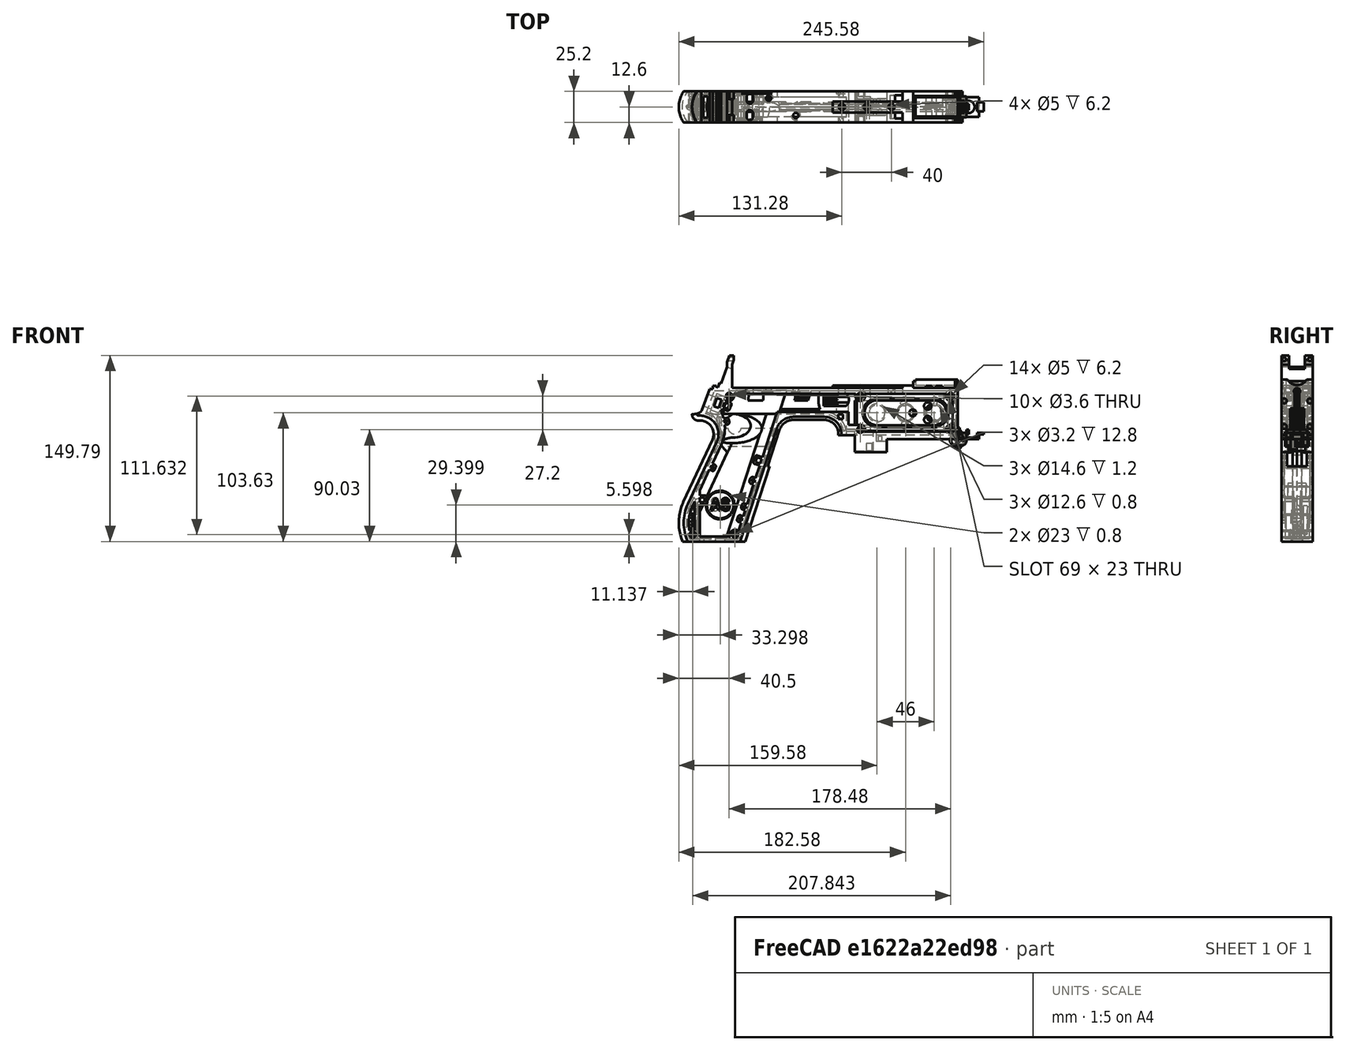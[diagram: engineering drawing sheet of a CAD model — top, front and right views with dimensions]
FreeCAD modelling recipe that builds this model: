
FCSTD DOCUMENT  (FreeCAD 1.1R20260325 (Git shallow))
Label: PICON-OF_ver_68
License: All rights reserved
LicenseURL: https://en.wikipedia.org/wiki/All_rights_reserved
objects: Sketcher::SketchObject×132, Part::Extrusion×66, Part::Cut×51, PartDesign::Pad×34, PartDesign::Pocket×21, PartDesign::Chamfer×15, PartDesign::Body×11, App::Point×11, PartDesign::Fillet×6, Part::MultiFuse×5, Part::Part2DObjectPython×4, PartDesign::SubtractivePipe×4, PartDesign::SubtractiveLoft×4, PartDesign::Plane×3, PartDesign::SubShapeBinder×2, Part::Sweep×1, PartDesign::ShapeBinder×1, Mesh::Feature×1, PartDesign::Point×1, PartDesign::Groove×1
note: 664 computed .brp shape members not serialized (recipe doc carries the construction recipe); baked Part::Feature solids carry a one-line shape summary decoded from their .brp

FEATURE [Sketcher::SketchObject] Sketch  label="corpo principale"
  ArcFitTolerance = 1e-06
  AttacherType = Attacher::AttachEngine3D
  AttachmentSupport = -> [XZ_Plane]
  ExternalTypes = [0]
  FullyConstrained = true
  MakeInternals = false
  MapMode = 5
  Placement = pos=(0,0,0) rot=(1,0,0;1.5708rad)
  _ExternalGeoVersion = 0
  sketch-geometry (65):
    g0: LineSegment StartX=0 StartY=0 StartZ=0 EndX=-57.2 EndY=0 EndZ=0
    g1: LineSegment StartX=-57.2 StartY=0 StartZ=0 EndX=-57.2 EndY=-10.4 EndZ=0
    g2: LineSegment StartX=-57.2 StartY=-10.4 StartZ=0 EndX=-82.8 EndY=-10.4 EndZ=0
    g3: LineSegment StartX=-82.8 StartY=-10.4 StartZ=0 EndX=-82.8 EndY=3.2 EndZ=0
    g4: LineSegment StartX=-82.8 StartY=3.2 StartZ=0 EndX=-93.6 EndY=3.2 EndZ=0
    g5: LineSegment StartX=-93.6 StartY=3.2 StartZ=0 EndX=-93.6 EndY=4 EndZ=0
    g6: LineSegment StartX=-107.6 StartY=18 StartZ=0 EndX=-132.428 EndY=18 EndZ=0
    g7: LineSegment StartX=-145.743 StartY=8.32624 StartZ=0 EndX=-175.232 EndY=-82.4316 EndZ=0
    g8: LineSegment StartX=-175.232 StartY=-82.4316 StartZ=0 EndX=-217.232 EndY=-82.4316 EndZ=0
    g9: LineSegment StartX=-217.232 StartY=-52.1862 StartZ=0 EndX=-193.988 EndY=-2.33927 EndZ=0
    g10: LineSegment StartX=-206.196 StartY=23.0857 StartZ=0 EndX=-199.861 EndY=40.4914 EndZ=0
    g11: LineSegment StartX=-199.861 StartY=40.4914 StartZ=0 EndX=-197.061 EndY=40.4914 EndZ=0
    g12: LineSegment StartX=-197.061 StartY=40.4914 StartZ=0 EndX=-197.061 EndY=42.8914 EndZ=0
    g13: LineSegment StartX=-197.061 StartY=42.8914 StartZ=0 EndX=-194.261 EndY=42.8914 EndZ=0
    g14: LineSegment StartX=-194.261 StartY=42.8914 StartZ=0 EndX=-194.535 EndY=42.1397 EndZ=0
    g15: LineSegment StartX=-194.535 StartY=42.1397 StartZ=0 EndX=-193.031 EndY=41.5924 EndZ=0
    g16: LineSegment StartX=-193.031 StartY=41.5924 StartZ=0 EndX=-191.663 EndY=45.3512 EndZ=0
    g17: LineSegment StartX=-191.663 StartY=45.3512 StartZ=0 EndX=-190.536 EndY=44.9408 EndZ=0
    g18: LineSegment StartX=-190.536 StartY=44.9408 StartZ=0 EndX=-185.747 EndY=58.0965 EndZ=0
    g19: LineSegment StartX=-185.747 StartY=58.0965 StartZ=0 EndX=-185.747 EndY=62.0965 EndZ=0
    g20: LineSegment StartX=-185.747 StartY=62.0965 StartZ=0 EndX=-183.832 EndY=67.3588 EndZ=0
    g21: LineSegment StartX=-183.832 StartY=67.3588 StartZ=0 EndX=-180.232 EndY=67.3588 EndZ=0
    g22: LineSegment StartX=-180.232 StartY=67.3588 StartZ=0 EndX=-180.232 EndY=63.7588 EndZ=0
    g23: LineSegment StartX=-180.232 StartY=63.7588 StartZ=0 EndX=-181.6 EndY=60 EndZ=0
    g24: LineSegment StartX=-181.6 StartY=60 StartZ=0 EndX=-181.6 EndY=41.2 EndZ=0
    g25: LineSegment StartX=-181.6 StartY=41.2 StartZ=0 EndX=-100.8 EndY=41.2 EndZ=0
    g26: LineSegment StartX=-36 StartY=43.2 StartZ=0 EndX=-36 EndY=41.2 EndZ=0
    g27: LineSegment StartX=0 StartY=48 StartZ=0 EndX=0 EndY=0 EndZ=0
    g28: LineSegment StartX=-209.901 StartY=19.85 StartZ=0 EndX=-209.901 EndY=20.1 EndZ=0
    g29: LineSegment StartX=-208.001 StartY=22 StartZ=0 EndX=-207.747 EndY=22 EndZ=0
    g30: LineSegment StartX=-207.583 StartY=19 StartZ=0 EndX=-209.051 EndY=19 EndZ=0
    g31: ArcOfCircle CenterX=-208.001 CenterY=20.1 CenterZ=0 NormalX=0 NormalY=0 NormalZ=1 AngleXU=0 Radius=1.9 StartAngle=1.5708 EndAngle=3.14159
    g32: GeomPoint [constr] X=-209.901 Y=22 Z=0
    g33: ArcOfCircle CenterX=-209.051 CenterY=19.85 CenterZ=0 NormalX=0 NormalY=0 NormalZ=1 AngleXU=0 Radius=0.85 StartAngle=3.14159 EndAngle=4.71239
    g34: GeomPoint [constr] X=-209.901 Y=19 Z=0
    g35: ArcOfCircle CenterX=-207.747 CenterY=23.65 CenterZ=0 NormalX=0 NormalY=0 NormalZ=1 AngleXU=0 Radius=1.65 StartAngle=4.71239 EndAngle=5.93412
    g36: GeomPoint [constr] X=-206.591 Y=22 Z=0
    g37: LineSegment StartX=-4 StartY=6 StartZ=0 EndX=-4 EndY=36.4 EndZ=0
    g38: LineSegment StartX=-4 StartY=36.4 StartZ=0 EndX=-185.2 EndY=36.4 EndZ=0
    g39: LineSegment StartX=-185.2 StartY=36.4 StartZ=0 EndX=-190.441 EndY=22 EndZ=0
    g40: LineSegment StartX=-214.575 StartY=-78.4316 StartZ=0 EndX=-178.142 EndY=-78.4316 EndZ=0
    g41: LineSegment StartX=-178.142 StartY=-78.4316 StartZ=0 EndX=-145.51 EndY=22 EndZ=0
    g42: LineSegment StartX=-145.51 StartY=22 StartZ=0 EndX=-87.91 EndY=22 EndZ=0
    g43: LineSegment StartX=-87.91 StartY=22 StartZ=0 EndX=-87.91 EndY=11.6 EndZ=0
    g44: LineSegment StartX=-87.91 StartY=11.6 StartZ=0 EndX=-80.11 EndY=11.6 EndZ=0
    g45: LineSegment StartX=-80.11 StartY=11.6 StartZ=0 EndX=-80.11 EndY=6 EndZ=0
    g46: LineSegment StartX=-80.11 StartY=6 StartZ=0 EndX=-4 EndY=6 EndZ=0
    g47: LineSegment StartX=-190.363 StartY=-4.02975 StartZ=0 EndX=-213.607 EndY=-53.8767 EndZ=0
    g48: ArcOfCircle CenterX=-132.428 CenterY=4 CenterZ=0 NormalX=0 NormalY=0 NormalZ=1 AngleXU=0 Radius=14 StartAngle=1.5708 EndAngle=2.82743
    g49: GeomPoint [constr] X=-142.6 Y=18 Z=0
    g50: ArcOfCircle CenterX=-107.6 CenterY=4 CenterZ=0 NormalX=0 NormalY=0 NormalZ=1 AngleXU=0 Radius=14 StartAngle=0 EndAngle=1.5708
    g51: GeomPoint [constr] X=-93.6 Y=18 Z=0
    g52: ArcOfCircle CenterX=-184.801 CenterY=-67.3089 CenterZ=0 NormalX=0 NormalY=0 NormalZ=1 AngleXU=0 Radius=35.7833 StartAngle=2.70526 EndAngle=3.57792
    g53: ArcOfCircle CenterX=-207.583 CenterY=4 CenterZ=0 NormalX=0 NormalY=0 NormalZ=1 AngleXU=0 Radius=15 StartAngle=5.84685 EndAngle=7.85398
    g54: LineSegment [constr] StartX=-213.607 StartY=-53.8767 StartZ=0 EndX=-217.232 EndY=-52.1862 EndZ=0
    g55: ArcOfCircle CenterX=-184.801 CenterY=-67.3089 CenterZ=0 NormalX=0 NormalY=0 NormalZ=1 AngleXU=0 Radius=31.7833 StartAngle=2.70526 EndAngle=3.49911
    g56: ArcOfCircle CenterX=-218.095 CenterY=8.90192 CenterZ=0 NormalX=0 NormalY=0 NormalZ=1 AngleXU=0 Radius=30.5989 StartAngle=5.84685 EndAngle=6.72553
    g57: LineSegment StartX=-44.6 StartY=43.2 StartZ=0 EndX=-36 EndY=43.2 EndZ=0
    g58: LineSegment StartX=-100.8 StartY=41.2 StartZ=0 EndX=-44.6 EndY=41.2 EndZ=0
    g59: LineSegment StartX=-44.6 StartY=41.2 StartZ=0 EndX=-44.6 EndY=43.2 EndZ=0
    g60: LineSegment StartX=-2.4 StartY=48 StartZ=0 EndX=0 EndY=48 EndZ=0
    g61: LineSegment StartX=-36 StartY=41.2 StartZ=0 EndX=-2.4 EndY=41.2 EndZ=0
    g62: LineSegment StartX=-2.4 StartY=41.2 StartZ=0 EndX=-2.4 EndY=48 EndZ=0
    g63: LineSegment [constr] StartX=-181.6 StartY=36.4 StartZ=0 EndX=-152.209 EndY=36.4 EndZ=0
    g64: LineSegment [constr] StartX=-181.6 StartY=36.4 StartZ=0 EndX=-130.41 EndY=36.4 EndZ=0
  constraints (183):
    c: Coincident(g-1,g0)
    c: PointOnObject(g0,g-1)
    c: Coincident(g0,g1)
    c: Vertical(g1)
    c: Coincident(g1,g2)
    c: Horizontal(g2)
    c: Coincident(g2,g3)
    c: Vertical(g3)
    c: Coincident(g3,g4)
    c: Coincident(g4,g5)
    c: Vertical(g5)
    c: Horizontal(g6)
    c: Coincident(g7,g8)
    c: Horizontal(g8)
    c: Coincident(g10,g11)
    c: Horizontal(g11)
    c: Coincident(g11,g12)
    c: Vertical(g12)
    c: Coincident(g12,g13)
    c: Horizontal(g13)
    c: Coincident(g13,g14)
    c: Coincident(g14,g15)
    c: Coincident(g15,g16)
    c: Coincident(g16,g17)
    c: Coincident(g17,g18)
    c: Coincident(g18,g19)
    c: Vertical(g19)
    c: Coincident(g19,g20)
    c: Coincident(g20,g21)
    c: Horizontal(g21)
    c: Coincident(g21,g22)
    c: Vertical(g22)
    c: Coincident(g22,g23)
    c: Coincident(g23,g24)
    c: Vertical(g24)
    c: Coincident(g24,g25)
    c: Horizontal(g25)
    c: Coincident(g57,g26)
    c: Vertical(g26)
    c: Coincident(g26,g61)
    c: PointOnObject(g60,g-2)
    c: Coincident(g60,g27)
    c: Coincident(g27,g0)
    c: DistanceY(g27,g27) = 48
    c: DistanceY(g1,g1) = 10.4
    c: DistanceX(g0,g0) = 57.2
    c: DistanceX(g2,g2) = 25.6
    c: Horizontal(g4)
    c: DistanceY(g3,g3) = 13.6
    c: DistanceX(g4,g4) = 10.8
    c: DistanceY(g5,g51) = 14.8
    c: DistanceX(g49,g51) = 49
    c: Distance(g7,g49) = 105.6
    c: DistanceX(g61,g60) = 36
    c: DistanceX(g25,g25) = 80.8
    c: DistanceY(g24,g24) = 18.8
    c: DistanceY(g22,g22) = 3.6
    c: Distance(g23) = 4
    c: Angle(g-1,g23) = 1.22173
    c: DistanceX(g21,g21) = 3.6
    c: Distance(g20) = 5.6
    c: Angle(g-1,g20) = 1.22173
    c: DistanceY(g19,g19) = 4
    c: Distance(g18) = 14
    c: Angle(g-1,g18) = 1.22173
    c: Distance(g17) = 1.2
    c: Distance(g16) = 4
    c: Angle(g16) = 1.22173
    c: Perpendicular(g18,g17)
    c: Distance(g15) = 1.6
    c: Perpendicular(g16,g15)
    c: Distance(g14) = 0.8
    c: DistanceX(g13,g13) = 2.8
    c: Perpendicular(g15,g14)
    c: DistanceY(g12,g12) = 2.4
    c: DistanceX(g11,g11) = 2.8
    c: Distance(g9) = 55
    c: Angle(g9,g-1) = 2.00713
    c: Horizontal(g29)
    c: Vertical(g28)
    c: Horizontal(g30)
    c: PointOnObject(g32,g29)
    c: PointOnObject(g32,g28)
    c: Tangent(g29,g31) = 1.5708
    c: Tangent(g28,g31) = 1.5708
    c: PointOnObject(g34,g28)
    c: PointOnObject(g34,g30)
    c: Tangent(g28,g33) = 1.5708
    c: Tangent(g30,g33) = 1.5708
    c: PointOnObject(g36,g29)
    c: PointOnObject(g36,g10)
    c: Tangent(g29,g35) = -1.5708
    c: Tangent(g10,g35) = -1.5708
    c: Angle(g-1,g10) = 1.22173
    c: Radius(g35) = 1.65
    c: Vertical(g37)
    c: Coincident(g37,g38)
    c: Horizontal(g38)
    c: Coincident(g38,g39)
    c: Horizontal(g40)
    c: Coincident(g40,g41)
    c: Coincident(g41,g42)
    c: Horizontal(g42)
    c: Coincident(g42,g43)
    c: Vertical(g43)
    c: Coincident(g43,g44)
    c: Horizontal(g44)
    c: Coincident(g44,g45)
    c: Vertical(g45)
    c: Coincident(g45,g46)
    c: Coincident(g46,g37)
    c: Horizontal(g46)
    c: DistanceY(g0,g37) = 6
    c: DistanceX(g37,g0) = 4
    c: DistanceY(g37,g25) = 4.8
    c: DistanceX(g38,g38) = 181.2
    c: DistanceX(g42,g42) = 57.6
    c: DistanceY(g49,g41) = 4
    c: DistanceX(g41,g49) = 2.91
    c: DistanceY(g43,g43) = 10.4
    c: DistanceX(g44,g44) = 7.8
    c: DistanceY(g7,g40) = 4
    c: Distance(g47) = 55
    c: Angle(g-1,g39) = 1.22173
    c: PointOnObject(g49,g7)
    c: PointOnObject(g49,g6)
    c: Tangent(g7,g48) = -1.5708
    c: Tangent(g6,g48) = -1.5708
    c: PointOnObject(g51,g5)
    c: PointOnObject(g51,g6)
    c: Tangent(g5,g50) = -1.5708
    c: Tangent(g6,g50) = -1.5708
    c: Radius(g50) = 14
    c: Radius(g48) = 14
    c: DistanceX(g8,g8) = 42
    c: Angle(g7,g-1) = 1.88496
    c: Parallel(g41,g7)
    c: Parallel(g47,g9)
    c: Coincident(g52,g8)
    c: Tangent(g52,g9) = 1.5708
    c: DistanceX(g9,g8) = 0
    c: Tangent(g53,g9) = -1.5708
    c: Tangent(g53,g30) = -1.5708
    c: Diameter(g53) = 30
    c: DistanceY(g53,g0) = -4
    c: Coincident(g54,g47)
    c: Distance(g54) = 4
    c: Coincident(g54,g9)
    c: Coincident(g55,g40)
    c: Tangent(g55,g47) = -1.5708
    c: Coincident(g52,g55)
    c: Coincident(g56,g39)
    c: Tangent(g56,g47) = 1.5708
    c: Horizontal(g57)
    c: DistanceX(g57,g57) = 8.6
    c: Coincident(g58,g25)
    c: Horizontal(g58)
    c: Coincident(g59,g58)
    c: Vertical(g59)
    c: DistanceY(g58,g57) = 2
    c: DistanceX(g58,g58) = 56.2
    c: Coincident(g59,g57)
    c: DistanceY(g41,g36) = 0
    c: DistanceY(g36,g39) = 0
    c: DistanceY(g28,g28) = 0.25
    c: DistanceX(g30,g36) = 2.46
    c: DistanceX(g28,g29) = 1.9
    c: Coincident(g62,g60)
    c: Horizontal(g60)
    c: DistanceX(g62,g27) = 2.4
    c: Coincident(g61,g62)
    c: DistanceY(g26,g26) = 2
    c: Vertical(g62)
    c: DistanceY(g61,g60) = 6.8
    c: Horizontal(g61)
    c: Distance(g63) = 29.391
    c: PointOnObject(g63,g38)
    c: PointOnObject(g63,g38)
    c: Distance(g64) = 51.19
    c: PointOnObject(g64,g38)
    c: PointOnObject(g64,g38)
    c: DistanceX(g24,g63) = 0
    c: DistanceX(g24,g64) = 0
FEATURE [Part::Extrusion] Extrude  label="Extrude corpo principale"
  Base = -> Sketch
  Dir = (0,-1,2e-16)
  DirMode = 2
  FaceMakerClass = Part::FaceMakerBullseye
  FaceMakerMode = 3
  InnerWireTaper = 1
  LengthFwd = 25.2
  LengthRev = 12.6
  Solid = true
  Symmetric = true
FEATURE [Sketcher::SketchObject] Sketch002  label="scavo grilletto"
  ArcFitTolerance = 1e-06
  AttachmentSupport = -> [XZ_Plane]
  ExternalGeometry = -> [Sketch]
  ExternalTypes = [0]
  FullyConstrained = true
  MakeInternals = false
  MapMode = 5
  Placement = pos=(0,0,0) rot=(1,0,0;1.5708rad)
  _ExternalGeoVersion = 0
  sketch-geometry (4):
    g0: LineSegment StartX=-89.51 StartY=22 StartZ=0 EndX=-152.71 EndY=22 EndZ=0
    g1: LineSegment StartX=-152.71 StartY=22 StartZ=0 EndX=-167.006 EndY=-22 EndZ=0
    g2: LineSegment StartX=-167.006 StartY=-22 StartZ=0 EndX=-89.51 EndY=-22 EndZ=0
    g3: LineSegment StartX=-89.51 StartY=-22 StartZ=0 EndX=-89.51 EndY=22 EndZ=0
  constraints (12):
    c: Horizontal(g0)
    c: Coincident(g0,g1)
    c: Coincident(g1,g2)
    c: Horizontal(g2)
    c: Coincident(g2,g3)
    c: Coincident(g3,g0)
    c: Vertical(g3)
    c: Angle(g1,g0) = 1.88496
    c: DistanceY(g3,g3) = 44
    c: DistanceX(g0,g0) = 63.2
    c: DistanceX(g0,g-3) = 1.6
    c: DistanceY(g-3,g0) = 0
FEATURE [Sketcher::SketchObject] Sketch004  label="traiettoria arrotondamento impugnatura anteriore"
  ArcFitTolerance = 1e-06
  AttachmentSupport = -> [XZ_Plane]
  ExternalGeometry = -> [Sketch]
  ExternalTypes = [0]
  FullyConstrained = true
  MakeInternals = false
  MapMode = 5
  Placement = pos=(0,0,0) rot=(1,0,0;1.5708rad)
  _ExternalGeoVersion = 0
  sketch-geometry (13):
    g0: LineSegment StartX=-175.232 StartY=-82.4316 StartZ=0 EndX=-145.743 EndY=8.32624 EndZ=0
    g1: LineSegment StartX=-93.6 StartY=3.2 StartZ=0 EndX=-93.6 EndY=4 EndZ=0
    g2: LineSegment StartX=-132.428 StartY=18 StartZ=0 EndX=-107.6 EndY=18 EndZ=0
    g3: ArcOfCircle CenterX=-132.428 CenterY=4 CenterZ=0 NormalX=0 NormalY=0 NormalZ=1 AngleXU=0 Radius=14 StartAngle=1.5708 EndAngle=2.82743
    g4: ArcOfCircle CenterX=-107.6 CenterY=4 CenterZ=0 NormalX=0 NormalY=0 NormalZ=1 AngleXU=0 Radius=14 StartAngle=0 EndAngle=1.5708
    g5: LineSegment StartX=-175.232 StartY=-82.4316 StartZ=0 EndX=-217.232 EndY=-82.4316 EndZ=0
    g6: LineSegment StartX=-217.232 StartY=-52.1862 StartZ=0 EndX=-193.988 EndY=-2.33927 EndZ=0
    g7: LineSegment StartX=-209.051 StartY=19 StartZ=0 EndX=-207.583 EndY=19 EndZ=0
    g8: LineSegment StartX=-209.901 StartY=20.1 StartZ=0 EndX=-209.901 EndY=19.85 EndZ=0
    g9: ArcOfCircle CenterX=-184.801 CenterY=-67.3089 CenterZ=0 NormalX=0 NormalY=0 NormalZ=1 AngleXU=0 Radius=35.7833 StartAngle=2.70526 EndAngle=3.57792
    g10: ArcOfCircle CenterX=-207.583 CenterY=4 CenterZ=0 NormalX=0 NormalY=0 NormalZ=1 AngleXU=0 Radius=15 StartAngle=5.84685 EndAngle=7.85398
    g11: ArcOfCircle CenterX=-209.051 CenterY=19.85 CenterZ=0 NormalX=0 NormalY=0 NormalZ=1 AngleXU=0 Radius=0.85 StartAngle=3.14159 EndAngle=4.71239
    g12: ArcOfCircle CenterX=-208.001 CenterY=20.1 CenterZ=0 NormalX=0 NormalY=0 NormalZ=1 AngleXU=0 Radius=1.9 StartAngle=1.5708 EndAngle=3.14159
  constraints (26):
    c: Coincident(g0,g-3)
    c: Coincident(g0,g-6)
    c: Coincident(g1,g-8)
    c: Coincident(g1,g-7)
    c: Coincident(g2,g-5)
    c: Coincident(g2,g-4)
    c: Coincident(g3,g2)
    c: Tangent(g3,g0) = 1.5708
    c: Coincident(g4,g1)
    c: Tangent(g4,g2) = 1.5708
    c: Coincident(g5,g0)
    c: Coincident(g5,g-9)
    c: Coincident(g6,g-12)
    c: Coincident(g6,g-11)
    c: Coincident(g7,g-15)
    c: Coincident(g7,g-14)
    c: Coincident(g8,g-16)
    c: Coincident(g8,g-17)
    c: Tangent(g9,g6) = 1.5708
    c: Coincident(g9,g5)
    c: Coincident(g10,g7)
    c: Tangent(g10,g6) = -1.5708
    c: Tangent(g11,g7) = -1.5708
    c: Coincident(g11,g8)
    c: Tangent(g12,g8) = -1.5708
    c: Coincident(g12,g-17)
FEATURE [PartDesign::Plane] DatumPlane  label="Piano per disegno arrotondamento impugnatura"
  AttachmentSupport = -> [Sketch]
  Length = 73.6581
  MapMode = 7
  Placement = pos=(-145.743,1.8e-15,8.32624) rot=(0.154555,0.154555,0.97582;1.59527rad)
  ResizeMode = 0
  Width = 303.511
FEATURE [Sketcher::SketchObject] Sketch005  label="forma arrotondamento impugnatura anteriore"
  ArcFitTolerance = 1e-06
  AttachmentSupport = -> [DatumPlane]
  ExternalTypes = [0]
  FullyConstrained = true
  MakeInternals = false
  MapMode = 5
  Placement = pos=(-145.743,1.8e-15,8.32624) rot=(0.154555,0.154555,0.97582;1.59527rad)
  _ExternalGeoVersion = 0
  sketch-geometry (5):
    g0: GeomPoint [constr] X=0 Y=-4 Z=0
    g1: GeomPoint [constr] X=-12.6 Y=7.1e-15 Z=0
    g2: GeomPoint [constr] X=12.6 Y=4.97e-14 Z=0
    g3: LineSegment StartX=-12.6 StartY=7.1e-15 StartZ=0 EndX=12.6 EndY=4.97e-14 EndZ=0
    g4: ArcOfCircle CenterX=-3.88e-14 CenterY=17.845 CenterZ=0 NormalX=0 NormalY=0 NormalZ=1 AngleXU=0 Radius=21.845 StartAngle=4.09759 EndAngle=5.32718
  constraints (11):
    c: DistanceY(g0,g-1) = 4
    c: DistanceX(g-1,g0) = 0
    c: DistanceX(g1,g-1) = 12.6
    c: DistanceX(g-1,g2) = 12.6
    c: DistanceY(g-1,g2) = 0
    c: DistanceY(g-1,g1) = 0
    c: Coincident(g3,g1)
    c: Coincident(g3,g2)
    c: Coincident(g4,g1)
    c: Coincident(g4,g2)
    c: PointOnObject(g0,g4)
FEATURE [Part::Sweep] Sweep  label="Sweep impugnatura"
  Frenet = true
  Sections = -> [Sketch005]
  Solid = true
  Spine = -> Sketch [Edge32,Edge33,Edge34,Edge35,Edge36,Edge37,Edge38,Edge39,Edge40,Edge41,Edge42,Edge43,Edge44]
  Transition = 1
FEATURE [Sketcher::SketchObject] Sketch008  label="buchi e pulizie varie"
  ArcFitTolerance = 1e-06
  AttachmentSupport = -> [XZ_Plane]
  ExternalGeometry = -> [Sketch]
  ExternalTypes = [0]
  FullyConstrained = true
  MakeInternals = false
  MapMode = 5
  Placement = pos=(0,0,0) rot=(1,0,0;1.5708rad)
  _ExternalGeoVersion = 0
  sketch-geometry (26):
    g0: LineSegment StartX=-96.278 StartY=20.155 StartZ=0 EndX=-92.278 EndY=20.155 EndZ=0
    g1: LineSegment StartX=-92.278 StartY=20.155 StartZ=0 EndX=-92.278 EndY=16.155 EndZ=0
    g2: LineSegment StartX=-92.278 StartY=16.155 StartZ=0 EndX=-96.278 EndY=16.155 EndZ=0
    g3: LineSegment StartX=-96.278 StartY=16.155 StartZ=0 EndX=-96.278 EndY=20.155 EndZ=0
    g4: LineSegment StartX=-222.232 StartY=-82.4316 StartZ=0 EndX=-170.232 EndY=-82.4316 EndZ=0
    g5: LineSegment StartX=-170.232 StartY=-82.4316 StartZ=0 EndX=-170.232 EndY=-86.4316 EndZ=0
    g6: LineSegment StartX=-170.232 StartY=-86.4316 StartZ=0 EndX=-222.232 EndY=-86.4316 EndZ=0
    g7: LineSegment StartX=-222.232 StartY=-86.4316 StartZ=0 EndX=-222.232 EndY=-82.4316 EndZ=0
    g8: LineSegment StartX=-213.901 StartY=20.1 StartZ=0 EndX=-213.901 EndY=26 EndZ=0
    g9: LineSegment StartX=-213.901 StartY=26 StartZ=0 EndX=-206.196 EndY=26 EndZ=0
    g10: LineSegment StartX=-17.4 StartY=42.8 StartZ=0 EndX=-12.4 EndY=42.8 EndZ=0
    g11: LineSegment StartX=-12.4 StartY=42.8 StartZ=0 EndX=-12.4 EndY=41.2 EndZ=0
    g12: LineSegment StartX=-12.4 StartY=41.2 StartZ=0 EndX=-17.4 EndY=41.2 EndZ=0
    g13: LineSegment StartX=-17.4 StartY=41.2 StartZ=0 EndX=-17.4 EndY=42.8 EndZ=0
    g14: LineSegment StartX=-25.9 StartY=42.8 StartZ=0 EndX=-20.9 EndY=42.8 EndZ=0
    g15: LineSegment StartX=-20.9 StartY=42.8 StartZ=0 EndX=-20.9 EndY=41.2 EndZ=0
    g16: LineSegment StartX=-20.9 StartY=41.2 StartZ=0 EndX=-25.9 EndY=41.2 EndZ=0
    g17: LineSegment StartX=-25.9 StartY=41.2 StartZ=0 EndX=-25.9 EndY=42.8 EndZ=0
    g18: GeomPoint [constr] X=-206.196 Y=23.0857 Z=0
    g19: GeomPoint [constr] X=-213.901 Y=20.1 Z=0
    g20: BSplineCurve PolesCount=4 KnotsCount=2 Degree=3 IsPeriodic=0
    g21-g24: Circle [constr] x4 (B-spline internal-alignment scaffolding for g20; pole/knot coordinates omitted)
    g25: LineSegment StartX=-206.196 StartY=26 StartZ=0 EndX=-206.196 EndY=23.0857 EndZ=0
  constraints (73):
    c: Horizontal(g0)
    c: Coincident(g1,g0)
    c: Vertical(g1)
    c: Coincident(g2,g1)
    c: Horizontal(g2)
    c: Coincident(g3,g2)
    c: Coincident(g3,g0)
    c: Vertical(g3)
    c: DistanceX(g0,g-4) = 4.368
    c: DistanceY(g0,g-4) = 1.845
    c: DistanceY(g1,g1) = 4
    c: DistanceX(g2,g2) = 4
    c: Horizontal(g4)
    c: Coincident(g5,g4)
    c: Vertical(g5)
    c: Coincident(g6,g5)
    c: Horizontal(g6)
    c: Coincident(g7,g6)
    c: Coincident(g7,g4)
    c: Vertical(g7)
    c: DistanceY(g7,g7) = 4
    c: DistanceX(g4,g-5) = 5
    c: DistanceX(g-5,g4) = 5
    c: DistanceY(g4,g-5) = 0
    c: Coincident(g9,g8)
    c: Parallel(g9,g-6)
    c: DistanceX(g8,g-8) = 4
    c: Horizontal(g10)
    c: Coincident(g11,g10)
    c: Vertical(g11)
    c: Coincident(g12,g11)
    c: Horizontal(g12)
    c: Coincident(g13,g12)
    c: Coincident(g13,g10)
    c: Vertical(g13)
    c: Horizontal(g14)
    c: Coincident(g15,g14)
    c: Vertical(g15)
    c: Coincident(g16,g15)
    c: Horizontal(g16)
    c: Coincident(g17,g16)
    c: Coincident(g17,g14)
    c: Vertical(g17)
    c: DistanceY(g11,g10) = 1.6
    c: DistanceX(g10,g10) = 5
    c: DistanceY(g15,g14) = 1.6
    c: DistanceX(g14,g14) = 5
    c: DistanceX(g15,g12) = 3.5
    c: DistanceX(g11,g-9) = 10
    c: DistanceY(g-9,g11) = 0
    c: DistanceY(g-9,g15) = 0
    c: Perpendicular(g8,g9)
    c: DistanceY(g-7,g9) = 4
    c: DistanceY(g8,g-8) = 0
    c: InternalAlignment(g18,g20)
    c: InternalAlignment(g19,g20)
    c: InternalAlignment(g21,g20)
    c: Weight(g21) = 1
    c: InternalAlignment(g22,g20)
    c: Equal(g22,g21)
    c: InternalAlignment(g23,g20)
    c: Equal(g23,g21)
    c: InternalAlignment(g24,g20)
    c: Equal(g24,g21)
    c: Coincident(g18,g-12)
    c: Coincident(g19,g8)
    c: Coincident(g25,g9)
    c: Coincident(g25,g20)
    c: Vertical(g25)
    c: DistanceY(g20,g23) = 0
    c: DistanceY(g22,g18) = 2.26
    c: DistanceX(g22,g18) = 0.93
    c: DistanceX(g20,g23) = 2.9
FEATURE [Part::Extrusion] Extrude004  label="Extrude Buchi e pulizie varie"
  Base = -> Sketch008
  Dir = (0,-1,2e-16)
  DirMode = 2
  FaceMakerClass = Part::FaceMakerBullseye
  FaceMakerMode = 3
  InnerWireTaper = 1
  LengthFwd = 25.2
  LengthRev = 0
  Solid = true
  Symmetric = true
FEATURE [Sketcher::SketchObject] Sketch009  label="rinforzi"
  ArcFitTolerance = 1e-06
  AttachmentSupport = -> [XZ_Plane]
  ExternalGeometry = -> [Sketch]
  ExternalTypes = [0]
  FullyConstrained = true
  MakeInternals = false
  MapMode = 5
  Placement = pos=(0,0,0) rot=(1,0,0;1.5708rad)
  _ExternalGeoVersion = 0
  sketch-geometry (9):
    g0: LineSegment StartX=-87.91 StartY=22 StartZ=0 EndX=-87.91 EndY=36.4 EndZ=0
    g1: LineSegment StartX=-87.91 StartY=36.4 StartZ=0 EndX=-97.91 EndY=36.4 EndZ=0
    g2: LineSegment StartX=-97.91 StartY=36.4 StartZ=0 EndX=-97.91 EndY=22 EndZ=0
    g3: LineSegment StartX=-97.91 StartY=22 StartZ=0 EndX=-87.91 EndY=22 EndZ=0
    g4: LineSegment StartX=-149.713 StartY=9.06563 StartZ=0 EndX=-154.586 EndY=-5.93437 EndZ=0
    g5: LineSegment StartX=-154.586 StartY=-5.93437 StartZ=0 EndX=-191.863 EndY=-5.93437 EndZ=0
    g6: LineSegment StartX=-191.863 StartY=-5.93437 StartZ=0 EndX=-191.863 EndY=9.06563 EndZ=0
    g7: LineSegment StartX=-191.863 StartY=9.06563 StartZ=0 EndX=-149.713 EndY=9.06563 EndZ=0
    g8: LineSegment [constr] StartX=-145.51 StartY=22 StartZ=0 EndX=-149.713 EndY=9.06563 EndZ=0
  constraints (25):
    c: Vertical(g0)
    c: Coincident(g1,g0)
    c: Horizontal(g1)
    c: Coincident(g2,g1)
    c: Vertical(g2)
    c: Coincident(g3,g2)
    c: Coincident(g3,g0)
    c: Horizontal(g3)
    c: Coincident(g0,g-4)
    c: DistanceX(g3,g3) = 10
    c: DistanceY(g0,g-3) = 0
    c: Coincident(g5,g4)
    c: Horizontal(g5)
    c: Coincident(g6,g5)
    c: Vertical(g6)
    c: Coincident(g7,g6)
    c: Coincident(g7,g4)
    c: Horizontal(g7)
    c: Distance(g8) = 13.6
    c: Parallel(g-6,g8)
    c: Coincident(g-6,g8)
    c: Parallel(g4,g-6)
    c: DistanceY(g4,g4) = 15
    c: Coincident(g4,g8)
    c: DistanceX(g-5,g5) = -1.5
FEATURE [Part::Extrusion] Extrude001  label="Extrude scavo grilletto"
  Base = -> Sketch002
  Dir = (0,-1,2e-16)
  DirMode = 2
  FaceMakerClass = Part::FaceMakerBullseye
  FaceMakerMode = 3
  InnerWireTaper = 1
  LengthFwd = 16
  LengthRev = 0
  Solid = true
  Symmetric = true
FEATURE [Part::Extrusion] Extrude005  label="Extrude Rinforzi"
  Base = -> Sketch009
  Dir = (0,-1,2e-16)
  DirMode = 2
  FaceMakerClass = Part::FaceMakerBullseye
  FaceMakerMode = 3
  InnerWireTaper = 1
  LengthFwd = 2
  LengthRev = 0
  Placement = pos=(0,12.6,0) rot=(0,0,1;0rad)
  Solid = true
  Symmetric = false
FEATURE [PartDesign::ShapeBinder] CopyCut
  TraceSupport = false
FEATURE [PartDesign::Plane] DatumPlane001
  AttachmentSupport = -> [CopyCut]
  Length = 283.944
  MapMode = 5
  Placement = pos=(0,12.6,0) rot=(0,0.707107,0.707107;3.14159rad)
  ResizeMode = 0
  Width = 188.15
FEATURE [Sketcher::SketchObject] Sketch010  label="buco neopixel"
  ArcFitTolerance = 1e-06
  AttachmentSupport = -> [XZ_Plane]
  ExternalGeometry = -> [Sketch]
  ExternalTypes = [0]
  FullyConstrained = true
  MakeInternals = false
  MapMode = 5
  Placement = pos=(0,0,0) rot=(1,0,0;1.5708rad)
  _ExternalGeoVersion = 0
  sketch-geometry (5):
    g0: LineSegment [constr] StartX=-199.861 StartY=40.4914 StartZ=0 EndX=-201.368 EndY=36.3521 EndZ=0
    g1: LineSegment StartX=-201.368 StartY=36.3521 StartZ=0 EndX=-204.932 EndY=26.5605 EndZ=0
    g2: LineSegment StartX=-201.368 StartY=36.3521 StartZ=0 EndX=-180.2 EndY=28.6477 EndZ=0
    g3: LineSegment StartX=-180.2 StartY=28.6477 StartZ=0 EndX=-183.764 EndY=18.8561 EndZ=0
    g4: LineSegment StartX=-183.764 StartY=18.8561 StartZ=0 EndX=-204.932 EndY=26.5605 EndZ=0
  constraints (14):
    c: Parallel(g0,g-3)
    c: Distance(g0) = 4.405
    c: Coincident(g0,g-3)
    c: Coincident(g2,g1)
    c: Coincident(g3,g2)
    c: Coincident(g4,g3)
    c: Coincident(g4,g1)
    c: Parallel(g1,g-3)
    c: Distance(g1) = 10.42
    c: Coincident(g1,g0)
    c: Parallel(g2,g4)
    c: Perpendicular(g1,g2)
    c: DistanceX(g-4,g2) = 5
    c: Parallel(g3,g1)
FEATURE [Part::Extrusion] Extrude006  label="Extrude buco neopixel"
  Base = -> Sketch010
  Dir = (0,-1,2e-16)
  DirMode = 2
  FaceMakerClass = Part::FaceMakerBullseye
  FaceMakerMode = 3
  InnerWireTaper = 1
  LengthFwd = 17.2
  LengthRev = 0
  Solid = true
  Symmetric = true
FEATURE [Sketcher::SketchObject] Sketch011  label="fermo grilletto"
  ArcFitTolerance = 1e-06
  AttachmentSupport = -> [XZ_Plane]
  ExternalGeometry = -> [Sketch]
  ExternalTypes = [0]
  FullyConstrained = true
  MakeInternals = false
  MapMode = 5
  Placement = pos=(0,0,0) rot=(1,0,0;1.5708rad)
  _ExternalGeoVersion = 0
  sketch-geometry (18):
    g0: LineSegment [constr] StartX=-145.51 StartY=22 StartZ=0 EndX=-157.347 EndY=-14.4293 EndZ=0
    g1: LineSegment [constr] StartX=-157.347 StartY=-14.4293 StartZ=0 EndX=-157.841 EndY=-15.951 EndZ=0
    g2: LineSegment StartX=-161.151 StartY=-13.1932 StartZ=0 EndX=-155.825 EndY=-14.9237 EndZ=0
    g3: LineSegment StartX=-163.167 StartY=-14.2205 StartZ=0 EndX=-164.403 EndY=-18.0247 EndZ=0
    g4: LineSegment StartX=-163.376 StartY=-20.0408 StartZ=0 EndX=-158.05 EndY=-21.7713 EndZ=0
    g5: LineSegment StartX=-158.05 StartY=-21.7713 StartZ=0 EndX=-155.825 EndY=-14.9237 EndZ=0
    g6: LineSegment StartX=-161.645 StartY=-14.7149 StartZ=0 EndX=-157.841 EndY=-15.951 EndZ=0
    g7: LineSegment StartX=-157.841 StartY=-15.951 StartZ=0 EndX=-159.077 EndY=-19.7552 EndZ=0
    g8: LineSegment StartX=-159.077 StartY=-19.7552 StartZ=0 EndX=-162.881 EndY=-18.5191 EndZ=0
    g9: LineSegment StartX=-162.881 StartY=-18.5191 StartZ=0 EndX=-161.645 EndY=-14.7149 EndZ=0
    g10: LineSegment [constr] StartX=-161.645 StartY=-14.7149 StartZ=0 EndX=-161.151 EndY=-13.1932 EndZ=0
    g11: LineSegment [constr] StartX=-159.077 StartY=-19.7552 StartZ=0 EndX=-157.555 EndY=-20.2496 EndZ=0
    g12: LineSegment [constr] StartX=-159.077 StartY=-19.7552 StartZ=0 EndX=-159.572 EndY=-21.2769 EndZ=0
    g13: LineSegment [constr] StartX=-161.645 StartY=-14.7149 StartZ=0 EndX=-163.167 EndY=-14.2205 EndZ=0
    g14: ArcOfCircle CenterX=-161.645 CenterY=-14.7149 CenterZ=0 NormalX=0 NormalY=0 NormalZ=1 AngleXU=0 Radius=1.6 StartAngle=1.25664 EndAngle=2.82743
    g15: GeomPoint [constr] X=-162.673 Y=-12.6988 Z=0
    g16: ArcOfCircle CenterX=-162.881 CenterY=-18.5191 CenterZ=0 NormalX=0 NormalY=0 NormalZ=1 AngleXU=0 Radius=1.6 StartAngle=2.82743 EndAngle=4.39823
    g17: GeomPoint [constr] X=-164.897 Y=-19.5464 Z=0
  constraints (48):
    c: Parallel(g0,g-3)
    c: Distance(g0) = 38.304
    c: Coincident(g0,g-3)
    c: Parallel(g1,g-3)
    c: Distance(g1) = 1.6
    c: Coincident(g1,g0)
    c: Coincident(g5,g4)
    c: Coincident(g5,g2)
    c: Coincident(g7,g6)
    c: Coincident(g8,g7)
    c: Coincident(g9,g8)
    c: Coincident(g9,g6)
    c: Parallel(g7,g-3)
    c: Parallel(g9,g7)
    c: Perpendicular(g6,g7)
    c: Parallel(g6,g8)
    c: Distance(g6) = 4
    c: Distance(g9) = 4
    c: Parallel(g5,g7)
    c: Parallel(g9,g3)
    c: Parallel(g2,g6)
    c: Parallel(g4,g8)
    c: Parallel(g13,g6)
    c: Parallel(g10,g9)
    c: Parallel(g11,g8)
    c: Parallel(g12,g7)
    c: Distance(g10) = 1.6
    c: Distance(g13) = 1.6
    c: Distance(g12) = 1.6
    c: Distance(g11) = 1.6
    c: Coincident(g10,g6)
    c: Coincident(g13,g6)
    c: Coincident(g12,g7)
    c: Coincident(g11,g7)
    c: Distance(g10,g15) = 1.6
    c: Distance(g15,g13) = 1.6
    c: Distance(g4,g12) = 1.6
    c: Distance(g4,g11) = 1.6
    c: PointOnObject(g15,g2)
    c: Tangent(g3,g14) = -1.5708
    c: Tangent(g2,g14) = 1.5708
    c: PointOnObject(g17,g4)
    c: PointOnObject(g17,g3)
    c: Tangent(g4,g16) = -1.5708
    c: Tangent(g3,g16) = -1.5708
    c: Equal(g16,g14)
    c: Coincident(g16,g8)
    c: Coincident(g6,g1)
FEATURE [Part::Extrusion] Extrude007  label="Extrude fermo grilletto"
  Base = -> Sketch011
  Dir = (0,-1,2e-16)
  DirMode = 2
  FaceMakerClass = Part::FaceMakerBullseye
  FaceMakerMode = 3
  InnerWireTaper = 1
  LengthFwd = 25.2
  LengthRev = 0
  Solid = true
  Symmetric = true
FEATURE [Sketcher::SketchObject] Sketch012  label="buco oled"
  ArcFitTolerance = 1e-06
  AttachmentSupport = -> [XZ_Plane]
  ExternalGeometry = -> [Sketch]
  ExternalTypes = [0]
  FullyConstrained = true
  MakeInternals = false
  MapMode = 5
  Placement = pos=(0,0,0) rot=(1,0,0;1.5708rad)
  _ExternalGeoVersion = 0
  sketch-geometry (4):
    g0: LineSegment StartX=-185.747 StartY=58.0965 StartZ=0 EndX=-180.232 EndY=56.0891 EndZ=0
    g1: LineSegment StartX=-185.747 StartY=58.0965 StartZ=0 EndX=-185.747 EndY=67.3588 EndZ=0
    g2: LineSegment StartX=-185.747 StartY=67.3588 StartZ=0 EndX=-180.232 EndY=67.3588 EndZ=0
    g3: LineSegment StartX=-180.232 StartY=67.3588 StartZ=0 EndX=-180.232 EndY=56.0891 EndZ=0
  constraints (10):
    c: Coincident(g1,g0)
    c: Coincident(g2,g1)
    c: Coincident(g3,g2)
    c: Coincident(g3,g0)
    c: Parallel(g1,g-5)
    c: Perpendicular(g-3,g0)
    c: Parallel(g2,g-6)
    c: Parallel(g3,g-4)
    c: Coincident(g0,g-5)
    c: Coincident(g2,g-6)
FEATURE [Part::Extrusion] Extrude008  label="Extrude buco oled"
  Base = -> Sketch012
  Dir = (0,-1,2e-16)
  DirMode = 2
  FaceMakerClass = Part::FaceMakerBullseye
  FaceMakerMode = 3
  InnerWireTaper = 1
  LengthFwd = 12.8
  LengthRev = 0
  Solid = true
  Symmetric = true
FEATURE [Sketcher::SketchObject] Sketch013  label="buco pompa"
  ArcFitTolerance = 1e-06
  AttachmentSupport = -> [XZ_Plane]
  ExternalGeometry = -> [Sketch]
  ExternalTypes = [0]
  FullyConstrained = true
  MakeInternals = false
  MapMode = 5
  Placement = pos=(0,0,0) rot=(1,0,0;1.5708rad)
  _ExternalGeoVersion = 0
  sketch-geometry (8):
    g0: LineSegment StartX=-82.8 StartY=-10.4 StartZ=0 EndX=-82.8 EndY=-9.6 EndZ=0
    g1: LineSegment StartX=-82.8 StartY=-9.6 StartZ=0 EndX=-67.9 EndY=-9.6 EndZ=0
    g2: LineSegment StartX=-67.9 StartY=-9.6 StartZ=0 EndX=-67.9 EndY=6 EndZ=0
    g3: LineSegment StartX=-67.9 StartY=6 StartZ=0 EndX=-65.9 EndY=6 EndZ=0
    g4: LineSegment StartX=-65.9 StartY=6 StartZ=0 EndX=-65.9 EndY=-1.7 EndZ=0
    g5: LineSegment StartX=-65.9 StartY=-1.7 StartZ=0 EndX=-57.2 EndY=-1.7 EndZ=0
    g6: LineSegment StartX=-57.2 StartY=-1.7 StartZ=0 EndX=-57.2 EndY=-10.4 EndZ=0
    g7: LineSegment StartX=-57.2 StartY=-10.4 StartZ=0 EndX=-82.8 EndY=-10.4 EndZ=0
  constraints (22):
    c: Vertical(g0)
    c: Coincident(g1,g0)
    c: Horizontal(g1)
    c: Coincident(g2,g1)
    c: Vertical(g2)
    c: Coincident(g3,g2)
    c: Horizontal(g3)
    c: Coincident(g4,g3)
    c: Vertical(g4)
    c: Coincident(g5,g4)
    c: Horizontal(g5)
    c: Coincident(g6,g5)
    c: Vertical(g6)
    c: Coincident(g7,g6)
    c: Coincident(g7,g0)
    c: DistanceY(g0,g0) = 0.8
    c: DistanceY(g6,g6) = 8.7
    c: DistanceX(g1,g1) = 14.9
    c: DistanceX(g3,g3) = 2
    c: Coincident(g0,g-4)
    c: DistanceY(g2,g-6) = 0
    c: Coincident(g6,g-5)
FEATURE [Part::Extrusion] Extrude009  label="Extrude buco pompa"
  Base = -> Sketch013
  Dir = (0,-1,2e-16)
  DirMode = 2
  FaceMakerClass = Part::FaceMakerBullseye
  FaceMakerMode = 3
  InnerWireTaper = 1
  LengthFwd = 13.2
  LengthRev = 0
  Solid = true
  Symmetric = true
FEATURE [Sketcher::SketchObject] Sketch014  label="buco frontale"
  ArcFitTolerance = 1e-06
  AttachmentSupport = -> [XZ_Plane]
  ExternalGeometry = -> [Sketch]
  ExternalTypes = [0]
  FullyConstrained = true
  MakeInternals = false
  MapMode = 5
  Placement = pos=(0,0,0) rot=(1,0,0;1.5708rad)
  _ExternalGeoVersion = 0
  sketch-geometry (10):
    g0: LineSegment StartX=0 StartY=0 StartZ=0 EndX=0 EndY=24.671 EndZ=0
    g1: LineSegment StartX=0 StartY=24.671 StartZ=0 EndX=-4 EndY=24.671 EndZ=0
    g2: LineSegment StartX=-4 StartY=24.671 StartZ=0 EndX=-4 EndY=16 EndZ=0
    g3: LineSegment StartX=-4 StartY=16 StartZ=0 EndX=-2.4 EndY=16 EndZ=0
    g4: LineSegment StartX=-2.4 StartY=16 StartZ=0 EndX=-2.4 EndY=10 EndZ=0
    g5: LineSegment StartX=-2.4 StartY=10 StartZ=0 EndX=-12 EndY=10 EndZ=0
    g6: LineSegment StartX=-12 StartY=10 StartZ=0 EndX=-12 EndY=6 EndZ=0
    g7: LineSegment StartX=-12 StartY=6 StartZ=0 EndX=-2.4 EndY=6 EndZ=0
    g8: LineSegment StartX=-2.4 StartY=6 StartZ=0 EndX=-2.4 EndY=0 EndZ=0
    g9: LineSegment StartX=-2.4 StartY=0 StartZ=0 EndX=0 EndY=0 EndZ=0
  constraints (29):
    c: Vertical(g0)
    c: Coincident(g1,g0)
    c: Horizontal(g1)
    c: Coincident(g2,g1)
    c: Vertical(g2)
    c: Coincident(g3,g2)
    c: Horizontal(g3)
    c: Coincident(g4,g3)
    c: Vertical(g4)
    c: Coincident(g5,g4)
    c: Horizontal(g5)
    c: Coincident(g6,g5)
    c: Vertical(g6)
    c: Coincident(g7,g6)
    c: Coincident(g8,g7)
    c: Vertical(g8)
    c: Coincident(g9,g8)
    c: Coincident(g9,g0)
    c: Horizontal(g9)
    c: DistanceY(g0,g0) = 24.671
    c: Horizontal(g7)
    c: DistanceY(g6,g6) = 4
    c: DistanceY(g4,g4) = 6
    c: DistanceX(g9,g9) = 2.4
    c: Coincident(g0,g-1)
    c: DistanceY(g-3,g7) = 0
    c: DistanceX(g8,g4) = 0
    c: DistanceX(g-3,g1) = 0
    c: DistanceX(g6,g-3) = 8
FEATURE [Part::Extrusion] Extrude010  label="Extrude buco frontale"
  Base = -> Sketch014
  Dir = (0,-1,2e-16)
  DirMode = 2
  FaceMakerClass = Part::FaceMakerBullseye
  FaceMakerMode = 3
  InnerWireTaper = 1
  LengthFwd = 11.2
  LengthRev = 0
  Solid = true
  Symmetric = true
FEATURE [Sketcher::SketchObject] Sketch015  label="guida rail"
  ArcFitTolerance = 1e-06
  AttachmentSupport = -> [XZ_Plane]
  ExternalGeometry = -> [Sketch]
  ExternalTypes = [0]
  FullyConstrained = true
  MakeInternals = false
  MapMode = 5
  Placement = pos=(0,0,0) rot=(1,0,0;1.5708rad)
  _ExternalGeoVersion = 0
  sketch-geometry (4):
    g0: LineSegment StartX=-100.8 StartY=43.2 StartZ=0 EndX=-44.6 EndY=43.2 EndZ=0
    g1: LineSegment StartX=-44.6 StartY=43.2 StartZ=0 EndX=-44.6 EndY=41.2 EndZ=0
    g2: LineSegment StartX=-44.6 StartY=41.2 StartZ=0 EndX=-100.8 EndY=41.2 EndZ=0
    g3: LineSegment StartX=-100.8 StartY=41.2 StartZ=0 EndX=-100.8 EndY=43.2 EndZ=0
  constraints (9):
    c: Horizontal(g0)
    c: Coincident(g1,g0)
    c: Coincident(g2,g1)
    c: Coincident(g3,g2)
    c: Coincident(g3,g0)
    c: Vertical(g3)
    c: Coincident(g2,g-3)
    c: Coincident(g1,g-3)
    c: Coincident(g0,g-4)
FEATURE [Part::Extrusion] Extrude011  label="Extrude guida rail"
  Base = -> Sketch015
  Dir = (0,-1,2e-16)
  DirMode = 2
  FaceMakerClass = Part::FaceMakerBullseye
  FaceMakerMode = 3
  InnerWireTaper = 1
  LengthFwd = 9
  LengthRev = 0
  Solid = true
  Symmetric = true
FEATURE [Sketcher::SketchObject] Sketch016  label="guide per coperture laterali"
  ArcFitTolerance = 1e-06
  AttachmentSupport = -> [XZ_Plane]
  ExternalGeometry = -> [Sketch]
  ExternalTypes = [0]
  FullyConstrained = true
  MakeInternals = false
  MapMode = 5
  Placement = pos=(0,0,0) rot=(1,0,0;1.5708rad)
  _ExternalGeoVersion = 0
  sketch-geometry (14):
    g0: Circle CenterX=-5.6 CenterY=7.6 CenterZ=0 NormalX=0 NormalY=0 NormalZ=1 AngleXU=0 Radius=1.6
    g1: Circle CenterX=-5.6 CenterY=7.6 CenterZ=0 NormalX=0 NormalY=0 NormalZ=1 AngleXU=0 Radius=4
    g2: Circle CenterX=-5.6 CenterY=34.8 CenterZ=0 NormalX=0 NormalY=0 NormalZ=1 AngleXU=0 Radius=1.6
    g3: Circle CenterX=-5.6 CenterY=34.8 CenterZ=0 NormalX=0 NormalY=0 NormalZ=1 AngleXU=0 Radius=4
    g4: Circle CenterX=-184.08 CenterY=34.8 CenterZ=0 NormalX=0 NormalY=0 NormalZ=1 AngleXU=0 Radius=1.6
    g5: Circle CenterX=-184.08 CenterY=34.8 CenterZ=0 NormalX=0 NormalY=0 NormalZ=1 AngleXU=0 Radius=4
    g6: Circle CenterX=-179.305 CenterY=-76.8316 CenterZ=0 NormalX=0 NormalY=0 NormalZ=1 AngleXU=0 Radius=1.6
    g7: Circle CenterX=-179.305 CenterY=-76.8316 CenterZ=0 NormalX=0 NormalY=0 NormalZ=1 AngleXU=0 Radius=4
    g8: Circle CenterX=-213.443 CenterY=-76.8316 CenterZ=0 NormalX=0 NormalY=0 NormalZ=1 AngleXU=0 Radius=1.6
    g9: Circle CenterX=-213.443 CenterY=-76.8316 CenterZ=0 NormalX=0 NormalY=0 NormalZ=1 AngleXU=0 Radius=4
    g10: Circle CenterX=-78.51 CenterY=7.6 CenterZ=0 NormalX=0 NormalY=0 NormalZ=1 AngleXU=0 Radius=1.6
    g11: Circle CenterX=-78.51 CenterY=7.6 CenterZ=0 NormalX=0 NormalY=0 NormalZ=1 AngleXU=0 Radius=4
    g12: Circle CenterX=-78.51 CenterY=34.8 CenterZ=0 NormalX=0 NormalY=0 NormalZ=1 AngleXU=0 Radius=1.6
    g13: Circle CenterX=-78.51 CenterY=34.8 CenterZ=0 NormalX=0 NormalY=0 NormalZ=1 AngleXU=0 Radius=4
  constraints (35):
    c: Diameter(g0) = 3.2
    c: Diameter(g1) = 8
    c: Coincident(g0,g1)
    c: Diameter(g2) = 3.2
    c: Diameter(g3) = 8
    c: Coincident(g3,g2)
    c: Tangent(g2,g-7)
    c: Diameter(g4) = 3.2
    c: Diameter(g5) = 8
    c: Coincident(g5,g4)
    c: Tangent(g4,g-7)
    c: Tangent(g4,g-8)
    c: Diameter(g6) = 3.2
    c: Diameter(g7) = 8
    c: Coincident(g7,g6)
    c: Tangent(g6,g-9)
    c: Tangent(g6,g-10)
    c: Diameter(g8) = 3.2
    c: Diameter(g9) = 8
    c: Coincident(g9,g8)
    c: Tangent(g8,g-10)
    c: Tangent(g8,g-11)
    c: Diameter(g10) = 3.2
    c: Diameter(g11) = 8
    c: Diameter(g12) = 3.2
    c: Diameter(g13) = 8
    c: Coincident(g12,g13)
    c: Coincident(g10,g11)
    c: Tangent(g12,g-7)
    c: DistanceX(g12,g10) = 0
    c: Tangent(g2,g-6)
    c: Tangent(g0,g-6)
    c: Tangent(g0,g-3)
    c: Tangent(g10,g-3)
    c: Tangent(g10,g-4)
FEATURE [Part::Extrusion] Extrude012  label="extrude guide per coperture laterali"
  Base = -> Sketch016
  Dir = (0,-1,2e-16)
  DirMode = 2
  FaceMakerClass = Part::FaceMakerBullseye
  FaceMakerMode = 3
  InnerWireTaper = 1
  LengthFwd = 25.2
  LengthRev = 0
  Solid = true
  Symmetric = true
FEATURE [Sketcher::SketchObject] Sketch017  label="supporto CAM"
  ArcFitTolerance = 1e-06
  AttachmentSupport = -> [XZ_Plane]
  ExternalGeometry = -> [Sketch]
  ExternalTypes = [0]
  FullyConstrained = true
  MakeInternals = false
  MapMode = 5
  Placement = pos=(0,0,0) rot=(1,0,0;1.5708rad)
  _ExternalGeoVersion = 0
  sketch-geometry (6):
    g0: LineSegment StartX=-2.4 StartY=48 StartZ=0 EndX=-2.4 EndY=41.2 EndZ=0
    g1: LineSegment StartX=-2.4 StartY=48 StartZ=0 EndX=-34 EndY=48 EndZ=0
    g2: LineSegment StartX=-34 StartY=48 StartZ=0 EndX=-34 EndY=46.72 EndZ=0
    g3: LineSegment StartX=-34 StartY=46.72 StartZ=0 EndX=-36 EndY=46.72 EndZ=0
    g4: LineSegment StartX=-36 StartY=46.72 StartZ=0 EndX=-36 EndY=41.2 EndZ=0
    g5: LineSegment StartX=-36 StartY=41.2 StartZ=0 EndX=-2.4 EndY=41.2 EndZ=0
  constraints (15):
    c: Coincident(g1,g0)
    c: Horizontal(g1)
    c: Coincident(g2,g1)
    c: Vertical(g2)
    c: Coincident(g3,g2)
    c: Horizontal(g3)
    c: Coincident(g4,g3)
    c: Coincident(g5,g4)
    c: DistanceX(g1,g0) = 31.6
    c: Coincident(g5,g0)
    c: Vertical(g4)
    c: DistanceY(g2,g1) = 1.28
    c: Coincident(g0,g-3)
    c: Coincident(g0,g-3)
    c: Coincident(g4,g-4)
FEATURE [Part::Extrusion] Extrude013  label="Extrude supporto CAM"
  Base = -> Sketch017
  Dir = (0,-1,2e-16)
  DirMode = 2
  FaceMakerClass = Part::FaceMakerBullseye
  FaceMakerMode = 3
  InnerWireTaper = 1
  LengthFwd = 17.8
  LengthRev = 0
  Solid = true
  Symmetric = true
FEATURE [Sketcher::SketchObject] Sketch018  label="Scavo CAM"
  ArcFitTolerance = 1e-06
  AttachmentSupport = -> [YZ_Plane]
  ExternalGeometry = -> [Sketch]
  ExternalTypes = [0]
  FullyConstrained = true
  MakeInternals = false
  MapMode = 5
  Placement = pos=(0,0,0) rot=(0.57735,0.57735,0.57735;2.0944rad)
  _ExternalGeoVersion = 0
  sketch-geometry (4):
    g0: LineSegment StartX=-7.73 StartY=48 StartZ=0 EndX=7.73 EndY=48 EndZ=0
    g1: LineSegment [constr] StartX=1.07e-14 StartY=48 StartZ=0 EndX=0 EndY=43.5155 EndZ=0
    g2: ArcOfCircle CenterX=9e-15 CenterY=52.42 CenterZ=0 NormalX=0 NormalY=0 NormalZ=1 AngleXU=0 Radius=8.90445 StartAngle=3.66102 EndAngle=5.76376
    g3: Circle [constr] CenterX=9e-15 CenterY=52.42 CenterZ=0 NormalX=0 NormalY=0 NormalZ=1 AngleXU=0 Radius=8.9
  constraints (13):
    c: Horizontal(g0)
    c: DistanceY(g-3,g0) = 0
    c: DistanceX(g0,g0) = 15.46
    c: DistanceX(g0,g-3) = 7.73
    c: DistanceX(g-3) = 0
    c: Coincident(g1,g-3)
    c: PointOnObject(g1,g-2)
    c: Coincident(g2,g0)
    c: Coincident(g2,g0)
    c: PointOnObject(g1,g2)
    c: Diameter(g3) = 17.8
    c: DistanceY(g1,g3) = 4.42
    c: Coincident(g2,g3)
FEATURE [Part::Extrusion] Extrude014  label="Extrude Scavo CAM"
  Base = -> Sketch018
  Dir = (1,0,0)
  DirMode = 2
  FaceMakerClass = Part::FaceMakerBullseye
  FaceMakerMode = 3
  InnerWireTaper = 1
  LengthFwd = -34
  LengthRev = 0
  Solid = true
  Symmetric = false
FEATURE [Sketcher::SketchObject] Sketch019  label="scavo rumble"
  ArcFitTolerance = 1e-06
  AttachmentSupport = -> [XZ_Plane]
  ExternalGeometry = -> [Sketch]
  ExternalTypes = [0]
  FullyConstrained = true
  MakeInternals = false
  MapMode = 5
  Placement = pos=(0,0,0) rot=(1,0,0;1.5708rad)
  _ExternalGeoVersion = 0
  sketch-geometry (6):
    g0: LineSegment StartX=-168.716 StartY=-37.1227 StartZ=0 EndX=-163.58 EndY=-38.7914 EndZ=0
    g1: LineSegment StartX=-163.58 StartY=-38.7914 StartZ=0 EndX=-170.687 EndY=-60.6657 EndZ=0
    g2: LineSegment StartX=-170.687 StartY=-60.6657 StartZ=0 EndX=-175.823 EndY=-58.997 EndZ=0
    g3: LineSegment StartX=-175.823 StartY=-58.997 StartZ=0 EndX=-168.716 EndY=-37.1227 EndZ=0
    g4: LineSegment [constr] StartX=-145.51 StartY=22 StartZ=0 EndX=-165.102 EndY=-38.297 EndZ=0
    g5: LineSegment [constr] StartX=-163.58 StartY=-38.7914 StartZ=0 EndX=-165.102 EndY=-38.297 EndZ=0
  constraints (17):
    c: Coincident(g1,g0)
    c: Coincident(g2,g1)
    c: Coincident(g3,g2)
    c: Coincident(g3,g0)
    c: Parallel(g3,g-3)
    c: Parallel(g3,g1)
    c: Perpendicular(g3,g0)
    c: Perpendicular(g2,g3)
    c: Distance(g2,g0) = 23
    c: Parallel(g4,g-3)
    c: Distance(g4) = 63.4
    c: Coincident(g4,g-3)
    c: Parallel(g5,g0)
    c: Coincident(g5,g0)
    c: Coincident(g5,g4)
    c: Distance(g4,g0) = 3.8
    c: Distance(g4,g0) = 1.6
FEATURE [Part::Extrusion] Extrude015  label="scavo rumble001"
  Base = -> Sketch019
  Dir = (0,-1,2e-16)
  DirMode = 2
  FaceMakerClass = Part::FaceMakerBullseye
  FaceMakerMode = 3
  InnerWireTaper = 1
  LengthFwd = 21
  LengthRev = 0
  Solid = true
  Symmetric = true
FEATURE [Sketcher::SketchObject] Sketch020  label="fermo rumble"
  ArcFitTolerance = 1e-06
  AttachmentSupport = -> [XZ_Plane]
  ExternalGeometry = -> [Sketch019,Sketch]
  ExternalTypes = [0]
  FullyConstrained = true
  MakeInternals = false
  MapMode = 5
  Placement = pos=(0,0,0) rot=(1,0,0;1.5708rad)
  _ExternalGeoVersion = 0
  sketch-geometry (16):
    g0: LineSegment [constr] StartX=-170.849 StartY=-55.9866 StartZ=0 EndX=-172.209 EndY=-60.1713 EndZ=0
    g1: LineSegment [constr] StartX=-172.209 StartY=-60.1713 StartZ=0 EndX=-170.687 EndY=-60.6657 EndZ=0
    g2: LineSegment StartX=-172.262 StartY=-53.2145 StartZ=0 EndX=-170.17 EndY=-53.8943 EndZ=0
    g3: LineSegment StartX=-170.17 StartY=-53.8943 StartZ=0 EndX=-170.849 EndY=-55.9866 EndZ=0
    g4: LineSegment StartX=-170.849 StartY=-55.9866 StartZ=0 EndX=-172.942 EndY=-55.3068 EndZ=0
    g5: LineSegment StartX=-172.942 StartY=-55.3068 StartZ=0 EndX=-172.262 EndY=-53.2145 EndZ=0
    g6: LineSegment StartX=-171.767 StartY=-51.6928 StartZ=0 EndX=-168.344 EndY=-52.8052 EndZ=0
    g7: LineSegment StartX=-168.344 StartY=-52.8052 StartZ=0 EndX=-169.951 EndY=-57.7507 EndZ=0
    g8: LineSegment StartX=-169.951 StartY=-57.7507 StartZ=0 EndX=-173.374 EndY=-56.6383 EndZ=0
    g9: LineSegment StartX=-174.402 StartY=-54.6222 StartZ=0 EndX=-173.784 EndY=-52.72 EndZ=0
    g10: LineSegment [constr] StartX=-173.784 StartY=-52.72 StartZ=0 EndX=-173.289 EndY=-51.1984 EndZ=0
    g11: LineSegment [constr] StartX=-173.289 StartY=-51.1984 StartZ=0 EndX=-171.767 EndY=-51.6928 EndZ=0
    g12: ArcOfCircle CenterX=-172.88 CenterY=-55.1166 CenterZ=0 NormalX=0 NormalY=0 NormalZ=1 AngleXU=0 Radius=1.6 StartAngle=2.82743 EndAngle=4.39823
    g13: GeomPoint [constr] X=-174.896 Y=-56.1438 Z=0
    g14: ArcOfCircle CenterX=-172.262 CenterY=-53.2145 CenterZ=0 NormalX=0 NormalY=0 NormalZ=1 AngleXU=0 Radius=1.6 StartAngle=1.25664 EndAngle=2.82743
    g15: GeomPoint [constr] X=-173.289 Y=-51.1984 Z=0
  constraints (42):
    c: Parallel(g0,g-4)
    c: Distance(g0) = 4.4
    c: Coincident(g1,g0)
    c: Perpendicular(g0,g1)
    c: Distance(g1) = 1.6
    c: Coincident(g1,g-5)
    c: Coincident(g3,g2)
    c: Coincident(g4,g3)
    c: Coincident(g5,g4)
    c: Coincident(g5,g2)
    c: Parallel(g3,g-4)
    c: Parallel(g3,g5)
    c: Perpendicular(g2,g3)
    c: Parallel(g4,g2)
    c: Distance(g2) = 2.2
    c: Distance(g3) = 2.2
    c: Coincident(g7,g6)
    c: Coincident(g8,g7)
    c: Parallel(g7,g-4)
    c: Parallel(g7,g9)
    c: Perpendicular(g6,g7)
    c: Parallel(g6,g8)
    c: Distance(g6,g15) = 5.2
    c: Distance(g7) = 5.2
    c: Coincident(g11,g10)
    c: Parallel(g10,g9)
    c: Parallel(g11,g6)
    c: Distance(g10) = 1.6
    c: Distance(g11) = 1.6
    c: Coincident(g10,g15)
    c: Distance(g11,g2) = 1.6
    c: Distance(g2,g10) = 1.6
    c: PointOnObject(g13,g8)
    c: PointOnObject(g13,g9)
    c: Tangent(g8,g12) = 1.5708
    c: Tangent(g9,g12) = 1.5708
    c: PointOnObject(g15,g9)
    c: Tangent(g6,g14) = 1.5708
    c: Tangent(g9,g14) = 1.5708
    c: Equal(g12,g14)
    c: Coincident(g6,g11)
    c: Coincident(g3,g0)
FEATURE [Part::Extrusion] Extrude016  label="Extrude fermo rumble"
  Base = -> Sketch020
  Dir = (0,-1,2e-16)
  DirMode = 2
  FaceMakerClass = Part::FaceMakerBullseye
  FaceMakerMode = 3
  InnerWireTaper = 1
  LengthFwd = 25.2
  LengthRev = 0
  Solid = true
  Symmetric = true
FEATURE [Sketcher::SketchObject] Sketch021  label="perno fermo rumble001"
  ArcFitTolerance = 1e-06
  AttachmentSupport = -> [XZ_Plane001]
  ExternalTypes = [0]
  FullyConstrained = true
  MakeInternals = false
  MapMode = 5
  Placement = pos=(0,0,0) rot=(1,0,0;1.5708rad)
  _ExternalGeoVersion = 0
  sketch-geometry (16):
    g0: LineSegment StartX=0 StartY=0.45 StartZ=0 EndX=0 EndY=1.55 EndZ=0
    g1: LineSegment StartX=0.45 StartY=2 StartZ=0 EndX=1.55 EndY=2 EndZ=0
    g2: LineSegment StartX=2 StartY=1.55 StartZ=0 EndX=2 EndY=0.45 EndZ=0
    g3: LineSegment StartX=1.55 StartY=0 StartZ=0 EndX=0.45 EndY=0 EndZ=0
    g4: ArcOfCircle [constr] CenterX=0.45 CenterY=1.55 CenterZ=0 NormalX=0 NormalY=0 NormalZ=1 AngleXU=0 Radius=0.45 StartAngle=1.5708 EndAngle=3.14159
    g5: GeomPoint [constr] X=0 Y=2 Z=0
    g6: LineSegment StartX=0.45 StartY=2 StartZ=0 EndX=0 EndY=1.55 EndZ=0
    g7: ArcOfCircle [constr] CenterX=1.55 CenterY=1.55 CenterZ=0 NormalX=0 NormalY=0 NormalZ=1 AngleXU=0 Radius=0.45 StartAngle=0 EndAngle=1.5708
    g8: GeomPoint [constr] X=2 Y=2 Z=0
    g9: LineSegment StartX=2 StartY=1.55 StartZ=0 EndX=1.55 EndY=2 EndZ=0
    g10: ArcOfCircle [constr] CenterX=1.55 CenterY=0.45 CenterZ=0 NormalX=0 NormalY=0 NormalZ=1 AngleXU=0 Radius=0.45 StartAngle=4.71239 EndAngle=6.28319
    g11: GeomPoint [constr] X=2 Y=0 Z=0
    g12: LineSegment StartX=1.55 StartY=0 StartZ=0 EndX=2 EndY=0.45 EndZ=0
    g13: ArcOfCircle [constr] CenterX=0.45 CenterY=0.45 CenterZ=0 NormalX=0 NormalY=0 NormalZ=1 AngleXU=0 Radius=0.45 StartAngle=3.14159 EndAngle=4.71239
    g14: GeomPoint [constr] X=0 Y=0 Z=0
    g15: LineSegment StartX=0 StartY=0.45 StartZ=0 EndX=0.45 EndY=0 EndZ=0
  constraints (35):
    c: Coincident(g14,g-1)
    c: PointOnObject(g5,g-2)
    c: Horizontal(g1)
    c: Vertical(g2)
    c: Horizontal(g3)
    c: DistanceX(g5,g8) = 2
    c: DistanceY(g11,g8) = 2
    c: PointOnObject(g5,g0)
    c: PointOnObject(g5,g1)
    c: Tangent(g0,g4) = 1.5708
    c: Tangent(g1,g4) = 1.5708
    c: Coincident(g6,g0)
    c: Coincident(g6,g1)
    c: PointOnObject(g8,g2)
    c: PointOnObject(g8,g1)
    c: Tangent(g2,g7) = 1.5708
    c: Tangent(g1,g7) = 1.5708
    c: Coincident(g9,g2)
    c: Coincident(g9,g1)
    c: PointOnObject(g11,g2)
    c: PointOnObject(g11,g3)
    c: Tangent(g2,g10) = 1.5708
    c: Tangent(g3,g10) = 1.5708
    c: Coincident(g12,g2)
    c: Coincident(g12,g3)
    c: PointOnObject(g14,g0)
    c: PointOnObject(g14,g3)
    c: Tangent(g0,g13) = 1.5708
    c: Tangent(g3,g13) = 1.5708
    c: Coincident(g15,g0)
    c: Coincident(g15,g3)
    c: Equal(g6,g9)
    c: Equal(g9,g12)
    c: Equal(g12,g15)
    c: DistanceX(g14,g3) = 0.45
FEATURE [Sketcher::SketchObject] Sketch022  label="fori per M3x5(OD)x6(L)"
  ArcFitTolerance = 1e-06
  AttachmentSupport = -> [XZ_Plane]
  ExternalGeometry = -> [Sketch016]
  ExternalTypes = [0]
  FullyConstrained = true
  MakeInternals = false
  MapMode = 5
  Placement = pos=(0,0,0) rot=(1,0,0;1.5708rad)
  _ExternalGeoVersion = 0
  sketch-geometry (7):
    g0: Circle CenterX=-5.6 CenterY=34.8 CenterZ=0 NormalX=0 NormalY=0 NormalZ=1 AngleXU=0 Radius=2.5
    g1: Circle CenterX=-5.6 CenterY=7.6 CenterZ=0 NormalX=0 NormalY=0 NormalZ=1 AngleXU=0 Radius=2.5
    g2: Circle CenterX=-78.51 CenterY=34.8 CenterZ=0 NormalX=0 NormalY=0 NormalZ=1 AngleXU=0 Radius=2.5
    g3: Circle CenterX=-78.51 CenterY=7.6 CenterZ=0 NormalX=0 NormalY=0 NormalZ=1 AngleXU=0 Radius=2.5
    g4: Circle CenterX=-184.08 CenterY=34.8 CenterZ=0 NormalX=0 NormalY=0 NormalZ=1 AngleXU=0 Radius=2.5
    g5: Circle CenterX=-179.305 CenterY=-76.8316 CenterZ=0 NormalX=0 NormalY=0 NormalZ=1 AngleXU=0 Radius=2.5
    g6: Circle CenterX=-213.443 CenterY=-76.8316 CenterZ=0 NormalX=0 NormalY=0 NormalZ=1 AngleXU=0 Radius=2.5
  constraints (14):
    c: Diameter(g0) = 5
    c: Diameter(g1) = 5
    c: Diameter(g2) = 5
    c: Diameter(g3) = 5
    c: Diameter(g4) = 5
    c: Diameter(g5) = 5
    c: Diameter(g6) = 5
    c: Coincident(g0,g-8)
    c: Coincident(g1,g-9)
    c: Coincident(g2,g-6)
    c: Coincident(g3,g-7)
    c: Coincident(g4,g-5)
    c: Coincident(g5,g-4)
    c: Coincident(g6,g-3)
FEATURE [Part::Extrusion] Extrude018  label="Extrude fori M3x5x6 - dx"
  Base = -> Sketch022
  Dir = (0,-1,2e-16)
  DirMode = 2
  FaceMakerClass = Part::FaceMakerBullseye
  FaceMakerMode = 3
  InnerWireTaper = 1
  LengthFwd = 6.2
  LengthRev = 0
  Placement = pos=(0,-9.5,0) rot=(0,0,1;0rad)
  Solid = true
  Symmetric = true
FEATURE [Part::Extrusion] Extrude019  label="Extrude fori M3x5x6 - sx"
  Base = -> Sketch022
  Dir = (0,-1,2e-16)
  DirMode = 2
  FaceMakerClass = Part::FaceMakerBullseye
  FaceMakerMode = 3
  InnerWireTaper = 1
  LengthFwd = 6.2
  LengthRev = 0
  Placement = pos=(0,9.5,0) rot=(0,0,1;0rad)
  Solid = true
  Symmetric = true
FEATURE [Sketcher::SketchObject] Sketch023  label="foro anteriore M3x5x6"
  ArcFitTolerance = 1e-06
  AttachmentSupport = -> [YZ_Plane]
  ExternalTypes = [0]
  FullyConstrained = true
  MakeInternals = false
  MapMode = 5
  Placement = pos=(0,0,0) rot=(0.57735,0.57735,0.57735;2.0944rad)
  _ExternalGeoVersion = 0
  sketch-geometry (2):
    g0: LineSegment [constr] StartX=0 StartY=0 StartZ=0 EndX=0 EndY=38.6 EndZ=0
    g1: Circle CenterX=0 CenterY=38.6 CenterZ=0 NormalX=0 NormalY=0 NormalZ=1 AngleXU=0 Radius=2.5
  constraints (5):
    c: Coincident(g0,g-1)
    c: PointOnObject(g0,g-2)
    c: DistanceY(g0,g0) = 38.6
    c: Diameter(g1) = 5
    c: Coincident(g1,g0)
FEATURE [Part::Extrusion] Extrude020  label="Extrude foro anteriore M3x5x6"
  Base = -> Sketch023
  Dir = (1,0,0)
  DirMode = 2
  FaceMakerClass = Part::FaceMakerBullseye
  FaceMakerMode = 3
  InnerWireTaper = 1
  LengthFwd = -6.2
  LengthRev = 0
  Solid = true
  Symmetric = false
FEATURE [Sketcher::SketchObject] Sketch024  label="fori per viti frontale"
  ArcFitTolerance = 1e-06
  AttachmentSupport = -> [YZ_Plane]
  ExternalTypes = [0]
  FullyConstrained = true
  MakeInternals = false
  MapMode = 5
  Placement = pos=(0,0,0) rot=(0.57735,0.57735,0.57735;2.0944rad)
  _ExternalGeoVersion = 0
  sketch-geometry (9):
    g0: LineSegment [constr] StartX=-10.3 StartY=30.721 StartZ=0 EndX=10.3 EndY=30.721 EndZ=0
    g1: LineSegment [constr] StartX=10.3 StartY=30.721 StartZ=0 EndX=10.3 EndY=10.121 EndZ=0
    g2: LineSegment [constr] StartX=10.3 StartY=10.121 StartZ=0 EndX=-10.3 EndY=10.121 EndZ=0
    g3: LineSegment [constr] StartX=-10.3 StartY=10.121 StartZ=0 EndX=-10.3 EndY=30.721 EndZ=0
    g4: LineSegment [constr] StartX=0 StartY=0 StartZ=0 EndX=0 EndY=10.121 EndZ=0
    g5: Circle CenterX=-10.3 CenterY=30.721 CenterZ=0 NormalX=0 NormalY=0 NormalZ=1 AngleXU=0 Radius=2
    g6: Circle CenterX=10.3 CenterY=30.721 CenterZ=0 NormalX=0 NormalY=0 NormalZ=1 AngleXU=0 Radius=2
    g7: Circle CenterX=-10.3 CenterY=10.121 CenterZ=0 NormalX=0 NormalY=0 NormalZ=1 AngleXU=0 Radius=2
    g8: Circle CenterX=10.3 CenterY=10.121 CenterZ=0 NormalX=0 NormalY=0 NormalZ=1 AngleXU=0 Radius=2
  constraints (22):
    c: Horizontal(g0)
    c: Coincident(g1,g0)
    c: Vertical(g1)
    c: Coincident(g2,g1)
    c: Horizontal(g2)
    c: Coincident(g3,g2)
    c: Coincident(g3,g0)
    c: Vertical(g3)
    c: DistanceX(g0,g0) = 20.6
    c: DistanceY(g3,g3) = 20.6
    c: Coincident(g4,g-1)
    c: PointOnObject(g4,g-2)
    c: DistanceY(g4,g4) = 10.121
    c: Symmetric(g2,g2,g4)
    c: Diameter(g5) = 4
    c: Diameter(g6) = 4
    c: Diameter(g7) = 4
    c: Diameter(g8) = 4
    c: Coincident(g5,g0)
    c: Coincident(g6,g0)
    c: Coincident(g7,g2)
    c: Coincident(g8,g1)
FEATURE [Part::Extrusion] Extrude021  label="Extrude fori per viti frontale"
  Base = -> Sketch024
  Dir = (1,0,0)
  DirMode = 2
  FaceMakerClass = Part::FaceMakerBullseye
  FaceMakerMode = 3
  InnerWireTaper = 1
  LengthFwd = -2.4
  LengthRev = 0
  Solid = true
  Symmetric = false
FEATURE [Sketcher::SketchObject] Sketch025  label="foro per filo CAM"
  ArcFitTolerance = 1e-06
  AttachmentSupport = -> [XZ_Plane]
  ExternalGeometry = -> [Sketch]
  ExternalTypes = [0]
  FullyConstrained = true
  MakeInternals = false
  MapMode = 5
  Placement = pos=(0,0,0) rot=(1,0,0;1.5708rad)
  _ExternalGeoVersion = 0
  sketch-geometry (4):
    g0: LineSegment StartX=-44.6 StartY=41.2 StartZ=0 EndX=-44.6 EndY=36.4 EndZ=0
    g1: LineSegment StartX=-44.6 StartY=36.4 StartZ=0 EndX=-54.6 EndY=36.4 EndZ=0
    g2: LineSegment StartX=-54.6 StartY=36.4 StartZ=0 EndX=-50.4 EndY=41.2 EndZ=0
    g3: LineSegment StartX=-50.4 StartY=41.2 StartZ=0 EndX=-44.6 EndY=41.2 EndZ=0
  constraints (11):
    c: Vertical(g0)
    c: Coincident(g1,g0)
    c: Horizontal(g1)
    c: Coincident(g2,g1)
    c: Coincident(g3,g2)
    c: Coincident(g3,g0)
    c: Horizontal(g3)
    c: Coincident(g0,g-3)
    c: DistanceY(g0,g-4) = 0
    c: DistanceX(g3,g3) = 5.8
    c: DistanceX(g1,g1) = 10
FEATURE [Part::Extrusion] Extrude022  label="Extrude foro per filo CAM dx"
  Base = -> Sketch025
  Dir = (0,-1,2e-16)
  DirMode = 2
  FaceMakerClass = Part::FaceMakerBullseye
  FaceMakerMode = 3
  InnerWireTaper = 1
  LengthFwd = 4.9
  LengthRev = 0
  Placement = pos=(0,6.95,0) rot=(0,0,1;0rad)
  Solid = true
  Symmetric = true
FEATURE [Part::Extrusion] Extrude023  label="Extrude foro per filo CAM sx"
  Base = -> Sketch025
  Dir = (0,-1,2e-16)
  DirMode = 2
  FaceMakerClass = Part::FaceMakerBullseye
  FaceMakerMode = 3
  InnerWireTaper = 1
  LengthFwd = 4.9
  LengthRev = 0
  Placement = pos=(0,-6.95,0) rot=(0,0,1;0rad)
  Solid = true
  Symmetric = true
FEATURE [Sketcher::SketchObject] Sketch026  label="foro sotto anteriore M3x5x6"
  ArcFitTolerance = 1e-06
  AttachmentSupport = -> [XY_Plane]
  ExternalTypes = [0]
  FullyConstrained = true
  MakeInternals = false
  MapMode = 5
  _ExternalGeoVersion = 0
  sketch-geometry (2):
    g0: LineSegment [constr] StartX=0 StartY=0 StartZ=0 EndX=-16.5 EndY=0 EndZ=0
    g1: Circle CenterX=-16.5 CenterY=0 CenterZ=0 NormalX=0 NormalY=0 NormalZ=1 AngleXU=0 Radius=2.5
  constraints (5):
    c: Distance(g0) = 16.5
    c: Coincident(g0,g-1)
    c: PointOnObject(g0,g-1)
    c: Diameter(g1) = 5
    c: Coincident(g0,g1)
FEATURE [Sketcher::SketchObject] Sketch027  label="foro sotto posteriore M3x5x6"
  ArcFitTolerance = 1e-06
  AttachmentSupport = -> [XY_Plane]
  ExternalGeometry = -> [Sketch]
  ExternalTypes = [0]
  FullyConstrained = true
  MakeInternals = false
  MapMode = 5
  _ExternalGeoVersion = 0
  sketch-geometry (2):
    g0: LineSegment [constr] StartX=-82.8 StartY=2e-16 StartZ=0 EndX=-71.3 EndY=2e-16 EndZ=0
    g1: Circle CenterX=-71.3 CenterY=2e-16 CenterZ=0 NormalX=0 NormalY=0 NormalZ=1 AngleXU=0 Radius=2.5
  constraints (5):
    c: Distance(g0) = 11.5
    c: Coincident(g0,g-3)
    c: PointOnObject(g0,g-3)
    c: Diameter(g1) = 5
    c: Coincident(g1,g0)
FEATURE [Sketcher::SketchObject] Sketch029  label="fori sotto impugnatura"
  ArcFitTolerance = 1e-06
  AttachmentSupport = -> [XY_Plane]
  ExternalGeometry = -> [Sketch]
  ExternalTypes = [0]
  FullyConstrained = true
  MakeInternals = false
  MapMode = 5
  _ExternalGeoVersion = 0
  sketch-geometry (15):
    g0: LineSegment [constr] StartX=-175.232 StartY=-1.83e-14 StartZ=0 EndX=-191.232 EndY=0 EndZ=0
    g1: Circle CenterX=-191.232 CenterY=0 CenterZ=0 NormalX=0 NormalY=0 NormalZ=1 AngleXU=0 Radius=3.95
    g2: LineSegment [constr] StartX=-175.232 StartY=-1.83e-14 StartZ=0 EndX=-204.275 EndY=0 EndZ=0
    g3: LineSegment StartX=-204.275 StartY=3.525 StartZ=0 EndX=-204.275 EndY=-3.525 EndZ=0
    g4: LineSegment StartX=-205.4 StartY=-4.65 StartZ=0 EndX=-206.65 EndY=-4.65 EndZ=0
    g5: LineSegment StartX=-207.775 StartY=-3.525 StartZ=0 EndX=-207.775 EndY=3.525 EndZ=0
    g6: LineSegment StartX=-206.65 StartY=4.65 StartZ=0 EndX=-205.4 EndY=4.65 EndZ=0
    g7: ArcOfCircle CenterX=-206.65 CenterY=3.525 CenterZ=0 NormalX=0 NormalY=0 NormalZ=1 AngleXU=0 Radius=1.125 StartAngle=1.5708 EndAngle=3.14159
    g8: GeomPoint [constr] X=-207.775 Y=4.65 Z=0
    g9: ArcOfCircle CenterX=-205.4 CenterY=3.525 CenterZ=0 NormalX=0 NormalY=0 NormalZ=1 AngleXU=0 Radius=1.125 StartAngle=0 EndAngle=1.5708
    g10: GeomPoint [constr] X=-204.275 Y=4.65 Z=0
    g11: ArcOfCircle CenterX=-205.4 CenterY=-3.525 CenterZ=0 NormalX=0 NormalY=0 NormalZ=1 AngleXU=0 Radius=1.125 StartAngle=4.71239 EndAngle=6.28319
    g12: GeomPoint [constr] X=-204.275 Y=-4.65 Z=0
    g13: ArcOfCircle CenterX=-206.65 CenterY=-3.525 CenterZ=0 NormalX=0 NormalY=0 NormalZ=1 AngleXU=0 Radius=1.125 StartAngle=3.14159 EndAngle=4.71239
    g14: GeomPoint [constr] X=-207.775 Y=-4.65 Z=0
  constraints (35):
    c: Distance(g0) = 16
    c: Coincident(g0,g-3)
    c: PointOnObject(g0,g-1)
    c: Diameter(g1) = 7.9
    c: Coincident(g1,g0)
    c: Coincident(g2,g0)
    c: PointOnObject(g2,g-1)
    c: Vertical(g3)
    c: Horizontal(g4)
    c: Vertical(g5)
    c: Horizontal(g6)
    c: DistanceY(g12,g10) = 9.3
    c: DistanceX(g8,g10) = 3.5
    c: Symmetric(g10,g12,g2)
    c: PointOnObject(g8,g5)
    c: PointOnObject(g8,g6)
    c: Tangent(g5,g7) = 1.5708
    c: Tangent(g6,g7) = 1.5708
    c: PointOnObject(g10,g3)
    c: PointOnObject(g10,g6)
    c: Tangent(g3,g9) = 1.5708
    c: Tangent(g6,g9) = 1.5708
    c: PointOnObject(g12,g3)
    c: PointOnObject(g12,g4)
    c: Tangent(g3,g11) = 1.5708
    c: Tangent(g4,g11) = 1.5708
    c: PointOnObject(g14,g4)
    c: PointOnObject(g14,g5)
    c: Tangent(g4,g13) = 1.5708
    c: Tangent(g5,g13) = 1.5708
    c: Equal(g7,g9)
    c: Equal(g9,g11)
    c: Equal(g11,g13)
    c: DistanceX(g6,g6) = 1.25
    c: DistanceX(g-5,g5) = 6.8
FEATURE [Sketcher::SketchObject] Sketch030  label="fori superiori per solenoide e oled"
  ArcFitTolerance = 1e-06
  AttachmentSupport = -> [XY_Plane]
  ExternalGeometry = -> [Sketch]
  ExternalTypes = [0]
  FullyConstrained = true
  MakeInternals = false
  MapMode = 5
  _ExternalGeoVersion = 0
  sketch-geometry (33):
    g0: LineSegment [constr] StartX=-181.6 StartY=1.12e-14 StartZ=0 EndX=-169.91 EndY=0 EndZ=0
    g1: LineSegment [constr] StartX=-169.91 StartY=0 StartZ=0 EndX=-169.91 EndY=-2.6 EndZ=0
    g2: LineSegment [constr] StartX=-169.91 StartY=0 StartZ=0 EndX=-169.91 EndY=2.6 EndZ=0
    g3: LineSegment StartX=-169.91 StartY=4.975 StartZ=0 EndX=-169.91 EndY=8.225 EndZ=0
    g4: LineSegment StartX=-167.535 StartY=10.6 StartZ=0 EndX=-167.285 EndY=10.6 EndZ=0
    g5: LineSegment StartX=-164.91 StartY=8.225 StartZ=0 EndX=-164.91 EndY=4.975 EndZ=0
    g6: LineSegment StartX=-167.285 StartY=2.6 StartZ=0 EndX=-167.535 EndY=2.6 EndZ=0
    g7: LineSegment StartX=-169.91 StartY=-4.975 StartZ=0 EndX=-169.91 EndY=-8.225 EndZ=0
    g8: LineSegment StartX=-167.535 StartY=-10.6 StartZ=0 EndX=-167.285 EndY=-10.6 EndZ=0
    g9: LineSegment StartX=-164.91 StartY=-8.225 StartZ=0 EndX=-164.91 EndY=-4.975 EndZ=0
    g10: LineSegment StartX=-167.285 StartY=-2.6 StartZ=0 EndX=-167.535 EndY=-2.6 EndZ=0
    g11: ArcOfCircle CenterX=-167.535 CenterY=8.225 CenterZ=0 NormalX=0 NormalY=0 NormalZ=1 AngleXU=0 Radius=2.375 StartAngle=1.5708 EndAngle=3.14159
    g12: GeomPoint [constr] X=-169.91 Y=10.6 Z=0
    g13: ArcOfCircle CenterX=-167.285 CenterY=8.225 CenterZ=0 NormalX=0 NormalY=0 NormalZ=1 AngleXU=0 Radius=2.375 StartAngle=0 EndAngle=1.5708
    g14: GeomPoint [constr] X=-164.91 Y=10.6 Z=0
    g15: ArcOfCircle CenterX=-167.285 CenterY=4.975 CenterZ=0 NormalX=0 NormalY=0 NormalZ=1 AngleXU=0 Radius=2.375 StartAngle=4.71239 EndAngle=6.28319
    g16: GeomPoint [constr] X=-164.91 Y=2.6 Z=0
    g17: ArcOfCircle CenterX=-167.535 CenterY=4.975 CenterZ=0 NormalX=0 NormalY=0 NormalZ=1 AngleXU=0 Radius=2.375 StartAngle=3.14159 EndAngle=4.71239
    g18: GeomPoint [constr] X=-169.91 Y=2.6 Z=0
    g19: ArcOfCircle CenterX=-167.535 CenterY=-4.975 CenterZ=0 NormalX=0 NormalY=0 NormalZ=1 AngleXU=0 Radius=2.375 StartAngle=1.5708 EndAngle=3.14159
    g20: GeomPoint [constr] X=-169.91 Y=-2.6 Z=0
    g21: ArcOfCircle CenterX=-167.285 CenterY=-4.975 CenterZ=0 NormalX=0 NormalY=0 NormalZ=1 AngleXU=0 Radius=2.375 StartAngle=0 EndAngle=1.5708
    g22: GeomPoint [constr] X=-164.91 Y=-2.6 Z=0
    g23: ArcOfCircle CenterX=-167.285 CenterY=-8.225 CenterZ=0 NormalX=0 NormalY=0 NormalZ=1 AngleXU=0 Radius=2.375 StartAngle=4.71239 EndAngle=6.28319
    g24: GeomPoint [constr] X=-164.91 Y=-10.6 Z=0
    g25: ArcOfCircle CenterX=-167.535 CenterY=-8.225 CenterZ=0 NormalX=0 NormalY=0 NormalZ=1 AngleXU=0 Radius=2.375 StartAngle=3.14159 EndAngle=4.71239
    g26: GeomPoint [constr] X=-169.91 Y=-10.6 Z=0
    g27: LineSegment [constr] StartX=-181.6 StartY=1.12e-14 StartZ=0 EndX=-152.209 EndY=0 EndZ=0
    g28: LineSegment [constr] StartX=-181.6 StartY=1.12e-14 StartZ=0 EndX=-130.41 EndY=0 EndZ=0
    g29: LineSegment [constr] StartX=-152.209 StartY=0 StartZ=0 EndX=-152.209 EndY=6.95 EndZ=0
    g30: LineSegment [constr] StartX=-130.41 StartY=0 StartZ=0 EndX=-130.41 EndY=-6.95 EndZ=0
    g31: Circle CenterX=-152.209 CenterY=6.95 CenterZ=0 NormalX=0 NormalY=0 NormalZ=1 AngleXU=0 Radius=2.1
    g32: Circle CenterX=-130.41 CenterY=-6.95 CenterZ=0 NormalX=0 NormalY=0 NormalZ=1 AngleXU=0 Radius=2.1
  constraints (79):
    c: Distance(g0) = 11.69
    c: PointOnObject(g0,g-1)
    c: Coincident(g-4,g0)
    c: Distance(g1) = 2.6
    c: Coincident(g1,g0)
    c: Vertical(g1)
    c: Distance(g2) = 2.6
    c: Coincident(g2,g0)
    c: Vertical(g2)
    c: Distance(g18,g12) = 8
    c: Coincident(g18,g2)
    c: Vertical(g3)
    c: Distance(g14,g12) = 5
    c: Horizontal(g4)
    c: Distance(g16,g14) = 8
    c: Vertical(g5)
    c: Distance(g26,g20) = 8
    c: Coincident(g20,g1)
    c: Vertical(g7)
    c: Distance(g26,g24) = 5
    c: Horizontal(g8)
    c: Distance(g24,g22) = 8
    c: Vertical(g9)
    c: PointOnObject(g12,g3)
    c: PointOnObject(g12,g4)
    c: Tangent(g3,g11) = 1.5708
    c: Tangent(g4,g11) = 1.5708
    c: PointOnObject(g14,g5)
    c: PointOnObject(g14,g4)
    c: Tangent(g5,g13) = 1.5708
    c: Tangent(g4,g13) = 1.5708
    c: PointOnObject(g16,g5)
    c: PointOnObject(g16,g6)
    c: Tangent(g5,g15) = 1.5708
    c: Tangent(g6,g15) = 1.5708
    c: PointOnObject(g18,g3)
    c: PointOnObject(g18,g6)
    c: Tangent(g3,g17) = 1.5708
    c: Tangent(g6,g17) = 1.5708
    c: Equal(g11,g13)
    c: Equal(g13,g15)
    c: Equal(g15,g17)
    c: DistanceX(g4,g4) = 0.25
    c: PointOnObject(g20,g7)
    c: PointOnObject(g20,g10)
    c: Tangent(g7,g19) = -1.5708
    c: Tangent(g10,g19) = -1.5708
    c: PointOnObject(g22,g9)
    c: PointOnObject(g22,g10)
    c: Tangent(g9,g21) = -1.5708
    c: Tangent(g10,g21) = -1.5708
    c: PointOnObject(g24,g9)
    c: PointOnObject(g24,g8)
    c: Tangent(g9,g23) = -1.5708
    c: Tangent(g8,g23) = -1.5708
    c: PointOnObject(g26,g8)
    c: PointOnObject(g26,g7)
    c: Tangent(g8,g25) = -1.5708
    c: Tangent(g7,g25) = -1.5708
    c: Equal(g19,g21)
    c: Equal(g21,g23)
    c: Equal(g23,g25)
    c: DistanceX(g10,g10) = 0.25
    c: Distance(g27) = 29.391
    c: Coincident(g27,g0)
    c: PointOnObject(g27,g-1)
    c: Distance(g28) = 51.19
    c: Coincident(g28,g0)
    c: PointOnObject(g28,g-1)
    c: Distance(g29) = 6.95
    c: Coincident(g29,g27)
    c: Vertical(g29)
    c: Distance(g30) = 6.95
    c: Coincident(g30,g28)
    c: Vertical(g30)
    c: Diameter(g31) = 4.2
    c: Diameter(g32) = 4.2
    c: Coincident(g32,g30)
    c: Coincident(g31,g29)
FEATURE [Sketcher::SketchObject] Sketch031  label="fori inferiori switch pompa"
  ArcFitTolerance = 1e-06
  AttachmentSupport = -> [XY_Plane]
  ExternalGeometry = -> [Sketch]
  ExternalTypes = [0]
  FullyConstrained = true
  MakeInternals = false
  MapMode = 5
  _ExternalGeoVersion = 0
  sketch-geometry (4):
    g0: LineSegment [constr] StartX=-57.2 StartY=1.9e-15 StartZ=0 EndX=-62.45 EndY=1.9e-15 EndZ=0
    g1: LineSegment [constr] StartX=-62.45 StartY=3.25 StartZ=0 EndX=-62.45 EndY=-3.25 EndZ=0
    g2: Circle CenterX=-62.45 CenterY=3.25 CenterZ=0 NormalX=0 NormalY=0 NormalZ=1 AngleXU=0 Radius=1.6
    g3: Circle CenterX=-62.45 CenterY=-3.25 CenterZ=0 NormalX=0 NormalY=0 NormalZ=1 AngleXU=0 Radius=1.6
  constraints (10):
    c: Distance(g0) = 5.25
    c: Coincident(g0,g-3)
    c: PointOnObject(g0,g-3)
    c: Vertical(g1)
    c: DistanceY(g1,g1) = 6.5
    c: Symmetric(g1,g1,g0)
    c: Diameter(g2) = 3.2
    c: Diameter(g3) = 3.2
    c: Coincident(g2,g1)
    c: Coincident(g3,g1)
FEATURE [Sketcher::SketchObject] Sketch032  label="spazio per PILA 18650"
  ArcFitTolerance = 1e-06
  AttachmentSupport = -> [XY_Plane]
  ExternalGeometry = -> [Sketch]
  ExternalTypes = [0]
  FullyConstrained = true
  MakeInternals = false
  MapMode = 5
  _ExternalGeoVersion = 0
  sketch-geometry (2):
    g0: LineSegment [constr] StartX=-178.142 StartY=-1.74e-14 StartZ=0 EndX=-191.142 EndY=-1.83e-14 EndZ=0
    g1: Circle CenterX=-191.142 CenterY=-1.83e-14 CenterZ=0 NormalX=0 NormalY=0 NormalZ=1 AngleXU=0 Radius=10.5
  constraints (5):
    c: Distance(g0) = 13
    c: Coincident(g0,g-3)
    c: PointOnObject(g0,g-4)
    c: Diameter(g1) = 21
    c: Coincident(g1,g0)
FEATURE [Part::Extrusion] Extrude030  label="Extrude spazio per PILA 18650"
  Base = -> Sketch032
  Dir = (0,0,1)
  DirLink = -> Sketch [Edge45]
  DirMode = 2
  FaceMakerClass = Part::FaceMakerBullseye
  FaceMakerMode = 3
  InnerWireTaper = 1
  LengthFwd = 76
  LengthRev = 0
  Placement = pos=(6,0,-72) rot=(0,0,1;0rad)
  Solid = true
  Symmetric = false
FEATURE [Sketcher::SketchObject] Sketch033  label="fermo per scheda micro"
  ArcFitTolerance = 1e-06
  AttachmentSupport = -> [XZ_Plane]
  ExternalGeometry = -> [Sketch]
  ExternalTypes = [0]
  FullyConstrained = true
  MakeInternals = false
  MapMode = 5
  Placement = pos=(0,0,0) rot=(1,0,0;1.5708rad)
  _ExternalGeoVersion = 0
  sketch-geometry (12):
    g0: LineSegment StartX=-11.6 StartY=6 StartZ=0 EndX=-4 EndY=6 EndZ=0
    g1: LineSegment StartX=-4 StartY=6 StartZ=0 EndX=-4 EndY=36.4 EndZ=0
    g2: LineSegment StartX=-4 StartY=36.4 StartZ=0 EndX=-11.6 EndY=36.4 EndZ=0
    g3: LineSegment StartX=-11.6 StartY=36.4 StartZ=0 EndX=-11.6 EndY=6 EndZ=0
    g4: LineSegment StartX=-80.11 StartY=11.6 StartZ=0 EndX=-70.51 EndY=11.6 EndZ=0
    g5: LineSegment StartX=-70.51 StartY=11.6 StartZ=0 EndX=-70.51 EndY=6 EndZ=0
    g6: LineSegment StartX=-70.51 StartY=6 StartZ=0 EndX=-80.11 EndY=6 EndZ=0
    g7: LineSegment StartX=-80.11 StartY=6 StartZ=0 EndX=-80.11 EndY=11.6 EndZ=0
    g8: LineSegment StartX=-78.51 StartY=36.4 StartZ=0 EndX=-70.51 EndY=36.4 EndZ=0
    g9: LineSegment StartX=-70.51 StartY=36.4 StartZ=0 EndX=-70.51 EndY=30.8 EndZ=0
    g10: LineSegment StartX=-70.51 StartY=30.8 StartZ=0 EndX=-78.51 EndY=30.8 EndZ=0
    g11: LineSegment StartX=-78.51 StartY=30.8 StartZ=0 EndX=-78.51 EndY=36.4 EndZ=0
  constraints (33):
    c: Horizontal(g0)
    c: Coincident(g1,g0)
    c: Coincident(g2,g1)
    c: Horizontal(g2)
    c: Coincident(g3,g2)
    c: Coincident(g3,g0)
    c: Vertical(g3)
    c: DistanceX(g2,g2) = 7.6
    c: Coincident(g1,g-3)
    c: Coincident(g0,g-3)
    c: Horizontal(g4)
    c: Coincident(g5,g4)
    c: Vertical(g5)
    c: Coincident(g6,g5)
    c: Horizontal(g6)
    c: Coincident(g7,g6)
    c: Coincident(g7,g4)
    c: Vertical(g7)
    c: DistanceY(g5,g5) = 5.6
    c: DistanceX(g4,g4) = 9.6
    c: Coincident(g9,g8)
    c: Vertical(g9)
    c: Coincident(g10,g9)
    c: Horizontal(g10)
    c: Coincident(g11,g10)
    c: Coincident(g11,g8)
    c: Vertical(g11)
    c: DistanceY(g9,g9) = 5.6
    c: DistanceX(g10,g10) = 8
    c: Coincident(g4,g-4)
    c: DistanceX(g4,g10) = 1.6
    c: Horizontal(g8)
    c: DistanceY(g8,g1) = 0
FEATURE [Sketcher::SketchObject] Sketch034  label="buchi guida rail"
  ArcFitTolerance = 1e-06
  AttachmentSupport = -> [XY_Plane]
  ExternalGeometry = -> [Sketch]
  ExternalTypes = [0]
  FullyConstrained = true
  MakeInternals = false
  MapMode = 5
  _ExternalGeoVersion = 0
  sketch-geometry (6):
    g0: LineSegment [constr] StartX=-100.8 StartY=9.1e-15 StartZ=0 EndX=-93.3 EndY=0 EndZ=0
    g1: LineSegment [constr] StartX=-93.3 StartY=0 StartZ=0 EndX=-73.3 EndY=0 EndZ=0
    g2: LineSegment [constr] StartX=-73.3 StartY=0 StartZ=0 EndX=-53.3 EndY=0 EndZ=0
    g3: Circle CenterX=-93.3 CenterY=0 CenterZ=0 NormalX=0 NormalY=0 NormalZ=1 AngleXU=0 Radius=2.5
    g4: Circle CenterX=-73.3 CenterY=0 CenterZ=0 NormalX=0 NormalY=0 NormalZ=1 AngleXU=0 Radius=2.5
    g5: Circle CenterX=-53.3 CenterY=0 CenterZ=0 NormalX=0 NormalY=0 NormalZ=1 AngleXU=0 Radius=2.5
  constraints (15):
    c: Distance(g0) = 7.5
    c: Coincident(g0,g-3)
    c: PointOnObject(g0,g-1)
    c: Distance(g1) = 20
    c: Coincident(g1,g0)
    c: PointOnObject(g1,g-1)
    c: Distance(g2) = 20
    c: Coincident(g2,g1)
    c: PointOnObject(g2,g-1)
    c: Diameter(g3) = 5
    c: Diameter(g4) = 5
    c: Diameter(g5) = 5
    c: Coincident(g3,g0)
    c: Coincident(g4,g1)
    c: Coincident(g5,g2)
FEATURE [Part::Extrusion] Extrude032  label="Extrude buchi guida rail"
  Base = -> Sketch034
  Dir = (0,0,1)
  DirMode = 2
  FaceMakerClass = Part::FaceMakerBullseye
  FaceMakerMode = 3
  InnerWireTaper = 1
  LengthFwd = -6.2
  LengthRev = 0
  Placement = pos=(0,0,43.2) rot=(0,0,1;0rad)
  Solid = true
  Symmetric = false
FEATURE [Part::Extrusion] Extrude033  label="Extrude fori superiori per solenoide e oled001"
  Base = -> Sketch030
  Dir = (0,0,1)
  DirMode = 2
  FaceMakerClass = Part::FaceMakerBullseye
  FaceMakerMode = 3
  InnerWireTaper = 1
  LengthFwd = -4.8
  LengthRev = 0
  Placement = pos=(0,0,41.2) rot=(0,0,1;0rad)
  Solid = true
  Symmetric = false
FEATURE [Part::Extrusion] Extrude034  label="Extrude fori sotto impugnatura001"
  Base = -> Sketch029
  Dir = (0,0,1)
  DirMode = 2
  FaceMakerClass = Part::FaceMakerBullseye
  FaceMakerMode = 3
  InnerWireTaper = 1
  LengthFwd = 5
  LengthRev = 0
  Placement = pos=(0,0,-83) rot=(0,0,1;0rad)
  Solid = true
  Symmetric = false
FEATURE [Part::Extrusion] Extrude035  label="Extrude fori inferiori switch pompa001"
  Base = -> Sketch031
  Dir = (0,0,1)
  DirMode = 2
  FaceMakerClass = Part::FaceMakerBullseye
  FaceMakerMode = 3
  InnerWireTaper = 1
  LengthFwd = 4
  LengthRev = 0
  Placement = pos=(0,0,-1.7) rot=(0,0,1;0rad)
  Solid = true
  Symmetric = false
FEATURE [Part::Extrusion] Extrude036  label="Extrude foro sotto posteriore M3x5x007"
  Base = -> Sketch027
  Dir = (0,0,1)
  DirMode = 2
  FaceMakerClass = Part::FaceMakerBullseye
  FaceMakerMode = 3
  InnerWireTaper = 1
  LengthFwd = 6.2
  LengthRev = 0
  Placement = pos=(0,0,-9.6) rot=(0,0,1;0rad)
  Solid = true
  Symmetric = false
FEATURE [Part::Extrusion] Extrude037  label="Extrude foro sotto anteriore M3x5x007"
  Base = -> Sketch026
  Dir = (0,0,1)
  DirMode = 2
  FaceMakerClass = Part::FaceMakerBullseye
  FaceMakerMode = 3
  InnerWireTaper = 1
  LengthFwd = 6.2
  LengthRev = 0
  Solid = true
  Symmetric = false
FEATURE [Sketcher::SketchObject] Sketch035  label="foro per fissaggio micro"
  ArcFitTolerance = 1e-06
  AttachmentSupport = -> [XZ_Plane]
  ExternalGeometry = -> [Sketch,Sketch033]
  ExternalTypes = [0]
  FullyConstrained = true
  MakeInternals = false
  MapMode = 5
  Placement = pos=(0,0,0) rot=(1,0,0;1.5708rad)
  _ExternalGeoVersion = 0
  sketch-geometry (3):
    g0: Circle CenterX=-7.8 CenterY=21.2 CenterZ=0 NormalX=0 NormalY=0 NormalZ=1 AngleXU=0 Radius=1.6
    g1: GeomPoint [constr] X=-4 Y=21.2 Z=0
    g2: LineSegment [constr] StartX=-4 StartY=21.2 StartZ=0 EndX=-11.6 EndY=21.2 EndZ=0
  constraints (6):
    c: Diameter(g0) = 3.2
    c: Symmetric(g-3,g-3,g1)
    c: Coincident(g2,g1)
    c: Horizontal(g2)
    c: DistanceX(g-4,g2) = 0
    c: Symmetric(g2,g1,g0)
FEATURE [Part::Extrusion] Extrude038  label="Extrude foro per fissaggio micro"
  Base = -> Sketch035
  Dir = (0,-1,2e-16)
  DirMode = 2
  FaceMakerClass = Part::FaceMakerBullseye
  FaceMakerMode = 3
  InnerWireTaper = 1
  LengthFwd = 3
  LengthRev = 0
  Placement = pos=(0,8.6,0) rot=(0,0,1;0rad)
  Solid = true
  Symmetric = false
FEATURE [Sketcher::SketchObject] Sketch036  label="supporto per alimentatore"
  ArcFitTolerance = 1e-06
  AttachmentSupport = -> [XZ_Plane]
  ExternalGeometry = -> [Sketch,Sketch016,Sketch022]
  ExternalTypes = [0]
  FullyConstrained = true
  MakeInternals = false
  MapMode = 5
  Placement = pos=(0,0,0) rot=(1,0,0;1.5708rad)
  _ExternalGeoVersion = 0
  sketch-geometry (5):
    g0: LineSegment StartX=-211.843 StartY=-50.0944 StartZ=0 EndX=-211.843 EndY=-80.4316 EndZ=0
    g1: LineSegment StartX=-211.843 StartY=-50.0944 StartZ=0 EndX=-207.775 EndY=-41.3701 EndZ=0
    g2: LineSegment [constr] StartX=-209.443 StartY=-50.0944 StartZ=0 EndX=-209.443 EndY=-80.4316 EndZ=0
    g3: LineSegment StartX=-207.775 StartY=-41.3701 StartZ=0 EndX=-207.775 EndY=-80.4316 EndZ=0
    g4: LineSegment StartX=-211.843 StartY=-80.4316 StartZ=0 EndX=-207.775 EndY=-80.4316 EndZ=0
  constraints (15):
    c: Vertical(g0)
    c: Coincident(g1,g0)
    c: Vertical(g2)
    c: Tangent(g2,g-5)
    c: Coincident(g3,g1)
    c: Vertical(g3)
    c: DistanceY(g-3,g3) = -2
    c: Tangent(g1,g-8)
    c: DistanceY(g-3,g0) = -2
    c: Coincident(g4,g0)
    c: Coincident(g4,g3)
    c: Tangent(g0,g-6)
    c: DistanceY(g-3,g2) = -2
    c: DistanceY(g2,g0) = 0
    c: DistanceX(g-3,g3) = 6.8
FEATURE [Part::Extrusion] Extrude039  label="Extrude039 supporto alimentatore"
  Base = -> Sketch036
  Dir = (0,-1,2e-16)
  DirMode = 2
  FaceMakerClass = Part::FaceMakerBullseye
  FaceMakerMode = 3
  InnerWireTaper = 1
  LengthFwd = 25.2
  LengthRev = 0
  Solid = true
  Symmetric = true
FEATURE [Sketcher::SketchObject] Sketch037  label="scavo per alimentatore"
  ArcFitTolerance = 1e-06
  AttachmentSupport = -> [XZ_Plane]
  ExternalGeometry = -> [Sketch036]
  ExternalTypes = [0]
  FullyConstrained = true
  MakeInternals = false
  MapMode = 5
  Placement = pos=(0,0,0) rot=(1,0,0;1.5708rad)
  _ExternalGeoVersion = 0
  sketch-geometry (4):
    g0: LineSegment StartX=-209.575 StartY=-50.4316 StartZ=0 EndX=-209.575 EndY=-80.4316 EndZ=0
    g1: LineSegment StartX=-209.575 StartY=-50.4316 StartZ=0 EndX=-207.775 EndY=-50.4316 EndZ=0
    g2: LineSegment StartX=-207.775 StartY=-50.4316 StartZ=0 EndX=-207.775 EndY=-80.4316 EndZ=0
    g3: LineSegment StartX=-207.775 StartY=-80.4316 StartZ=0 EndX=-209.575 EndY=-80.4316 EndZ=0
  constraints (11):
    c: Vertical(g0)
    c: Coincident(g1,g0)
    c: Horizontal(g1)
    c: Coincident(g2,g1)
    c: Vertical(g2)
    c: Coincident(g3,g2)
    c: Coincident(g3,g0)
    c: Horizontal(g3)
    c: DistanceX(g1,g1) = 1.8
    c: Coincident(g2,g-3)
    c: DistanceY(g2,g2) = 30
FEATURE [Part::Extrusion] Extrude040  label="Extrude040 scavo alimentatore"
  Base = -> Sketch037
  Dir = (0,-1,2e-16)
  DirMode = 2
  FaceMakerClass = Part::FaceMakerBullseye
  FaceMakerMode = 3
  InnerWireTaper = 1
  LengthFwd = 19.5
  LengthRev = 0
  Solid = true
  Symmetric = true
FEATURE [Part::Extrusion] Extrude031  label="Extrude fermo per scheda micro"
  Base = -> Sketch033
  Dir = (0,-1,2e-16)
  DirMode = 2
  FaceMakerClass = Part::FaceMakerBullseye
  FaceMakerMode = 3
  InnerWireTaper = 1
  LengthFwd = 3
  LengthRev = 0
  Placement = pos=(0,8.6,0) rot=(0,0,1;0rad)
  Solid = true
  Symmetric = false
FEATURE [Sketcher::SketchObject] Sketch038  label="scavo driver solenoide"
  ArcFitTolerance = 1e-06
  AttachmentSupport = -> [XZ_Plane]
  ExternalGeometry = -> [Sketch,Sketch036]
  ExternalTypes = [0]
  FullyConstrained = true
  MakeInternals = false
  MapMode = 5
  Placement = pos=(0,0,0) rot=(1,0,0;1.5708rad)
  _ExternalGeoVersion = 0
  sketch-geometry (8):
    g0: LineSegment StartX=-193.575 StartY=-10.9177 StartZ=0 EndX=-196.838 EndY=-9.39626 EndZ=0
    g1: LineSegment StartX=-196.838 StartY=-9.39626 StartZ=0 EndX=-214.165 EndY=-46.5549 EndZ=0
    g2: LineSegment StartX=-193.575 StartY=-10.9177 StartZ=0 EndX=-190.131 EndY=-12.5236 EndZ=0
    g3: LineSegment StartX=-190.131 StartY=-12.5236 StartZ=0 EndX=-206.38 EndY=-47.3701 EndZ=0
    g4: LineSegment [constr] StartX=-214.165 StartY=-46.5549 StartZ=0 EndX=-210.902 EndY=-48.0763 EndZ=0
    g5: LineSegment StartX=-214.165 StartY=-46.5549 StartZ=0 EndX=-210.902 EndY=-48.0763 EndZ=0
    g6: LineSegment StartX=-206.38 StartY=-47.3701 StartZ=0 EndX=-207.775 EndY=-47.3701 EndZ=0
    g7: LineSegment StartX=-207.775 StartY=-47.3701 StartZ=0 EndX=-210.902 EndY=-48.0763 EndZ=0
  constraints (23):
    c: Coincident(g1,g0)
    c: Coincident(g3,g2)
    c: Distance(g2) = 3.8
    c: Distance(g1) = 41
    c: Coincident(g4,g1)
    c: Distance(g4) = 3.6
    c: Perpendicular(g4,g-3)
    c: Parallel(g1,g-3)
    c: Perpendicular(g1,g0)
    c: Distance(g0) = 3.6
    c: Coincident(g5,g1)
    c: Parallel(g3,g-3)
    c: Perpendicular(g2,g3)
    c: Coincident(g2,g0)
    c: PointOnObject(g4,g-3)
    c: Distance(g-3,g4) = 6.4
    c: Coincident(g6,g3)
    c: Horizontal(g6)
    c: PointOnObject(g6,g-4)
    c: Coincident(g7,g6)
    c: Coincident(g7,g5)
    c: DistanceY(g6,g-4) = 6
    c: Coincident(g5,g4)
FEATURE [Part::Extrusion] Extrude041  label="Extrude scavo driver solenoide"
  Base = -> Sketch038
  Dir = (0,-1,2e-16)
  DirMode = 2
  FaceMakerClass = Part::FaceMakerBullseye
  FaceMakerMode = 3
  InnerWireTaper = 1
  LengthFwd = 20.6
  LengthRev = 0
  Solid = true
  Symmetric = true
FEATURE [Sketcher::SketchObject] Sketch039  label="scavo per cavo usb per micro"
  ArcFitTolerance = 1e-06
  AttachmentSupport = -> [XZ_Plane]
  ExternalGeometry = -> [Sketch,Sketch016]
  ExternalTypes = [0]
  FullyConstrained = true
  MakeInternals = false
  MapMode = 5
  Placement = pos=(0,0,0) rot=(1,0,0;1.5708rad)
  _ExternalGeoVersion = 0
  sketch-geometry (4):
    g0: LineSegment StartX=-82.51 StartY=36.4 StartZ=0 EndX=-74.51 EndY=36.4 EndZ=0
    g1: LineSegment StartX=-74.51 StartY=36.4 StartZ=0 EndX=-74.51 EndY=30.8 EndZ=0
    g2: LineSegment StartX=-74.51 StartY=30.8 StartZ=0 EndX=-82.51 EndY=30.8 EndZ=0
    g3: LineSegment StartX=-82.51 StartY=30.8 StartZ=0 EndX=-82.51 EndY=36.4 EndZ=0
  constraints (11):
    c: Coincident(g1,g0)
    c: Vertical(g1)
    c: Coincident(g2,g1)
    c: Horizontal(g2)
    c: Coincident(g3,g2)
    c: Coincident(g3,g0)
    c: Vertical(g3)
    c: Tangent(g0,g-3)
    c: Tangent(g2,g-4)
    c: Tangent(g3,g-4)
    c: Tangent(g1,g-4)
FEATURE [Part::Extrusion] Extrude042  label="Extrude scavo per cavo usb per micro"
  Base = -> Sketch039
  Dir = (0,-1,2e-16)
  DirMode = 2
  FaceMakerClass = Part::FaceMakerBullseye
  FaceMakerMode = 3
  InnerWireTaper = 1
  LengthFwd = 13.2
  LengthRev = 0
  Placement = pos=(0,5.6,0) rot=(0,0,1;0rad)
  Solid = true
  Symmetric = false
FEATURE [Sketcher::SketchObject] Sketch040  label="scavo saldature alimentatore connettore 5v"
  ArcFitTolerance = 1e-06
  AttachmentSupport = -> [XZ_Plane]
  ExternalGeometry = -> [Sketch037]
  ExternalTypes = [0]
  FullyConstrained = true
  MakeInternals = false
  MapMode = 5
  Placement = pos=(0,0,0) rot=(1,0,0;1.5708rad)
  _ExternalGeoVersion = 0
  sketch-geometry (4):
    g0: LineSegment StartX=-211.175 StartY=-52.4316 StartZ=0 EndX=-211.175 EndY=-56.4316 EndZ=0
    g1: LineSegment StartX=-211.175 StartY=-52.4316 StartZ=0 EndX=-209.575 EndY=-52.4316 EndZ=0
    g2: LineSegment StartX=-209.575 StartY=-52.4316 StartZ=0 EndX=-209.575 EndY=-56.4316 EndZ=0
    g3: LineSegment StartX=-209.575 StartY=-56.4316 StartZ=0 EndX=-211.175 EndY=-56.4316 EndZ=0
  constraints (11):
    c: Vertical(g0)
    c: Coincident(g1,g0)
    c: Horizontal(g1)
    c: Coincident(g2,g1)
    c: Coincident(g3,g2)
    c: Coincident(g3,g0)
    c: Horizontal(g3)
    c: DistanceX(g1,g1) = 1.6
    c: DistanceY(g2,g2) = 4
    c: Tangent(g2,g-3)
    c: DistanceY(g1,g-3) = 2
FEATURE [Part::Extrusion] Extrude043  label="Extrude scavo saldature alimentatore connettore 5v"
  Base = -> Sketch040
  Dir = (0,-1,2e-16)
  DirMode = 2
  FaceMakerClass = Part::FaceMakerBullseye
  FaceMakerMode = 3
  InnerWireTaper = 1
  LengthFwd = 8
  LengthRev = 0
  Solid = true
  Symmetric = true
FEATURE [Sketcher::SketchObject] Sketch041  label="scavo saldature alimentatore connettore 5v verticali"
  ArcFitTolerance = 1e-06
  AttachmentSupport = -> [XZ_Plane]
  ExternalGeometry = -> [Sketch037]
  ExternalTypes = [0]
  FullyConstrained = true
  MakeInternals = false
  MapMode = 5
  Placement = pos=(0,0,0) rot=(1,0,0;1.5708rad)
  _ExternalGeoVersion = 0
  sketch-geometry (4):
    g0: LineSegment StartX=-211.175 StartY=-53.6316 StartZ=0 EndX=-209.575 EndY=-53.6316 EndZ=0
    g1: LineSegment StartX=-209.575 StartY=-53.6316 StartZ=0 EndX=-209.575 EndY=-76.6316 EndZ=0
    g2: LineSegment StartX=-209.575 StartY=-76.6316 StartZ=0 EndX=-211.175 EndY=-76.6316 EndZ=0
    g3: LineSegment StartX=-211.175 StartY=-76.6316 StartZ=0 EndX=-211.175 EndY=-53.6316 EndZ=0
  constraints (11):
    c: Horizontal(g0)
    c: Coincident(g1,g0)
    c: Coincident(g2,g1)
    c: Horizontal(g2)
    c: Coincident(g3,g2)
    c: Coincident(g3,g0)
    c: Vertical(g3)
    c: DistanceY(g3,g3) = 23
    c: DistanceX(g0,g0) = 1.6
    c: Tangent(g1,g-3)
    c: DistanceY(g0,g-3) = 3.2
FEATURE [Part::Extrusion] Extrude044  label="Extrude scavo saldature alimentatore connettore 5v verticali"
  Base = -> Sketch041
  Dir = (0,-1,2e-16)
  DirMode = 2
  FaceMakerClass = Part::FaceMakerBullseye
  FaceMakerMode = 3
  InnerWireTaper = 1
  LengthFwd = 3.2
  LengthRev = 0
  Placement = pos=(0,8.3,0) rot=(0,0,1;0rad)
  Solid = true
  Symmetric = false
FEATURE [Sketcher::SketchObject] Sketch042  label="fermi per driver solenoide e alimentatore"
  ArcFitTolerance = 1e-06
  AttachmentSupport = -> [XZ_Plane]
  ExternalGeometry = -> [Sketch036,Sketch037,Sketch,Sketch038]
  ExternalTypes = [0]
  FullyConstrained = true
  MakeInternals = false
  MapMode = 5
  Placement = pos=(0,0,0) rot=(1,0,0;1.5708rad)
  _ExternalGeoVersion = 0
  sketch-geometry (27):
    g0: LineSegment StartX=-198.308 StartY=-21.0683 StartZ=0 EndX=-199.238 EndY=-23.0622 EndZ=0
    g1: LineSegment StartX=-199.238 StartY=-23.0622 StartZ=0 EndX=-197.244 EndY=-23.992 EndZ=0
    g2: LineSegment StartX=-197.244 StartY=-23.992 StartZ=0 EndX=-196.314 EndY=-21.9981 EndZ=0
    g3: LineSegment StartX=-196.314 StartY=-21.9981 StartZ=0 EndX=-198.308 EndY=-21.0683 EndZ=0
    g4: LineSegment StartX=-199.082 StartY=-18.9421 StartZ=0 EndX=-201.364 EndY=-23.8361 EndZ=0
    g5: LineSegment StartX=-201.364 StartY=-23.8361 StartZ=0 EndX=-197.92 EndY=-25.4421 EndZ=0
    g6: LineSegment StartX=-195.794 StartY=-24.6682 StartZ=0 EndX=-194.864 EndY=-22.6743 EndZ=0
    g7: LineSegment StartX=-195.638 StartY=-20.548 StartZ=0 EndX=-199.082 EndY=-18.9421 EndZ=0
    g8: LineSegment [constr] StartX=-196.47 StartY=-26.1183 StartZ=0 EndX=-195.794 EndY=-24.6682 EndZ=0
    g9: LineSegment [constr] StartX=-196.47 StartY=-26.1183 StartZ=0 EndX=-197.92 EndY=-25.4421 EndZ=0
    g10: ArcOfCircle CenterX=-196.314 CenterY=-21.9981 CenterZ=0 NormalX=0 NormalY=0 NormalZ=1 AngleXU=0 Radius=1.6 StartAngle=5.84685 EndAngle=7.41765
    g11: GeomPoint [constr] X=-194.188 Y=-21.2242 Z=0
    g12: ArcOfCircle CenterX=-197.244 CenterY=-23.992 CenterZ=0 NormalX=0 NormalY=0 NormalZ=1 AngleXU=0 Radius=1.6 StartAngle=4.27606 EndAngle=5.84685
    g13: GeomPoint [constr] X=-196.47 Y=-26.1183 Z=0
    g14: LineSegment StartX=-207.775 StartY=-46.8316 StartZ=0 EndX=-207.775 EndY=-50.8316 EndZ=0
    g15: LineSegment StartX=-207.775 StartY=-46.8316 StartZ=0 EndX=-203.775 EndY=-46.8316 EndZ=0
    g16: LineSegment StartX=-203.775 StartY=-46.8316 StartZ=0 EndX=-203.775 EndY=-50.8316 EndZ=0
    g17: LineSegment StartX=-207.775 StartY=-50.8316 StartZ=0 EndX=-203.775 EndY=-50.8316 EndZ=0
    g18: LineSegment StartX=-209.375 StartY=-52.4316 StartZ=0 EndX=-203.775 EndY=-52.4316 EndZ=0
    g19: LineSegment StartX=-202.175 StartY=-50.8316 StartZ=0 EndX=-202.175 EndY=-46.8316 EndZ=0
    g20: LineSegment StartX=-203.775 StartY=-45.2316 StartZ=0 EndX=-209.375 EndY=-45.2316 EndZ=0
    g21: LineSegment StartX=-209.375 StartY=-45.2316 StartZ=0 EndX=-209.375 EndY=-52.4316 EndZ=0
    g22: ArcOfCircle CenterX=-203.775 CenterY=-46.8316 CenterZ=0 NormalX=0 NormalY=0 NormalZ=1 AngleXU=0 Radius=1.6 StartAngle=1.8e-15 EndAngle=1.5708
    g23: GeomPoint [constr] X=-202.175 Y=-45.2316 Z=0
    g24: ArcOfCircle CenterX=-203.775 CenterY=-50.8316 CenterZ=0 NormalX=0 NormalY=0 NormalZ=1 AngleXU=0 Radius=1.6 StartAngle=4.71239 EndAngle=6.28319
    g25: GeomPoint [constr] X=-202.175 Y=-52.4316 Z=0
    g26: LineSegment [constr] StartX=-207.775 StartY=-50.4316 StartZ=0 EndX=-207.775 EndY=-50.8316 EndZ=0
  constraints (69):
    c: Coincident(g1,g0)
    c: Coincident(g2,g1)
    c: Coincident(g3,g2)
    c: Coincident(g3,g0)
    c: Parallel(g0,g2)
    c: Perpendicular(g3,g0)
    c: Perpendicular(g1,g0)
    c: Coincident(g5,g4)
    c: Coincident(g7,g4)
    c: Distance(g3) = 2.2
    c: Distance(g2) = 2.2
    c: Parallel(g6,g2)
    c: Parallel(g6,g4)
    c: Perpendicular(g5,g6)
    c: Perpendicular(g7,g6)
    c: Distance(g13,g11) = 5.4
    c: Distance(g5,g13) = 5.4
    c: Coincident(g9,g8)
    c: Distance(g8) = 1.6
    c: Distance(g9) = 1.6
    c: Perpendicular(g9,g8)
    c: Parallel(g8,g6)
    c: Coincident(g8,g13)
    c: Distance(g8,g1) = 1.6
    c: Distance(g9,g1) = 1.6
    c: Tangent(g0,g-5)
    c: Distance(g0,g-6) = 27.6
    c: PointOnObject(g11,g7)
    c: PointOnObject(g11,g6)
    c: Tangent(g7,g10) = -1.5708
    c: Tangent(g6,g10) = -1.5708
    c: PointOnObject(g13,g5)
    c: Tangent(g5,g12) = -1.5708
    c: Tangent(g6,g12) = -1.5708
    c: Equal(g10,g12)
    c: Coincident(g10,g2)
    c: Vertical(g14)
    c: Coincident(g15,g14)
    c: Horizontal(g15)
    c: Coincident(g16,g15)
    c: Vertical(g16)
    c: Coincident(g17,g14)
    c: Coincident(g17,g16)
    c: Horizontal(g17)
    c: Distance(g16) = 4
    c: Distance(g15) = 4
    c: Horizontal(g18)
    c: Vertical(g19)
    c: Horizontal(g20)
    c: Coincident(g21,g20)
    c: Coincident(g21,g18)
    c: Vertical(g21)
    c: Distance(g20,g23) = 7.2
    c: Distance(g25,g23) = 7.2
    c: DistanceY(g18,g14) = 1.6
    c: DistanceX(g18,g14) = 1.6
    c: PointOnObject(g23,g20)
    c: PointOnObject(g23,g19)
    c: Tangent(g20,g22) = -1.5708
    c: Tangent(g19,g22) = -1.5708
    c: PointOnObject(g25,g19)
    c: Tangent(g18,g24) = -1.5708
    c: Tangent(g19,g24) = -1.5708
    c: Equal(g22,g24)
    c: Coincident(g22,g15)
    c: Vertical(g26)
    c: Distance(g26) = 0.4
    c: Coincident(g26,g-4)
    c: Coincident(g14,g26)
FEATURE [Part::Extrusion] Extrude045  label="Extrude fermi per driver solenoide e alimentatore"
  Base = -> Sketch042
  Dir = (0,-1,2e-16)
  DirMode = 2
  FaceMakerClass = Part::FaceMakerBullseye
  FaceMakerMode = 3
  InnerWireTaper = 1
  LengthFwd = 25.2
  LengthRev = 0
  Solid = true
  Symmetric = true
FEATURE [Sketcher::SketchObject] Sketch043  label="scavo pulizia fermo alimentatore"
  ArcFitTolerance = 1e-06
  AttachmentSupport = -> [XZ_Plane]
  ExternalGeometry = -> [Sketch042,Sketch036,Sketch037]
  ExternalTypes = [0]
  FullyConstrained = true
  MakeInternals = false
  MapMode = 5
  Placement = pos=(0,0,0) rot=(1,0,0;1.5708rad)
  _ExternalGeoVersion = 0
  sketch-geometry (6):
    g0: LineSegment StartX=-209.375 StartY=-52.4316 StartZ=0 EndX=-209.375 EndY=-50.4316 EndZ=0
    g1: LineSegment StartX=-209.375 StartY=-50.4316 StartZ=0 EndX=-207.775 EndY=-50.4316 EndZ=0
    g2: LineSegment StartX=-207.775 StartY=-50.4316 StartZ=0 EndX=-207.775 EndY=-45.2316 EndZ=0
    g3: LineSegment StartX=-207.775 StartY=-45.2316 StartZ=0 EndX=-202.175 EndY=-45.2316 EndZ=0
    g4: LineSegment StartX=-202.175 StartY=-45.2316 StartZ=0 EndX=-202.175 EndY=-52.4316 EndZ=0
    g5: LineSegment StartX=-202.175 StartY=-52.4316 StartZ=0 EndX=-209.375 EndY=-52.4316 EndZ=0
  constraints (13):
    c: Vertical(g0)
    c: Coincident(g1,g0)
    c: Coincident(g2,g1)
    c: Coincident(g3,g2)
    c: Coincident(g4,g3)
    c: Coincident(g5,g4)
    c: Coincident(g5,g0)
    c: Horizontal(g5)
    c: Coincident(g0,g-6)
    c: Tangent(g1,g-8)
    c: Tangent(g2,g-4)
    c: Tangent(g3,g-7)
    c: Tangent(g4,g-3)
FEATURE [Part::Extrusion] Extrude046  label="Extrude scavo pulizia fermo alimentatore"
  Base = -> Sketch043
  Dir = (0,-1,2e-16)
  DirMode = 2
  FaceMakerClass = Part::FaceMakerBullseye
  FaceMakerMode = 3
  InnerWireTaper = 1
  LengthFwd = 19.5
  LengthRev = 0
  Solid = true
  Symmetric = true
FEATURE [Sketcher::SketchObject] Sketch044  label="buchini per fissaggio oled"
  ArcFitTolerance = 1e-06
  AttachmentSupport = -> [YZ_Plane]
  ExternalGeometry = -> [Sketch]
  ExternalTypes = [0]
  FullyConstrained = true
  MakeInternals = false
  MapMode = 5
  Placement = pos=(0,0,0) rot=(0.57735,0.57735,0.57735;2.0944rad)
  _ExternalGeoVersion = 0
  sketch-geometry (5):
    g0: LineSegment [constr] StartX=1.5e-14 StartY=67.3588 StartZ=0 EndX=0 EndY=64.3588 EndZ=0
    g1: LineSegment [constr] StartX=0 StartY=64.3588 StartZ=0 EndX=10.4 EndY=64.3588 EndZ=0
    g2: LineSegment [constr] StartX=0 StartY=64.3588 StartZ=0 EndX=-10.4 EndY=64.3588 EndZ=0
    g3: Circle CenterX=10.4 CenterY=64.3588 CenterZ=0 NormalX=0 NormalY=0 NormalZ=1 AngleXU=0 Radius=1.5
    g4: Circle CenterX=-10.4 CenterY=64.3588 CenterZ=0 NormalX=0 NormalY=0 NormalZ=1 AngleXU=0 Radius=1.5
  constraints (13):
    c: Distance(g0) = 3
    c: PointOnObject(g0,g-2)
    c: Coincident(g1,g0)
    c: Horizontal(g1)
    c: Coincident(g2,g0)
    c: Horizontal(g2)
    c: DistanceX(g1,g1) = 10.4
    c: Coincident(g3,g1)
    c: Diameter(g4) = 3
    c: Coincident(g4,g2)
    c: Coincident(g0,g-7)
    c: Equal(g1,g2)
    c: Equal(g4,g3)
FEATURE [Part::Extrusion] Extrude047  label="Extrude buchini per fissaggio oled"
  Base = -> Sketch044
  Dir = (1,0,0)
  DirMode = 2
  FaceMakerClass = Part::FaceMakerBullseye
  FaceMakerMode = 3
  InnerWireTaper = 1
  LengthFwd = 10
  LengthRev = 0
  Placement = pos=(-186,0,0) rot=(0,0,1;0rad)
  Solid = true
  Symmetric = false
FEATURE [Sketcher::SketchObject] Sketch046  label="scavo 5x5 neopixel"
  ArcFitTolerance = 1e-06
  AttachmentSupport = -> [YZ_Plane002]
  ExternalTypes = [0]
  FullyConstrained = true
  MakeInternals = false
  MapMode = 5
  Placement = pos=(0,0,0) rot=(0.57735,0.57735,0.57735;2.0944rad)
  _ExternalGeoVersion = 0
  sketch-geometry (4):
    g0: LineSegment StartX=-2.7 StartY=2.7 StartZ=0 EndX=2.7 EndY=2.7 EndZ=0
    g1: LineSegment StartX=2.7 StartY=2.7 StartZ=0 EndX=2.7 EndY=-2.7 EndZ=0
    g2: LineSegment StartX=2.7 StartY=-2.7 StartZ=0 EndX=-2.7 EndY=-2.7 EndZ=0
    g3: LineSegment StartX=-2.7 StartY=-2.7 StartZ=0 EndX=-2.7 EndY=2.7 EndZ=0
  constraints (11):
    c: Horizontal(g0)
    c: Coincident(g1,g0)
    c: Vertical(g1)
    c: Coincident(g2,g1)
    c: Horizontal(g2)
    c: Coincident(g3,g2)
    c: Coincident(g3,g0)
    c: Vertical(g3)
    c: DistanceX(g0,g0) = 5.4
    c: DistanceY(g1,g1) = 5.4
    c: Symmetric(g0,g1,g-1)
FEATURE [Sketcher::SketchObject] Sketch047  label="scavo 10x10 neopixel corpo"
  ArcFitTolerance = 1e-06
  AttachmentOffset = pos=(0,0,1) rot=(0,0,1;0rad)
  AttachmentSupport = -> [YZ_Plane002]
  ExternalTypes = [0]
  FullyConstrained = true
  MakeInternals = false
  MapMode = 5
  Placement = pos=(1,0,0) rot=(0.57735,0.57735,0.57735;2.0944rad)
  _ExternalGeoVersion = 0
  sketch-geometry (4):
    g0: LineSegment StartX=-5 StartY=5.1 StartZ=0 EndX=5 EndY=5.1 EndZ=0
    g1: LineSegment StartX=5 StartY=5.1 StartZ=0 EndX=5 EndY=-5.1 EndZ=0
    g2: LineSegment StartX=5 StartY=-5.1 StartZ=0 EndX=-5 EndY=-5.1 EndZ=0
    g3: LineSegment StartX=-5 StartY=-5.1 StartZ=0 EndX=-5 EndY=5.1 EndZ=0
  constraints (11):
    c: Horizontal(g0)
    c: Coincident(g1,g0)
    c: Vertical(g1)
    c: Coincident(g2,g1)
    c: Horizontal(g2)
    c: Coincident(g3,g2)
    c: Coincident(g3,g0)
    c: Vertical(g3)
    c: DistanceX(g0,g0) = 10
    c: DistanceY(g1,g1) = 10.2
    c: Symmetric(g0,g2,g-1)
FEATURE [Sketcher::SketchObject] Sketch048  label="buco per perno blocco neopixel"
  ArcFitTolerance = 1e-06
  AttachmentSupport = -> [XZ_Plane002]
  ExternalTypes = [0]
  FullyConstrained = true
  MakeInternals = false
  MapMode = 5
  Placement = pos=(0,0,0) rot=(1,0,0;1.5708rad)
  _ExternalGeoVersion = 0
  sketch-geometry (4):
    g0: LineSegment StartX=3 StartY=1.2 StartZ=0 EndX=3 EndY=-1.2 EndZ=0
    g1: LineSegment StartX=3 StartY=-1.2 StartZ=0 EndX=5.4 EndY=-1.2 EndZ=0
    g2: LineSegment StartX=5.4 StartY=-1.2 StartZ=0 EndX=5.4 EndY=1.2 EndZ=0
    g3: LineSegment StartX=5.4 StartY=1.2 StartZ=0 EndX=3 EndY=1.2 EndZ=0
  constraints (11):
    c: Coincident(g1,g0)
    c: Horizontal(g1)
    c: Coincident(g2,g1)
    c: Vertical(g2)
    c: Coincident(g3,g2)
    c: Coincident(g3,g0)
    c: Horizontal(g3)
    c: DistanceX(g1,g1) = 2.4
    c: DistanceY(g2,g2) = 2.4
    c: Symmetric(g0,g0,g-1)
    c: DistanceX(g-1,g0) = 3
FEATURE [Sketcher::SketchObject] Sketch045  label="blocco principale per neopixel"
  ArcFitTolerance = 1e-06
  AttachmentSupport = -> [XZ_Plane002]
  ExternalGeometry = -> [Sketch048]
  ExternalTypes = [0]
  FullyConstrained = true
  MakeInternals = false
  MapMode = 5
  Placement = pos=(0,0,0) rot=(1,0,0;1.5708rad)
  _ExternalGeoVersion = 0
  sketch-geometry (6):
    g0: LineSegment StartX=0 StartY=5.1 StartZ=0 EndX=0 EndY=-5.1 EndZ=0
    g1: LineSegment StartX=0 StartY=-5.1 StartZ=0 EndX=3 EndY=-5.1 EndZ=0
    g2: LineSegment StartX=7 StartY=-1.1 StartZ=0 EndX=7 EndY=5.1 EndZ=0
    g3: LineSegment StartX=7 StartY=5.1 StartZ=0 EndX=0 EndY=5.1 EndZ=0
    g4: ArcOfCircle CenterX=3 CenterY=-1.1 CenterZ=0 NormalX=0 NormalY=0 NormalZ=1 AngleXU=0 Radius=4 StartAngle=4.71239 EndAngle=6.28319
    g5: GeomPoint [constr] X=7 Y=-5.1 Z=0
  constraints (15):
    c: Vertical(g0)
    c: Coincident(g1,g0)
    c: Horizontal(g1)
    c: Vertical(g2)
    c: Coincident(g3,g2)
    c: Coincident(g3,g0)
    c: Horizontal(g3)
    c: DistanceY(g0,g0) = 10.2
    c: Symmetric(g0,g0,g-1)
    c: DistanceX(g3,g3) = 7
    c: PointOnObject(g5,g2)
    c: PointOnObject(g5,g1)
    c: Tangent(g2,g4) = -1.5708
    c: Tangent(g1,g4) = -1.5708
    c: DistanceX(g-3,g1) = 0
FEATURE [Sketcher::SketchObject] Sketch049  label="rinforzi esterni per corpo neopoixel"
  ArcFitTolerance = 1e-06
  AttachmentSupport = -> [XZ_Plane002]
  ExternalGeometry = -> [Sketch045]
  ExternalTypes = [0]
  FullyConstrained = true
  MakeInternals = false
  MapMode = 5
  Placement = pos=(0,0,0) rot=(1,0,0;1.5708rad)
  _ExternalGeoVersion = 0
  sketch-geometry (8):
    g0: LineSegment StartX=1 StartY=-4.1 StartZ=0 EndX=2 EndY=-4.1 EndZ=0
    g1: LineSegment StartX=2 StartY=-4.1 StartZ=0 EndX=2 EndY=-5.1 EndZ=0
    g2: LineSegment StartX=2 StartY=-5.1 StartZ=0 EndX=1 EndY=-5.1 EndZ=0
    g3: LineSegment StartX=1 StartY=-5.1 StartZ=0 EndX=1 EndY=-4.1 EndZ=0
    g4: LineSegment StartX=1 StartY=5.1 StartZ=0 EndX=2 EndY=5.1 EndZ=0
    g5: LineSegment StartX=2 StartY=5.1 StartZ=0 EndX=2 EndY=4.1 EndZ=0
    g6: LineSegment StartX=2 StartY=4.1 StartZ=0 EndX=1 EndY=4.1 EndZ=0
    g7: LineSegment StartX=1 StartY=4.1 StartZ=0 EndX=1 EndY=5.1 EndZ=0
  constraints (24):
    c: Horizontal(g0)
    c: Coincident(g1,g0)
    c: Vertical(g1)
    c: Coincident(g2,g1)
    c: Horizontal(g2)
    c: Coincident(g3,g2)
    c: Coincident(g3,g0)
    c: Vertical(g3)
    c: Horizontal(g4)
    c: Coincident(g5,g4)
    c: Vertical(g5)
    c: Coincident(g6,g5)
    c: Horizontal(g6)
    c: Coincident(g7,g6)
    c: Coincident(g7,g4)
    c: Vertical(g7)
    c: DistanceX(g4,g4) = 1
    c: DistanceY(g5,g5) = 1
    c: DistanceX(g0,g0) = 1
    c: DistanceY(g1,g1) = 1
    c: DistanceX(g-3,g4) = 1
    c: DistanceY(g-3,g4) = 0
    c: DistanceX(g-4,g2) = 1
    c: DistanceY(g2,g-4) = 0
FEATURE [Sketcher::SketchObject] Sketch052  label="scavo saldature driver solenoide"
  ArcFitTolerance = 1e-06
  AttachmentSupport = -> [XZ_Plane]
  ExternalGeometry = -> [Sketch038]
  ExternalTypes = [0]
  FullyConstrained = true
  MakeInternals = false
  MapMode = 5
  Placement = pos=(0,0,0) rot=(1,0,0;1.5708rad)
  _ExternalGeoVersion = 0
  sketch-geometry (4):
    g0: LineSegment StartX=-197.2 StartY=-9.22721 StartZ=0 EndX=-198.891 EndY=-12.8524 EndZ=0
    g1: LineSegment StartX=-198.891 StartY=-12.8524 StartZ=0 EndX=-198.528 EndY=-13.0215 EndZ=0
    g2: LineSegment StartX=-198.528 StartY=-13.0215 StartZ=0 EndX=-196.838 EndY=-9.39626 EndZ=0
    g3: LineSegment StartX=-196.838 StartY=-9.39626 StartZ=0 EndX=-197.2 EndY=-9.22721 EndZ=0
  constraints (11):
    c: Coincident(g1,g0)
    c: Coincident(g2,g1)
    c: Coincident(g3,g2)
    c: Coincident(g3,g0)
    c: Parallel(g2,g0)
    c: Perpendicular(g2,g3)
    c: Perpendicular(g1,g2,g1) = 1.5708
    c: Parallel(g2,g-3)
    c: Distance(g2) = 4
    c: Distance(g3) = 0.4
    c: Coincident(g2,g-3)
FEATURE [Part::Extrusion] Extrude055  label="Extrude scavo saldature driver solenoide"
  Base = -> Sketch052
  Dir = (0,-1,2e-16)
  DirMode = 2
  FaceMakerClass = Part::FaceMakerBullseye
  FaceMakerMode = 3
  InnerWireTaper = 1
  LengthFwd = 6
  LengthRev = 0
  Solid = true
  Symmetric = true
FEATURE [Sketcher::SketchObject] Sketch053  label="scavo saldature rumble"
  ArcFitTolerance = 1e-06
  AttachmentSupport = -> [XZ_Plane]
  ExternalGeometry = -> [Sketch019]
  ExternalTypes = [0]
  FullyConstrained = true
  MakeInternals = false
  MapMode = 5
  Placement = pos=(0,0,0) rot=(1,0,0;1.5708rad)
  _ExternalGeoVersion = 0
  sketch-geometry (4):
    g0: LineSegment StartX=-169.451 StartY=-56.8615 StartZ=0 EndX=-170.687 EndY=-60.6657 EndZ=0
    g1: LineSegment StartX=-170.687 StartY=-60.6657 StartZ=0 EndX=-169.546 EndY=-61.0365 EndZ=0
    g2: LineSegment StartX=-169.546 StartY=-61.0365 StartZ=0 EndX=-168.31 EndY=-57.2323 EndZ=0
    g3: LineSegment StartX=-168.31 StartY=-57.2323 StartZ=0 EndX=-169.451 EndY=-56.8615 EndZ=0
  constraints (11):
    c: Coincident(g1,g0)
    c: Coincident(g2,g1)
    c: Coincident(g3,g2)
    c: Coincident(g3,g0)
    c: Parallel(g0,g2)
    c: Perpendicular(g3,g0)
    c: Perpendicular(g1,g0)
    c: Parallel(g0,g-3)
    c: Distance(g0) = 4
    c: Coincident(g0,g-3)
    c: Distance(g1) = 1.2
FEATURE [Part::Extrusion] Extrude056  label="Extrude scavo saldature rumble"
  Base = -> Sketch053
  Dir = (0,-1,2e-16)
  DirMode = 2
  FaceMakerClass = Part::FaceMakerBullseye
  FaceMakerMode = 3
  InnerWireTaper = 1
  LengthFwd = 8.4
  LengthRev = 0
  Solid = true
  Symmetric = true
FEATURE [Sketcher::SketchObject] Sketch054  label="scavo saldature alimentatore connettore USB"
  ArcFitTolerance = 1e-06
  AttachmentSupport = -> [XZ_Plane]
  ExternalGeometry = -> [Sketch037]
  ExternalTypes = [0]
  FullyConstrained = true
  MakeInternals = false
  MapMode = 5
  Placement = pos=(0,0,0) rot=(1,0,0;1.5708rad)
  _ExternalGeoVersion = 0
  sketch-geometry (4):
    g0: LineSegment StartX=-209.575 StartY=-80.4316 StartZ=0 EndX=-210.375 EndY=-80.4316 EndZ=0
    g1: LineSegment StartX=-210.375 StartY=-80.4316 StartZ=0 EndX=-210.375 EndY=-72.4316 EndZ=0
    g2: LineSegment StartX=-210.375 StartY=-72.4316 StartZ=0 EndX=-209.575 EndY=-72.4316 EndZ=0
    g3: LineSegment StartX=-209.575 StartY=-72.4316 StartZ=0 EndX=-209.575 EndY=-80.4316 EndZ=0
  constraints (11):
    c: Horizontal(g0)
    c: Coincident(g1,g0)
    c: Vertical(g1)
    c: Coincident(g2,g1)
    c: Horizontal(g2)
    c: Coincident(g3,g2)
    c: Coincident(g3,g0)
    c: Vertical(g3)
    c: DistanceX(g0,g0) = 0.8
    c: DistanceY(g3,g3) = 8
    c: Coincident(g0,g-4)
FEATURE [Part::Extrusion] Extrude057  label="Extrude scavo saldature alimentatore connettore USB"
  Base = -> Sketch054
  Dir = (0,-1,2e-16)
  DirMode = 2
  FaceMakerClass = Part::FaceMakerBullseye
  FaceMakerMode = 3
  InnerWireTaper = 1
  LengthFwd = 11
  LengthRev = 0
  Solid = true
  Symmetric = true
FEATURE [Sketcher::SketchObject] Sketch055  label="buco interno per micro switch"
  ArcFitTolerance = 1e-06
  AttachmentSupport = -> [XZ_Plane]
  ExternalGeometry = -> [Sketch]
  ExternalTypes = [0]
  FullyConstrained = true
  MakeInternals = false
  MapMode = 5
  Placement = pos=(0,0,0) rot=(1,0,0;1.5708rad)
  _ExternalGeoVersion = 0
  sketch-geometry (11):
    g0: LineSegment [constr] StartX=-194.483 StartY=34.2854 StartZ=0 EndX=-196.022 EndY=30.0568 EndZ=0
    g1: LineSegment [constr] StartX=-196.022 StartY=30.0568 StartZ=0 EndX=-197.561 EndY=25.8282 EndZ=0
    g2: LineSegment [constr] StartX=-196.022 StartY=30.0568 StartZ=0 EndX=-194.143 EndY=29.3727 EndZ=0
    g3: LineSegment [constr] StartX=-196.022 StartY=30.0568 StartZ=0 EndX=-197.902 EndY=30.7408 EndZ=0
    g4: LineSegment StartX=-196.362 StartY=34.9694 StartZ=0 EndX=-192.604 EndY=33.6014 EndZ=0
    g5: LineSegment StartX=-199.441 StartY=26.5122 StartZ=0 EndX=-195.682 EndY=25.1441 EndZ=0
    g6: LineSegment StartX=-192.604 StartY=33.6014 StartZ=0 EndX=-195.682 EndY=25.1441 EndZ=0
    g7: LineSegment StartX=-196.362 StartY=34.9694 StartZ=0 EndX=-199.441 EndY=26.5122 EndZ=0
    g8: GeomPoint [constr] X=-187.821 Y=29.2 Z=0
    g9: LineSegment [constr] StartX=-188.505 StartY=27.3206 StartZ=0 EndX=-196.022 EndY=30.0568 EndZ=0
    g10: LineSegment [constr] StartX=-187.821 StartY=29.2 StartZ=0 EndX=-188.505 EndY=27.3206 EndZ=0
  constraints (27):
    c: Coincident(g2,g0)
    c: Parallel(g0,g-3)
    c: Tangent(g1,g0) = -1.5708
    c: Perpendicular(g0,g2)
    c: Tangent(g2,g3)
    c: Distance(g0,g1) = 9
    c: Equal(g0,g1)
    c: Distance(g3,g2) = 4
    c: Equal(g2,g3)
    c: Parallel(g3,g4)
    c: Symmetric(g4,g4,g0)
    c: Parallel(g6,g1)
    c: Parallel(g7,g1)
    c: Symmetric(g6,g6,g2)
    c: Symmetric(g5,g5,g1)
    c: Symmetric(g7,g7,g3)
    c: Coincident(g7,g4)
    c: Coincident(g6,g4)
    c: Coincident(g5,g6)
    c: Symmetric(g-3,g-3,g8)
    c: Perpendicular(g-3,g9)
    c: Distance(g9) = 8
    c: Coincident(g3,g9)
    c: Coincident(g10,g8)
    c: Parallel(g10,g-3)
    c: Distance(g10) = 2
    c: Coincident(g10,g9)
FEATURE [Sketcher::SketchObject] Sketch056  label="buco esterno per micro switch"
  ArcFitTolerance = 1e-06
  AttachmentSupport = -> [XZ_Plane]
  ExternalGeometry = -> [Sketch055]
  ExternalTypes = [0]
  FullyConstrained = true
  MakeInternals = false
  MapMode = 5
  Placement = pos=(0,0,0) rot=(1,0,0;1.5708rad)
  _ExternalGeoVersion = 0
  sketch-geometry (17):
    g0: GeomPoint [constr] X=-194.143 Y=29.3727 Z=0
    g1: GeomPoint [constr] X=-194.483 Y=34.2854 Z=0
    g2: GeomPoint [constr] X=-197.902 Y=30.7408 Z=0
    g3: GeomPoint [constr] X=-197.561 Y=25.8282 Z=0
    g4: GeomPoint [constr] X=-196.022 Y=30.0568 Z=0
    g5: LineSegment [constr] StartX=-194.483 StartY=34.2854 StartZ=0 EndX=-196.022 EndY=30.0568 EndZ=0
    g6: LineSegment [constr] StartX=-196.022 StartY=30.0568 StartZ=0 EndX=-197.561 EndY=25.8282 EndZ=0
    g7: LineSegment [constr] StartX=-197.902 StartY=30.7408 StartZ=0 EndX=-196.022 EndY=30.0568 EndZ=0
    g8: LineSegment [constr] StartX=-196.022 StartY=30.0568 StartZ=0 EndX=-194.143 EndY=29.3727 EndZ=0
    g9: LineSegment [constr] StartX=-195.338 StartY=31.9362 StartZ=0 EndX=-196.022 EndY=30.0568 EndZ=0
    g10: LineSegment [constr] StartX=-196.022 StartY=30.0568 StartZ=0 EndX=-196.706 EndY=28.1774 EndZ=0
    g11: LineSegment [constr] StartX=-196.022 StartY=30.0568 StartZ=0 EndX=-196.821 EndY=30.3475 EndZ=0
    g12: LineSegment [constr] StartX=-196.022 StartY=30.0568 StartZ=0 EndX=-195.223 EndY=29.7661 EndZ=0
    g13: LineSegment StartX=-194.539 StartY=31.6454 StartZ=0 EndX=-195.907 EndY=27.8867 EndZ=0
    g14: LineSegment StartX=-196.137 StartY=32.2269 StartZ=0 EndX=-197.505 EndY=28.4681 EndZ=0
    g15: LineSegment StartX=-196.137 StartY=32.2269 StartZ=0 EndX=-194.539 EndY=31.6454 EndZ=0
    g16: LineSegment StartX=-197.505 StartY=28.4681 StartZ=0 EndX=-195.907 EndY=27.8867 EndZ=0
  constraints (34):
    c: Symmetric(g-5,g-5,g1)
    c: Symmetric(g-5,g-6,g0)
    c: Symmetric(g-6,g-6,g3)
    c: Symmetric(g-5,g-6,g2)
    c: Coincident(g5,g1)
    c: Coincident(g5,g4)
    c: Coincident(g6,g4)
    c: Coincident(g6,g3)
    c: Equal(g5,g6)
    c: Coincident(g7,g2)
    c: Coincident(g7,g4)
    c: Coincident(g8,g4)
    c: Coincident(g8,g0)
    c: Equal(g7,g8)
    c: Coincident(g11,g9)
    c: Coincident(g12,g9)
    c: Tangent(g10,g9) = -1.5708
    c: Perpendicular(g11,g9)
    c: Parallel(g9,g-4)
    c: Equal(g9,g10)
    c: Parallel(g12,g11)
    c: Equal(g11,g12)
    c: Distance(g11,g12) = 1.7
    c: Distance(g9,g10) = 4
    c: Symmetric(g13,g13,g12)
    c: Parallel(g13,g9)
    c: Symmetric(g14,g14,g11)
    c: Symmetric(g15,g15,g9)
    c: Parallel(g15,g11)
    c: Symmetric(g16,g16,g10)
    c: Coincident(g16,g14)
    c: Coincident(g15,g14)
    c: Coincident(g13,g15)
    c: Coincident(g9,g4)
FEATURE [Sketcher::SketchObject] Sketch057  label="buco interno per SWITCH"
  ArcFitTolerance = 1e-06
  AttachmentSupport = -> [XZ_Plane]
  ExternalGeometry = -> [Sketch]
  ExternalTypes = [0]
  FullyConstrained = true
  MakeInternals = false
  MapMode = 5
  Placement = pos=(0,0,0) rot=(1,0,0;1.5708rad)
  _ExternalGeoVersion = 0
  sketch-geometry (10):
    g0: GeomPoint [constr] X=-187.821 Y=29.2 Z=0
    g1: LineSegment [constr] StartX=-188.505 StartY=27.3206 StartZ=0 EndX=-193.203 EndY=29.0307 EndZ=0
    g2: LineSegment [constr] StartX=-190.809 StartY=35.6086 StartZ=0 EndX=-195.597 EndY=22.4529 EndZ=0
    g3: GeomPoint [constr] X=-193.203 Y=29.0307 Z=0
    g4: LineSegment [constr] StartX=-196.492 StartY=30.2278 StartZ=0 EndX=-189.914 EndY=27.8336 EndZ=0
    g5: LineSegment StartX=-194.098 StartY=36.8056 StartZ=0 EndX=-187.52 EndY=34.4115 EndZ=0
    g6: LineSegment StartX=-194.098 StartY=36.8056 StartZ=0 EndX=-198.886 EndY=23.6499 EndZ=0
    g7: LineSegment StartX=-187.52 StartY=34.4115 StartZ=0 EndX=-192.308 EndY=21.2558 EndZ=0
    g8: LineSegment StartX=-198.886 StartY=23.6499 StartZ=0 EndX=-192.308 EndY=21.2558 EndZ=0
    g9: LineSegment [constr] StartX=-187.821 StartY=29.2 StartZ=0 EndX=-188.505 EndY=27.3206 EndZ=0
  constraints (23):
    c: Symmetric(g-3,g-3,g0)
    c: Perpendicular(g1,g-3)
    c: Parallel(g2,g-3)
    c: Symmetric(g2,g2,g3)
    c: Perpendicular(g2,g4)
    c: Symmetric(g4,g4,g3)
    c: Distance(g2) = 14
    c: Distance(g4) = 7
    c: Distance(g1) = 5
    c: Parallel(g5,g4)
    c: Parallel(g7,g2)
    c: Symmetric(g5,g5,g2)
    c: Symmetric(g6,g6,g4)
    c: Symmetric(g7,g7,g4)
    c: Symmetric(g8,g8,g2)
    c: Coincident(g6,g5)
    c: Coincident(g7,g5)
    c: Coincident(g8,g7)
    c: Coincident(g3,g1)
    c: Coincident(g9,g0)
    c: Parallel(g9,g-3)
    c: Distance(g9) = 2
    c: Coincident(g1,g9)
FEATURE [Sketcher::SketchObject] Sketch058  label="buco esterno per SWITCH"
  ArcFitTolerance = 1e-06
  AttachmentSupport = -> [XZ_Plane]
  ExternalGeometry = -> [Sketch057]
  ExternalTypes = [0]
  FullyConstrained = true
  MakeInternals = false
  MapMode = 5
  Placement = pos=(0,0,0) rot=(1,0,0;1.5708rad)
  _ExternalGeoVersion = 0
  sketch-geometry (12):
    g0: GeomPoint [constr] X=-190.809 Y=35.6086 Z=0
    g1: GeomPoint [constr] X=-196.492 Y=30.2278 Z=0
    g2: GeomPoint [constr] X=-189.914 Y=27.8336 Z=0
    g3: GeomPoint [constr] X=-195.597 Y=22.4529 Z=0
    g4: GeomPoint [constr] X=-193.203 Y=29.0307 Z=0
    g5: LineSegment [constr] StartX=-192.006 StartY=32.3196 StartZ=0 EndX=-194.4 EndY=25.7418 EndZ=0
    g6: GeomPoint [constr] X=-193.203 Y=29.0307 Z=0
    g7: LineSegment [constr] StartX=-195.082 StartY=29.7148 StartZ=0 EndX=-191.324 EndY=28.3467 EndZ=0
    g8: LineSegment StartX=-193.885 StartY=33.0037 StartZ=0 EndX=-190.127 EndY=31.6356 EndZ=0
    g9: LineSegment StartX=-190.127 StartY=31.6356 StartZ=0 EndX=-192.521 EndY=25.0578 EndZ=0
    g10: LineSegment StartX=-196.28 StartY=26.4258 StartZ=0 EndX=-192.521 EndY=25.0578 EndZ=0
    g11: LineSegment StartX=-193.885 StartY=33.0037 StartZ=0 EndX=-196.28 EndY=26.4258 EndZ=0
  constraints (21):
    c: Symmetric(g-6,g-6,g3)
    c: Symmetric(g-4,g-6,g2)
    c: Symmetric(g-5,g-4,g0)
    c: Symmetric(g-5,g-6,g1)
    c: Symmetric(g1,g2,g4)
    c: Parallel(g5,g-4)
    c: Symmetric(g5,g5,g6)
    c: Perpendicular(g7,g5)
    c: Symmetric(g7,g7,g6)
    c: Distance(g5) = 7
    c: Distance(g7) = 4
    c: Parallel(g8,g7)
    c: Parallel(g11,g5)
    c: Symmetric(g8,g8,g5)
    c: Symmetric(g9,g9,g7)
    c: Symmetric(g10,g10,g5)
    c: Symmetric(g11,g11,g7)
    c: Coincident(g11,g8)
    c: Coincident(g9,g8)
    c: Coincident(g9,g10)
    c: Coincident(g6,g4)
FEATURE [Part::Extrusion] Extrude060  label="Extrude buco interno per SWITCH destro"
  Base = -> Sketch057
  Dir = (0,-1,2e-16)
  DirMode = 2
  FaceMakerClass = Part::FaceMakerBullseye
  FaceMakerMode = 3
  InnerWireTaper = 1
  LengthFwd = 13.2
  LengthRev = 0
  Placement = pos=(0,2.6,0) rot=(0,0,1;0rad)
  Solid = true
  Symmetric = false
FEATURE [Part::Extrusion] Extrude061  label="Extrude buco esterno per SWITCH destro"
  Base = -> Sketch058
  Dir = (0,-1,2e-16)
  DirMode = 2
  FaceMakerClass = Part::FaceMakerBullseye
  FaceMakerMode = 3
  InnerWireTaper = 1
  LengthFwd = 2
  LengthRev = 0
  Placement = pos=(0,-10.6,0) rot=(0,0,1;0rad)
  Solid = true
  Symmetric = false
FEATURE [Sketcher::SketchObject] Sketch059  label="buco per spazio introduzione SWITCH"
  ArcFitTolerance = 1e-06
  AttachmentSupport = -> [XZ_Plane]
  ExternalGeometry = -> [Sketch057,Sketch010]
  ExternalTypes = [0]
  FullyConstrained = true
  MakeInternals = false
  MapMode = 5
  Placement = pos=(0,0,0) rot=(1,0,0;1.5708rad)
  _ExternalGeoVersion = 0
  sketch-geometry (8):
    g0: LineSegment [constr] StartX=-201.368 StartY=36.3521 StartZ=0 EndX=-195.094 EndY=34.0687 EndZ=0
    g1: LineSegment [constr] StartX=-194.098 StartY=36.8056 StartZ=0 EndX=-195.094 EndY=34.0687 EndZ=0
    g2: LineSegment StartX=-198.658 StartY=24.2771 StartZ=0 EndX=-199.654 EndY=21.5401 EndZ=0
    g3: LineSegment StartX=-199.654 StartY=21.5401 StartZ=0 EndX=-181.196 EndY=14.822 EndZ=0
    g4: LineSegment StartX=-181.196 StartY=14.822 StartZ=0 EndX=-180.2 EndY=17.559 EndZ=0
    g5: LineSegment StartX=-180.2 StartY=17.559 StartZ=0 EndX=-198.658 EndY=24.2771 EndZ=0
    g6: LineSegment [constr] StartX=-204.932 StartY=26.5605 StartZ=0 EndX=-198.658 EndY=24.2771 EndZ=0
    g7: LineSegment [constr] StartX=-198.658 StartY=24.2771 StartZ=0 EndX=-199.654 EndY=21.5401 EndZ=0
  constraints (20):
    c: Parallel(g1,g-3)
    c: Parallel(g0,g-4)
    c: Coincident(g0,g-4)
    c: Coincident(g1,g-3)
    c: Coincident(g0,g1)
    c: Coincident(g3,g2)
    c: Coincident(g4,g3)
    c: Coincident(g5,g4)
    c: Coincident(g5,g2)
    c: Parallel(g5,g-5)
    c: Parallel(g3,g-5)
    c: Parallel(g4,g-6)
    c: DistanceX(g-6,g4) = 0
    c: Coincident(g6,g-5)
    c: Equal(g6,g0)
    c: Coincident(g7,g6)
    c: Equal(g7,g1)
    c: Tangent(g7,g-3)
    c: Coincident(g2,g6)
    c: Coincident(g2,g7)
FEATURE [Part::Extrusion] Extrude062  label="Extrude buco per spazio introduzione SWITCH"
  Base = -> Sketch059
  Dir = (0,-1,2e-16)
  DirMode = 2
  FaceMakerClass = Part::FaceMakerBullseye
  FaceMakerMode = 3
  InnerWireTaper = 1
  LengthFwd = 13.2
  LengthRev = 0
  Solid = true
  Symmetric = true
FEATURE [Part::Extrusion] Extrude063  label="Extrude buco interno per SWITCH sinistro"
  Base = -> Sketch057
  Dir = (0,-1,2e-16)
  DirMode = 2
  FaceMakerClass = Part::FaceMakerBullseye
  FaceMakerMode = 3
  InnerWireTaper = 1
  LengthFwd = 13.2
  LengthRev = 0
  Placement = pos=(0,10.6,0) rot=(0,0,1;0rad)
  Solid = true
  Symmetric = false
FEATURE [Part::Extrusion] Extrude064  label="Extrude buco esterno per SWITCH sinistro"
  Base = -> Sketch058
  Dir = (0,-1,2e-16)
  DirMode = 2
  FaceMakerClass = Part::FaceMakerBullseye
  FaceMakerMode = 3
  InnerWireTaper = 1
  LengthFwd = 2
  LengthRev = 0
  Placement = pos=(0,12.6,0) rot=(0,0,1;0rad)
  Solid = true
  Symmetric = false
FEATURE [Sketcher::SketchObject] Sketch061  label="struttura esterna blocco switch"
  ArcFitTolerance = 1e-06
  AttachmentSupport = -> [XZ_Plane003]
  ExternalTypes = [0]
  FullyConstrained = true
  MakeInternals = false
  MapMode = 5
  Placement = pos=(0,0,0) rot=(1,0,0;1.5708rad)
  _ExternalGeoVersion = 0
  sketch-geometry (5):
    g0: LineSegment StartX=-1 StartY=-5.1 StartZ=0 EndX=1 EndY=-5.1 EndZ=0
    g1: LineSegment StartX=1 StartY=-5.1 StartZ=0 EndX=1 EndY=5.1 EndZ=0
    g2: LineSegment StartX=1 StartY=5.1 StartZ=0 EndX=-1 EndY=5.1 EndZ=0
    g3: LineSegment StartX=-1 StartY=5.1 StartZ=0 EndX=-1 EndY=-5.1 EndZ=0
    g4: GeomPoint [constr] X=0 Y=0 Z=0
  constraints (12):
    c: Coincident(g0,g1)
    c: Coincident(g1,g2)
    c: Coincident(g2,g3)
    c: Coincident(g3,g0)
    c: Horizontal(g0)
    c: Horizontal(g2)
    c: Vertical(g1)
    c: Vertical(g3)
    c: Symmetric(g2,g0,g4)
    c: Distance(g1,g3) = 2
    c: Distance(g0,g2) = 10.2
    c: Coincident(g4,g-1)
FEATURE [Sketcher::SketchObject] Sketch062  label="struttura interna blocco switch"
  ArcFitTolerance = 1e-06
  AttachmentSupport = -> [XZ_Plane003]
  ExternalGeometry = -> [Sketch061]
  ExternalTypes = [0]
  FullyConstrained = true
  MakeInternals = false
  MapMode = 5
  Placement = pos=(0,0,0) rot=(1,0,0;1.5708rad)
  _ExternalGeoVersion = 0
  sketch-geometry (5):
    g0: LineSegment StartX=-1 StartY=3.1 StartZ=0 EndX=-1 EndY=-3.1 EndZ=0
    g1: LineSegment StartX=-1 StartY=-3.1 StartZ=0 EndX=1 EndY=-3.1 EndZ=0
    g2: LineSegment StartX=1 StartY=-3.1 StartZ=0 EndX=1 EndY=3.1 EndZ=0
    g3: LineSegment StartX=1 StartY=3.1 StartZ=0 EndX=-1 EndY=3.1 EndZ=0
    g4: GeomPoint [constr] X=0 Y=0 Z=0
  constraints (12):
    c: Coincident(g0,g1)
    c: Coincident(g1,g2)
    c: Coincident(g2,g3)
    c: Coincident(g3,g0)
    c: Vertical(g0)
    c: Vertical(g2)
    c: Horizontal(g1)
    c: Horizontal(g3)
    c: Symmetric(g2,g0,g4)
    c: Coincident(g4,g-1)
    c: Distance(g0) = 6.2
    c: Equal(g3,g-3)
FEATURE [Sketcher::SketchObject] Sketch063  label="blocchi tra switch"
  ArcFitTolerance = 1e-06
  AttachmentSupport = -> [XZ_Plane003]
  ExternalGeometry = -> [Sketch061,Sketch062]
  ExternalTypes = [0]
  FullyConstrained = true
  MakeInternals = false
  MapMode = 5
  Placement = pos=(0,0,0) rot=(1,0,0;1.5708rad)
  _ExternalGeoVersion = 0
  sketch-geometry (8):
    g0: LineSegment StartX=-3 StartY=5.1 StartZ=0 EndX=-1 EndY=5.1 EndZ=0
    g1: LineSegment StartX=-1 StartY=5.1 StartZ=0 EndX=-1 EndY=3.1 EndZ=0
    g2: LineSegment StartX=-1 StartY=3.1 StartZ=0 EndX=-3 EndY=3.1 EndZ=0
    g3: LineSegment StartX=-3 StartY=3.1 StartZ=0 EndX=-3 EndY=5.1 EndZ=0
    g4: LineSegment StartX=-3 StartY=-3.1 StartZ=0 EndX=-1 EndY=-3.1 EndZ=0
    g5: LineSegment StartX=-1 StartY=-3.1 StartZ=0 EndX=-1 EndY=-5.1 EndZ=0
    g6: LineSegment StartX=-1 StartY=-5.1 StartZ=0 EndX=-3 EndY=-5.1 EndZ=0
    g7: LineSegment StartX=-3 StartY=-5.1 StartZ=0 EndX=-3 EndY=-3.1 EndZ=0
  constraints (20):
    c: Horizontal(g0)
    c: Coincident(g1,g0)
    c: Coincident(g2,g1)
    c: Horizontal(g2)
    c: Coincident(g3,g2)
    c: Coincident(g3,g0)
    c: Vertical(g3)
    c: Horizontal(g4)
    c: Coincident(g5,g4)
    c: Coincident(g6,g5)
    c: Horizontal(g6)
    c: Coincident(g7,g6)
    c: Coincident(g7,g4)
    c: Vertical(g7)
    c: Coincident(g0,g-4)
    c: Coincident(g1,g-5)
    c: Coincident(g4,g-6)
    c: Coincident(g5,g-7)
    c: Distance(g0) = 2
    c: Distance(g4) = 2
FEATURE [Sketcher::SketchObject] Sketch066  label="piano per rampino"
  ArcFitTolerance = 1e-06
  AttachmentSupport = -> [XZ_Plane002]
  ExternalGeometry = -> [Sketch045]
  ExternalTypes = [0]
  FullyConstrained = true
  MakeInternals = false
  MapMode = 5
  Placement = pos=(0,0,0) rot=(1,0,0;1.5708rad)
  _ExternalGeoVersion = 0
  sketch-geometry (4):
    g0: LineSegment StartX=5.4 StartY=5.1 StartZ=0 EndX=5.4 EndY=3.9 EndZ=0
    g1: LineSegment StartX=5.4 StartY=3.9 StartZ=0 EndX=7 EndY=3.9 EndZ=0
    g2: LineSegment StartX=7 StartY=3.9 StartZ=0 EndX=7 EndY=5.1 EndZ=0
    g3: LineSegment StartX=7 StartY=5.1 StartZ=0 EndX=5.4 EndY=5.1 EndZ=0
  constraints (11):
    c: Coincident(g0,g1)
    c: Coincident(g1,g2)
    c: Coincident(g2,g3)
    c: Coincident(g3,g0)
    c: Vertical(g0)
    c: Vertical(g2)
    c: Horizontal(g1)
    c: Horizontal(g3)
    c: Distance(g0,g2) = 1.6
    c: Distance(g1,g3) = 1.2
    c: Coincident(g2,g-3)
FEATURE [Sketcher::SketchObject] Sketch064  label="rampini_per_serraggio_struttura"
  ArcFitTolerance = 1e-06
  AttachmentSupport = -> [XZ_Plane002]
  ExternalGeometry = -> [Sketch066,Sketch045]
  ExternalTypes = [0]
  FullyConstrained = true
  MakeInternals = false
  MapMode = 5
  Placement = pos=(0,0,0) rot=(1,0,0;1.5708rad)
  _ExternalGeoVersion = 0
  sketch-geometry (7):
    g0: LineSegment StartX=7 StartY=5.1 StartZ=0 EndX=7 EndY=3.9 EndZ=0
    g1: LineSegment StartX=7 StartY=3.9 StartZ=0 EndX=9 EndY=3.9 EndZ=0
    g2: LineSegment StartX=7 StartY=5.1 StartZ=0 EndX=7 EndY=5.1 EndZ=0
    g3: LineSegment StartX=7 StartY=5.1 StartZ=0 EndX=7 EndY=7.5 EndZ=0
    g4: LineSegment StartX=9 StartY=5.1 StartZ=0 EndX=9 EndY=3.9 EndZ=0
    g5: LineSegment StartX=7 StartY=7.5 StartZ=0 EndX=9 EndY=7.5 EndZ=0
    g6: LineSegment StartX=9 StartY=7.5 StartZ=0 EndX=9 EndY=5.1 EndZ=0
  constraints (20):
    c: Vertical(g0)
    c: Coincident(g1,g0)
    c: Horizontal(g1)
    c: Coincident(g2,g0)
    c: Horizontal(g2)
    c: Coincident(g3,g2)
    c: Vertical(g3)
    c: Coincident(g5,g3)
    c: Coincident(g4,g6)
    c: Coincident(g4,g1)
    c: Vertical(g4)
    c: Coincident(g0,g-3)
    c: DistanceY(g-4,g3) = 2.4
    c: DistanceX(g1,g1) = 2
    c: DistanceY(g2,g6) = 0
    c: DistanceX(g2,g2) = 0
    c: DistanceY(g0,g0) = 1.2
    c: Coincident(g5,g6)
    c: Horizontal(g5)
    c: Vertical(g6)
FEATURE [Sketcher::SketchObject] Sketch067  label="perno per blocco switch"
  ArcFitTolerance = 1e-06
  AttachmentSupport = -> [XZ_Plane]
  ExternalGeometry = -> [Sketch,Sketch010]
  ExternalTypes = [0]
  FullyConstrained = true
  MakeInternals = false
  MapMode = 5
  Placement = pos=(0,0,0) rot=(1,0,0;1.5708rad)
  _ExternalGeoVersion = 0
  sketch-geometry (14):
    g0: LineSegment StartX=-191.073 StartY=24.9429 StartZ=0 EndX=-185.81 EndY=23.0276 EndZ=0
    g1: LineSegment StartX=-183.76 StartY=23.9839 StartZ=0 EndX=-182.392 EndY=27.7427 EndZ=0
    g2: LineSegment StartX=-183.348 StartY=29.7934 StartZ=0 EndX=-188.61 EndY=31.7087 EndZ=0
    g3: LineSegment StartX=-188.61 StartY=31.7087 StartZ=0 EndX=-191.073 EndY=24.9429 EndZ=0
    g4: GeomPoint [constr] X=-186.459 Y=27.0946 Z=0
    g5: LineSegment StartX=-189.022 StartY=25.8992 StartZ=0 EndX=-185.263 EndY=24.5311 EndZ=0
    g6: LineSegment StartX=-185.263 StartY=24.5311 StartZ=0 EndX=-183.895 EndY=28.2899 EndZ=0
    g7: LineSegment StartX=-183.895 StartY=28.2899 StartZ=0 EndX=-187.654 EndY=29.658 EndZ=0
    g8: LineSegment StartX=-187.654 StartY=29.658 StartZ=0 EndX=-189.022 EndY=25.8992 EndZ=0
    g9: GeomPoint [constr] X=-186.459 Y=27.0946 Z=0
    g10: ArcOfCircle CenterX=-185.263 CenterY=24.5311 CenterZ=0 NormalX=0 NormalY=0 NormalZ=1 AngleXU=0 Radius=1.6 StartAngle=4.36332 EndAngle=5.93412
    g11: GeomPoint [constr] X=-184.307 Y=22.4804 Z=0
    g12: ArcOfCircle CenterX=-183.895 CenterY=28.2899 CenterZ=0 NormalX=0 NormalY=0 NormalZ=1 AngleXU=0 Radius=1.6 StartAngle=5.93412 EndAngle=7.50492
    g13: GeomPoint [constr] X=-181.844 Y=29.2462 Z=0
  constraints (30):
    c: Coincident(g2,g3)
    c: Coincident(g3,g0)
    c: Symmetric(g13,g0,g4)
    c: Distance(g11,g3) = 7.2
    c: Distance(g0,g2) = 7.2
    c: Parallel(g3,g1)
    c: Parallel(g2,g0)
    c: Perpendicular(g2,g3)
    c: Coincident(g5,g6)
    c: Coincident(g6,g7)
    c: Coincident(g7,g8)
    c: Coincident(g8,g5)
    c: Symmetric(g7,g5,g9)
    c: Distance(g6,g8) = 4
    c: Distance(g5,g7) = 4
    c: Coincident(g9,g4)
    c: Parallel(g8,g6)
    c: Parallel(g7,g5)
    c: Perpendicular(g7,g8)
    c: Tangent(g8,g-3)
    c: Tangent(g2,g-4)
    c: PointOnObject(g11,g1)
    c: PointOnObject(g11,g0)
    c: Tangent(g1,g10) = -1.5708
    c: Tangent(g0,g10) = -1.5708
    c: PointOnObject(g13,g1)
    c: Tangent(g1,g12) = -1.5708
    c: Tangent(g2,g12) = -1.5708
    c: Equal(g10,g12)
    c: Coincident(g10,g5)
FEATURE [Part::Extrusion] Extrude072  label="Extrude perno per blocco switch"
  Base = -> Sketch067
  Dir = (0,-1,2e-16)
  DirMode = 2
  FaceMakerClass = Part::FaceMakerBullseye
  FaceMakerMode = 3
  InnerWireTaper = 1
  LengthFwd = 25.2
  LengthRev = 0
  Solid = true
  Symmetric = true
FEATURE [Part::MultiFuse] Fusion
  Refine = true
  Shapes = -> [Extrude,Sweep,Extrude007,Extrude011,Extrude005,Extrude012,Extrude013,Extrude016,Extrude031,Extrude039,Extrude045,Extrude072]
FEATURE [Part::Cut] Cut
  Base = -> Fusion
  Refine = true
  Tool = -> Extrude001
FEATURE [Part::Cut] Cut001
  Base = -> Cut
  Refine = true
  Tool = -> Extrude004
FEATURE [Part::Cut] Cut002
  Base = -> Cut001
  Refine = true
  Tool = -> Extrude006
FEATURE [Part::Cut] Cut003
  Base = -> Cut002
  Refine = true
  Tool = -> Extrude008
FEATURE [Part::Cut] Cut004
  Base = -> Cut003
  Refine = true
  Tool = -> Extrude009
FEATURE [Part::Cut] Cut005
  Base = -> Cut004
  Refine = true
  Tool = -> Extrude010
FEATURE [Part::Cut] Cut006
  Base = -> Cut005
  Refine = true
  Tool = -> Extrude014
FEATURE [Part::Cut] Cut007
  Base = -> Cut006
  Refine = true
  Tool = -> Extrude015
FEATURE [Part::Cut] Cut008
  Base = -> Cut007
  Refine = true
  Tool = -> Extrude018
FEATURE [Part::Cut] Cut009
  Base = -> Cut008
  Refine = true
  Tool = -> Extrude019
FEATURE [Part::Cut] Cut010
  Base = -> Cut009
  Refine = true
  Tool = -> Extrude020
FEATURE [Part::Cut] Cut011
  Base = -> Cut010
  Refine = true
  Tool = -> Extrude021
FEATURE [Part::Cut] Cut012
  Base = -> Cut011
  Refine = true
  Tool = -> Extrude022
FEATURE [Part::Cut] Cut013
  Base = -> Cut012
  Refine = true
  Tool = -> Extrude023
FEATURE [Part::Cut] Cut014
  Base = -> Cut013
  Refine = true
  Tool = -> Extrude032
FEATURE [Part::Cut] Cut015
  Base = -> Cut014
  Refine = true
  Tool = -> Extrude033
FEATURE [Part::Cut] Cut016
  Base = -> Cut015
  Refine = true
  Tool = -> Extrude034
FEATURE [Part::Cut] Cut017
  Base = -> Cut016
  Refine = true
  Tool = -> Extrude035
FEATURE [Part::Cut] Cut018
  Base = -> Cut017
  Refine = true
  Tool = -> Extrude036
FEATURE [Part::Cut] Cut019
  Base = -> Cut018
  Refine = true
  Tool = -> Extrude037
FEATURE [Part::Cut] Cut020
  Base = -> Cut019
  Refine = true
  Tool = -> Extrude030
FEATURE [Part::Cut] Cut022
  Base = -> Cut020
  Refine = true
  Tool = -> Extrude038
FEATURE [Part::Cut] Cut023
  Base = -> Cut022
  Refine = true
  Tool = -> Extrude041
FEATURE [Part::Cut] Cut024
  Base = -> Cut023
  Refine = true
  Tool = -> Extrude040
FEATURE [Part::Cut] Cut025
  Base = -> Cut024
  Refine = true
  Tool = -> Extrude042
FEATURE [Part::Cut] Cut026
  Base = -> Cut025
  Refine = true
  Tool = -> Extrude043
FEATURE [Part::Cut] Cut027
  Base = -> Cut026
  Refine = true
  Tool = -> Extrude044
FEATURE [Part::Cut] Cut028
  Base = -> Cut027
  Refine = true
  Tool = -> Extrude046
FEATURE [Part::Cut] Cut029
  Base = -> Cut028
  Refine = true
  Tool = -> Extrude047
FEATURE [Part::Cut] Cut033
  Base = -> Cut029
  Refine = true
  Tool = -> Extrude055
FEATURE [Part::Cut] Cut034
  Base = -> Cut033
  Refine = true
  Tool = -> Extrude056
FEATURE [Part::Cut] Cut035
  Base = -> Cut034
  Refine = true
  Tool = -> Extrude057
FEATURE [Part::Cut] Cut037
  Base = -> Cut035
  Refine = true
  Tool = -> Extrude060
FEATURE [Part::Cut] Cut038
  Base = -> Cut037
  Refine = true
  Tool = -> Extrude061
FEATURE [Part::Cut] Cut039
  Base = -> Cut038
  Refine = true
  Tool = -> Extrude063
FEATURE [Part::Cut] Cut040
  Base = -> Cut039
  Refine = true
  Tool = -> Extrude064
FEATURE [Part::Cut] Cut041
  Base = -> Cut040
  Refine = true
  Tool = -> Extrude062
FEATURE [Sketcher::SketchObject] Sketch068  label="base con smusso sopra neopixel"
  ArcFitTolerance = 1e-06
  AttachmentSupport = -> [YZ_Plane002]
  ExternalTypes = [0]
  FullyConstrained = true
  MakeInternals = false
  MapMode = 5
  Placement = pos=(0,0,0) rot=(0.57735,0.57735,0.57735;2.0944rad)
  _ExternalGeoVersion = 0
  sketch-geometry (5):
    g0: LineSegment StartX=-9.5 StartY=-6.1 StartZ=0 EndX=9.5 EndY=-6.1 EndZ=0
    g1: LineSegment StartX=9.5 StartY=-6.1 StartZ=0 EndX=9.5 EndY=6.1 EndZ=0
    g2: LineSegment StartX=9.5 StartY=6.1 StartZ=0 EndX=-9.5 EndY=6.1 EndZ=0
    g3: LineSegment StartX=-9.5 StartY=6.1 StartZ=0 EndX=-9.5 EndY=-6.1 EndZ=0
    g4: GeomPoint [constr] X=0 Y=0 Z=0
  constraints (12):
    c: Coincident(g0,g1)
    c: Coincident(g1,g2)
    c: Coincident(g2,g3)
    c: Coincident(g3,g0)
    c: Horizontal(g0)
    c: Horizontal(g2)
    c: Vertical(g1)
    c: Vertical(g3)
    c: Symmetric(g2,g0,g4)
    c: Distance(g1,g3) = 19
    c: Distance(g0,g2) = 12.2
    c: Coincident(g4,g-1)
FEATURE [Sketcher::SketchObject] Sketch069  label="cilindro minore"
  ArcFitTolerance = 1e-06
  AttachmentSupport = -> [XZ_Plane004]
  ExternalTypes = [0]
  FullyConstrained = true
  MakeInternals = false
  MapMode = 5
  Placement = pos=(0,0,0) rot=(1,0,0;1.5708rad)
  _ExternalGeoVersion = 0
  sketch-geometry (1):
    g0: Circle CenterX=0 CenterY=0 CenterZ=0 NormalX=0 NormalY=0 NormalZ=1 AngleXU=0 Radius=5.8
  constraints (2):
    c: Diameter(g0) = 11.6
    c: Coincident(g0,g-1)
FEATURE [Sketcher::SketchObject] Sketch070  label="cilindro maggiore"
  ArcFitTolerance = 1e-06
  AttachmentSupport = -> [XZ_Plane004]
  ExternalGeometry = -> [Sketch069]
  ExternalTypes = [0]
  FullyConstrained = true
  MakeInternals = false
  MapMode = 5
  Placement = pos=(0,0,0) rot=(1,0,0;1.5708rad)
  _ExternalGeoVersion = 0
  sketch-geometry (1):
    g0: Circle CenterX=0 CenterY=0 CenterZ=0 NormalX=0 NormalY=0 NormalZ=1 AngleXU=0 Radius=6.5
  constraints (2):
    c: Coincident(g0,g-1)
    c: Diameter(g0) = 13
FEATURE [Sketcher::SketchObject] Sketch071  label="buco interno"
  ArcFitTolerance = 1e-06
  AttachmentSupport = -> [XZ_Plane004]
  ExternalGeometry = -> [Sketch069]
  ExternalTypes = [0]
  FullyConstrained = true
  MakeInternals = false
  MapMode = 5
  Placement = pos=(0,0,0) rot=(1,0,0;1.5708rad)
  _ExternalGeoVersion = 0
  sketch-geometry (1):
    g0: Circle CenterX=0 CenterY=0 CenterZ=0 NormalX=0 NormalY=0 NormalZ=1 AngleXU=0 Radius=5
  constraints (2):
    c: Coincident(g0,g-1)
    c: Diameter(g0) = 10
FEATURE [PartDesign::Pad] Pad
  Direction = (0,-1,2e-16)
  Length = 1.2
  Length2 = 10
  Placement = pos=(0,0,0) rot=(1,0,0;1.5708rad)
  Profile = -> Sketch070
  ReferenceAxis = -> Sketch070 [N_Axis]
  Refine = true
  SideType = 0
  Suppressed = false
  Type = 0
  Type2 = 0
FEATURE [PartDesign::Pad] Pad001
  BaseFeature = -> Pad
  Direction = (0,-1,2e-16)
  Length = 5.6
  Length2 = 10
  Placement = pos=(0,0,0) rot=(1,0,0;1.5708rad)
  Profile = -> Sketch069
  ReferenceAxis = -> Sketch069 [N_Axis]
  Refine = true
  SideType = 0
  Suppressed = false
  Type = 0
  Type2 = 0
FEATURE [PartDesign::Pocket] Pocket
  BaseFeature = -> Pad001
  Direction = (0,1,-2e-16)
  Length = 7
  Length2 = 5
  Placement = pos=(0,0,0) rot=(1,0,0;1.5708rad)
  Profile = -> Sketch071
  ReferenceAxis = -> Sketch071 [N_Axis]
  Refine = true
  SideType = 2
  Suppressed = false
  Type = 0
  Type2 = 0
FEATURE [PartDesign::Fillet] Fillet
  Base = -> Pocket [Face7]
  BaseFeature = -> Pocket
  Placement = pos=(0,0,0) rot=(1,0,0;1.5708rad)
  Radius = 1
  Refine = true
  SupportTransform = false
  Suppressed = false
  UseAllEdges = false
FEATURE [PartDesign::Body] Body004  label="pulsanti lato sinistro"
  AllowCompound = false
  Group = -> [Sketch069,Sketch070,Sketch071,Pad,Pad001,Pocket,Fillet]
  Origin = -> Origin004
  Tip = -> Fillet
FEATURE [Sketcher::SketchObject] Sketch072  label="buco per saldature e diodo driver solenoide"
  ArcFitTolerance = 1e-06
  AttachmentSupport = -> [XZ_Plane]
  ExternalGeometry = -> [Sketch038]
  ExternalTypes = [0]
  FullyConstrained = true
  MakeInternals = false
  MapMode = 5
  Placement = pos=(0,0,0) rot=(1,0,0;1.5708rad)
  _ExternalGeoVersion = 0
  sketch-geometry (4):
    g0: LineSegment StartX=-214.165 StartY=-46.5549 StartZ=0 EndX=-209.093 EndY=-35.6792 EndZ=0
    g1: LineSegment StartX=-209.093 StartY=-35.6792 StartZ=0 EndX=-209.456 EndY=-35.5101 EndZ=0
    g2: LineSegment StartX=-209.456 StartY=-35.5101 StartZ=0 EndX=-214.527 EndY=-46.3858 EndZ=0
    g3: LineSegment StartX=-214.527 StartY=-46.3858 StartZ=0 EndX=-214.165 EndY=-46.5549 EndZ=0
  constraints (11):
    c: Coincident(g1,g0)
    c: Coincident(g2,g1)
    c: Coincident(g3,g2)
    c: Coincident(g3,g0)
    c: Parallel(g-3,g0)
    c: Parallel(g0,g2)
    c: Perpendicular(g0,g3)
    c: Perpendicular(g1,g0)
    c: Distance(g3) = 0.4
    c: Distance(g2) = 12
    c: Coincident(g0,g-3)
FEATURE [Part::Extrusion] Extrude074  label="Extrude buco per saldature e diodo driver solenoide"
  Base = -> Sketch072
  Dir = (0,-1,2e-16)
  DirMode = 2
  FaceMakerClass = Part::FaceMakerBullseye
  FaceMakerMode = 3
  InnerWireTaper = 1
  LengthFwd = 14.6
  LengthRev = 0
  Solid = true
  Symmetric = true
FEATURE [Part::Cut] Cut042
  Base = -> Cut041
  Refine = true
  Tool = -> Extrude074
FEATURE [Sketcher::SketchObject] Sketch073  label="fori slargati blocco solenoide"
  ArcFitTolerance = 1e-06
  AttachmentSupport = -> [XY_Plane]
  ExternalGeometry = -> [Sketch030]
  ExternalTypes = [0]
  FullyConstrained = true
  MakeInternals = false
  MapMode = 5
  _ExternalGeoVersion = 0
  sketch-geometry (2):
    g0: Circle CenterX=-152.209 CenterY=6.95 CenterZ=0 NormalX=0 NormalY=0 NormalZ=1 AngleXU=0 Radius=3.7
    g1: Circle CenterX=-130.41 CenterY=-6.95 CenterZ=0 NormalX=0 NormalY=0 NormalZ=1 AngleXU=0 Radius=3.7
  constraints (4):
    c: Diameter(g0) = 7.4
    c: Coincident(g0,g-3)
    c: Diameter(g1) = 7.4
    c: Coincident(g1,g-4)
FEATURE [Part::Extrusion] Extrude075  label="Extrude fori slargati blocco solenoide"
  Base = -> Sketch073
  Dir = (0,0,1)
  DirMode = 2
  FaceMakerClass = Part::FaceMakerBullseye
  FaceMakerMode = 3
  InnerWireTaper = 1
  LengthFwd = 1.5
  LengthRev = 0
  Placement = pos=(0,0,36.4) rot=(0,0,1;0rad)
  Solid = true
  Symmetric = false
FEATURE [Part::Cut] Cut043
  Base = -> Cut042
  Refine = true
  Tool = -> Extrude075
FEATURE [Sketcher::SketchObject] Sketch074  label="lato sx pistola"
  ArcFitTolerance = 1e-06
  AttachmentSupport = -> [XZ_Plane]
  ExternalGeometry = -> [Sketch016,Sketch,Sketch058]
  ExternalTypes = [0]
  FullyConstrained = true
  MakeInternals = false
  MapMode = 5
  Placement = pos=(0,0,0) rot=(1,0,0;1.5708rad)
  _ExternalGeoVersion = 0
  sketch-geometry (37):
    g0: LineSegment StartX=-82.8 StartY=3.2 StartZ=0 EndX=0 EndY=3.2 EndZ=0
    g1: LineSegment StartX=-82.8 StartY=3.2 StartZ=0 EndX=-82.8 EndY=6.2 EndZ=0
    g2: LineSegment [constr] StartX=-107.6 StartY=18 StartZ=0 EndX=-107.6 EndY=20 EndZ=0
    g3: LineSegment [constr] StartX=-132.428 StartY=18 StartZ=0 EndX=-132.428 EndY=20 EndZ=0
    g4: LineSegment StartX=-132.428 StartY=20 StartZ=0 EndX=-107.6 EndY=20 EndZ=0
    g5: ArcOfCircle CenterX=-107.6 CenterY=4 CenterZ=0 NormalX=0 NormalY=0 NormalZ=1 AngleXU=0 Radius=16 StartAngle=0.137937 EndAngle=1.5708
    g6: LineSegment StartX=-82.8 StartY=6.2 StartZ=0 EndX=-91.752 EndY=6.2 EndZ=0
    g7: LineSegment [constr] StartX=-145.743 StartY=8.32624 StartZ=0 EndX=-147.645 EndY=8.94427 EndZ=0
    g8: ArcOfCircle CenterX=-132.428 CenterY=4 CenterZ=0 NormalX=0 NormalY=0 NormalZ=1 AngleXU=0 Radius=16 StartAngle=1.5708 EndAngle=2.82743
    g9: LineSegment StartX=-215.932 StartY=-80.4316 StartZ=0 EndX=-176.685 EndY=-80.4316 EndZ=0
    g10: LineSegment StartX=-147.645 StartY=8.94427 StartZ=0 EndX=-176.685 EndY=-80.4316 EndZ=0
    g11: LineSegment [constr] StartX=-193.988 StartY=-2.33927 StartZ=0 EndX=-192.176 EndY=-3.18451 EndZ=0
    g12: LineSegment [constr] StartX=-217.232 StartY=-52.1862 StartZ=0 EndX=-215.42 EndY=-53.0314 EndZ=0
    g13: LineSegment StartX=-192.176 StartY=-3.18451 StartZ=0 EndX=-215.42 EndY=-53.0314 EndZ=0
    g14: ArcOfCircle CenterX=-184.801 CenterY=-67.3089 CenterZ=0 NormalX=0 NormalY=0 NormalZ=1 AngleXU=0 Radius=33.7833 StartAngle=2.70526 EndAngle=3.54053
    g15: ArcOfCircle CenterX=-207.583 CenterY=4 CenterZ=0 NormalX=0 NormalY=0 NormalZ=1 AngleXU=0 Radius=17 StartAngle=5.84685 EndAngle=7.56663
    g16: LineSegment StartX=-202.765 StartY=20.303 StartZ=0 EndX=-195.887 EndY=39.2 EndZ=0
    g17: LineSegment [constr] StartX=-193.885 StartY=33.0037 StartZ=0 EndX=-197.644 EndY=34.3718 EndZ=0
    g18: LineSegment StartX=-195.887 StartY=39.2 StartZ=0 EndX=0 EndY=39.2 EndZ=0
    g19: LineSegment StartX=0 StartY=3.2 StartZ=0 EndX=0 EndY=39.2 EndZ=0
    g20: LineSegment StartX=-189.939 StartY=31.5672 StartZ=0 EndX=-192.333 EndY=24.9893 EndZ=0
    g21: LineSegment StartX=-196.467 StartY=26.4942 StartZ=0 EndX=-194.073 EndY=33.0721 EndZ=0
    g22: Circle CenterX=-213.443 CenterY=-76.8316 CenterZ=0 NormalX=0 NormalY=0 NormalZ=1 AngleXU=0 Radius=1.8
    g23: Circle CenterX=-179.305 CenterY=-76.8316 CenterZ=0 NormalX=0 NormalY=0 NormalZ=1 AngleXU=0 Radius=1.8
    g24: Circle CenterX=-184.08 CenterY=34.8 CenterZ=0 NormalX=0 NormalY=0 NormalZ=1 AngleXU=0 Radius=1.8
    g25: Circle CenterX=-78.51 CenterY=34.8 CenterZ=0 NormalX=0 NormalY=0 NormalZ=1 AngleXU=0 Radius=1.8
    g26: Circle CenterX=-78.51 CenterY=7.6 CenterZ=0 NormalX=0 NormalY=0 NormalZ=1 AngleXU=0 Radius=1.8
    g27: Circle CenterX=-5.6 CenterY=34.8 CenterZ=0 NormalX=0 NormalY=0 NormalZ=1 AngleXU=0 Radius=1.8
    g28: Circle CenterX=-5.6 CenterY=7.6 CenterZ=0 NormalX=0 NormalY=0 NormalZ=1 AngleXU=0 Radius=1.8
    g29: LineSegment StartX=-190.127 StartY=31.6356 StartZ=0 EndX=-189.939 EndY=31.5672 EndZ=0
    g30: LineSegment StartX=-194.073 StartY=33.0721 StartZ=0 EndX=-193.885 EndY=33.0037 EndZ=0
    g31: LineSegment StartX=-193.885 StartY=33.0037 StartZ=0 EndX=-190.127 EndY=31.6356 EndZ=0
    g32: LineSegment StartX=-196.467 StartY=26.4942 StartZ=0 EndX=-192.333 EndY=24.9893 EndZ=0
    g33: Circle CenterX=-19 CenterY=21.2 CenterZ=0 NormalX=0 NormalY=0 NormalZ=1 AngleXU=0 Radius=6.3
    g34: Circle CenterX=-42 CenterY=21.2 CenterZ=0 NormalX=0 NormalY=0 NormalZ=1 AngleXU=0 Radius=6.3
    g35: Circle CenterX=-65 CenterY=21.2 CenterZ=0 NormalX=0 NormalY=0 NormalZ=1 AngleXU=0 Radius=6.3
    g36: LineSegment [constr] StartX=-4 StartY=21.2 StartZ=0 EndX=-65 EndY=21.2 EndZ=0
  constraints (96):
    c: Coincident(g0,g-41)
    c: Horizontal(g0)
    c: PointOnObject(g0,g-39)
    c: Coincident(g1,g0)
    c: Vertical(g1)
    c: DistanceY(g1,g1) = 3
    c: Coincident(g2,g-17)
    c: Vertical(g2)
    c: Coincident(g3,g-16)
    c: Vertical(g3)
    c: DistanceY(g2,g2) = 2
    c: DistanceY(g3,g3) = 2
    c: Coincident(g4,g3)
    c: Coincident(g4,g2)
    c: Coincident(g5,g-17)
    c: Coincident(g5,g2)
    c: Coincident(g6,g1)
    c: Horizontal(g6)
    c: Coincident(g6,g5)
    c: Coincident(g7,g-15)
    c: Coincident(g8,g7)
    c: Coincident(g8,g3)
    c: Coincident(g8,g-15)
    c: Horizontal(g9)
    c: DistanceY(g-13,g9) = 2
    c: Coincident(g10,g7)
    c: Parallel(g10,g-14)
    c: Coincident(g9,g10)
    c: Distance(g11) = 2
    c: Coincident(g11,g-11)
    c: Perpendicular(g-11,g11)
    c: Distance(g12) = 2
    c: Coincident(g12,g-12)
    c: Perpendicular(g-11,g12)
    c: Coincident(g13,g11)
    c: Coincident(g13,g12)
    c: Coincident(g14,g-32)
    c: Coincident(g14,g12)
    c: Coincident(g14,g9)
    c: Coincident(g15,g-10)
    c: Coincident(g15,g11)
    c: Parallel(g16,g-22)
    c: Distance(g17) = 4
    c: PointOnObject(g17,g16)
    c: Coincident(g15,g16)
    c: Horizontal(g18)
    c: Coincident(g18,g16)
    c: Coincident(g19,g0)
    c: PointOnObject(g19,g-39)
    c: DistanceY(g19,g-36) = 2
    c: Coincident(g18,g19)
    c: Diameter(g22) = 3.6
    c: Coincident(g22,g-9)
    c: Diameter(g23) = 3.6
    c: Coincident(g23,g-8)
    c: Diameter(g24) = 3.6
    c: Diameter(g25) = 3.6
    c: Diameter(g26) = 3.6
    c: Diameter(g27) = 3.6
    c: Diameter(g28) = 3.6
    c: Coincident(g27,g-4)
    c: Coincident(g28,g-3)
    c: Coincident(g25,g-6)
    c: Coincident(g26,g-5)
    c: Coincident(g24,g-7)
    c: Parallel(g20,g-21)
    c: Equal(g20,g-21)
    c: Parallel(g21,g-19)
    c: Equal(g21,g-19)
    c: Distance(g29) = 0.2
    c: Distance(g30) = 0.2
    c: Parallel(g29,g-20)
    c: Parallel(g31,g-20)
    c: Equal(g31,g-20)
    c: Coincident(g30,g31)
    c: Coincident(g31,g29)
    c: Coincident(g29,g-21)
    c: Parallel(g30,g31)
    c: Coincident(g17,g30)
    c: Coincident(g20,g29)
    c: Coincident(g21,g30)
    c: Perpendicular(g16,g17)
    c: Coincident(g32,g21)
    c: Coincident(g32,g20)
    c: Perpendicular(g10,g7)
    c: Diameter(g33) = 12.6
    c: Diameter(g34) = 12.6
    c: Diameter(g35) = 12.6
    c: Horizontal(g36)
    c: PointOnObject(g33,g36)
    c: PointOnObject(g34,g36)
    c: DistanceX(g34,g33) = 23
    c: DistanceX(g35,g34) = 23
    c: DistanceX(g33,g36) = 15
    c: Symmetric(g-24,g-24,g36)
    c: Coincident(g36,g35)
FEATURE [Sketcher::SketchObject] Sketch075  label="lato dx pistola"
  ArcFitTolerance = 1e-06
  AttachmentSupport = -> [XZ_Plane]
  ExternalGeometry = -> [Sketch016,Sketch,Sketch058,Sketch074]
  ExternalTypes = [0]
  FullyConstrained = true
  MakeInternals = false
  MapMode = 5
  Placement = pos=(0,0,0) rot=(1,0,0;1.5708rad)
  _ExternalGeoVersion = 0
  sketch-geometry (61):
    g0: LineSegment StartX=-82.8 StartY=3.2 StartZ=0 EndX=0 EndY=3.2 EndZ=0
    g1: LineSegment StartX=-82.8 StartY=3.2 StartZ=0 EndX=-82.8 EndY=6.2 EndZ=0
    g2: LineSegment [constr] StartX=-107.6 StartY=18 StartZ=0 EndX=-107.6 EndY=20 EndZ=0
    g3: LineSegment [constr] StartX=-132.428 StartY=18 StartZ=0 EndX=-132.428 EndY=20 EndZ=0
    g4: LineSegment StartX=-132.428 StartY=20 StartZ=0 EndX=-107.6 EndY=20 EndZ=0
    g5: ArcOfCircle CenterX=-107.6 CenterY=4 CenterZ=0 NormalX=0 NormalY=0 NormalZ=1 AngleXU=0 Radius=16 StartAngle=0.137937 EndAngle=1.5708
    g6: LineSegment StartX=-82.8 StartY=6.2 StartZ=0 EndX=-91.752 EndY=6.2 EndZ=0
    g7: LineSegment [constr] StartX=-145.743 StartY=8.32624 StartZ=0 EndX=-147.645 EndY=8.94427 EndZ=0
    g8: ArcOfCircle CenterX=-132.428 CenterY=4 CenterZ=0 NormalX=0 NormalY=0 NormalZ=1 AngleXU=0 Radius=16 StartAngle=1.5708 EndAngle=2.82743
    g9: LineSegment StartX=-215.932 StartY=-80.4316 StartZ=0 EndX=-176.685 EndY=-80.4316 EndZ=0
    g10: LineSegment StartX=-147.645 StartY=8.94427 StartZ=0 EndX=-176.685 EndY=-80.4316 EndZ=0
    g11: LineSegment [constr] StartX=-193.988 StartY=-2.33927 StartZ=0 EndX=-192.176 EndY=-3.18451 EndZ=0
    g12: LineSegment [constr] StartX=-217.232 StartY=-52.1862 StartZ=0 EndX=-215.42 EndY=-53.0314 EndZ=0
    g13: LineSegment StartX=-192.176 StartY=-3.18451 StartZ=0 EndX=-215.42 EndY=-53.0314 EndZ=0
    g14: ArcOfCircle CenterX=-184.801 CenterY=-67.3089 CenterZ=0 NormalX=0 NormalY=0 NormalZ=1 AngleXU=0 Radius=33.7833 StartAngle=2.70526 EndAngle=3.54053
    g15: ArcOfCircle CenterX=-207.583 CenterY=4 CenterZ=0 NormalX=0 NormalY=0 NormalZ=1 AngleXU=0 Radius=17 StartAngle=5.84685 EndAngle=7.56663
    g16: LineSegment StartX=-202.765 StartY=20.303 StartZ=0 EndX=-195.887 EndY=39.2 EndZ=0
    g17: LineSegment [constr] StartX=-193.885 StartY=33.0037 StartZ=0 EndX=-197.644 EndY=34.3718 EndZ=0
    g18: LineSegment StartX=-195.887 StartY=39.2 StartZ=0 EndX=0 EndY=39.2 EndZ=0
    g19: LineSegment StartX=0 StartY=3.2 StartZ=0 EndX=0 EndY=39.2 EndZ=0
    g20: LineSegment StartX=-189.939 StartY=31.5672 StartZ=0 EndX=-192.333 EndY=24.9893 EndZ=0
    g21: LineSegment StartX=-196.467 StartY=26.4942 StartZ=0 EndX=-194.073 EndY=33.0721 EndZ=0
    g22: Circle CenterX=-213.443 CenterY=-76.8316 CenterZ=0 NormalX=0 NormalY=0 NormalZ=1 AngleXU=0 Radius=1.8
    g23: Circle CenterX=-179.305 CenterY=-76.8316 CenterZ=0 NormalX=0 NormalY=0 NormalZ=1 AngleXU=0 Radius=1.8
    g24: Circle CenterX=-184.08 CenterY=34.8 CenterZ=0 NormalX=0 NormalY=0 NormalZ=1 AngleXU=0 Radius=1.8
    g25: Circle CenterX=-78.51 CenterY=34.8 CenterZ=0 NormalX=0 NormalY=0 NormalZ=1 AngleXU=0 Radius=1.8
    g26: Circle CenterX=-78.51 CenterY=7.6 CenterZ=0 NormalX=0 NormalY=0 NormalZ=1 AngleXU=0 Radius=1.8
    g27: Circle CenterX=-5.6 CenterY=34.8 CenterZ=0 NormalX=0 NormalY=0 NormalZ=1 AngleXU=0 Radius=1.8
    g28: Circle CenterX=-5.6 CenterY=7.6 CenterZ=0 NormalX=0 NormalY=0 NormalZ=1 AngleXU=0 Radius=1.8
    g29: LineSegment StartX=-190.127 StartY=31.6356 StartZ=0 EndX=-189.939 EndY=31.5672 EndZ=0
    g30: LineSegment StartX=-194.073 StartY=33.0721 StartZ=0 EndX=-193.885 EndY=33.0037 EndZ=0
    g31: LineSegment StartX=-193.885 StartY=33.0037 StartZ=0 EndX=-190.127 EndY=31.6356 EndZ=0
    g32: LineSegment StartX=-196.467 StartY=26.4942 StartZ=0 EndX=-192.333 EndY=24.9893 EndZ=0
    g33: LineSegment [constr] StartX=-4 StartY=21.2 StartZ=0 EndX=-87.91 EndY=21.2 EndZ=0
    g34: GeomPoint [constr] X=-4 Y=21.2 Z=0
    g35: LineSegment [constr] StartX=-15.2 StartY=33.7 StartZ=0 EndX=-15.2 EndY=8.7 EndZ=0
    g36: LineSegment [constr] StartX=-15.2 StartY=33.7 StartZ=0 EndX=-56.2 EndY=33.7 EndZ=0
    g37: LineSegment [constr] StartX=-15.2 StartY=8.7 StartZ=0 EndX=-56.2 EndY=8.7 EndZ=0
    g38: LineSegment [constr] StartX=-56.2 StartY=33.7 StartZ=0 EndX=-56.2 EndY=8.7 EndZ=0
    g39: Circle CenterX=-18.6 CenterY=30.3 CenterZ=0 NormalX=0 NormalY=0 NormalZ=1 AngleXU=0 Radius=3.4
    g40: Circle CenterX=-18.6 CenterY=12.1 CenterZ=0 NormalX=0 NormalY=0 NormalZ=1 AngleXU=0 Radius=3.4
    g41: Circle CenterX=-43.2 CenterY=30.3 CenterZ=0 NormalX=0 NormalY=0 NormalZ=1 AngleXU=0 Radius=3.4
    g42: Circle CenterX=-43.2 CenterY=12.1 CenterZ=0 NormalX=0 NormalY=0 NormalZ=1 AngleXU=0 Radius=3.4
    g43: LineSegment [constr] StartX=-4 StartY=21.2 StartZ=0 EndX=-15.2 EndY=21.2 EndZ=0
    g44: LineSegment [constr] StartX=-15.2 StartY=21.2 StartZ=0 EndX=-36.2 EndY=21.2 EndZ=0
    g45: LineSegment [constr] StartX=-41.5 StartY=16.2 StartZ=0 EndX=-30.9 EndY=16.2 EndZ=0
    g46: LineSegment [constr] StartX=-30.9 StartY=16.2 StartZ=0 EndX=-30.9 EndY=26.2 EndZ=0
    g47: LineSegment [constr] StartX=-30.9 StartY=26.2 StartZ=0 EndX=-41.5 EndY=26.2 EndZ=0
    g48: LineSegment [constr] StartX=-41.5 StartY=26.2 StartZ=0 EndX=-41.5 EndY=16.2 EndZ=0
    g49: GeomPoint [constr] X=-36.2 Y=21.2 Z=0
    g50: Circle CenterX=-36.2 CenterY=21.2 CenterZ=0 NormalX=0 NormalY=0 NormalZ=1 AngleXU=0 Radius=2.8
    g51: LineSegment [constr] StartX=-24.2 StartY=26.7 StartZ=0 EndX=-24.2 EndY=15.7 EndZ=0
    g52: Circle CenterX=-24.2 CenterY=26.7 CenterZ=0 NormalX=0 NormalY=0 NormalZ=1 AngleXU=0 Radius=3
    g53: Circle CenterX=-24.2 CenterY=15.7 CenterZ=0 NormalX=0 NormalY=0 NormalZ=1 AngleXU=0 Radius=3
    g54: GeomPoint X=-18.6 Y=30.3 Z=0
    g55: GeomPoint X=-18.6 Y=12.1 Z=0
    g56: GeomPoint X=-43.2 Y=12.1 Z=0
    g57: GeomPoint X=-43.2 Y=30.3 Z=0
    g58: Circle CenterX=-65 CenterY=21.2 CenterZ=0 NormalX=0 NormalY=0 NormalZ=1 AngleXU=0 Radius=1.5
    g59: Circle CenterX=-42 CenterY=21.2 CenterZ=0 NormalX=0 NormalY=0 NormalZ=1 AngleXU=0 Radius=1.5
    g60: Circle CenterX=-19 CenterY=21.2 CenterZ=0 NormalX=0 NormalY=0 NormalZ=1 AngleXU=0 Radius=1.5
  constraints (149):
    c: Coincident(g0,g-41)
    c: Horizontal(g0)
    c: PointOnObject(g0,g-39)
    c: Coincident(g1,g0)
    c: Vertical(g1)
    c: DistanceY(g1,g1) = 3
    c: Coincident(g2,g-17)
    c: Vertical(g2)
    c: Coincident(g3,g-16)
    c: Vertical(g3)
    c: DistanceY(g2,g2) = 2
    c: DistanceY(g3,g3) = 2
    c: Coincident(g4,g3)
    c: Coincident(g4,g2)
    c: Coincident(g5,g-17)
    c: Coincident(g5,g2)
    c: Coincident(g6,g1)
    c: Horizontal(g6)
    c: Coincident(g6,g5)
    c: Coincident(g7,g-15)
    c: Coincident(g8,g7)
    c: Coincident(g8,g3)
    c: Coincident(g8,g-15)
    c: Horizontal(g9)
    c: DistanceY(g-13,g9) = 2
    c: Coincident(g10,g7)
    c: Parallel(g10,g-14)
    c: Coincident(g9,g10)
    c: Distance(g11) = 2
    c: Coincident(g11,g-11)
    c: Perpendicular(g-11,g11)
    c: Distance(g12) = 2
    c: Coincident(g12,g-12)
    c: Perpendicular(g-11,g12)
    c: Coincident(g13,g11)
    c: Coincident(g13,g12)
    c: Coincident(g14,g-32)
    c: Coincident(g14,g12)
    c: Coincident(g14,g9)
    c: Coincident(g15,g-10)
    c: Coincident(g15,g11)
    c: Parallel(g16,g-22)
    c: Distance(g17) = 4
    c: PointOnObject(g17,g16)
    c: Coincident(g15,g16)
    c: Horizontal(g18)
    c: Coincident(g18,g16)
    c: Coincident(g19,g0)
    c: PointOnObject(g19,g-39)
    c: DistanceY(g19,g-36) = 2
    c: Coincident(g18,g19)
    c: Diameter(g22) = 3.6
    c: Coincident(g22,g-9)
    c: Diameter(g23) = 3.6
    c: Coincident(g23,g-8)
    c: Diameter(g24) = 3.6
    c: Diameter(g25) = 3.6
    c: Diameter(g26) = 3.6
    c: Diameter(g27) = 3.6
    c: Diameter(g28) = 3.6
    c: Coincident(g27,g-4)
    c: Coincident(g28,g-3)
    c: Coincident(g25,g-6)
    c: Coincident(g26,g-5)
    c: Coincident(g24,g-7)
    c: Parallel(g20,g-21)
    c: Equal(g20,g-21)
    c: Parallel(g21,g-19)
    c: Equal(g21,g-19)
    c: Distance(g29) = 0.2
    c: Distance(g30) = 0.2
    c: Parallel(g29,g-20)
    c: Parallel(g31,g-20)
    c: Equal(g31,g-20)
    c: Coincident(g30,g31)
    c: Coincident(g31,g29)
    c: Coincident(g29,g-21)
    c: Parallel(g30,g31)
    c: Coincident(g17,g30)
    c: Coincident(g20,g29)
    c: Coincident(g21,g30)
    c: Perpendicular(g16,g17)
    c: Coincident(g32,g21)
    c: Coincident(g32,g20)
    c: Perpendicular(g10,g7)
    c: Horizontal(g33)
    c: Symmetric(g-24,g-24,g33)
    c: PointOnObject(g33,g-28)
    c: Symmetric(g-24,g-24,g34)
    c: DistanceY(g35,g35) = 25
    c: Symmetric(g35,g35,g33)
    c: Distance(g36) = 41
    c: Coincident(g36,g35)
    c: Horizontal(g36)
    c: Coincident(g37,g35)
    c: Horizontal(g37)
    c: Coincident(g38,g36)
    c: Vertical(g38)
    c: Coincident(g37,g38)
    c: Diameter(g39) = 6.8
    c: Diameter(g40) = 6.8
    c: Tangent(g39,g36)
    c: Tangent(g40,g37)
    c: Tangent(g39,g35)
    c: Tangent(g40,g35)
    c: Diameter(g41) = 6.8
    c: Diameter(g42) = 6.8
    c: Tangent(g41,g36)
    c: Tangent(g42,g37)
    c: DistanceX(g41,g39) = 24.6
    c: DistanceX(g42,g40) = 24.6
    c: Distance(g43) = 11.2
    c: Coincident(g43,g33)
    c: PointOnObject(g43,g33)
    c: PointOnObject(g43,g35)
    c: Distance(g44) = 21
    c: Coincident(g44,g43)
    c: PointOnObject(g44,g33)
    c: Coincident(g45,g46)
    c: Coincident(g46,g47)
    c: Coincident(g47,g48)
    c: Coincident(g48,g45)
    c: Horizontal(g45)
    c: Horizontal(g47)
    c: Vertical(g46)
    c: Vertical(g48)
    c: Symmetric(g47,g45,g49)
    c: Distance(g46,g48) = 10.6
    c: Distance(g45,g47) = 10
    c: Coincident(g49,g44)
    c: Diameter(g50) = 5.6
    c: Coincident(g50,g44)
    c: Distance(g51) = 11
    c: Symmetric(g51,g51,g33)
    c: DistanceX(g51,g43) = 9
    c: Diameter(g52) = 6
    c: Coincident(g52,g51)
    c: Diameter(g53) = 6
    c: Coincident(g53,g51)
    c: Coincident(g40,g55)
    c: Coincident(g39,g54)
    c: Coincident(g41,g57)
    c: Coincident(g42,g56)
    c: Diameter(g58) = 3
    c: Diameter(g59) = 3
    c: Diameter(g60) = 3
    c: Coincident(g58,g-44)
    c: Coincident(g59,g-46)
    c: Coincident(g60,g-45)
FEATURE [Sketcher::SketchObject] Sketch078
  ArcFitTolerance = 1e-06
  AttachmentSupport = -> [XZ_Plane005]
  ExternalTypes = [0]
  FullyConstrained = true
  MakeInternals = false
  MapMode = 5
  Placement = pos=(0,0,0) rot=(1,0,0;1.5708rad)
  _ExternalGeoVersion = 0
  sketch-geometry (5):
    g0: LineSegment [constr] StartX=0 StartY=5.5 StartZ=0 EndX=0 EndY=-5.5 EndZ=0
    g1: ArcOfCircle CenterX=0 CenterY=5.5 CenterZ=0 NormalX=0 NormalY=0 NormalZ=1 AngleXU=0 Radius=2.7 StartAngle=0 EndAngle=3.14159
    g2: ArcOfCircle CenterX=0 CenterY=-5.5 CenterZ=0 NormalX=0 NormalY=0 NormalZ=1 AngleXU=0 Radius=2.7 StartAngle=3.1416 EndAngle=6.28318
    g3: LineSegment StartX=-2.7 StartY=5.5 StartZ=0 EndX=-2.7 EndY=-5.50001 EndZ=0
    g4: LineSegment StartX=2.7 StartY=5.5 StartZ=0 EndX=2.7 EndY=-5.50001 EndZ=0
  constraints (13):
    c: Distance(g0) = 11
    c: Vertical(g0)
    c: Symmetric(g0,g0,g-1)
    c: Radius(g1) = 2.7
    c: Coincident(g1,g0)
    c: Radius(g2) = 2.7
    c: Coincident(g2,g0)
    c: Vertical(g3)
    c: Vertical(g4)
    c: Coincident(g2,g4)
    c: Coincident(g2,g3)
    c: Tangent(g3,g1) = -1.5708
    c: Tangent(g4,g1) = 1.5708
FEATURE [PartDesign::Pad] Pad002
  Direction = (0,-1,2e-16)
  Length = 0.8
  Length2 = 10
  Placement = pos=(0,0,0) rot=(1,0,0;1.5708rad)
  Profile = -> Sketch078
  ReferenceAxis = -> Sketch078 [N_Axis]
  Refine = true
  SideType = 0
  Suppressed = false
  Type = 0
  Type2 = 0
FEATURE [Sketcher::SketchObject] Sketch079
  ArcFitTolerance = 1e-06
  AttachmentSupport = -> [XZ_Plane005]
  ExternalGeometry = -> [Sketch078]
  ExternalTypes = [0]
  FullyConstrained = true
  MakeInternals = false
  MapMode = 5
  Placement = pos=(0,0,0) rot=(1,0,0;1.5708rad)
  _ExternalGeoVersion = 0
  sketch-geometry (2):
    g0: Circle CenterX=-1e-16 CenterY=5.5 CenterZ=0 NormalX=0 NormalY=0 NormalZ=1 AngleXU=0 Radius=2.7
    g1: Circle CenterX=0 CenterY=-5.5 CenterZ=0 NormalX=0 NormalY=0 NormalZ=1 AngleXU=0 Radius=2.7
  constraints (4):
    c: Coincident(g0,g-3)
    c: PointOnObject(g-3,g0)
    c: Coincident(g1,g-4)
    c: Equal(g1,g-4)
FEATURE [PartDesign::Pad] Pad003
  BaseFeature = -> Pad002
  Direction = (0,-1,2e-16)
  Length = 5
  Length2 = 10
  Placement = pos=(0,0,0) rot=(1,0,0;1.5708rad)
  Profile = -> Sketch079
  ReferenceAxis = -> Sketch079 [N_Axis]
  Refine = true
  SideType = 0
  Suppressed = false
  Type = 0
  Type2 = 0
FEATURE [PartDesign::Fillet] Fillet001
  Base = -> Pad003 [Edge16,Edge14]
  BaseFeature = -> Pad003
  Placement = pos=(0,0,0) rot=(1,0,0;1.5708rad)
  Radius = 0.4
  Refine = true
  SupportTransform = false
  Suppressed = false
  UseAllEdges = false
FEATURE [PartDesign::Body] Body005  label="pulsanti lato destro"
  AllowCompound = false
  Group = -> [Sketch078,Pad002,Sketch079,Pad003,Fillet001]
  Origin = -> Origin005
  Tip = -> Fillet001
FEATURE [PartDesign::SubShapeBinder] Binder
  BindCopyOnChange = 0
  BindMode = 0
  ClaimChildren = false
  Context = -> Body006 [Binder.]
  Fuse = false
  MakeFace = true
  OffsetFill = false
  OffsetIntersection = false
  OffsetJoinType = 0
  OffsetOpenResult = false
  PartialLoad = false
  Refine = true
  Relative = true
  Support = -> [Body[Sketch074.]]
  _Version = 2
FEATURE [PartDesign::SubShapeBinder] Binder001
  BindCopyOnChange = 0
  BindMode = 0
  ClaimChildren = false
  Context = -> Body007 [Binder001.]
  Fuse = false
  MakeFace = true
  OffsetFill = false
  OffsetIntersection = false
  OffsetJoinType = 0
  OffsetOpenResult = false
  PartialLoad = false
  Refine = true
  Relative = true
  Support = -> [Body[Sketch075.]]
  _Version = 2
FEATURE [Mesh::Feature] logo_per_PCB_definitivo_positivo
  Placement = pos=(-191,17,-66) rot=(0,1,1;0rad)
FEATURE [Sketcher::SketchObject] Sketch114  label="Sketch114 - base lato DX"
  ArcFitTolerance = 1e-06
  AttachmentSupport = -> [Binder001]
  ExternalGeometry = -> [Binder001]
  ExternalTypes = [0]
  FullyConstrained = true
  MakeInternals = false
  MapMode = 5
  Placement = pos=(0,1e-15,0) rot=(0,0.707107,0.707107;3.14159rad)
  _ExternalGeoVersion = 0
  sketch-geometry (30):
    g0: Circle CenterX=5.6 CenterY=34.8 CenterZ=0 NormalX=0 NormalY=0 NormalZ=1 AngleXU=0 Radius=1.8
    g1: Circle CenterX=5.6 CenterY=7.6 CenterZ=0 NormalX=0 NormalY=0 NormalZ=1 AngleXU=0 Radius=1.8
    g2: Circle CenterX=24.2 CenterY=26.7 CenterZ=0 NormalX=0 NormalY=0 NormalZ=1 AngleXU=0 Radius=3
    g3: Circle CenterX=24.2 CenterY=15.7 CenterZ=0 NormalX=0 NormalY=0 NormalZ=1 AngleXU=0 Radius=3
    g4: Circle CenterX=36.2 CenterY=21.2 CenterZ=0 NormalX=0 NormalY=0 NormalZ=1 AngleXU=0 Radius=2.8
    g5: Circle CenterX=78.51 CenterY=34.8 CenterZ=0 NormalX=0 NormalY=0 NormalZ=1 AngleXU=0 Radius=1.8
    g6: Circle CenterX=78.51 CenterY=7.6 CenterZ=0 NormalX=0 NormalY=0 NormalZ=1 AngleXU=0 Radius=1.8
    g7: Circle CenterX=184.08 CenterY=34.8 CenterZ=0 NormalX=0 NormalY=0 NormalZ=1 AngleXU=0 Radius=1.8
    g8: Circle CenterX=213.443 CenterY=-76.8316 CenterZ=0 NormalX=0 NormalY=0 NormalZ=1 AngleXU=0 Radius=1.8
    g9: Circle CenterX=179.305 CenterY=-76.8316 CenterZ=0 NormalX=0 NormalY=0 NormalZ=1 AngleXU=0 Radius=1.8
    g10: ArcOfCircle [constr] CenterX=132.428 CenterY=4 CenterZ=0 NormalX=0 NormalY=0 NormalZ=1 AngleXU=0 Radius=16 StartAngle=0.314159 EndAngle=1.5708
    g11: ArcOfCircle CenterX=107.6 CenterY=4 CenterZ=0 NormalX=0 NormalY=0 NormalZ=1 AngleXU=0 Radius=16 StartAngle=1.5708 EndAngle=3.00366
    g12: ArcOfCircle CenterX=207.583 CenterY=4 CenterZ=0 NormalX=0 NormalY=0 NormalZ=1 AngleXU=0 Radius=17 StartAngle=1.85815 EndAngle=3.57792
    g13: ArcOfCircle CenterX=184.801 CenterY=-67.3089 CenterZ=0 NormalX=0 NormalY=0 NormalZ=1 AngleXU=0 Radius=33.7833 StartAngle=5.88425 EndAngle=6.71952
    g14: LineSegment StartX=0 StartY=39.2 StartZ=0 EndX=0 EndY=3.2 EndZ=0
    g15: LineSegment StartX=0 StartY=3.2 StartZ=0 EndX=82.8 EndY=3.2 EndZ=0
    g16: LineSegment StartX=82.8 StartY=3.2 StartZ=0 EndX=82.8 EndY=6.2 EndZ=0
    g17: LineSegment StartX=82.8 StartY=6.2 StartZ=0 EndX=91.752 EndY=6.2 EndZ=0
    g18: LineSegment StartX=107.6 StartY=20 StartZ=0 EndX=132.428 EndY=20 EndZ=0
    g19: LineSegment StartX=147.645 StartY=8.94427 StartZ=0 EndX=176.685 EndY=-80.4316 EndZ=0
    g20: LineSegment StartX=176.685 StartY=-80.4316 StartZ=0 EndX=215.932 EndY=-80.4316 EndZ=0
    g21: LineSegment StartX=215.42 StartY=-53.0314 StartZ=0 EndX=192.176 EndY=-3.18451 EndZ=0
    g22: LineSegment StartX=202.765 StartY=20.303 StartZ=0 EndX=195.887 EndY=39.2 EndZ=0
    g23: LineSegment StartX=195.887 StartY=39.2 StartZ=0 EndX=0 EndY=39.2 EndZ=0
    g24: LineSegment StartX=196.467 StartY=26.4942 StartZ=0 EndX=194.073 EndY=33.0721 EndZ=0
    g25: LineSegment StartX=194.073 StartY=33.0721 StartZ=0 EndX=189.939 EndY=31.5672 EndZ=0
    g26: LineSegment StartX=189.939 StartY=31.5672 StartZ=0 EndX=192.333 EndY=24.9893 EndZ=0
    g27: LineSegment StartX=192.333 StartY=24.9893 StartZ=0 EndX=196.467 EndY=26.4942 EndZ=0
    g28: LineSegment StartX=132.428 StartY=20 StartZ=0 EndX=144.053 EndY=20 EndZ=0
    g29: LineSegment StartX=144.053 StartY=20 StartZ=0 EndX=147.645 EndY=8.94427 EndZ=0
  constraints (65):
    c: Equal(g0,g-25)
    c: Equal(g2,g-29)
    c: Equal(g3,g-30)
    c: Equal(g4,g-28)
    c: Equal(g1,g-26)
    c: Coincident(g0,g-25)
    c: Coincident(g1,g-26)
    c: Coincident(g2,g-29)
    c: Coincident(g3,g-30)
    c: Coincident(g4,g-28)
    c: Equal(g5,g-23)
    c: Equal(g6,g-24)
    c: Coincident(g5,g-23)
    c: Coincident(g6,g-24)
    c: Equal(g7,g-20)
    c: Coincident(g7,g-20)
    c: Equal(g9,g-22)
    c: Coincident(g9,g-22)
    c: Equal(g8,g-21)
    c: Coincident(g8,g-21)
    c: Equal(g13,g-12)
    c: Equal(g12,g-14)
    c: Equal(g10,g-9)
    c: Equal(g11,g-7)
    c: Coincident(g14,g-27)
    c: Coincident(g14,g-27)
    c: Coincident(g15,g14)
    c: Coincident(g15,g-5)
    c: Coincident(g16,g15)
    c: Coincident(g16,g-6)
    c: Coincident(g17,g16)
    c: Coincident(g17,g-7)
    c: Coincident(g11,g17)
    c: Coincident(g11,g-8)
    c: Coincident(g18,g11)
    c: Coincident(g18,g-9)
    c: Coincident(g10,g18)
    c: Coincident(g10,g-10)
    c: Coincident(g19,g10)
    c: Coincident(g19,g-11)
    c: Coincident(g20,g19)
    c: Coincident(g20,g-12)
    c: Coincident(g13,g20)
    c: Coincident(g13,g-13)
    c: Coincident(g21,g13)
    c: Coincident(g21,g-14)
    c: Coincident(g12,g21)
    c: Coincident(g12,g-15)
    c: Coincident(g22,g12)
    c: Coincident(g22,g-15)
    c: Coincident(g23,g22)
    c: Coincident(g23,g14)
    c: Coincident(g24,g-18)
    c: Coincident(g24,g-16)
    c: Coincident(g25,g24)
    c: Coincident(g25,g-19)
    c: Coincident(g26,g25)
    c: Coincident(g26,g-19)
    c: Coincident(g27,g26)
    c: Coincident(g27,g24)
    c: Coincident(g29,g10)
    c: Coincident(g28,g10)
    c: Coincident(g29,g28)
    c: Parallel(g28,g18)
    c: Parallel(g29,g19)
FEATURE [PartDesign::Pad] Pad011
  Direction = (0,1,-2e-16)
  Length = 2
  Length2 = 10
  Profile = -> Sketch114
  ReferenceAxis = -> Sketch114 [N_Axis]
  Refine = true
  Reversed = true
  SideType = 0
  Suppressed = false
  Type = 0
  Type2 = 0
FEATURE [Sketcher::SketchObject] Sketch115
  ArcFitTolerance = 1e-06
  AttachmentSupport = -> [Pad011]
  ExternalGeometry = -> [Binder001]
  ExternalTypes = [0]
  FullyConstrained = true
  MakeInternals = false
  MapMode = 5
  Placement = pos=(0,1.7e-15,0) rot=(0,0.707107,0.707107;3.14159rad)
  _ExternalGeoVersion = 0
  sketch-geometry (4):
    g0: ArcOfCircle CenterX=24.2 CenterY=26.7 CenterZ=0 NormalX=0 NormalY=0 NormalZ=1 AngleXU=0 Radius=3 StartAngle=4.48384e-08 EndAngle=3.14159
    g1: ArcOfCircle CenterX=24.2 CenterY=15.7 CenterZ=0 NormalX=0 NormalY=0 NormalZ=1 AngleXU=0 Radius=3 StartAngle=3.14159 EndAngle=6.28318
    g2: LineSegment StartX=21.2 StartY=26.7 StartZ=0 EndX=21.2 EndY=15.7 EndZ=0
    g3: LineSegment StartX=27.2 StartY=26.7 StartZ=0 EndX=27.2 EndY=15.7 EndZ=0
  constraints (12):
    c: Equal(g1,g-4)
    c: Equal(g0,g-3)
    c: Coincident(g0,g-3)
    c: Coincident(g1,g-4)
    c: Vertical(g2)
    c: Vertical(g3)
    c: Tangent(g3,g-3)
    c: Tangent(g2,g-3)
    c: Coincident(g0,g2)
    c: Coincident(g0,g3)
    c: Coincident(g1,g2)
    c: Coincident(g3,g1)
FEATURE [Sketcher::SketchObject] Sketch117  label="Sketch117 - fori per inserto M3 x 3 x 4.5"
  ArcFitTolerance = 1e-06
  AttachmentSupport = -> [Pad011]
  ExternalGeometry = -> [Binder001]
  ExternalTypes = [0]
  FullyConstrained = true
  MakeInternals = false
  MapMode = 5
  Placement = pos=(0,1.7e-15,0) rot=(0,0.707107,0.707107;3.14159rad)
  _ExternalGeoVersion = 0
  sketch-geometry (4):
    g0: Circle CenterX=43.2 CenterY=30.3 CenterZ=0 NormalX=0 NormalY=0 NormalZ=1 AngleXU=0 Radius=2.25
    g1: Circle CenterX=43.2 CenterY=12.1 CenterZ=0 NormalX=0 NormalY=0 NormalZ=1 AngleXU=0 Radius=2.25
    g2: Circle CenterX=18.6 CenterY=30.3 CenterZ=0 NormalX=0 NormalY=0 NormalZ=1 AngleXU=0 Radius=2.25
    g3: Circle CenterX=18.6 CenterY=12.1 CenterZ=0 NormalX=0 NormalY=0 NormalZ=1 AngleXU=0 Radius=2.25
  constraints (8):
    c: Diameter(g0) = 4.5
    c: Diameter(g1) = 4.5
    c: Diameter(g2) = 4.5
    c: Diameter(g3) = 4.5
    c: Coincident(g2,g-3)
    c: Coincident(g3,g-6)
    c: Coincident(g0,g-4)
    c: Coincident(g1,g-5)
FEATURE [Sketcher::SketchObject] Sketch118
  ArcFitTolerance = 1e-06
  AttachmentSupport = -> [Pad011]
  ExternalGeometry = -> [Binder001]
  ExternalTypes = [0]
  FullyConstrained = true
  MakeInternals = false
  MapMode = 5
  Placement = pos=(0,-2,0) rot=(1,0,0;1.5708rad)
  _ExternalGeoVersion = 0
  sketch-geometry (12):
    g0: Circle CenterX=-78.51 CenterY=34.8 CenterZ=0 NormalX=0 NormalY=0 NormalZ=1 AngleXU=0 Radius=1.8
    g1: Circle CenterX=-78.51 CenterY=7.6 CenterZ=0 NormalX=0 NormalY=0 NormalZ=1 AngleXU=0 Radius=1.8
    g2: Circle CenterX=-5.6 CenterY=34.8 CenterZ=0 NormalX=0 NormalY=0 NormalZ=1 AngleXU=0 Radius=1.8
    g3: Circle CenterX=-5.6 CenterY=7.6 CenterZ=0 NormalX=0 NormalY=0 NormalZ=1 AngleXU=0 Radius=1.8
    g4: LineSegment StartX=0 StartY=39.2 StartZ=0 EndX=0 EndY=3.2 EndZ=0
    g5: LineSegment StartX=0 StartY=3.2 StartZ=0 EndX=-82.8 EndY=3.2 EndZ=0
    g6: LineSegment StartX=-82.8 StartY=3.2 StartZ=0 EndX=-82.8 EndY=39.2 EndZ=0
    g7: LineSegment StartX=-82.8 StartY=39.2 StartZ=0 EndX=0 EndY=39.2 EndZ=0
    g8: ArcOfCircle CenterX=-65 CenterY=21.2 CenterZ=0 NormalX=0 NormalY=0 NormalZ=1 AngleXU=0 Radius=10 StartAngle=1.5708 EndAngle=4.71239
    g9: ArcOfCircle CenterX=-19 CenterY=21.2 CenterZ=0 NormalX=0 NormalY=0 NormalZ=1 AngleXU=0 Radius=10 StartAngle=4.71239 EndAngle=7.85398
    g10: LineSegment StartX=-65 StartY=31.2 StartZ=0 EndX=-19 EndY=31.2 EndZ=0
    g11: LineSegment StartX=-65 StartY=11.2 StartZ=0 EndX=-19 EndY=11.2 EndZ=0
  constraints (25):
    c: Equal(g2,g-5)
    c: Equal(g3,g-7)
    c: Equal(g1,g-6)
    c: Equal(g0,g-4)
    c: Coincident(g0,g-4)
    c: Coincident(g1,g-6)
    c: Coincident(g3,g-7)
    c: Coincident(g2,g-5)
    c: Coincident(g4,g-8)
    c: Coincident(g4,g-9)
    c: Coincident(g5,g4)
    c: Coincident(g5,g-10)
    c: Coincident(g6,g5)
    c: PointOnObject(g6,g-3)
    c: Vertical(g6)
    c: Coincident(g7,g6)
    c: Coincident(g7,g4)
    c: Tangent(g8,g10) = 1.5708
    c: Tangent(g8,g11) = -1.5708
    c: Tangent(g9,g10) = 1.5708
    c: Tangent(g9,g11) = -1.5708
    c: Equal(g8,g9)
    c: Radius(g8) = 10
    c: Coincident(g8,g-11)
    c: Coincident(g9,g-12)
FEATURE [Sketcher::SketchObject] Sketch120
  ArcFitTolerance = 1e-06
  AttachmentSupport = -> [Pad011]
  ExternalGeometry = -> [Binder001]
  ExternalTypes = [0]
  FullyConstrained = true
  MakeInternals = false
  MapMode = 5
  Placement = pos=(0,-2,0) rot=(1,0,0;1.5708rad)
  _ExternalGeoVersion = 0
  sketch-geometry (4):
    g0: LineSegment StartX=-137.815 StartY=39.2 StartZ=0 EndX=-142.655 EndY=24.303 EndZ=0
    g1: LineSegment StartX=-137.815 StartY=39.2 StartZ=0 EndX=-110.815 EndY=39.2 EndZ=0
    g2: LineSegment StartX=-142.655 StartY=24.303 StartZ=0 EndX=-110.815 EndY=24.303 EndZ=0
    g3: ArcOfCircle CenterX=-92.2534 CenterY=31.7515 CenterZ=0 NormalX=0 NormalY=0 NormalZ=1 AngleXU=0 Radius=20 StartAngle=2.75997 EndAngle=3.52321
  constraints (12):
    c: PointOnObject(g0,g-3)
    c: Coincident(g1,g0)
    c: PointOnObject(g1,g-3)
    c: Coincident(g2,g0)
    c: Horizontal(g2)
    c: Tangent(g0,g-4)
    c: Vertical(g2,g1)
    c: DistanceX(g1,g1) = 27
    c: DistanceY(g-6,g0) = 4
    c: Radius(g3) = 20
    c: Coincident(g3,g1)
    c: Coincident(g3,g2)
FEATURE [Sketcher::SketchObject] Sketch121
  ArcFitTolerance = 1e-06
  AttachmentSupport = -> [Pad011]
  ExternalGeometry = -> [Binder001]
  ExternalTypes = [0]
  FullyConstrained = true
  MakeInternals = false
  MapMode = 5
  Placement = pos=(0,-2,0) rot=(1,0,0;1.5708rad)
  _ExternalGeoVersion = 0
  sketch-geometry (15):
    g0: LineSegment StartX=-137.815 StartY=39.2 StartZ=0 EndX=-143.955 EndY=20.303 EndZ=0
    g1: LineSegment StartX=-143.955 StartY=20.303 StartZ=0 EndX=-190.141 EndY=20.303 EndZ=0
    g2: LineSegment StartX=-190.141 StartY=20.303 StartZ=0 EndX=-186.139 EndY=31.3 EndZ=0
    g3: LineSegment StartX=-178.754 StartY=39.2 StartZ=0 EndX=-180.791 EndY=33.6029 EndZ=0
    g4: ArcOfCircle CenterX=-184.08 CenterY=34.8 CenterZ=0 NormalX=0 NormalY=0 NormalZ=1 AngleXU=0 Radius=3.5 StartAngle=4.71239 EndAngle=5.93412
    g5: LineSegment StartX=-184.08 StartY=31.3 StartZ=0 EndX=-186.139 EndY=31.3 EndZ=0
    g6: LineSegment StartX=-137.815 StartY=39.2 StartZ=0 EndX=-156.815 EndY=39.2 EndZ=0
    g7: LineSegment StartX=-168.815 StartY=39.2 StartZ=0 EndX=-178.754 EndY=39.2 EndZ=0
    g8: LineSegment StartX=-157.815 StartY=39.2 StartZ=0 EndX=-167.815 EndY=39.2 EndZ=0
    g9: LineSegment StartX=-168.815 StartY=31.2 StartZ=0 EndX=-156.815 EndY=31.2 EndZ=0
    g10: LineSegment StartX=-167.436 StartY=36.2 StartZ=0 EndX=-157.436 EndY=36.2 EndZ=0
    g11: ArcOfCircle CenterX=-176.411 CenterY=35.2 CenterZ=0 NormalX=0 NormalY=0 NormalZ=1 AngleXU=0 Radius=20 StartAngle=6.08183 EndAngle=6.48454
    g12: ArcOfCircle CenterX=-188.411 CenterY=35.2 CenterZ=0 NormalX=0 NormalY=0 NormalZ=1 AngleXU=0 Radius=20 StartAngle=6.08183 EndAngle=6.48454
    g13: ArcOfCircle CenterX=-177.411 CenterY=35.2 CenterZ=0 NormalX=0 NormalY=0 NormalZ=1 AngleXU=0 Radius=20 StartAngle=0.0500209 EndAngle=0.201358
    g14: ArcOfCircle CenterX=-187.411 CenterY=35.2 CenterZ=0 NormalX=0 NormalY=0 NormalZ=1 AngleXU=0 Radius=20 StartAngle=0.0500209 EndAngle=0.201358
  constraints (46):
    c: PointOnObject(g0,g-3)
    c: Tangent(g0,g-5)
    c: Coincident(g1,g0)
    c: Horizontal(g1)
    c: Coincident(g2,g1)
    c: PointOnObject(g3,g-3)
    c: Parallel(g3,g-6)
    c: Parallel(g2,g-6)
    c: Radius(g4) = 3.5
    c: Coincident(g4,g-7)
    c: Tangent(g3,g4) = 1.5708
    c: Horizontal(g5)
    c: Tangent(g5,g4) = 1.5708
    c: DistanceX(g-8,g5) = 3.8
    c: Coincident(g2,g5)
    c: Coincident(g6,g0)
    c: PointOnObject(g6,g-3)
    c: DistanceX(g6,g6) = 19
    c: PointOnObject(g7,g-3)
    c: DistanceX(g7,g6) = 12
    c: Coincident(g7,g3)
    c: PointOnObject(g8,g-3)
    c: PointOnObject(g8,g-3)
    c: DistanceX(g8,g8) = 10
    c: DistanceX(g8,g6) = 1
    c: Horizontal(g9)
    c: Vertical(g7,g9)
    c: Vertical(g6,g9)
    c: DistanceY(g9,g7) = 8
    c: Horizontal(g10)
    c: Equal(g8,g10)
    c: DistanceY(g10,g8) = 3
    c: Radius(g11) = 20
    c: Coincident(g11,g6)
    c: Coincident(g11,g9)
    c: Radius(g12) = 20
    c: Coincident(g12,g7)
    c: Coincident(g12,g9)
    c: Equal(g13,g11)
    c: Coincident(g13,g8)
    c: Coincident(g13,g10)
    c: Horizontal(g13,g11)
    c: Equal(g14,g12)
    c: Coincident(g14,g8)
    c: Coincident(g14,g10)
    c: Horizontal(g1,g-6)
FEATURE [Sketcher::SketchObject] Sketch122
  ArcFitTolerance = 1e-06
  AttachmentSupport = -> [Pad011]
  ExternalGeometry = -> [Binder001]
  ExternalTypes = [0]
  FullyConstrained = true
  MakeInternals = false
  MapMode = 5
  Placement = pos=(0,-2,0) rot=(1,0,0;1.5708rad)
  _ExternalGeoVersion = 0
  sketch-geometry (8):
    g0: ArcOfCircle CenterX=-184.801 CenterY=-67.3089 CenterZ=0 NormalX=0 NormalY=0 NormalZ=1 AngleXU=0 Radius=33.7833 StartAngle=2.70526 EndAngle=3.54053
    g1: LineSegment StartX=-176.685 StartY=-80.4316 StartZ=0 EndX=-215.932 EndY=-80.4316 EndZ=0
    g2: LineSegment StartX=-215.42 StartY=-53.0314 StartZ=0 EndX=-192.176 EndY=-3.18454 EndZ=0
    g3: ArcOfCircle CenterX=-207.583 CenterY=4 CenterZ=0 NormalX=0 NormalY=0 NormalZ=1 AngleXU=0 Radius=17 StartAngle=5.84685 EndAngle=7.56663
    g4: Circle CenterX=-213.443 CenterY=-76.8316 CenterZ=0 NormalX=0 NormalY=0 NormalZ=1 AngleXU=0 Radius=3
    g5: Circle CenterX=-179.305 CenterY=-76.8316 CenterZ=0 NormalX=0 NormalY=0 NormalZ=1 AngleXU=0 Radius=3
    g6: LineSegment StartX=-143.955 StartY=20.303 StartZ=0 EndX=-176.685 EndY=-80.4316 EndZ=0
    g7: LineSegment StartX=-202.765 StartY=20.303 StartZ=0 EndX=-143.955 EndY=20.303 EndZ=0
  constraints (18):
    c: Coincident(g0,g-7)
    c: Coincident(g0,g-8)
    c: Coincident(g1,g0)
    c: Tangent(g2,g-5)
    c: Coincident(g3,g-6)
    c: Coincident(g2,g3)
    c: Coincident(g0,g2)
    c: Diameter(g4) = 6
    c: Diameter(g5) = 6
    c: Coincident(g4,g-9)
    c: Coincident(g5,g-10)
    c: Horizontal(g1)
    c: Coincident(g6,g1)
    c: Tangent(g6,g-4)
    c: Coincident(g3,g-6)
    c: Coincident(g7,g3)
    c: Horizontal(g7)
    c: Coincident(g7,g6)
FEATURE [Sketcher::SketchObject] Sketch123
  ArcFitTolerance = 1e-06
  AttachmentSupport = -> [Pad011]
  ExternalGeometry = -> [Binder001]
  ExternalTypes = [0]
  FullyConstrained = true
  MakeInternals = false
  MapMode = 5
  Placement = pos=(0,-2,0) rot=(1,0,0;1.5708rad)
  _ExternalGeoVersion = 0
  sketch-geometry (4):
    g0: LineSegment StartX=-108 StartY=36.8 StartZ=0 EndX=-90 EndY=36.8 EndZ=0
    g1: LineSegment StartX=-108 StartY=36.8 StartZ=0 EndX=-108 EndY=26.8 EndZ=0
    g2: LineSegment StartX=-108 StartY=26.8 StartZ=0 EndX=-90 EndY=26.8 EndZ=0
    g3: ArcOfCircle CenterX=-94 CenterY=31.8 CenterZ=0 NormalX=0 NormalY=0 NormalZ=1 AngleXU=0 Radius=6.40312 StartAngle=5.38713 EndAngle=7.17924
  constraints (13):
    c: Horizontal(g0)
    c: Coincident(g1,g0)
    c: Vertical(g1)
    c: Coincident(g2,g1)
    c: Horizontal(g2)
    c: DistanceX(g0,g0) = 18
    c: DistanceY(g1,g1) = 10
    c: Equal(g0,g2)
    c: DistanceX(g0,g-3) = 90
    c: DistanceY(g0,g-3) = 2.4
    c: Coincident(g3,g0)
    c: Coincident(g3,g2)
    c: DistanceX(g3,g0) = 4
FEATURE [PartDesign::Chamfer] Chamfer014
  Angle = 45
  Base = -> Pad011 [Edge80,Edge4,Edge7]
  BaseFeature = -> Pad011
  ChamferType = 0
  FlipDirection = false
  Refine = true
  Size = 1.9
  Size2 = 1
  SupportTransform = false
  Suppressed = false
  UseAllEdges = false
FEATURE [PartDesign::Pocket] Pocket006
  BaseFeature = -> Chamfer014
  Direction = (0,-1,2e-16)
  Length = 1.2
  Length2 = 5
  Profile = -> Sketch115
  ReferenceAxis = -> Sketch115 [N_Axis]
  Refine = true
  SideType = 0
  Suppressed = false
  Type = 0
  Type2 = 0
FEATURE [Sketcher::SketchObject] Sketch116  label="Sketch116 - pieno per inserto M3 x 3 x 4,5"
  ArcFitTolerance = 1e-06
  AttachmentSupport = -> [Pocket006]
  ExternalGeometry = -> [Binder001]
  ExternalTypes = [0]
  FullyConstrained = true
  MakeInternals = false
  MapMode = 5
  Placement = pos=(0,1.7e-15,0) rot=(0,0.707107,0.707107;3.14159rad)
  _ExternalGeoVersion = 0
  sketch-geometry (4):
    g0: Circle CenterX=43.2 CenterY=30.3 CenterZ=0 NormalX=0 NormalY=0 NormalZ=1 AngleXU=0 Radius=3.4
    g1: Circle CenterX=43.2 CenterY=12.1 CenterZ=0 NormalX=0 NormalY=0 NormalZ=1 AngleXU=0 Radius=3.4
    g2: Circle CenterX=18.6 CenterY=30.3 CenterZ=0 NormalX=0 NormalY=0 NormalZ=1 AngleXU=0 Radius=3.4
    g3: Circle CenterX=18.6 CenterY=12.1 CenterZ=0 NormalX=0 NormalY=0 NormalZ=1 AngleXU=0 Radius=3.4
  constraints (8):
    c: Diameter(g0) = 6.8
    c: Diameter(g1) = 6.8
    c: Diameter(g2) = 6.8
    c: Diameter(g3) = 6.8
    c: Coincident(g2,g-3)
    c: Coincident(g0,g-4)
    c: Coincident(g3,g-6)
    c: Coincident(g1,g-5)
FEATURE [PartDesign::Pad] Pad012
  BaseFeature = -> Pocket006
  Direction = (0,1,-2e-16)
  Length = 2.4
  Length2 = 10
  Profile = -> Sketch116
  ReferenceAxis = -> Sketch116 [N_Axis]
  Refine = true
  SideType = 0
  Suppressed = false
  Type = 0
  Type2 = 0
FEATURE [PartDesign::Pocket] Pocket007
  BaseFeature = -> Pad012
  Direction = (0,-1,2e-16)
  Length = 2.4
  Length2 = 0.6
  Profile = -> Sketch117
  ReferenceAxis = -> Sketch117 [N_Axis]
  Refine = true
  Reversed = true
  SideType = 1
  Suppressed = false
  Type = 0
  Type2 = 0
FEATURE [PartDesign::Pad] Pad013
  BaseFeature = -> Pocket007
  Direction = (0,-1,2e-16)
  Length = 1.6
  Length2 = 10
  Profile = -> Sketch118
  ReferenceAxis = -> Sketch118 [N_Axis]
  Refine = true
  SideType = 0
  Suppressed = false
  Type = 0
  Type2 = 0
FEATURE [Sketcher::SketchObject] Sketch119
  ArcFitTolerance = 1e-06
  AttachmentSupport = -> [Pad013]
  ExternalGeometry = -> [Binder001]
  ExternalTypes = [0]
  FullyConstrained = true
  MakeInternals = false
  MapMode = 5
  Placement = pos=(0,-3.6,0) rot=(1,0,0;1.5708rad)
  _ExternalGeoVersion = 0
  sketch-geometry (21):
    g0: LineSegment [constr] StartX=-82.8 StartY=3.2 StartZ=0 EndX=-82.8 EndY=39.2 EndZ=0
    g1: ArcOfCircle CenterX=-78.51 CenterY=34.8 CenterZ=0 NormalX=0 NormalY=0 NormalZ=1 AngleXU=0 Radius=3.5 StartAngle=4.71239 EndAngle=6.28319
    g2: ArcOfCircle CenterX=-78.51 CenterY=7.6 CenterZ=0 NormalX=0 NormalY=0 NormalZ=1 AngleXU=0 Radius=3.5 StartAngle=0 EndAngle=1.5708
    g3: ArcOfCircle CenterX=-5.6 CenterY=34.8 CenterZ=0 NormalX=0 NormalY=0 NormalZ=1 AngleXU=0 Radius=3.5 StartAngle=3.14159 EndAngle=4.71239
    g4: ArcOfCircle CenterX=-5.6 CenterY=7.6 CenterZ=0 NormalX=0 NormalY=0 NormalZ=1 AngleXU=0 Radius=3.5 StartAngle=1.5708 EndAngle=3.14159
    g5: LineSegment StartX=0 StartY=39.2 StartZ=0 EndX=0 EndY=31.3 EndZ=0
    g6: LineSegment StartX=0 StartY=39.2 StartZ=0 EndX=-9.1 EndY=39.2 EndZ=0
    g7: LineSegment StartX=0 StartY=3.2 StartZ=0 EndX=0 EndY=11.1 EndZ=0
    g8: LineSegment StartX=0 StartY=3.2 StartZ=0 EndX=-9.1 EndY=3.2 EndZ=0
    g9: LineSegment StartX=-82.8 StartY=3.2 StartZ=0 EndX=-75.01 EndY=3.2 EndZ=0
    g10: LineSegment StartX=-82.8 StartY=3.2 StartZ=0 EndX=-82.8 EndY=11.1 EndZ=0
    g11: LineSegment StartX=-82.8 StartY=39.2 StartZ=0 EndX=-82.8 EndY=31.3 EndZ=0
    g12: LineSegment StartX=-82.8 StartY=39.2 StartZ=0 EndX=-75.01 EndY=39.2 EndZ=0
    g13: LineSegment StartX=-82.8 StartY=31.3 StartZ=0 EndX=-78.51 EndY=31.3 EndZ=0
    g14: LineSegment StartX=-75.01 StartY=39.2 StartZ=0 EndX=-75.01 EndY=34.8 EndZ=0
    g15: LineSegment StartX=-82.8 StartY=11.1 StartZ=0 EndX=-78.51 EndY=11.1 EndZ=0
    g16: LineSegment StartX=-75.01 StartY=3.2 StartZ=0 EndX=-75.01 EndY=7.6 EndZ=0
    g17: LineSegment StartX=-9.1 StartY=39.2 StartZ=0 EndX=-9.1 EndY=34.8 EndZ=0
    g18: LineSegment StartX=0 StartY=31.3 StartZ=0 EndX=-5.6 EndY=31.3 EndZ=0
    g19: LineSegment StartX=0 StartY=11.1 StartZ=0 EndX=-5.6 EndY=11.1 EndZ=0
    g20: LineSegment StartX=-9.1 StartY=3.2 StartZ=0 EndX=-9.1 EndY=7.6 EndZ=0
  constraints (51):
    c: Coincident(g0,g-10)
    c: PointOnObject(g0,g-8)
    c: Vertical(g0)
    c: Coincident(g1,g-3)
    c: Coincident(g2,g-4)
    c: Coincident(g3,g-5)
    c: Coincident(g4,g-6)
    c: Radius(g4) = 3.5
    c: Radius(g3) = 3.5
    c: Radius(g1) = 3.5
    c: Radius(g2) = 3.5
    c: Coincident(g5,g-9)
    c: PointOnObject(g5,g-9)
    c: Coincident(g6,g5)
    c: PointOnObject(g6,g-8)
    c: Coincident(g7,g-9)
    c: PointOnObject(g7,g-9)
    c: Coincident(g8,g7)
    c: PointOnObject(g8,g-7)
    c: Coincident(g9,g0)
    c: PointOnObject(g9,g-7)
    c: Coincident(g10,g0)
    c: PointOnObject(g10,g0)
    c: Coincident(g11,g0)
    c: PointOnObject(g11,g0)
    c: Coincident(g12,g0)
    c: PointOnObject(g12,g-8)
    c: Coincident(g13,g11)
    c: Horizontal(g13)
    c: Coincident(g14,g12)
    c: Vertical(g14)
    c: Coincident(g15,g10)
    c: Horizontal(g15)
    c: Coincident(g16,g9)
    c: Vertical(g16)
    c: Coincident(g17,g6)
    c: Vertical(g17)
    c: Coincident(g18,g5)
    c: Horizontal(g18)
    c: Coincident(g19,g7)
    c: Horizontal(g19)
    c: Coincident(g20,g8)
    c: Vertical(g20)
    c: Tangent(g20,g4) = 1.5708
    c: Tangent(g4,g19) = -1.5708
    c: Tangent(g18,g3) = 1.5708
    c: Tangent(g3,g17) = -1.5708
    c: Tangent(g13,g1) = -1.5708
    c: Tangent(g1,g14) = 1.5708
    c: Tangent(g16,g2) = -1.5708
    c: Tangent(g2,g15) = 1.5708
FEATURE [PartDesign::Pocket] Pocket008
  BaseFeature = -> Pad013
  Direction = (0,1,-2e-16)
  Length = 1.6
  Length2 = 5
  Profile = -> Sketch119
  ReferenceAxis = -> Sketch119 [N_Axis]
  Refine = true
  SideType = 0
  Suppressed = false
  Type = 0
  Type2 = 0
FEATURE [PartDesign::Pad] Pad017
  BaseFeature = -> Pocket008
  Direction = (0,-1,2e-16)
  Length = 1.6
  Length2 = 10
  Profile = -> Sketch123
  ReferenceAxis = -> Sketch123 [N_Axis]
  Refine = true
  SideType = 0
  Suppressed = false
  Type = 0
  Type2 = 0
FEATURE [Sketcher::SketchObject] Sketch125
  ArcFitTolerance = 1e-06
  AttachmentSupport = -> [Pad017]
  ExternalGeometry = -> [Pad017]
  ExternalTypes = [0]
  FullyConstrained = true
  MakeInternals = false
  MapMode = 5
  Placement = pos=(0,-3.6,8e-16) rot=(1,0,0;1.5708rad)
  _ExternalGeoVersion = 0
  sketch-geometry (20):
    g0: LineSegment StartX=-108 StartY=35.8 StartZ=0 EndX=-108 EndY=35 EndZ=0
    g1: LineSegment StartX=-108 StartY=35 StartZ=0 EndX=-97 EndY=35 EndZ=0
    g2: LineSegment StartX=-97 StartY=35 StartZ=0 EndX=-97 EndY=35.8 EndZ=0
    g3: LineSegment StartX=-97 StartY=35.8 StartZ=0 EndX=-108 EndY=35.8 EndZ=0
    g4: LineSegment StartX=-108 StartY=28.6 StartZ=0 EndX=-108 EndY=27.8 EndZ=0
    g5: LineSegment StartX=-108 StartY=27.8 StartZ=0 EndX=-97 EndY=27.8 EndZ=0
    g6: LineSegment StartX=-97 StartY=27.8 StartZ=0 EndX=-97 EndY=28.6 EndZ=0
    g7: LineSegment StartX=-97 StartY=28.6 StartZ=0 EndX=-108 EndY=28.6 EndZ=0
    g8: LineSegment StartX=-108 StartY=30.4 StartZ=0 EndX=-108 EndY=29.6 EndZ=0
    g9: LineSegment StartX=-108 StartY=29.6 StartZ=0 EndX=-97 EndY=29.6 EndZ=0
    g10: LineSegment StartX=-97 StartY=29.6 StartZ=0 EndX=-97 EndY=30.4 EndZ=0
    g11: LineSegment StartX=-97 StartY=30.4 StartZ=0 EndX=-108 EndY=30.4 EndZ=0
    g12: LineSegment StartX=-108 StartY=32.2 StartZ=0 EndX=-108 EndY=31.4 EndZ=0
    g13: LineSegment StartX=-108 StartY=31.4 StartZ=0 EndX=-97 EndY=31.4 EndZ=0
    g14: LineSegment StartX=-97 StartY=31.4 StartZ=0 EndX=-97 EndY=32.2 EndZ=0
    g15: LineSegment StartX=-97 StartY=32.2 StartZ=0 EndX=-108 EndY=32.2 EndZ=0
    g16: LineSegment StartX=-108 StartY=34 StartZ=0 EndX=-108 EndY=33.2 EndZ=0
    g17: LineSegment StartX=-108 StartY=33.2 StartZ=0 EndX=-97 EndY=33.2 EndZ=0
    g18: LineSegment StartX=-97 StartY=33.2 StartZ=0 EndX=-97 EndY=34 EndZ=0
    g19: LineSegment StartX=-97 StartY=34 StartZ=0 EndX=-108 EndY=34 EndZ=0
  constraints (55):
    c: Coincident(g1,g0)
    c: Horizontal(g1)
    c: Coincident(g2,g1)
    c: Vertical(g2)
    c: Coincident(g3,g2)
    c: Horizontal(g3)
    c: Coincident(g3,g0)
    c: DistanceX(g1,g1) = 11
    c: DistanceY(g2,g2) = 0.8
    c: Coincident(g5,g4)
    c: Horizontal(g5)
    c: Coincident(g6,g5)
    c: Vertical(g6)
    c: Coincident(g7,g6)
    c: Horizontal(g7)
    c: Coincident(g7,g4)
    c: Coincident(g9,g8)
    c: Horizontal(g9)
    c: Coincident(g10,g9)
    c: Vertical(g10)
    c: Coincident(g11,g10)
    c: Horizontal(g11)
    c: Coincident(g11,g8)
    c: Coincident(g13,g12)
    c: Horizontal(g13)
    c: Coincident(g14,g13)
    c: Vertical(g14)
    c: Coincident(g15,g14)
    c: Horizontal(g15)
    c: Coincident(g15,g12)
    c: Coincident(g17,g16)
    c: Horizontal(g17)
    c: Coincident(g18,g17)
    c: Vertical(g18)
    c: Coincident(g19,g18)
    c: Horizontal(g19)
    c: Coincident(g19,g16)
    c: Equal(g3,g19)
    c: Equal(g3,g15)
    c: Equal(g3,g11)
    c: Equal(g3,g7)
    c: Equal(g2,g18)
    c: Equal(g2,g14)
    c: Equal(g2,g10)
    c: Equal(g2,g6)
    c: DistanceY(g-4,g4) = 1
    c: DistanceY(g4,g8) = 1
    c: DistanceY(g8,g12) = 1
    c: DistanceY(g12,g16) = 1
    c: DistanceY(g16,g0) = 1
    c: Tangent(g0,g-5)
    c: Tangent(g16,g-5)
    c: Tangent(g12,g-5)
    c: Tangent(g8,g-5)
    c: Tangent(g4,g-5)
FEATURE [PartDesign::Chamfer] Chamfer009
  Angle = 45
  Base = -> Pad017 [Edge151,Edge154]
  BaseFeature = -> Pad017
  ChamferType = 1
  FlipDirection = false
  Refine = true
  Size = 1.5
  Size2 = 2.8
  SupportTransform = false
  Suppressed = false
  UseAllEdges = false
FEATURE [PartDesign::Pocket] Pocket009
  BaseFeature = -> Chamfer009
  Direction = (0,1,-2e-16)
  Length = 1
  Length2 = 5
  Profile = -> Sketch125
  ReferenceAxis = -> Sketch125 [N_Axis]
  Refine = true
  SideType = 0
  Suppressed = false
  Type = 0
  Type2 = 0
FEATURE [PartDesign::Pad] Pad014
  BaseFeature = -> Pocket009
  Direction = (0,-1,2e-16)
  Length = 0.8
  Length2 = 10
  Profile = -> Sketch120
  ReferenceAxis = -> Sketch120 [N_Axis]
  Refine = true
  SideType = 0
  Suppressed = false
  Type = 0
  Type2 = 0
FEATURE [Sketcher::SketchObject] Sketch124
  ArcFitTolerance = 1e-06
  AttachmentSupport = -> [Pad014]
  ExternalGeometry = -> [Binder001]
  ExternalTypes = [0]
  FullyConstrained = true
  MakeInternals = false
  MapMode = 5
  Placement = pos=(0,-2.8,6e-16) rot=(1,0,0;1.5708rad)
  _ExternalGeoVersion = 0
  sketch-geometry (4):
    g0: LineSegment StartX=-129 StartY=39.2 StartZ=0 EndX=-131.599 EndY=31.2 EndZ=0
    g1: LineSegment StartX=-118 StartY=39.2 StartZ=0 EndX=-120.599 EndY=31.2 EndZ=0
    g2: LineSegment StartX=-129 StartY=39.2 StartZ=0 EndX=-118 EndY=39.2 EndZ=0
    g3: LineSegment StartX=-120.599 StartY=31.2 StartZ=0 EndX=-131.599 EndY=31.2 EndZ=0
  constraints (12):
    c: PointOnObject(g0,g-3)
    c: PointOnObject(g1,g-3)
    c: Parallel(g-4,g0)
    c: Parallel(g-4,g1)
    c: Coincident(g2,g0)
    c: Coincident(g2,g1)
    c: DistanceX(g2,g2) = 11
    c: DistanceY(g1,g1) = 8
    c: Coincident(g3,g1)
    c: Horizontal(g3)
    c: Coincident(g3,g0)
    c: DistanceX(g1,g-3) = 118
FEATURE [PartDesign::Pad] Pad018
  BaseFeature = -> Pad014
  Direction = (0,-1,2e-16)
  Length = 1.2
  Length2 = 10
  Profile = -> Sketch124
  ReferenceAxis = -> Sketch124 [N_Axis]
  Refine = true
  SideType = 0
  Suppressed = false
  Type = 0
  Type2 = 0
FEATURE [Sketcher::SketchObject] Sketch126
  ArcFitTolerance = 1e-06
  AttachmentSupport = -> [Pad018]
  ExternalGeometry = -> [Pad018]
  ExternalTypes = [0]
  FullyConstrained = true
  MakeInternals = false
  MapMode = 5
  Placement = pos=(0,-4,0) rot=(1,0,0;1.5708rad)
  _ExternalGeoVersion = 0
  sketch-geometry (8):
    g0: LineSegment StartX=-129.877 StartY=36.5 StartZ=0 EndX=-130.137 EndY=35.7 EndZ=0
    g1: LineSegment StartX=-130.69 StartY=34 StartZ=0 EndX=-130.95 EndY=33.2 EndZ=0
    g2: LineSegment StartX=-129.877 StartY=36.5 StartZ=0 EndX=-118.877 EndY=36.5 EndZ=0
    g3: LineSegment StartX=-130.137 StartY=35.7 StartZ=0 EndX=-119.137 EndY=35.7 EndZ=0
    g4: LineSegment StartX=-130.69 StartY=34 StartZ=0 EndX=-119.69 EndY=34 EndZ=0
    g5: LineSegment StartX=-130.95 StartY=33.2 StartZ=0 EndX=-119.95 EndY=33.2 EndZ=0
    g6: LineSegment StartX=-118.877 StartY=36.5 StartZ=0 EndX=-119.137 EndY=35.7 EndZ=0
    g7: LineSegment StartX=-119.69 StartY=34 StartZ=0 EndX=-119.95 EndY=33.2 EndZ=0
  constraints (20):
    c: Coincident(g2,g0)
    c: Horizontal(g2)
    c: Coincident(g3,g0)
    c: Horizontal(g3)
    c: Coincident(g4,g1)
    c: Horizontal(g4)
    c: Coincident(g5,g1)
    c: Horizontal(g5)
    c: Coincident(g6,g2)
    c: Coincident(g6,g3)
    c: Coincident(g7,g4)
    c: Coincident(g7,g5)
    c: Tangent(g0,g-4)
    c: Tangent(g6,g-5)
    c: Tangent(g1,g-4)
    c: Tangent(g7,g-5)
    c: DistanceY(g3,g2) = 0.8
    c: DistanceY(g5,g4) = 0.8
    c: DistanceY(g-6,g1) = 2
    c: DistanceY(g-6,g0) = 4.5
FEATURE [PartDesign::Chamfer] Chamfer008
  Angle = 45
  Base = -> Pad018 [Edge257]
  BaseFeature = -> Pad018
  ChamferType = 1
  FlipDirection = false
  Refine = true
  Size = 1
  Size2 = 6
  SupportTransform = false
  Suppressed = false
  UseAllEdges = false
FEATURE [PartDesign::Pocket] Pocket010
  BaseFeature = -> Chamfer008
  Direction = (0,1,-2e-16)
  Length = 1
  Length2 = 5
  Profile = -> Sketch126
  ReferenceAxis = -> Sketch126 [N_Axis]
  Refine = true
  SideType = 0
  Suppressed = false
  Type = 0
  Type2 = 0
FEATURE [PartDesign::Pad] Pad015
  BaseFeature = -> Pocket010
  Direction = (0,-1,2e-16)
  Length = 2
  Length2 = 10
  Profile = -> Sketch121
  ReferenceAxis = -> Sketch121 [N_Axis]
  Refine = true
  SideType = 0
  Suppressed = false
  Type = 0
  Type2 = 0
FEATURE [PartDesign::Pad] Pad016
  BaseFeature = -> Pad015
  Direction = (0,-1,2e-16)
  Length = 1.6
  Length2 = 10
  Profile = -> Sketch122
  ReferenceAxis = -> Sketch122 [N_Axis]
  Refine = true
  SideType = 0
  Suppressed = false
  Type = 0
  Type2 = 0
FEATURE [Sketcher::SketchObject] Sketch129
  ArcFitTolerance = 1e-06
  AttachmentSupport = -> [Pad016]
  ExternalGeometry = -> [Binder001]
  ExternalTypes = [0]
  FullyConstrained = true
  MakeInternals = false
  MapMode = 5
  Placement = pos=(0,-3.6,0) rot=(1,0,0;1.5708rad)
  _ExternalGeoVersion = 0
  sketch-geometry (12):
    g0: LineSegment [constr] StartX=-192.176 StartY=-3.18451 StartZ=0 EndX=-181.223 EndY=20.303 EndZ=0
    g1: LineSegment [constr] StartX=-202.765 StartY=20.303 StartZ=0 EndX=-181.223 EndY=20.303 EndZ=0
    g2: LineSegment StartX=-202.765 StartY=20.303 StartZ=0 EndX=-181.223 EndY=20.303 EndZ=0
    g3: LineSegment StartX=-192.176 StartY=-3.18451 StartZ=0 EndX=-196.804 EndY=-13.1107 EndZ=0
    g4: ArcOfCircle CenterX=-207.583 CenterY=4 CenterZ=0 NormalX=0 NormalY=0 NormalZ=1 AngleXU=0 Radius=17 StartAngle=5.84685 EndAngle=7.56663
    g5: ArcOfEllipse CenterX=-181.223 CenterY=8.55923 CenterZ=0 NormalX=0 NormalY=0 NormalZ=1 MajorRadius=23.4779 MinorRadius=11.7437 AngleXU=2e-16 StartAngle=4.71239 EndAngle=7.85398
    g6: LineSegment [constr] StartX=-157.745 StartY=8.55923 StartZ=0 EndX=-204.701 EndY=8.55923 EndZ=0
    g7: LineSegment [constr] StartX=-181.223 StartY=20.303 StartZ=0 EndX=-181.223 EndY=-3.18451 EndZ=0
    g8: GeomPoint [constr] X=-160.894 Y=8.55923 Z=0
    g9: GeomPoint [constr] X=-201.553 Y=8.55923 Z=0
    g10: ArcOfCircle CenterX=-181.223 CenterY=-20.3763 CenterZ=0 NormalX=0 NormalY=0 NormalZ=1 AngleXU=0 Radius=17.1918 StartAngle=1.57079 EndAngle=2.70526
    g11: GeomPoint [constr] X=-181.223 Y=-3.18451 Z=0
  constraints (23):
    c: Coincident(g0,g-5)
    c: Coincident(g1,g-6)
    c: Horizontal(g1)
    c: Coincident(g1,g0)
    c: Parallel(g0,g-4)
    c: Coincident(g2,g1)
    c: Coincident(g2,g0)
    c: Coincident(g3,g0)
    c: Equal(g4,g-5)
    c: Coincident(g4,g1)
    c: Coincident(g4,g0)
    c: InternalAlignment(g6-g9 -> g5) x4
    c: Vertical(g5,g0)
    c: Horizontal(g6)
    c: Coincident(g5,g0)
    c: DistanceX(g6,g-3) = 10.1
    c: Tangent(g10,g3) = -1.5708
    c: PointOnObject(g11,g10)
    c: Tangent(g5,g10,g11) = 1.5708
    c: Coincident(g10,g5)
    c: Coincident(g11,g7)
    c: Parallel(g3,g-4)
    c: Horizontal(g5,g0)
FEATURE [Sketcher::SketchObject] Sketch130
  ArcFitTolerance = 1e-06
  AttachmentOffset = pos=(0,0,-1.6) rot=(0,0,1;0rad)
  AttachmentSupport = -> [Pad016]
  ExternalGeometry = -> [Binder001]
  ExternalTypes = [0]
  FullyConstrained = true
  MakeInternals = false
  MapMode = 5
  Placement = pos=(0,-2,-4e-16) rot=(1,0,0;1.5708rad)
  _ExternalGeoVersion = 0
  sketch-geometry (12):
    g0: LineSegment [constr] StartX=-192.176 StartY=-3.18451 StartZ=0 EndX=-181.223 EndY=20.303 EndZ=0
    g1: LineSegment [constr] StartX=-202.765 StartY=20.303 StartZ=0 EndX=-181.223 EndY=20.303 EndZ=0
    g2: LineSegment StartX=-202.765 StartY=20.303 StartZ=0 EndX=-181.223 EndY=20.303 EndZ=0
    g3: LineSegment StartX=-192.176 StartY=-3.18451 StartZ=0 EndX=-193.827 EndY=-6.72678 EndZ=0
    g4: ArcOfCircle CenterX=-207.583 CenterY=4 CenterZ=0 NormalX=0 NormalY=0 NormalZ=1 AngleXU=0 Radius=17 StartAngle=5.84685 EndAngle=7.56663
    g5: ArcOfEllipse CenterX=-181.223 CenterY=10.803 CenterZ=0 NormalX=0 NormalY=0 NormalZ=1 MajorRadius=14.4779 MinorRadius=9.5 AngleXU=0 StartAngle=4.71239 EndAngle=7.85398
    g6: LineSegment [constr] StartX=-166.745 StartY=10.803 StartZ=0 EndX=-195.701 EndY=10.803 EndZ=0
    g7: LineSegment [constr] StartX=-181.223 StartY=20.303 StartZ=0 EndX=-181.223 EndY=1.30297 EndZ=0
    g8: GeomPoint [constr] X=-170.298 Y=10.803 Z=0
    g9: GeomPoint [constr] X=-192.148 Y=10.803 Z=0
    g10: ArcOfCircle CenterX=-181.223 CenterY=-12.6042 CenterZ=0 NormalX=0 NormalY=0 NormalZ=1 AngleXU=0 Radius=13.9072 StartAngle=1.5708 EndAngle=2.70526
    g11: GeomPoint [constr] X=-181.223 Y=1.30297 Z=0
  constraints (23):
    c: Coincident(g0,g-5)
    c: Coincident(g1,g-6)
    c: Horizontal(g1)
    c: Coincident(g1,g0)
    c: Parallel(g0,g-4)
    c: Coincident(g2,g1)
    c: Coincident(g2,g0)
    c: Coincident(g3,g0)
    c: Equal(g4,g-5)
    c: Coincident(g4,g1)
    c: Coincident(g4,g0)
    c: InternalAlignment(g6-g9 -> g5) x4
    c: Vertical(g5,g0)
    c: Horizontal(g6)
    c: Coincident(g5,g0)
    c: DistanceX(g6,g-3) = 19.1
    c: Tangent(g10,g3) = -1.5708
    c: PointOnObject(g11,g10)
    c: Tangent(g5,g10,g11) = 1.5708
    c: Coincident(g10,g5)
    c: Coincident(g11,g7)
    c: Parallel(g3,g-4)
    c: DistanceY(g5,g0) = 19
FEATURE [Part::Part2DObjectPython] Clone2D001  label="Sketch130 (2D)"  # Draft 2D object (typed FeaturePython)
  ForceCompound = false
  Fuse = false
  Objects = -> [Sketch130]
  Placement = pos=(0,-2,-4e-16) rot=(1,0,0;1.5708rad)
  Scale = (1,1,1)
FEATURE [Sketcher::SketchObject] Sketch131
  ArcFitTolerance = 1e-06
  AttachmentOffset = pos=(0,0,-3.5) rot=(0,0,1;0rad)
  AttachmentSupport = -> [Pad016]
  ExternalGeometry = -> [Binder001]
  ExternalTypes = [0]
  FullyConstrained = true
  MakeInternals = false
  MapMode = 5
  Placement = pos=(0,-0.1,-8e-16) rot=(1,0,0;1.5708rad)
  _ExternalGeoVersion = 0
  sketch-geometry (1):
    g0: GeomPoint X=-197.47 Y=8.55923 Z=0
  constraints (1):
    c: Symmetric(g-6,g-4,g0)
FEATURE [Sketcher::SketchObject] Sketch132
  ArcFitTolerance = 1e-06
  AttachmentSupport = -> [Pad016]
  ExternalGeometry = -> [Binder001]
  ExternalTypes = [0]
  FullyConstrained = true
  MakeInternals = false
  MapMode = 5
  Placement = pos=(0,-3.6,0) rot=(1,0,0;1.5708rad)
  _ExternalGeoVersion = 0
  sketch-geometry (3):
    g0: LineSegment [constr] StartX=-215.42 StartY=-53.0314 StartZ=0 EndX=-167.782 EndY=-53.0314 EndZ=0
    g1: Circle CenterX=-191.282 CenterY=-53.0314 CenterZ=0 NormalX=0 NormalY=0 NormalZ=1 AngleXU=0 Radius=11.5
    g2: Circle CenterX=-191.282 CenterY=-53.0314 CenterZ=0 NormalX=0 NormalY=0 NormalZ=1 AngleXU=0 Radius=10.7
  constraints (8):
    c: Coincident(g0,g-3)
    c: PointOnObject(g0,g-4)
    c: Horizontal(g0)
    c: Diameter(g1) = 23
    c: PointOnObject(g1,g0)
    c: DistanceX(g1,g0) = 23.5
    c: Diameter(g2) = 21.4
    c: Coincident(g2,g1)
FEATURE [Part::Part2DObjectPython] ShapeString  # Draft 2D object (typed FeaturePython)
  FontFile = <path>
  Fuse = false
  Justification = 6
  JustificationReference = 0
  KeepLeftMargin = false
  MakeFace = true
  ObliqueAngle = 0
  Placement = pos=(-199,-3.6,-57.5) rot=(1,0,0;1.5708rad)
  ScaleToSize = true
  Size = 10
  String = AS
  Tracking = 0
FEATURE [Sketcher::SketchObject] Sketch133
  ArcFitTolerance = 1e-06
  AttachmentSupport = -> [Binder]
  ExternalGeometry = -> [Binder]
  ExternalTypes = [0]
  FullyConstrained = true
  MakeInternals = false
  MapMode = 5
  Placement = pos=(0,9e-16,0) rot=(0,0.707107,0.707107;3.14159rad)
  _ExternalGeoVersion = 0
  sketch-geometry (30):
    g0: LineSegment StartX=0 StartY=39.2 StartZ=0 EndX=0 EndY=3.2 EndZ=0
    g1: LineSegment StartX=0 StartY=3.2 StartZ=0 EndX=82.8 EndY=3.2 EndZ=0
    g2: LineSegment StartX=82.8 StartY=3.2 StartZ=0 EndX=82.8 EndY=6.2 EndZ=0
    g3: LineSegment StartX=82.8 StartY=6.2 StartZ=0 EndX=91.752 EndY=6.2 EndZ=0
    g4: LineSegment StartX=0 StartY=39.2 StartZ=0 EndX=195.887 EndY=39.2 EndZ=0
    g5: LineSegment StartX=195.887 StartY=39.2 StartZ=0 EndX=202.765 EndY=20.303 EndZ=0
    g6: LineSegment StartX=192.333 StartY=24.9893 StartZ=0 EndX=196.467 EndY=26.4942 EndZ=0
    g7: LineSegment StartX=196.467 StartY=26.4942 StartZ=0 EndX=194.073 EndY=33.0721 EndZ=0
    g8: LineSegment StartX=194.073 StartY=33.0721 StartZ=0 EndX=189.939 EndY=31.5672 EndZ=0
    g9: LineSegment StartX=189.939 StartY=31.5672 StartZ=0 EndX=192.333 EndY=24.9893 EndZ=0
    g10: ArcOfCircle CenterX=107.6 CenterY=4 CenterZ=0 NormalX=0 NormalY=0 NormalZ=1 AngleXU=0 Radius=16 StartAngle=1.5708 EndAngle=3.00366
    g11: LineSegment StartX=107.6 StartY=20 StartZ=0 EndX=132.428 EndY=20 EndZ=0
    g12: ArcOfCircle [constr] CenterX=132.428 CenterY=4 CenterZ=0 NormalX=0 NormalY=0 NormalZ=1 AngleXU=0 Radius=16 StartAngle=0.314159 EndAngle=1.5708
    g13: LineSegment StartX=147.645 StartY=8.94427 StartZ=0 EndX=176.685 EndY=-80.4316 EndZ=0
    g14: LineSegment StartX=176.685 StartY=-80.4316 StartZ=0 EndX=215.932 EndY=-80.4316 EndZ=0
    g15: ArcOfCircle CenterX=207.583 CenterY=4 CenterZ=0 NormalX=0 NormalY=0 NormalZ=1 AngleXU=0 Radius=17 StartAngle=1.85815 EndAngle=3.57792
    g16: ArcOfCircle CenterX=184.801 CenterY=-67.3089 CenterZ=0 NormalX=0 NormalY=0 NormalZ=1 AngleXU=0 Radius=33.7833 StartAngle=5.88425 EndAngle=6.71952
    g17: LineSegment StartX=192.176 StartY=-3.18451 StartZ=0 EndX=215.42 EndY=-53.0314 EndZ=0
    g18: Circle CenterX=5.6 CenterY=34.8 CenterZ=0 NormalX=0 NormalY=0 NormalZ=1 AngleXU=0 Radius=1.8
    g19: Circle CenterX=5.6 CenterY=7.6 CenterZ=0 NormalX=0 NormalY=0 NormalZ=1 AngleXU=0 Radius=1.8
    g20: Circle CenterX=78.51 CenterY=34.8 CenterZ=0 NormalX=0 NormalY=0 NormalZ=1 AngleXU=0 Radius=1.8
    g21: Circle CenterX=78.51 CenterY=7.6 CenterZ=0 NormalX=0 NormalY=0 NormalZ=1 AngleXU=0 Radius=1.8
    g22: Circle CenterX=184.08 CenterY=34.8 CenterZ=0 NormalX=0 NormalY=0 NormalZ=1 AngleXU=0 Radius=1.8
    g23: Circle CenterX=179.305 CenterY=-76.8316 CenterZ=0 NormalX=0 NormalY=0 NormalZ=1 AngleXU=0 Radius=1.8
    g24: Circle CenterX=213.443 CenterY=-76.8316 CenterZ=0 NormalX=0 NormalY=0 NormalZ=1 AngleXU=0 Radius=1.8
    g25: Circle CenterX=19 CenterY=21.2 CenterZ=0 NormalX=0 NormalY=0 NormalZ=1 AngleXU=0 Radius=6.3
    g26: Circle CenterX=42 CenterY=21.2 CenterZ=0 NormalX=0 NormalY=0 NormalZ=1 AngleXU=0 Radius=6.3
    g27: Circle CenterX=65 CenterY=21.2 CenterZ=0 NormalX=0 NormalY=0 NormalZ=1 AngleXU=0 Radius=6.3
    g28: LineSegment StartX=132.428 StartY=20 StartZ=0 EndX=144.053 EndY=20 EndZ=0
    g29: LineSegment StartX=147.645 StartY=8.94427 StartZ=0 EndX=144.053 EndY=20 EndZ=0
  constraints (65):
    c: Coincident(g0,g-4)
    c: Coincident(g0,g-5)
    c: Coincident(g1,g0)
    c: Coincident(g1,g-6)
    c: Coincident(g2,g1)
    c: Coincident(g2,g-7)
    c: Coincident(g3,g2)
    c: Coincident(g3,g-8)
    c: Coincident(g4,g0)
    c: Coincident(g4,g-16)
    c: Coincident(g5,g4)
    c: Coincident(g5,g-16)
    c: Coincident(g6,g-20)
    c: Coincident(g6,g-21)
    c: Coincident(g7,g6)
    c: Coincident(g7,g-23)
    c: Coincident(g8,g7)
    c: Coincident(g8,g-22)
    c: Coincident(g9,g8)
    c: Coincident(g9,g6)
    c: Equal(g10,g-8)
    c: Coincident(g10,g3)
    c: Coincident(g10,g-9)
    c: Coincident(g11,g10)
    c: Coincident(g11,g-10)
    c: Equal(g12,g-10)
    c: Coincident(g12,g11)
    c: Coincident(g12,g-11)
    c: Coincident(g13,g12)
    c: Coincident(g13,g-12)
    c: Coincident(g14,g13)
    c: Coincident(g14,g-13)
    c: Equal(g15,g-15)
    c: Coincident(g15,g5)
    c: Coincident(g15,g-15)
    c: Equal(g16,g-13)
    c: Coincident(g16,g14)
    c: Coincident(g16,g-14)
    c: Coincident(g17,g15)
    c: Coincident(g17,g16)
    c: Equal(g18,g-28)
    c: Equal(g19,g-29)
    c: Equal(g20,g-26)
    c: Equal(g21,g-27)
    c: Equal(g22,g-17)
    c: Equal(g24,g-25)
    c: Equal(g23,g-24)
    c: Coincident(g23,g-24)
    c: Coincident(g24,g-25)
    c: Coincident(g22,g-17)
    c: Coincident(g20,g-26)
    c: Coincident(g21,g-27)
    c: Coincident(g18,g-28)
    c: Coincident(g19,g-29)
    c: Equal(g25,g-30)
    c: Equal(g26,g-31)
    c: Equal(g27,g-32)
    c: Coincident(g25,g-30)
    c: Coincident(g26,g-31)
    c: Coincident(g27,g-32)
    c: Parallel(g28,g11)
    c: Parallel(g29,g13)
    c: Coincident(g28,g11)
    c: Coincident(g29,g12)
    c: Coincident(g29,g28)
FEATURE [PartDesign::Pad] Pad019
  Direction = (0,1,-2e-16)
  Length = 2
  Length2 = 10
  Profile = -> Sketch133
  ReferenceAxis = -> Sketch133 [N_Axis]
  Refine = true
  SideType = 0
  Suppressed = false
  Type = 0
  Type2 = 0
FEATURE [Sketcher::SketchObject] Sketch091  label="Sketch091 - forma anteriore"
  ArcFitTolerance = 1e-06
  AttachmentSupport = -> [Pad019]
  ExternalGeometry = -> [Binder]
  ExternalTypes = [0]
  FullyConstrained = true
  MakeInternals = false
  MapMode = 5
  Placement = pos=(0,2,0) rot=(0,0.707107,0.707107;3.14159rad)
  _ExternalGeoVersion = 0
  sketch-geometry (12):
    g0: Circle CenterX=5.6 CenterY=34.8 CenterZ=0 NormalX=0 NormalY=0 NormalZ=1 AngleXU=0 Radius=1.8
    g1: Circle CenterX=5.6 CenterY=7.6 CenterZ=0 NormalX=0 NormalY=0 NormalZ=1 AngleXU=0 Radius=1.8
    g2: Circle CenterX=78.51 CenterY=34.8 CenterZ=0 NormalX=0 NormalY=0 NormalZ=1 AngleXU=0 Radius=1.8
    g3: Circle CenterX=78.51 CenterY=7.6 CenterZ=0 NormalX=0 NormalY=0 NormalZ=1 AngleXU=0 Radius=1.8
    g4: LineSegment StartX=0 StartY=39.2 StartZ=0 EndX=0 EndY=3.2 EndZ=0
    g5: LineSegment StartX=0 StartY=3.2 StartZ=0 EndX=82.8 EndY=3.2 EndZ=0
    g6: LineSegment StartX=82.8 StartY=3.2 StartZ=0 EndX=82.8 EndY=39.2 EndZ=0
    g7: LineSegment StartX=82.8 StartY=39.2 StartZ=0 EndX=0 EndY=39.2 EndZ=0
    g8: ArcOfCircle CenterX=19 CenterY=21.2 CenterZ=0 NormalX=0 NormalY=0 NormalZ=1 AngleXU=0 Radius=10 StartAngle=1.5708 EndAngle=4.71239
    g9: ArcOfCircle CenterX=65 CenterY=21.2 CenterZ=0 NormalX=0 NormalY=0 NormalZ=1 AngleXU=0 Radius=10 StartAngle=4.71239 EndAngle=7.85398
    g10: LineSegment StartX=19 StartY=31.2 StartZ=0 EndX=65 EndY=31.2 EndZ=0
    g11: LineSegment StartX=19 StartY=11.2 StartZ=0 EndX=65 EndY=11.2 EndZ=0
  constraints (25):
    c: Equal(g2,g-7)
    c: Equal(g3,g-8)
    c: Equal(g1,g-13)
    c: Equal(g0,g-12)
    c: Coincident(g0,g-12)
    c: Coincident(g1,g-13)
    c: Coincident(g3,g-8)
    c: Coincident(g2,g-7)
    c: Coincident(g4,g-4)
    c: Coincident(g4,g-5)
    c: Coincident(g5,g4)
    c: Coincident(g5,g-6)
    c: Coincident(g6,g5)
    c: PointOnObject(g6,g-3)
    c: Vertical(g6)
    c: Coincident(g7,g6)
    c: Coincident(g7,g4)
    c: Tangent(g8,g10) = 1.5708
    c: Tangent(g8,g11) = -1.5708
    c: Tangent(g9,g10) = 1.5708
    c: Tangent(g9,g11) = -1.5708
    c: Equal(g8,g9)
    c: Radius(g8) = 10
    c: Coincident(g8,g-11)
    c: Coincident(g9,g-9)
FEATURE [Sketcher::SketchObject] Sketch093  label="Sketch093 - scavi interni pulsanti"
  ArcFitTolerance = 1e-06
  AttachmentSupport = -> [Pad019]
  ExternalGeometry = -> [Binder]
  ExternalTypes = [0]
  FullyConstrained = true
  MakeInternals = false
  MapMode = 5
  Placement = pos=(0,1.8e-15,0) rot=(1,0,0;1.5708rad)
  _ExternalGeoVersion = 0
  sketch-geometry (3):
    g0: Circle CenterX=-65 CenterY=21.2 CenterZ=0 NormalX=0 NormalY=0 NormalZ=1 AngleXU=0 Radius=7.3
    g1: Circle CenterX=-42 CenterY=21.2 CenterZ=0 NormalX=0 NormalY=0 NormalZ=1 AngleXU=0 Radius=7.3
    g2: Circle CenterX=-19 CenterY=21.2 CenterZ=0 NormalX=0 NormalY=0 NormalZ=1 AngleXU=0 Radius=7.3
  constraints (6):
    c: Coincident(g0,g-3)
    c: Coincident(g1,g-4)
    c: Coincident(g2,g-5)
    c: Diameter(g0) = 14.6
    c: Diameter(g1) = 14.6
    c: Diameter(g2) = 14.6
FEATURE [Sketcher::SketchObject] Sketch094  label="Sketch094 - forma centrale"
  ArcFitTolerance = 1e-06
  AttachmentSupport = -> [Pad019]
  ExternalGeometry = -> [Binder]
  ExternalTypes = [0]
  FullyConstrained = true
  MakeInternals = false
  MapMode = 5
  Placement = pos=(0,2,0) rot=(0,0.707107,0.707107;3.14159rad)
  _ExternalGeoVersion = 0
  sketch-geometry (4):
    g0: LineSegment StartX=137.815 StartY=39.2 StartZ=0 EndX=142.655 EndY=24.303 EndZ=0
    g1: LineSegment StartX=110.815 StartY=24.303 StartZ=0 EndX=142.655 EndY=24.303 EndZ=0
    g2: LineSegment StartX=137.815 StartY=39.2 StartZ=0 EndX=110.815 EndY=39.2 EndZ=0
    g3: ArcOfCircle CenterX=92.2534 CenterY=31.7515 CenterZ=0 NormalX=0 NormalY=0 NormalZ=1 AngleXU=0 Radius=20 StartAngle=5.90156 EndAngle=6.66481
  constraints (12):
    c: PointOnObject(g0,g-3)
    c: Tangent(g0,g-5)
    c: Horizontal(g1)
    c: Coincident(g1,g0)
    c: Coincident(g2,g0)
    c: PointOnObject(g2,g-3)
    c: DistanceX(g2,g2) = 27
    c: Vertical(g1,g2)
    c: Coincident(g3,g2)
    c: Radius(g3) = 20
    c: Coincident(g3,g1)
    c: DistanceY(g-6,g0) = 4
FEATURE [Sketcher::SketchObject] Sketch095  label="Sketch095 - forma posteriore"
  ArcFitTolerance = 1e-06
  AttachmentSupport = -> [Pad019]
  ExternalGeometry = -> [Binder]
  ExternalTypes = [0]
  FullyConstrained = true
  MakeInternals = false
  MapMode = 5
  Placement = pos=(0,2,0) rot=(0,0.707107,0.707107;3.14159rad)
  _ExternalGeoVersion = 0
  sketch-geometry (15):
    g0: LineSegment StartX=137.815 StartY=39.2 StartZ=0 EndX=143.955 EndY=20.303 EndZ=0
    g1: LineSegment StartX=143.955 StartY=20.303 StartZ=0 EndX=190.141 EndY=20.303 EndZ=0
    g2: ArcOfCircle CenterX=184.08 CenterY=34.8 CenterZ=0 NormalX=0 NormalY=0 NormalZ=1 AngleXU=0 Radius=3.5 StartAngle=3.49066 EndAngle=4.71239
    g3: LineSegment StartX=180.791 StartY=33.6029 StartZ=0 EndX=178.754 EndY=39.2 EndZ=0
    g4: LineSegment StartX=184.08 StartY=31.3 StartZ=0 EndX=186.139 EndY=31.3 EndZ=0
    g5: LineSegment StartX=190.141 StartY=20.303 StartZ=0 EndX=186.139 EndY=31.3 EndZ=0
    g6: LineSegment StartX=137.815 StartY=39.2 StartZ=0 EndX=156.815 EndY=39.2 EndZ=0
    g7: LineSegment StartX=178.754 StartY=39.2 StartZ=0 EndX=168.815 EndY=39.2 EndZ=0
    g8: LineSegment StartX=156.815 StartY=31.2 StartZ=0 EndX=168.815 EndY=31.2 EndZ=0
    g9: ArcOfCircle CenterX=176.411 CenterY=35.2 CenterZ=0 NormalX=0 NormalY=0 NormalZ=1 AngleXU=0 Radius=20 StartAngle=2.94023 EndAngle=3.34295
    g10: ArcOfCircle CenterX=188.411 CenterY=35.2 CenterZ=0 NormalX=0 NormalY=0 NormalZ=1 AngleXU=0 Radius=20 StartAngle=2.94023 EndAngle=3.34295
    g11: LineSegment StartX=157.815 StartY=39.2 StartZ=0 EndX=167.815 EndY=39.2 EndZ=0
    g12: LineSegment StartX=157.436 StartY=36.2 StartZ=0 EndX=167.436 EndY=36.2 EndZ=0
    g13: ArcOfCircle CenterX=177.411 CenterY=35.2 CenterZ=0 NormalX=0 NormalY=0 NormalZ=1 AngleXU=0 Radius=20 StartAngle=2.94023 EndAngle=3.09157
    g14: ArcOfCircle CenterX=187.411 CenterY=35.2 CenterZ=0 NormalX=0 NormalY=0 NormalZ=1 AngleXU=0 Radius=20 StartAngle=2.94023 EndAngle=3.09157
  constraints (46):
    c: PointOnObject(g0,g-3)
    c: Tangent(g0,g-6)
    c: Coincident(g1,g0)
    c: Horizontal(g1)
    c: Radius(g2) = 3.5
    c: Coincident(g2,g-5)
    c: PointOnObject(g3,g-3)
    c: Parallel(g3,g-4)
    c: Tangent(g3,g2) = 1.5708
    c: Horizontal(g4)
    c: Tangent(g4,g2) = -1.5708
    c: Coincident(g5,g1)
    c: Parallel(g5,g-4)
    c: Coincident(g5,g4)
    c: DistanceX(g4,g-8) = 3.8
    c: Coincident(g6,g0)
    c: PointOnObject(g6,g-3)
    c: Coincident(g7,g3)
    c: PointOnObject(g7,g-3)
    c: Horizontal(g8)
    c: DistanceX(g6,g7) = 12
    c: Vertical(g8,g6)
    c: Vertical(g7,g8)
    c: DistanceY(g8,g6) = 8
    c: Coincident(g9,g8)
    c: Coincident(g9,g6)
    c: Coincident(g10,g7)
    c: Coincident(g10,g8)
    c: Radius(g9) = 20
    c: Radius(g10) = 20
    c: PointOnObject(g11,g-3)
    c: PointOnObject(g11,g-3)
    c: DistanceX(g11,g11) = 10
    c: DistanceX(g6,g11) = 1
    c: Horizontal(g12)
    c: Equal(g12,g11)
    c: DistanceY(g12,g11) = 3
    c: Coincident(g13,g11)
    c: Coincident(g13,g12)
    c: Radius(g13) = 20
    c: Coincident(g14,g11)
    c: Coincident(g14,g12)
    c: Radius(g14) = 20
    c: DistanceX(g0,g6) = 19
    c: Horizontal(g9,g13)
    c: Horizontal(g0,g-4)
FEATURE [Sketcher::SketchObject] Sketch096  label="Sketch096 - forma impugnatura"
  ArcFitTolerance = 1e-06
  AttachmentSupport = -> [Pad019]
  ExternalGeometry = -> [Binder]
  ExternalTypes = [0]
  FullyConstrained = true
  MakeInternals = false
  MapMode = 5
  Placement = pos=(0,2,0) rot=(0,0.707107,0.707107;3.14159rad)
  _ExternalGeoVersion = 0
  sketch-geometry (8):
    g0: LineSegment StartX=176.685 StartY=-80.4316 StartZ=0 EndX=143.955 EndY=20.303 EndZ=0
    g1: LineSegment StartX=176.685 StartY=-80.4316 StartZ=0 EndX=215.932 EndY=-80.4316 EndZ=0
    g2: Circle CenterX=179.305 CenterY=-76.8316 CenterZ=0 NormalX=0 NormalY=0 NormalZ=1 AngleXU=0 Radius=3
    g3: Circle CenterX=213.443 CenterY=-76.8316 CenterZ=0 NormalX=0 NormalY=0 NormalZ=1 AngleXU=0 Radius=3
    g4: LineSegment StartX=143.955 StartY=20.303 StartZ=0 EndX=202.765 EndY=20.303 EndZ=0
    g5: LineSegment StartX=215.42 StartY=-53.0314 StartZ=0 EndX=192.176 EndY=-3.18451 EndZ=0
    g6: ArcOfCircle CenterX=184.801 CenterY=-67.3089 CenterZ=0 NormalX=0 NormalY=0 NormalZ=1 AngleXU=0 Radius=33.7833 StartAngle=5.88425 EndAngle=6.71952
    g7: ArcOfCircle CenterX=207.583 CenterY=4 CenterZ=0 NormalX=0 NormalY=0 NormalZ=1 AngleXU=0 Radius=17 StartAngle=1.85815 EndAngle=3.57792
  constraints (19):
    c: Coincident(g0,g-4)
    c: PointOnObject(g0,g-3)
    c: Horizontal(g0,g-7)
    c: Coincident(g1,g0)
    c: Coincident(g1,g-5)
    c: Diameter(g2) = 6
    c: Diameter(g3) = 6
    c: Coincident(g2,g-9)
    c: Coincident(g3,g-10)
    c: Coincident(g4,g0)
    c: Coincident(g5,g-6)
    c: Coincident(g6,g1)
    c: Coincident(g6,g5)
    c: Equal(g-5,g6)
    c: Coincident(g5,g-7)
    c: Coincident(g4,g-7)
    c: Tangent(g7,g-7)
    c: Coincident(g7,g4)
    c: Coincident(g7,g5)
FEATURE [Sketcher::SketchObject] Sketch097
  ArcFitTolerance = 1e-06
  AttachmentSupport = -> [Pad019]
  ExternalGeometry = -> [Binder]
  ExternalTypes = [0]
  FullyConstrained = true
  MakeInternals = false
  MapMode = 5
  Placement = pos=(0,2,0) rot=(0,0.707107,0.707107;3.14159rad)
  _ExternalGeoVersion = 0
  sketch-geometry (4):
    g0: LineSegment StartX=90 StartY=36.8 StartZ=0 EndX=108 EndY=36.8 EndZ=0
    g1: LineSegment StartX=108 StartY=36.8 StartZ=0 EndX=108 EndY=26.8 EndZ=0
    g2: LineSegment StartX=108 StartY=26.8 StartZ=0 EndX=90 EndY=26.8 EndZ=0
    g3: ArcOfCircle CenterX=94 CenterY=31.8 CenterZ=0 NormalX=0 NormalY=0 NormalZ=1 AngleXU=0 Radius=6.40312 StartAngle=2.24554 EndAngle=4.03765
  constraints (13):
    c: Horizontal(g0)
    c: Coincident(g1,g0)
    c: Vertical(g1)
    c: DistanceX(g0,g0) = 18
    c: DistanceY(g1,g1) = 10
    c: Coincident(g2,g1)
    c: Horizontal(g2)
    c: Equal(g2,g0)
    c: DistanceY(g0,g-3) = 2.4
    c: Coincident(g3,g0)
    c: Coincident(g3,g2)
    c: DistanceX(g2,g3) = 4
    c: DistanceX(g-3,g0) = 90
FEATURE [PartDesign::Chamfer] Chamfer015
  Angle = 45
  Base = -> Pad019 [Edge19,Edge22,Edge79]
  BaseFeature = -> Pad019
  ChamferType = 0
  FlipDirection = false
  Refine = true
  Size = 1.9
  Size2 = 1
  SupportTransform = false
  Suppressed = false
  UseAllEdges = false
FEATURE [PartDesign::Pocket] Pocket002
  BaseFeature = -> Chamfer015
  Direction = (0,1,-2e-16)
  Length = 1.2
  Length2 = 5
  Profile = -> Sketch093
  ReferenceAxis = -> Sketch093 [N_Axis]
  Refine = true
  SideType = 0
  Suppressed = false
  Type = 0
  Type2 = 0
FEATURE [PartDesign::Pad] Pad005
  BaseFeature = -> Pocket002
  Direction = (0,1,-2e-16)
  Length = 1.6
  Length2 = 10
  Profile = -> Sketch091
  ReferenceAxis = -> Sketch091 [N_Axis]
  Refine = true
  SideType = 0
  Suppressed = false
  Type = 0
  Type2 = 0
FEATURE [Sketcher::SketchObject] Sketch092  label="Sketch092 - scavi per viti anteriori"
  ArcFitTolerance = 1e-06
  AttachmentSupport = -> [Pad005]
  ExternalGeometry = -> [Binder]
  ExternalTypes = [0]
  FullyConstrained = true
  MakeInternals = false
  MapMode = 5
  Placement = pos=(0,3.6,0) rot=(0,0.707107,0.707107;3.14159rad)
  _ExternalGeoVersion = 0
  sketch-geometry (20):
    g0: ArcOfCircle CenterX=5.6 CenterY=7.6 CenterZ=0 NormalX=0 NormalY=0 NormalZ=1 AngleXU=0 Radius=3.5 StartAngle=0 EndAngle=1.5708
    g1: ArcOfCircle CenterX=5.6 CenterY=34.8 CenterZ=0 NormalX=0 NormalY=0 NormalZ=1 AngleXU=0 Radius=3.5 StartAngle=4.71239 EndAngle=6.28319
    g2: ArcOfCircle CenterX=78.51 CenterY=34.8 CenterZ=0 NormalX=0 NormalY=0 NormalZ=1 AngleXU=0 Radius=3.5 StartAngle=3.14159 EndAngle=4.71239
    g3: ArcOfCircle CenterX=78.51 CenterY=7.6 CenterZ=0 NormalX=0 NormalY=0 NormalZ=1 AngleXU=0 Radius=3.5 StartAngle=1.5708 EndAngle=3.14159
    g4: LineSegment StartX=0 StartY=3.2 StartZ=0 EndX=0 EndY=11.1 EndZ=0
    g5: LineSegment StartX=0 StartY=11.1 StartZ=0 EndX=5.6 EndY=11.1 EndZ=0
    g6: LineSegment StartX=0 StartY=3.2 StartZ=0 EndX=9.1 EndY=3.2 EndZ=0
    g7: LineSegment StartX=9.1 StartY=3.2 StartZ=0 EndX=9.1 EndY=7.6 EndZ=0
    g8: LineSegment StartX=0 StartY=39.2 StartZ=0 EndX=0 EndY=31.3 EndZ=0
    g9: LineSegment StartX=0 StartY=31.3 StartZ=0 EndX=5.6 EndY=31.3 EndZ=0
    g10: LineSegment StartX=0 StartY=39.2 StartZ=0 EndX=9.1 EndY=39.2 EndZ=0
    g11: LineSegment StartX=9.1 StartY=39.2 StartZ=0 EndX=9.1 EndY=34.8 EndZ=0
    g12: LineSegment StartX=82.8 StartY=39.2 StartZ=0 EndX=75.01 EndY=39.2 EndZ=0
    g13: LineSegment StartX=82.8 StartY=39.2 StartZ=0 EndX=82.8 EndY=31.3 EndZ=0
    g14: LineSegment StartX=82.8 StartY=31.3 StartZ=0 EndX=78.51 EndY=31.3 EndZ=0
    g15: LineSegment StartX=82.8 StartY=3.2 StartZ=0 EndX=75.01 EndY=3.2 EndZ=0
    g16: LineSegment StartX=75.01 StartY=3.2 StartZ=0 EndX=75.01 EndY=7.6 EndZ=0
    g17: LineSegment StartX=82.8 StartY=3.2 StartZ=0 EndX=82.8 EndY=11.1 EndZ=0
    g18: LineSegment StartX=82.8 StartY=11.1 StartZ=0 EndX=78.51 EndY=11.1 EndZ=0
    g19: LineSegment StartX=75.01 StartY=39.2 StartZ=0 EndX=75.01 EndY=34.8 EndZ=0
  constraints (48):
    c: Radius(g0) = 3.5
    c: Coincident(g0,g-10)
    c: Radius(g1) = 3.5
    c: Coincident(g1,g-9)
    c: Radius(g2) = 3.5
    c: Coincident(g2,g-8)
    c: Radius(g3) = 3.5
    c: Coincident(g3,g-7)
    c: Coincident(g4,g-5)
    c: PointOnObject(g4,g-4)
    c: Coincident(g5,g4)
    c: Horizontal(g5)
    c: Coincident(g6,g4)
    c: PointOnObject(g6,g-5)
    c: Coincident(g7,g6)
    c: Vertical(g7)
    c: Coincident(g8,g-4)
    c: PointOnObject(g8,g-4)
    c: Coincident(g9,g8)
    c: Horizontal(g9)
    c: Coincident(g10,g8)
    c: PointOnObject(g10,g-3)
    c: Coincident(g11,g10)
    c: Vertical(g11)
    c: PointOnObject(g12,g-3)
    c: PointOnObject(g12,g-3)
    c: Coincident(g13,g12)
    c: Vertical(g13)
    c: Coincident(g14,g13)
    c: Horizontal(g14)
    c: Coincident(g15,g-6)
    c: PointOnObject(g15,g-5)
    c: Coincident(g16,g15)
    c: Vertical(g16)
    c: Coincident(g17,g15)
    c: Coincident(g18,g17)
    c: Horizontal(g18)
    c: Tangent(g3,g18) = -1.5708
    c: Tangent(g16,g3) = 1.5708
    c: Coincident(g19,g12)
    c: Vertical(g19)
    c: Tangent(g2,g19) = -1.5708
    c: Tangent(g2,g14) = 1.5708
    c: Tangent(g0,g7) = -1.5708
    c: Tangent(g0,g5) = 1.5708
    c: Tangent(g9,g1) = -1.5708
    c: Tangent(g1,g11) = 1.5708
    c: Tangent(g17,g13)
FEATURE [PartDesign::Pocket] Pocket001
  BaseFeature = -> Pad005
  Direction = (0,-1,2e-16)
  Length = 1.6
  Length2 = 5
  Profile = -> Sketch092
  ReferenceAxis = -> Sketch092 [N_Axis]
  Refine = true
  SideType = 0
  Suppressed = false
  Type = 0
  Type2 = 0
FEATURE [PartDesign::Pad] Pad006
  BaseFeature = -> Pocket001
  Direction = (0,1,-2e-16)
  Length = 0.8
  Length2 = 10
  Profile = -> Sketch094
  ReferenceAxis = -> Sketch094 [N_Axis]
  Refine = true
  SideType = 0
  Suppressed = false
  Type = 0
  Type2 = 0
FEATURE [PartDesign::Pad] Pad007
  BaseFeature = -> Pad006
  Direction = (0,1,-2e-16)
  Length = 2
  Length2 = 10
  Profile = -> Sketch095
  ReferenceAxis = -> Sketch095 [N_Axis]
  Refine = true
  SideType = 0
  Suppressed = false
  Type = 0
  Type2 = 0
FEATURE [PartDesign::Pad] Pad008  label="Pad008 - forma impugnatura"
  BaseFeature = -> Pad007
  Direction = (0,1,-2e-16)
  Length = 1.6
  Length2 = 10
  Profile = -> Sketch096
  ReferenceAxis = -> Sketch096 [N_Axis]
  Refine = true
  SideType = 0
  Suppressed = false
  Type = 0
  Type2 = 0
FEATURE [PartDesign::Pad] Pad009
  BaseFeature = -> Pad008
  Direction = (0,1,-2e-16)
  Length = 1.6
  Length2 = 10
  Profile = -> Sketch097
  ReferenceAxis = -> Sketch097 [N_Axis]
  Refine = true
  SideType = 0
  Suppressed = false
  Type = 0
  Type2 = 0
FEATURE [Sketcher::SketchObject] Sketch098
  ArcFitTolerance = 1e-06
  AttachmentSupport = -> [Pad006]
  ExternalGeometry = -> [Binder]
  ExternalTypes = [0]
  FullyConstrained = true
  MakeInternals = false
  MapMode = 5
  Placement = pos=(0,2.8,-7e-16) rot=(0,0.707107,0.707107;3.14159rad)
  _ExternalGeoVersion = 0
  sketch-geometry (4):
    g0: LineSegment StartX=118 StartY=39.2 StartZ=0 EndX=129 EndY=39.2 EndZ=0
    g1: LineSegment StartX=120.599 StartY=31.2 StartZ=0 EndX=131.599 EndY=31.2 EndZ=0
    g2: LineSegment StartX=129 StartY=39.2 StartZ=0 EndX=131.599 EndY=31.2 EndZ=0
    g3: LineSegment StartX=118 StartY=39.2 StartZ=0 EndX=120.599 EndY=31.2 EndZ=0
  constraints (12):
    c: PointOnObject(g0,g-3)
    c: PointOnObject(g0,g-3)
    c: DistanceX(g0,g0) = 11
    c: Horizontal(g1)
    c: Equal(g1,g0)
    c: Coincident(g2,g0)
    c: Coincident(g3,g0)
    c: Parallel(g-4,g2)
    c: Coincident(g1,g2)
    c: Coincident(g1,g3)
    c: DistanceY(g1,g0) = 8
    c: DistanceX(g-3,g0) = 118
FEATURE [Sketcher::SketchObject] Sketch099
  ArcFitTolerance = 1e-06
  AttachmentSupport = -> [Pad008]
  ExternalGeometry = -> [Binder]
  ExternalTypes = [0]
  FullyConstrained = true
  MakeInternals = false
  MapMode = 5
  Placement = pos=(0,3.6,0) rot=(0,0.707107,0.707107;3.14159rad)
  _ExternalGeoVersion = 0
  sketch-geometry (13):
    g0: LineSegment StartX=192.176 StartY=-3.18451 StartZ=0 EndX=196.804 EndY=-13.1108 EndZ=0
    g1: LineSegment [constr] StartX=202.765 StartY=20.303 StartZ=0 EndX=181.223 EndY=20.303 EndZ=0
    g2: LineSegment [constr] StartX=181.223 StartY=20.303 StartZ=0 EndX=181.223 EndY=-3.18451 EndZ=0
    g3: ArcOfCircle CenterX=181.223 CenterY=-20.3764 CenterZ=0 NormalX=0 NormalY=0 NormalZ=1 AngleXU=0 Radius=17.1918 StartAngle=0.436332 EndAngle=1.57079
    g4: ArcOfEllipse CenterX=181.223 CenterY=8.55923 CenterZ=0 NormalX=0 NormalY=0 NormalZ=1 MajorRadius=23.4779 MinorRadius=11.7437 AngleXU=0 StartAngle=1.5708 EndAngle=4.71239
    g5: LineSegment [constr] StartX=204.701 StartY=8.55923 StartZ=0 EndX=157.745 EndY=8.55923 EndZ=0
    g6: LineSegment [constr] StartX=181.223 StartY=20.303 StartZ=0 EndX=181.223 EndY=-3.18451 EndZ=0
    g7: GeomPoint [constr] X=201.553 Y=8.55923 Z=0
    g8: GeomPoint [constr] X=160.894 Y=8.55923 Z=0
    g9: GeomPoint [constr] X=181.223 Y=-3.18451 Z=0
    g10: LineSegment StartX=181.223 StartY=20.303 StartZ=0 EndX=202.765 EndY=20.303 EndZ=0
    g11: ArcOfCircle CenterX=207.583 CenterY=4 CenterZ=0 NormalX=0 NormalY=0 NormalZ=1 AngleXU=0 Radius=17 StartAngle=1.85815 EndAngle=3.57792
    g12: LineSegment [constr] StartX=172.411 StartY=39.2 StartZ=0 EndX=192.176 EndY=-3.18451 EndZ=0
  constraints (27):
    c: Coincident(g1,g-7)
    c: Horizontal(g1)
    c: Coincident(g2,g1)
    c: Vertical(g2)
    c: Horizontal(g2,g0)
    c: Coincident(g3,g0)
    c: Coincident(g3,g2)
    c: InternalAlignment(g5-g8 -> g4) x4
    c: Horizontal(g5)
    c: PointOnObject(g4,g2)
    c: Coincident(g4,g1)
    c: DistanceX(g-3,g5) = 10.1
    c: Coincident(g4,g2)
    c: Tangent(g3,g-5)
    c: PointOnObject(g9,g4)
    c: PointOnObject(g9,g3)
    c: Tangent(g4,g3,g9) = 1.5708
    c: Coincident(g10,g1)
    c: Coincident(g10,g1)
    c: Equal(g11,g-4)
    c: Coincident(g11,g1)
    c: Coincident(g11,g0)
    c: PointOnObject(g12,g-6)
    c: PointOnObject(g1,g12)
    c: Tangent(g12,g-5) = -1.5708
    c: Tangent(g0,g-5) = -1.5708
    c: Horizontal(g9,g12)
FEATURE [Sketcher::SketchObject] Sketch106  label="Sketch106 - smusso impuniatura interno"
  ArcFitTolerance = 1e-06
  AttachmentSupport = -> [Pad008]
  ExternalGeometry = -> [Pad008]
  ExternalTypes = [0]
  FullyConstrained = true
  MakeInternals = false
  MapMode = 5
  Placement = pos=(0,-1.585e-13,-80.4316) rot=(1,0,0;3.14159rad)
  _ExternalGeoVersion = 0
  sketch-geometry (9):
    g0: LineSegment StartX=-176.685 StartY=-3.6 StartZ=0 EndX=-176.685 EndY=-1.417e-13 EndZ=0
    g1: LineSegment [constr] StartX=-176.685 StartY=-1.415e-13 StartZ=0 EndX=-176.685 EndY=-1.415e-13 EndZ=0
    g2: LineSegment [constr] StartX=-186.685 StartY=-3.6 StartZ=0 EndX=-186.685 EndY=-1.417e-13 EndZ=0
    g3: ArcOfEllipse CenterX=-186.685 CenterY=-1.415e-13 CenterZ=0 NormalX=0 NormalY=0 NormalZ=1 MajorRadius=10 MinorRadius=3.6 AngleXU=3.14159 StartAngle=1.5708 EndAngle=3.14159
    g4: LineSegment [constr] StartX=-196.685 StartY=-1.415e-13 StartZ=0 EndX=-176.685 EndY=-1.415e-13 EndZ=0
    g5: LineSegment [constr] StartX=-186.685 StartY=-3.6 StartZ=0 EndX=-186.685 EndY=3.6 EndZ=0
    g6: GeomPoint [constr] X=-196.015 Y=-1.415e-13 Z=0
    g7: GeomPoint [constr] X=-177.356 Y=-1.415e-13 Z=0
    g8: LineSegment StartX=-176.685 StartY=-3.6 StartZ=0 EndX=-186.685 EndY=-3.6 EndZ=0
  constraints (15):
    c: PointOnObject(g2,g-3)
    c: Coincident(g1,g-5)
    c: DistanceY(g1,g1) = 0
    c: Coincident(g0,g1)
    c: DistanceX(g2,g-5) = 10
    c: Vertical(g2)
    c: Horizontal(g2,g0)
    c: InternalAlignment(g4-g7 -> g3) x4
    c: Coincident(g3,g2)
    c: Horizontal(g4)
    c: Coincident(g3,g0)
    c: Tangent(g0,g-5) = 1.5708
    c: Coincident(g3,g2)
    c: Coincident(g8,g0)
    c: Coincident(g8,g2)
FEATURE [Sketcher::SketchObject] Sketch107  label="Sketch107 - smusso impugnatura esterno"
  ArcFitTolerance = 1e-06
  AttachmentSupport = -> [Pad008]
  ExternalGeometry = -> [Pad008]
  ExternalTypes = [0]
  FullyConstrained = true
  MakeInternals = false
  MapMode = 5
  Placement = pos=(0,-1.585e-13,-80.4316) rot=(1,0,0;3.14159rad)
  _ExternalGeoVersion = 0
  sketch-geometry (9):
    g0: LineSegment [constr] StartX=-215.932 StartY=-1.416e-13 StartZ=0 EndX=-215.932 EndY=-7.05e-14 EndZ=0
    g1: LineSegment StartX=-215.932 StartY=-3.6 StartZ=0 EndX=-215.932 EndY=-7.06e-14 EndZ=0
    g2: LineSegment StartX=-215.932 StartY=-3.6 StartZ=0 EndX=-205.932 EndY=-3.6 EndZ=0
    g3: LineSegment [constr] StartX=-205.932 StartY=-3.6 StartZ=0 EndX=-205.932 EndY=-7.06e-14 EndZ=0
    g4: ArcOfEllipse CenterX=-205.932 CenterY=-7.05e-14 CenterZ=0 NormalX=0 NormalY=0 NormalZ=1 MajorRadius=10 MinorRadius=3.6 AngleXU=-3.14159 StartAngle=-2.66e-14 EndAngle=1.5708
    g5: LineSegment [constr] StartX=-215.932 StartY=-1.416e-13 StartZ=0 EndX=-195.932 EndY=-1.416e-13 EndZ=0
    g6: LineSegment [constr] StartX=-205.932 StartY=-3.6 StartZ=0 EndX=-205.932 EndY=3.6 EndZ=0
    g7: GeomPoint [constr] X=-215.262 Y=-1.598e-13 Z=0
    g8: GeomPoint [constr] X=-196.602 Y=-1.551e-13 Z=0
  constraints (16):
    c: Coincident(g0,g-6)
    c: PointOnObject(g0,g-6)
    c: DistanceY(g0,g0) = 0
    c: Coincident(g1,g-6)
    c: Coincident(g1,g0)
    c: Tangent(g2,g-3)
    c: DistanceX(g2,g2) = 10
    c: Coincident(g3,g2)
    c: Vertical(g3)
    c: Horizontal(g3,g0)
    c: InternalAlignment(g5-g8 -> g4) x4
    c: Coincident(g4,g3)
    c: Horizontal(g5)
    c: Coincident(g4,g0)
    c: Coincident(g4,g2)
    c: PointOnObject(g2,g1)
FEATURE [Sketcher::SketchObject] Sketch108
  ArcFitTolerance = 1e-06
  AttachmentOffset = pos=(0,0,-1.6) rot=(0,0,1;0rad)
  AttachmentSupport = -> [Pad008]
  ExternalGeometry = -> [Binder]
  ExternalTypes = [0]
  FullyConstrained = true
  MakeInternals = false
  MapMode = 5
  Placement = pos=(0,2,4e-16) rot=(0,0.707107,0.707107;3.14159rad)
  _ExternalGeoVersion = 0
  sketch-geometry (14):
    g0: LineSegment StartX=192.176 StartY=-3.18451 StartZ=0 EndX=193.827 EndY=-6.72678 EndZ=0
    g1: LineSegment [constr] StartX=202.765 StartY=20.303 StartZ=0 EndX=181.223 EndY=20.303 EndZ=0
    g2: LineSegment [constr] StartX=181.223 StartY=20.303 StartZ=0 EndX=181.223 EndY=1.30297 EndZ=0
    g3: ArcOfCircle CenterX=181.223 CenterY=-12.6042 CenterZ=0 NormalX=0 NormalY=0 NormalZ=1 AngleXU=0 Radius=13.9072 StartAngle=0.436332 EndAngle=1.5708
    g4: ArcOfEllipse CenterX=181.223 CenterY=10.803 CenterZ=0 NormalX=0 NormalY=0 NormalZ=1 MajorRadius=14.4779 MinorRadius=9.5 AngleXU=0 StartAngle=1.5708 EndAngle=4.71239
    g5: LineSegment [constr] StartX=195.701 StartY=10.803 StartZ=0 EndX=166.745 EndY=10.803 EndZ=0
    g6: LineSegment [constr] StartX=181.223 StartY=20.303 StartZ=0 EndX=181.223 EndY=1.30297 EndZ=0
    g7: GeomPoint [constr] X=192.148 Y=10.803 Z=0
    g8: GeomPoint [constr] X=170.298 Y=10.803 Z=0
    g9: LineSegment StartX=181.223 StartY=20.303 StartZ=0 EndX=202.765 EndY=20.303 EndZ=0
    g10: ArcOfCircle CenterX=207.583 CenterY=4 CenterZ=0 NormalX=0 NormalY=0 NormalZ=1 AngleXU=0 Radius=17 StartAngle=1.85815 EndAngle=3.57792
    g11: LineSegment [constr] StartX=172.411 StartY=39.2 StartZ=0 EndX=192.176 EndY=-3.18451 EndZ=0
    g12: GeomPoint [constr] X=181.223 Y=1.30297 Z=0
    g13: GeomPoint [constr] X=181.223 Y=1.30297 Z=0
  constraints (28):
    c: Coincident(g1,g-7)
    c: Horizontal(g1)
    c: Coincident(g2,g1)
    c: Vertical(g2)
    c: Coincident(g3,g2)
    c: InternalAlignment(g5-g8 -> g4) x4
    c: Horizontal(g5)
    c: PointOnObject(g4,g2)
    c: Coincident(g4,g1)
    c: DistanceX(g-3,g5) = 19.1
    c: Coincident(g4,g2)
    c: Coincident(g9,g1)
    c: Coincident(g9,g1)
    c: Coincident(g10,g1)
    c: Coincident(g10,g0)
    c: PointOnObject(g11,g-6)
    c: PointOnObject(g1,g11)
    c: DistanceY(g2,g1) = 19
    c: Coincident(g10,g-4)
    c: PointOnObject(g12,g4)
    c: PointOnObject(g12,g3)
    c: Tangent(g11,g-5) = -1.5708
    c: Tangent(g0,g-5) = -1.5708
    c: Tangent(g3,g0) = 1.5708
    c: PointOnObject(g13,g4)
    c: PointOnObject(g13,g3)
    c: Tangent(g4,g3,g13) = 1.5708
    c: Horizontal(g11,g0)
FEATURE [Part::Part2DObjectPython] Clone2D  label="Sketch108 (2D)"  # Draft 2D object (typed FeaturePython)
  ForceCompound = false
  Fuse = false
  Objects = -> [Sketch108]
  Placement = pos=(0,2,4e-16) rot=(0,0.707107,0.707107;3.14159rad)
  Scale = (1,1,1)
FEATURE [Sketcher::SketchObject] Sketch109
  ArcFitTolerance = 1e-06
  AttachmentOffset = pos=(0,0,-3.5) rot=(0,0,1;0rad)
  AttachmentSupport = -> [Pad008]
  ExternalGeometry = -> [Binder]
  ExternalTypes = [0]
  FullyConstrained = true
  MakeInternals = false
  MapMode = 5
  Placement = pos=(0,0.1,8e-16) rot=(0,0.707107,0.707107;3.14159rad)
  _ExternalGeoVersion = 0
  sketch-geometry (1):
    g0: GeomPoint X=197.47 Y=8.55923 Z=0
  constraints (1):
    c: Symmetric(g-7,g-5,g0)
FEATURE [PartDesign::Chamfer] Chamfer005
  Angle = 45
  Base = -> Pad009 [Edge215,Edge212]
  BaseFeature = -> Pad009
  ChamferType = 1
  FlipDirection = false
  Refine = true
  Size = 1.5
  Size2 = 2.8
  SupportTransform = false
  Suppressed = false
  UseAllEdges = false
FEATURE [Sketcher::SketchObject] Sketch111
  ArcFitTolerance = 1e-06
  AttachmentSupport = -> [Pad009]
  ExternalGeometry = -> [Pad009]
  ExternalTypes = [0]
  FullyConstrained = true
  MakeInternals = false
  MapMode = 5
  Placement = pos=(0,3.6,-8e-16) rot=(0,0.707107,0.707107;3.14159rad)
  _ExternalGeoVersion = 0
  sketch-geometry (21):
    g0: LineSegment [constr] StartX=97 StartY=36.8 StartZ=0 EndX=97 EndY=26.8 EndZ=0
    g1: LineSegment StartX=97 StartY=28.6 StartZ=0 EndX=97 EndY=27.8 EndZ=0
    g2: LineSegment StartX=97 StartY=27.8 StartZ=0 EndX=108 EndY=27.8 EndZ=0
    g3: LineSegment StartX=108 StartY=27.8 StartZ=0 EndX=108 EndY=28.6 EndZ=0
    g4: LineSegment StartX=108 StartY=28.6 StartZ=0 EndX=97 EndY=28.6 EndZ=0
    g5: LineSegment StartX=97 StartY=35.8 StartZ=0 EndX=97 EndY=35 EndZ=0
    g6: LineSegment StartX=97 StartY=35 StartZ=0 EndX=108 EndY=35 EndZ=0
    g7: LineSegment StartX=108 StartY=35 StartZ=0 EndX=108 EndY=35.8 EndZ=0
    g8: LineSegment StartX=108 StartY=35.8 StartZ=0 EndX=97 EndY=35.8 EndZ=0
    g9: LineSegment StartX=97 StartY=30.4 StartZ=0 EndX=97 EndY=29.6 EndZ=0
    g10: LineSegment StartX=97 StartY=29.6 StartZ=0 EndX=108 EndY=29.6 EndZ=0
    g11: LineSegment StartX=108 StartY=29.6 StartZ=0 EndX=108 EndY=30.4 EndZ=0
    g12: LineSegment StartX=108 StartY=30.4 StartZ=0 EndX=97 EndY=30.4 EndZ=0
    g13: LineSegment StartX=97 StartY=34 StartZ=0 EndX=97 EndY=33.2 EndZ=0
    g14: LineSegment StartX=97 StartY=33.2 StartZ=0 EndX=108 EndY=33.2 EndZ=0
    g15: LineSegment StartX=108 StartY=33.2 StartZ=0 EndX=108 EndY=34 EndZ=0
    g16: LineSegment StartX=108 StartY=34 StartZ=0 EndX=97 EndY=34 EndZ=0
    g17: LineSegment StartX=97 StartY=32.2 StartZ=0 EndX=97 EndY=31.4 EndZ=0
    g18: LineSegment StartX=97 StartY=31.4 StartZ=0 EndX=108 EndY=31.4 EndZ=0
    g19: LineSegment StartX=108 StartY=31.4 StartZ=0 EndX=108 EndY=32.2 EndZ=0
    g20: LineSegment StartX=108 StartY=32.2 StartZ=0 EndX=97 EndY=32.2 EndZ=0
  constraints (54):
    c: Vertical(g0)
    c: PointOnObject(g0,g-3)
    c: PointOnObject(g0,g-4)
    c: DistanceX(g0,g-5) = 11
    c: Coincident(g1,g2)
    c: Coincident(g2,g3)
    c: Coincident(g3,g4)
    c: Coincident(g4,g1)
    c: Horizontal(g2)
    c: Horizontal(g4)
    c: Tangent(g1,g0)
    c: Tangent(g3,g-5)
    c: DistanceY(g2,g3) = 0.8
    c: Coincident(g5,g6)
    c: Coincident(g6,g7)
    c: Coincident(g7,g8)
    c: Coincident(g8,g5)
    c: Horizontal(g6)
    c: Horizontal(g8)
    c: DistanceY(g6,g7) = 0.8
    c: Coincident(g9,g10)
    c: Coincident(g10,g11)
    c: Coincident(g11,g12)
    c: Coincident(g12,g9)
    c: Horizontal(g10)
    c: Horizontal(g12)
    c: DistanceY(g10,g11) = 0.8
    c: Tangent(g5,g0)
    c: Tangent(g7,g-5)
    c: Tangent(g9,g0)
    c: Tangent(g11,g-5)
    c: Coincident(g13,g14)
    c: Coincident(g14,g15)
    c: Coincident(g15,g16)
    c: Coincident(g16,g13)
    c: Horizontal(g14)
    c: Horizontal(g16)
    c: DistanceY(g14,g15) = 0.8
    c: Tangent(g13,g0)
    c: Tangent(g15,g-5)
    c: Coincident(g17,g18)
    c: Coincident(g18,g19)
    c: Coincident(g19,g20)
    c: Coincident(g20,g17)
    c: Horizontal(g18)
    c: Horizontal(g20)
    c: DistanceY(g18,g19) = 0.8
    c: Tangent(g17,g0)
    c: Tangent(g19,g-5)
    c: DistanceY(g1,g9) = 1
    c: DistanceY(g9,g17) = 1
    c: DistanceY(g17,g13) = 1
    c: DistanceY(g13,g5) = 1
    c: DistanceY(g0,g1) = 1
FEATURE [PartDesign::Pocket] Pocket004
  BaseFeature = -> Chamfer005
  Direction = (0,-1,2e-16)
  Length = 1
  Length2 = 5
  Profile = -> Sketch111
  ReferenceAxis = -> Sketch111 [N_Axis]
  Refine = true
  SideType = 0
  Suppressed = false
  Type = 0
  Type2 = 0
FEATURE [PartDesign::Pad] Pad010
  BaseFeature = -> Pocket004
  Direction = (0,1,-2e-16)
  Length = 1.2
  Length2 = 10
  Profile = -> Sketch098
  ReferenceAxis = -> Sketch098 [N_Axis]
  Refine = true
  SideType = 0
  Suppressed = false
  Type = 0
  Type2 = 0
FEATURE [PartDesign::Chamfer] Chamfer006
  Angle = 45
  Base = -> Pad010 [Edge291]
  BaseFeature = -> Pad010
  ChamferType = 1
  FlipDirection = false
  Refine = true
  Size = 1
  Size2 = 6
  SupportTransform = false
  Suppressed = false
  UseAllEdges = false
FEATURE [Sketcher::SketchObject] Sketch110
  ArcFitTolerance = 1e-06
  AttachmentSupport = -> [Pad010]
  ExternalGeometry = -> [Sketch098]
  ExternalTypes = [0]
  FullyConstrained = true
  MakeInternals = false
  MapMode = 5
  Placement = pos=(0,4,-9e-16) rot=(0,0.707107,0.707107;3.14159rad)
  _ExternalGeoVersion = 0
  sketch-geometry (8):
    g0: LineSegment StartX=119.69 StartY=34 StartZ=0 EndX=130.69 EndY=34 EndZ=0
    g1: LineSegment StartX=119.95 StartY=33.2 StartZ=0 EndX=130.95 EndY=33.2 EndZ=0
    g2: LineSegment StartX=119.137 StartY=35.7 StartZ=0 EndX=130.137 EndY=35.7 EndZ=0
    g3: LineSegment StartX=118.877 StartY=36.5 StartZ=0 EndX=129.877 EndY=36.5 EndZ=0
    g4: LineSegment StartX=118.877 StartY=36.5 StartZ=0 EndX=119.137 EndY=35.7 EndZ=0
    g5: LineSegment StartX=129.877 StartY=36.5 StartZ=0 EndX=130.137 EndY=35.7 EndZ=0
    g6: LineSegment StartX=119.69 StartY=34 StartZ=0 EndX=119.95 EndY=33.2 EndZ=0
    g7: LineSegment StartX=130.69 StartY=34 StartZ=0 EndX=130.95 EndY=33.2 EndZ=0
  constraints (24):
    c: Horizontal(g0)
    c: Horizontal(g1)
    c: Horizontal(g2)
    c: Horizontal(g3)
    c: Equal(g1,g-5)
    c: Equal(g0,g-5)
    c: Equal(g2,g-5)
    c: Equal(g3,g-5)
    c: PointOnObject(g0,g-3)
    c: PointOnObject(g1,g-3)
    c: PointOnObject(g2,g-3)
    c: PointOnObject(g3,g-3)
    c: Coincident(g4,g3)
    c: Coincident(g4,g2)
    c: Coincident(g5,g3)
    c: Coincident(g5,g2)
    c: Coincident(g6,g0)
    c: Coincident(g6,g1)
    c: Coincident(g7,g0)
    c: Coincident(g7,g1)
    c: DistanceY(g1,g0) = 0.8
    c: DistanceY(g2,g3) = 0.8
    c: DistanceY(g-5,g1) = 2
    c: DistanceY(g-5,g2) = 4.5
FEATURE [PartDesign::Pocket] Pocket003
  BaseFeature = -> Chamfer006
  Direction = (0,-1,2e-16)
  Length = 1
  Length2 = 5
  Profile = -> Sketch110
  ReferenceAxis = -> Sketch110 [N_Axis]
  Refine = true
  SideType = 0
  Suppressed = false
  Type = 0
  Type2 = 0
FEATURE [PartDesign::SubtractivePipe] SubtractivePipe
  AuxiliaryCurvilinear = true
  AuxiliarySpineTangent = false
  BaseFeature = -> Pocket003
  Binormal = (0,0,0)
  Mode = 0
  Profile = -> Sketch106
  Refine = true
  Spine = -> Pad008 [Edge215]
  SpineTangent = false
  Suppressed = false
  Transformation = 0
  Transition = 0
FEATURE [PartDesign::SubtractivePipe] SubtractivePipe001
  AuxiliaryCurvilinear = true
  AuxiliarySpineTangent = false
  BaseFeature = -> SubtractivePipe
  Binormal = (0,0,0)
  Mode = 0
  Profile = -> Sketch107
  Refine = true
  Spine = -> Pad008 [Edge213,Edge216,Edge210]
  SpineTangent = false
  Suppressed = false
  Transformation = 0
  Transition = 0
FEATURE [PartDesign::SubtractiveLoft] SubtractiveLoft
  BaseFeature = -> SubtractivePipe001
  Closed = false
  Profile = -> Sketch099
  Refine = true
  Ruled = false
  Sections = -> [Sketch108]
  Suppressed = false
FEATURE [PartDesign::SubtractiveLoft] SubtractiveLoft001
  BaseFeature = -> SubtractiveLoft
  Closed = false
  Profile = -> Clone2D
  Refine = true
  Ruled = false
  Sections = -> [Sketch109]
  Suppressed = false
FEATURE [Sketcher::SketchObject] Sketch112
  ArcFitTolerance = 1e-06
  AttachmentSupport = -> [Pad008]
  ExternalGeometry = -> [Binder]
  ExternalTypes = [0]
  FullyConstrained = true
  MakeInternals = false
  MapMode = 5
  Placement = pos=(0,3.6,0) rot=(0,0.707107,0.707107;3.14159rad)
  _ExternalGeoVersion = 0
  sketch-geometry (4):
    g0: LineSegment [constr] StartX=167.782 StartY=-53.0314 StartZ=0 EndX=215.42 EndY=-53.0314 EndZ=0
    g1: GeomPoint [constr] X=191.282 Y=-53.0314 Z=0
    g2: Circle CenterX=191.282 CenterY=-53.0314 CenterZ=0 NormalX=0 NormalY=0 NormalZ=1 AngleXU=0 Radius=11.5
    g3: Circle CenterX=191.282 CenterY=-53.0314 CenterZ=0 NormalX=0 NormalY=0 NormalZ=1 AngleXU=0 Radius=10.7
  constraints (9):
    c: Horizontal(g0)
    c: PointOnObject(g0,g-3)
    c: Diameter(g2) = 23
    c: Coincident(g2,g1)
    c: Diameter(g3) = 21.4
    c: Coincident(g3,g1)
    c: DistanceX(g0,g1) = 23.5
    c: PointOnObject(g1,g0)
    c: Coincident(g0,g-4)
FEATURE [PartDesign::Chamfer] Chamfer016
  Angle = 45
  Base = -> SubtractiveLoft001 [Edge118,Edge117,Edge119,Edge120,Edge109]
  BaseFeature = -> SubtractiveLoft001
  ChamferType = 0
  FlipDirection = false
  Refine = true
  Size = 1.5
  Size2 = 1
  SupportTransform = false
  Suppressed = false
  UseAllEdges = false
FEATURE [PartDesign::Chamfer] Chamfer017
  Angle = 45
  Base = -> Chamfer016 [Edge15]
  BaseFeature = -> Chamfer016
  ChamferType = 0
  FlipDirection = false
  Refine = true
  Size = 1.6
  Size2 = 1
  SupportTransform = false
  Suppressed = false
  UseAllEdges = false
FEATURE [PartDesign::Chamfer] Chamfer018
  Angle = 45
  Base = -> Chamfer017 [Edge10]
  BaseFeature = -> Chamfer017
  ChamferType = 0
  FlipDirection = false
  Refine = true
  Size = 3.5
  Size2 = 1
  SupportTransform = false
  Suppressed = false
  UseAllEdges = false
FEATURE [PartDesign::Chamfer] Chamfer019
  Angle = 45
  Base = -> Chamfer018 [Edge94]
  BaseFeature = -> Chamfer018
  ChamferType = 0
  FlipDirection = false
  Refine = true
  Size = 1.9
  Size2 = 1
  SupportTransform = false
  Suppressed = false
  UseAllEdges = false
FEATURE [PartDesign::Fillet] Fillet009
  Base = -> Chamfer019 [Edge83]
  BaseFeature = -> Chamfer019
  Radius = 1.1
  Refine = true
  SupportTransform = false
  Suppressed = false
  UseAllEdges = false
FEATURE [PartDesign::Fillet] Fillet010
  Base = -> Fillet009 [Edge77]
  BaseFeature = -> Fillet009
  Radius = 1.9
  Refine = true
  SupportTransform = false
  Suppressed = false
  UseAllEdges = false
FEATURE [PartDesign::Pocket] Pocket005
  BaseFeature = -> Fillet010
  Direction = (0,-1,2e-16)
  Length = 0.8
  Length2 = 5
  Profile = -> Sketch112
  ReferenceAxis = -> Sketch112 [N_Axis]
  Refine = true
  SideType = 0
  Suppressed = false
  Type = 0
  Type2 = 0
FEATURE [Part::Part2DObjectPython] ShapeString001  # Draft 2D object (typed FeaturePython)
  FontFile = <path>
  Fuse = false
  Justification = 6
  JustificationReference = 0
  KeepLeftMargin = false
  MakeFace = true
  ObliqueAngle = 0
  Placement = pos=(-183.5,3.6,-57.5) rot=(0,0.707107,0.707107;3.14159rad)
  ScaleToSize = true
  Size = 10
  String = AS
  Tracking = 0
FEATURE [PartDesign::Pocket] Pocket013
  BaseFeature = -> Pocket005
  Direction = (-1e-16,-1,2e-16)
  Length = 1
  Length2 = 5
  Profile = -> ShapeString001
  ReferenceAxis = -> ShapeString001 [N_Axis]
  Refine = true
  SideType = 0
  Suppressed = false
  Type = 0
  Type2 = 0
FEATURE [PartDesign::Pad] Pad020
  Direction = (0,-1,2e-16)
  Length = 25.2
  Length2 = 10
  Placement = pos=(0,0,0) rot=(1,0,0;1.5708rad)
  Profile = -> Sketch021
  ReferenceAxis = -> Sketch021 [N_Axis]
  Refine = true
  SideType = 2
  Suppressed = false
  Type = 0
  Type2 = 0
FEATURE [PartDesign::Body] Body001  label="perno fermo rumble e driver solenoide"
  AllowCompound = false
  Group = -> [Sketch021,Pad020]
  Origin = -> Origin001
  Tip = -> Pad020
FEATURE [PartDesign::Pad] Pad021
  Direction = (0,-1,2e-16)
  Length = 16.8
  Length2 = 10
  Placement = pos=(0,0,0) rot=(1,0,0;1.5708rad)
  Profile = -> Sketch061
  ReferenceAxis = -> Sketch061 [N_Axis]
  Refine = true
  SideType = 2
  Suppressed = false
  Type = 0
  Type2 = 0
FEATURE [PartDesign::Pocket] Pocket014
  BaseFeature = -> Pad021
  Direction = (0,1,-2e-16)
  Length = 12.8
  Length2 = 5
  Placement = pos=(0,0,0) rot=(1,0,0;1.5708rad)
  Profile = -> Sketch062
  ReferenceAxis = -> Sketch062 [N_Axis]
  Refine = true
  SideType = 2
  Suppressed = false
  Type = 0
  Type2 = 0
FEATURE [PartDesign::Pad] Pad022
  BaseFeature = -> Pocket014
  Direction = (0,-1,2e-16)
  Length = 7.6
  Length2 = 10
  Placement = pos=(0,0,0) rot=(1,0,0;1.5708rad)
  Profile = -> Sketch063
  ReferenceAxis = -> Sketch063 [N_Axis]
  Refine = true
  SideType = 2
  Suppressed = false
  Type = 0
  Type2 = 0
FEATURE [PartDesign::Body] Body003  label="blocco switch"
  AllowCompound = false
  Group = -> [Sketch061,Sketch062,Sketch063,Pad021,Pocket014,Pad022]
  Origin = -> Origin003
  Tip = -> Pad022
FEATURE [PartDesign::Pad] Pad024
  Direction = (0,-1,2e-16)
  Length = 17
  Length2 = 10
  Placement = pos=(0,0,0) rot=(1,0,0;1.5708rad)
  Profile = -> Sketch045
  ReferenceAxis = -> Sketch045 [N_Axis]
  Refine = true
  SideType = 2
  Suppressed = false
  Type = 0
  Type2 = 0
FEATURE [PartDesign::Pocket] Pocket015
  BaseFeature = -> Pad024
  Direction = (-1,0,0)
  Length = 8
  Length2 = 5
  Placement = pos=(0,0,0) rot=(1,0,0;1.5708rad)
  Profile = -> Sketch047
  ReferenceAxis = -> Sketch047 [N_Axis]
  Refine = true
  Reversed = true
  SideType = 0
  Suppressed = false
  Type = 0
  Type2 = 0
FEATURE [PartDesign::Pocket] Pocket016
  BaseFeature = -> Pocket015
  Direction = (-1,0,0)
  Length = 1
  Length2 = 5
  Placement = pos=(0,0,0) rot=(1,0,0;1.5708rad)
  Profile = -> Sketch046
  ReferenceAxis = -> Sketch046 [N_Axis]
  Refine = true
  Reversed = true
  SideType = 0
  Suppressed = false
  Type = 0
  Type2 = 0
FEATURE [PartDesign::Pocket] Pocket017
  BaseFeature = -> Pocket016
  Direction = (0,1,-2e-16)
  Length = 17
  Length2 = 5
  Placement = pos=(0,0,0) rot=(1,0,0;1.5708rad)
  Profile = -> Sketch048
  ReferenceAxis = -> Sketch048 [N_Axis]
  Refine = true
  SideType = 2
  Suppressed = false
  Type = 0
  Type2 = 0
FEATURE [PartDesign::Pad] Pad025
  BaseFeature = -> Pocket017
  Direction = (0,-1,2e-16)
  Length = 17
  Length2 = 10
  Placement = pos=(0,0,0) rot=(1,0,0;1.5708rad)
  Profile = -> Sketch049
  ReferenceAxis = -> Sketch049 [N_Axis]
  Refine = true
  SideType = 2
  Suppressed = false
  Type = 0
  Type2 = 0
FEATURE [PartDesign::Pad] Pad026
  BaseFeature = -> Pad025
  Direction = (0,-1,2e-16)
  Length = 17
  Length2 = 10
  Placement = pos=(0,0,0) rot=(1,0,0;1.5708rad)
  Profile = -> Sketch066
  ReferenceAxis = -> Sketch066 [N_Axis]
  Refine = true
  SideType = 2
  Suppressed = false
  Type = 0
  Type2 = 0
FEATURE [PartDesign::Pad] Pad027
  BaseFeature = -> Pad026
  Direction = (0,-1,2e-16)
  Length = 5
  Length2 = 10
  Placement = pos=(0,0,0) rot=(1,0,0;1.5708rad)
  Profile = -> Sketch064
  ReferenceAxis = -> Sketch064 [N_Axis]
  Refine = true
  SideType = 2
  Suppressed = false
  Type = 0
  Type2 = 0
FEATURE [PartDesign::Pad] Pad028
  BaseFeature = -> Pad027
  Direction = (1,0,0)
  Length = 1
  Length2 = 10
  Placement = pos=(0,0,0) rot=(1,0,0;1.5708rad)
  Profile = -> Sketch068
  ReferenceAxis = -> Sketch068 [N_Axis]
  Refine = true
  Reversed = true
  SideType = 0
  Suppressed = false
  Type = 0
  Type2 = 0
FEATURE [PartDesign::Chamfer] Chamfer020
  Angle = 45
  Base = -> Pad028 [Edge73,Edge75,Edge78,Edge77]
  BaseFeature = -> Pad028
  ChamferType = 0
  FlipDirection = false
  Placement = pos=(0,0,0) rot=(1,0,0;1.5708rad)
  Refine = true
  Size = 0.5
  Size2 = 1
  SupportTransform = false
  Suppressed = false
  UseAllEdges = false
FEATURE [PartDesign::Body] Body002  label="supporto per neopixel"
  AllowCompound = false
  Group = -> [Sketch045,Sketch047,Sketch046,Sketch048,Sketch049,Sketch066,Sketch064,Sketch068,Pad024,Pocket015,Pocket016,Pocket017,Pad025,Pad026,Pad027,Pad028,Chamfer020]
  Origin = -> Origin002
  Tip = -> Chamfer020
FEATURE [Sketcher::SketchObject] Sketch134  label="perno fermo rumble002"
  ArcFitTolerance = 1e-06
  AttachmentSupport = -> [XZ_Plane008]
  ExternalTypes = [0]
  FullyConstrained = true
  MakeInternals = false
  MapMode = 5
  Placement = pos=(0,0,0) rot=(1,0,0;1.5708rad)
  _ExternalGeoVersion = 0
  sketch-geometry (16):
    g0: LineSegment StartX=0 StartY=0.45 StartZ=0 EndX=0 EndY=1.55 EndZ=0
    g1: LineSegment StartX=0.45 StartY=2 StartZ=0 EndX=1.55 EndY=2 EndZ=0
    g2: LineSegment StartX=2 StartY=1.55 StartZ=0 EndX=2 EndY=0.45 EndZ=0
    g3: LineSegment StartX=1.55 StartY=0 StartZ=0 EndX=0.45 EndY=0 EndZ=0
    g4: ArcOfCircle [constr] CenterX=0.45 CenterY=1.55 CenterZ=0 NormalX=0 NormalY=0 NormalZ=1 AngleXU=0 Radius=0.45 StartAngle=1.5708 EndAngle=3.14159
    g5: GeomPoint [constr] X=0 Y=2 Z=0
    g6: LineSegment StartX=0.45 StartY=2 StartZ=0 EndX=0 EndY=1.55 EndZ=0
    g7: ArcOfCircle [constr] CenterX=1.55 CenterY=1.55 CenterZ=0 NormalX=0 NormalY=0 NormalZ=1 AngleXU=0 Radius=0.45 StartAngle=0 EndAngle=1.5708
    g8: GeomPoint [constr] X=2 Y=2 Z=0
    g9: LineSegment StartX=2 StartY=1.55 StartZ=0 EndX=1.55 EndY=2 EndZ=0
    g10: ArcOfCircle [constr] CenterX=1.55 CenterY=0.45 CenterZ=0 NormalX=0 NormalY=0 NormalZ=1 AngleXU=0 Radius=0.45 StartAngle=4.71239 EndAngle=6.28319
    g11: GeomPoint [constr] X=2 Y=0 Z=0
    g12: LineSegment StartX=1.55 StartY=0 StartZ=0 EndX=2 EndY=0.45 EndZ=0
    g13: ArcOfCircle [constr] CenterX=0.45 CenterY=0.45 CenterZ=0 NormalX=0 NormalY=0 NormalZ=1 AngleXU=0 Radius=0.45 StartAngle=3.14159 EndAngle=4.71239
    g14: GeomPoint [constr] X=0 Y=0 Z=0
    g15: LineSegment StartX=0 StartY=0.45 StartZ=0 EndX=0.45 EndY=0 EndZ=0
  constraints (35):
    c: Coincident(g14,g-1)
    c: PointOnObject(g5,g-2)
    c: Horizontal(g1)
    c: Vertical(g2)
    c: Horizontal(g3)
    c: DistanceX(g5,g8) = 2
    c: DistanceY(g11,g8) = 2
    c: PointOnObject(g5,g0)
    c: PointOnObject(g5,g1)
    c: Tangent(g0,g4) = 1.5708
    c: Tangent(g1,g4) = 1.5708
    c: Coincident(g6,g0)
    c: Coincident(g6,g1)
    c: PointOnObject(g8,g2)
    c: PointOnObject(g8,g1)
    c: Tangent(g2,g7) = 1.5708
    c: Tangent(g1,g7) = 1.5708
    c: Coincident(g9,g2)
    c: Coincident(g9,g1)
    c: PointOnObject(g11,g2)
    c: PointOnObject(g11,g3)
    c: Tangent(g2,g10) = 1.5708
    c: Tangent(g3,g10) = 1.5708
    c: Coincident(g12,g2)
    c: Coincident(g12,g3)
    c: PointOnObject(g14,g0)
    c: PointOnObject(g14,g3)
    c: Tangent(g0,g13) = 1.5708
    c: Tangent(g3,g13) = 1.5708
    c: Coincident(g15,g0)
    c: Coincident(g15,g3)
    c: Equal(g6,g9)
    c: Equal(g9,g12)
    c: Equal(g12,g15)
    c: DistanceX(g14,g3) = 0.45
FEATURE [PartDesign::Pad] Pad029
  Direction = (0,-1,2e-16)
  Length = 17
  Length2 = 10
  Placement = pos=(0,0,0) rot=(1,0,0;1.5708rad)
  Profile = -> Sketch134
  ReferenceAxis = -> Sketch134 [N_Axis]
  Refine = true
  SideType = 2
  Suppressed = false
  Type = 0
  Type2 = 0
FEATURE [PartDesign::Body] Body008  label="perno fermo neopixel"
  AllowCompound = false
  Group = -> [Sketch134,Pad029]
  Origin = -> Origin008
  Tip = -> Pad029
FEATURE [Sketcher::SketchObject] Sketch135  label="perno fermo rumble003"
  ArcFitTolerance = 1e-06
  AttachmentSupport = -> [XZ_Plane009]
  ExternalTypes = [0]
  FullyConstrained = true
  MakeInternals = false
  MapMode = 5
  Placement = pos=(0,0,0) rot=(1,0,0;1.5708rad)
  _ExternalGeoVersion = 0
  sketch-geometry (16):
    g0: LineSegment StartX=1.378e-13 StartY=0.8 StartZ=0 EndX=-3.04e-14 EndY=3.1 EndZ=0
    g1: LineSegment StartX=0.8 StartY=3.9 StartZ=0 EndX=3.1 EndY=3.9 EndZ=0
    g2: LineSegment StartX=3.9 StartY=3.1 StartZ=0 EndX=3.9 EndY=0.8 EndZ=0
    g3: LineSegment StartX=3.1 StartY=4.515e-13 StartZ=0 EndX=0.8 EndY=4.515e-13 EndZ=0
    g4: ArcOfCircle [constr] CenterX=0.8 CenterY=3.1 CenterZ=0 NormalX=0 NormalY=0 NormalZ=1 AngleXU=0 Radius=0.8 StartAngle=1.5708 EndAngle=3.14159
    g5: GeomPoint [constr] X=0 Y=3.9 Z=0
    g6: LineSegment StartX=0.8 StartY=3.9 StartZ=0 EndX=-3.04e-14 EndY=3.1 EndZ=0
    g7: ArcOfCircle [constr] CenterX=3.1 CenterY=3.1 CenterZ=0 NormalX=0 NormalY=0 NormalZ=1 AngleXU=0 Radius=0.8 StartAngle=-2.4e-14 EndAngle=1.5708
    g8: GeomPoint [constr] X=3.9 Y=3.9 Z=0
    g9: LineSegment StartX=3.9 StartY=3.1 StartZ=0 EndX=3.1 EndY=3.9 EndZ=0
    g10: ArcOfCircle [constr] CenterX=3.1 CenterY=0.8 CenterZ=0 NormalX=0 NormalY=0 NormalZ=1 AngleXU=0 Radius=0.8 StartAngle=4.71239 EndAngle=6.28319
    g11: GeomPoint [constr] X=3.9 Y=0 Z=0
    g12: LineSegment StartX=3.1 StartY=4.515e-13 StartZ=0 EndX=3.9 EndY=0.8 EndZ=0
    g13: ArcOfCircle [constr] CenterX=0.8 CenterY=0.8 CenterZ=0 NormalX=0 NormalY=0 NormalZ=1 AngleXU=0 Radius=0.8 StartAngle=3.14159 EndAngle=4.71239
    g14: GeomPoint [constr] X=0 Y=0 Z=0
    g15: LineSegment StartX=1.378e-13 StartY=0.8 StartZ=0 EndX=0.8 EndY=4.515e-13 EndZ=0
  constraints (35):
    c: Coincident(g14,g-1)
    c: PointOnObject(g5,g-2)
    c: Horizontal(g1)
    c: Vertical(g2)
    c: Horizontal(g3)
    c: DistanceX(g5,g8) = 3.9
    c: DistanceY(g11,g8) = 3.9
    c: PointOnObject(g5,g0)
    c: PointOnObject(g5,g1)
    c: Tangent(g0,g4) = 1.5708
    c: Tangent(g1,g4) = 1.5708
    c: Coincident(g6,g0)
    c: Coincident(g6,g1)
    c: PointOnObject(g8,g2)
    c: PointOnObject(g8,g1)
    c: Tangent(g2,g7) = 1.5708
    c: Tangent(g1,g7) = 1.5708
    c: Coincident(g9,g2)
    c: Coincident(g9,g1)
    c: PointOnObject(g11,g2)
    c: PointOnObject(g11,g3)
    c: Tangent(g2,g10) = 1.5708
    c: Tangent(g3,g10) = 1.5708
    c: Coincident(g12,g2)
    c: Coincident(g12,g3)
    c: PointOnObject(g14,g0)
    c: PointOnObject(g14,g3)
    c: Tangent(g0,g13) = 1.5708
    c: Tangent(g3,g13) = 1.5708
    c: Coincident(g15,g0)
    c: Coincident(g15,g3)
    c: Equal(g6,g9)
    c: Equal(g9,g12)
    c: Equal(g12,g15)
    c: DistanceX(g14,g3) = 0.8
FEATURE [PartDesign::Pad] Pad030
  Direction = (0,-1,2e-16)
  Length = 25.2
  Length2 = 10
  Placement = pos=(0,0,0) rot=(1,0,0;1.5708rad)
  Profile = -> Sketch135
  ReferenceAxis = -> Sketch135 [N_Axis]
  Refine = true
  SideType = 2
  Suppressed = false
  Type = 0
  Type2 = 0
FEATURE [PartDesign::Body] Body009  label="perno fermo switch - caricabatterie - grilletto"
  AllowCompound = false
  Group = -> [Sketch135,Pad030]
  Origin = -> Origin009
  Tip = -> Pad030
FEATURE [Sketcher::SketchObject] Sketch136  label="scavo_rele"
  ArcFitTolerance = 1e-06
  AttachmentSupport = -> [XZ_Plane]
  ExternalGeometry = -> [Sketch]
  ExternalTypes = [0]
  FullyConstrained = true
  MakeInternals = false
  MapMode = 5
  Placement = pos=(0,0,0) rot=(1,0,0;1.5708rad)
  _ExternalGeoVersion = 0
  sketch-geometry (7):
    g0: LineSegment [constr] StartX=-172.456 StartY=-60.9321 StartZ=0 EndX=-176.597 EndY=-73.6763 EndZ=0
    g1: LineSegment [constr] StartX=-172.456 StartY=-60.9321 StartZ=0 EndX=-170.364 EndY=-61.612 EndZ=0
    g2: LineSegment [constr] StartX=-172.456 StartY=-60.9321 StartZ=0 EndX=-176.07 EndY=-59.7579 EndZ=0
    g3: LineSegment StartX=-176.07 StartY=-59.7579 StartZ=0 EndX=-170.364 EndY=-61.612 EndZ=0
    g4: LineSegment StartX=-176.07 StartY=-59.7579 StartZ=0 EndX=-180.211 EndY=-72.502 EndZ=0
    g5: LineSegment StartX=-170.364 StartY=-61.612 StartZ=0 EndX=-174.505 EndY=-74.3561 EndZ=0
    g6: LineSegment StartX=-180.211 StartY=-72.502 StartZ=0 EndX=-174.505 EndY=-74.3561 EndZ=0
  constraints (19):
    c: Tangent(g0,g-3)
    c: Distance(g0,g-3) = 87.2
    c: Distance(g0,g0) = 13.4
    c: Coincident(g1,g0)
    c: Coincident(g2,g0)
    c: Distance(g2) = 3.8
    c: Distance(g1) = 2.2
    c: Perpendicular(g0,g1)
    c: Perpendicular(g0,g2)
    c: Coincident(g3,g2)
    c: Coincident(g3,g1)
    c: Equal(g4,g0)
    c: Equal(g5,g0)
    c: Parallel(g4,g0)
    c: Parallel(g5,g0)
    c: Coincident(g4,g2)
    c: Coincident(g5,g1)
    c: Coincident(g6,g4)
    c: Coincident(g6,g5)
FEATURE [Part::Extrusion] Extrude076  label="Extrude076 - scavo_rele"
  Base = -> Sketch136
  Dir = (0,-1,2e-16)
  DirMode = 2
  FaceMakerClass = Part::FaceMakerBullseye
  FaceMakerMode = 3
  InnerWireTaper = 1
  LengthFwd = 18.2
  LengthRev = 0
  Solid = true
  Symmetric = true
FEATURE [Sketcher::SketchObject] Sketch137  label="scavo_nuovo_driver"
  ArcFitTolerance = 1e-06
  AttachmentSupport = -> [XZ_Plane]
  ExternalGeometry = -> [Sketch]
  ExternalTypes = [0]
  FullyConstrained = true
  MakeInternals = false
  MapMode = 5
  Placement = pos=(0,0,0) rot=(1,0,0;1.5708rad)
  _ExternalGeoVersion = 0
  sketch-geometry (7):
    g0: LineSegment [constr] StartX=-160.034 StartY=-22.6997 StartZ=0 EndX=-164.854 EndY=-37.5361 EndZ=0
    g1: LineSegment [constr] StartX=-160.034 StartY=-22.6997 StartZ=0 EndX=-156.99 EndY=-23.6885 EndZ=0
    g2: LineSegment [constr] StartX=-160.034 StartY=-22.6997 StartZ=0 EndX=-163.648 EndY=-21.5254 EndZ=0
    g3: LineSegment StartX=-163.648 StartY=-21.5254 StartZ=0 EndX=-156.99 EndY=-23.6885 EndZ=0
    g4: LineSegment StartX=-163.648 StartY=-21.5254 StartZ=0 EndX=-168.468 EndY=-36.3619 EndZ=0
    g5: LineSegment StartX=-156.99 StartY=-23.6885 StartZ=0 EndX=-161.811 EndY=-38.525 EndZ=0
    g6: LineSegment StartX=-168.468 StartY=-36.3619 StartZ=0 EndX=-161.811 EndY=-38.525 EndZ=0
  constraints (19):
    c: Distance(g0,g-3) = 47
    c: Distance(g0) = 15.6
    c: Tangent(g0,g-3)
    c: Coincident(g1,g0)
    c: Coincident(g2,g0)
    c: Distance(g1) = 3.2
    c: Distance(g2) = 3.8
    c: Perpendicular(g0,g1)
    c: Perpendicular(g0,g2)
    c: Coincident(g3,g2)
    c: Coincident(g3,g1)
    c: Equal(g4,g0)
    c: Equal(g5,g0)
    c: Parallel(g4,g0)
    c: Parallel(g5,g0)
    c: Coincident(g4,g2)
    c: Coincident(g5,g1)
    c: Coincident(g6,g4)
    c: Coincident(g6,g5)
FEATURE [Part::Extrusion] Extrude077  label="Extrude077 - scavo_nuovo_driver"
  Base = -> Sketch137
  Dir = (0,-1,2e-16)
  DirMode = 2
  FaceMakerClass = Part::FaceMakerBullseye
  FaceMakerMode = 3
  InnerWireTaper = 1
  LengthFwd = 20.8
  LengthRev = 0
  Solid = true
  Symmetric = true
FEATURE [Sketcher::SketchObject] Sketch138  label="scavo_nuovo_driver_alto"
  ArcFitTolerance = 1e-06
  AttachmentSupport = -> [XZ_Plane]
  ExternalGeometry = -> [Sketch]
  ExternalTypes = [0]
  FullyConstrained = true
  MakeInternals = false
  MapMode = 5
  Placement = pos=(0,0,0) rot=(1,0,0;1.5708rad)
  _ExternalGeoVersion = 0
  sketch-geometry (7):
    g0: LineSegment [constr] StartX=-188.917 StartY=18.1185 StartZ=0 EndX=-187.75 EndY=4.97025 EndZ=0
    g1: LineSegment StartX=-187.75 StartY=4.97025 StartZ=0 EndX=-189.742 EndY=4.79337 EndZ=0
    g2: LineSegment StartX=-187.75 StartY=4.97025 StartZ=0 EndX=-182.769 EndY=5.41245 EndZ=0
    g3: LineSegment StartX=-190.909 StartY=17.9416 StartZ=0 EndX=-189.742 EndY=4.79337 EndZ=0
    g4: LineSegment StartX=-183.937 StartY=18.5607 StartZ=0 EndX=-182.769 EndY=5.41245 EndZ=0
    g5: LineSegment StartX=-190.909 StartY=17.9416 StartZ=0 EndX=-188.917 EndY=18.1185 EndZ=0
    g6: LineSegment StartX=-188.917 StartY=18.1185 StartZ=0 EndX=-183.937 EndY=18.5607 EndZ=0
  constraints (20):
    c: Distance(g0) = 13.2
    c: DistanceY(g-3,g0) = 9
    c: PointOnObject(g0,g-4)
    c: PointOnObject(g0,g-4)
    c: Coincident(g1,g0)
    c: Coincident(g2,g0)
    c: Distance(g1) = 2
    c: Distance(g2) = 5
    c: Perpendicular(g0,g1)
    c: Perpendicular(g0,g2)
    c: Equal(g3,g0)
    c: Parallel(g3,g0)
    c: Coincident(g3,g1)
    c: Equal(g4,g0)
    c: Parallel(g4,g0)
    c: Coincident(g4,g2)
    c: Coincident(g5,g3)
    c: Coincident(g5,g0)
    c: Coincident(g6,g0)
    c: Coincident(g6,g4)
FEATURE [Part::Extrusion] Extrude078  label="Extrude078 - scavo_nuovo_driver_alto"
  Base = -> Sketch138
  Dir = (0,-1,2e-16)
  DirMode = 2
  FaceMakerClass = Part::FaceMakerBullseye
  FaceMakerMode = 3
  InnerWireTaper = 1
  LengthFwd = 17.2
  LengthRev = 0
  Solid = true
  Symmetric = true
FEATURE [Sketcher::SketchObject] Sketch139  label="fermi_nuovo_driver_alto"
  ArcFitTolerance = 1e-06
  AttachmentSupport = -> [XZ_Plane]
  ExternalGeometry = -> [Sketch138,Sketch]
  ExternalTypes = [0]
  FullyConstrained = true
  MakeInternals = false
  MapMode = 5
  Placement = pos=(0,0,0) rot=(1,0,0;1.5708rad)
  _ExternalGeoVersion = 0
  sketch-geometry (17):
    g0: LineSegment [constr] StartX=-188.41 StartY=16.8018 StartZ=0 EndX=-187.948 EndY=14.1416 EndZ=0
    g1: LineSegment [constr] StartX=-187.948 StartY=14.1416 StartZ=0 EndX=-187.486 EndY=11.4815 EndZ=0
    g2: LineSegment StartX=-187.948 StartY=14.1416 StartZ=0 EndX=-187.76 EndY=13.0579 EndZ=0
    g3: LineSegment StartX=-187.948 StartY=14.1416 StartZ=0 EndX=-188.136 EndY=15.2254 EndZ=0
    g4: LineSegment StartX=-187.76 StartY=13.0579 StartZ=0 EndX=-185.592 EndY=13.4346 EndZ=0
    g5: LineSegment StartX=-188.136 StartY=15.2254 StartZ=0 EndX=-185.969 EndY=15.6021 EndZ=0
    g6: LineSegment StartX=-185.969 StartY=15.6021 StartZ=0 EndX=-185.592 EndY=13.4346 EndZ=0
    g7: LineSegment StartX=-187.486 StartY=11.4815 StartZ=0 EndX=-189.062 EndY=11.2075 EndZ=0
    g8: LineSegment StartX=-188.41 StartY=16.8018 StartZ=0 EndX=-189.987 EndY=16.5278 EndZ=0
    g9: LineSegment StartX=-189.987 StartY=16.5278 StartZ=0 EndX=-189.062 EndY=11.2075 EndZ=0
    g10: LineSegment StartX=-187.486 StartY=11.4815 StartZ=0 EndX=-185.318 EndY=11.8582 EndZ=0
    g11: LineSegment StartX=-188.41 StartY=16.8018 StartZ=0 EndX=-186.243 EndY=17.1785 EndZ=0
    g12: LineSegment StartX=-184.393 StartY=15.8761 StartZ=0 EndX=-184.016 EndY=13.7086 EndZ=0
    g13: ArcOfCircle CenterX=-185.969 CenterY=15.6021 CenterZ=0 NormalX=0 NormalY=0 NormalZ=1 AngleXU=0 Radius=1.6 StartAngle=0.172085 EndAngle=1.74288
    g14: GeomPoint [constr] X=-184.667 Y=17.4525 Z=0
    g15: ArcOfCircle CenterX=-185.592 CenterY=13.4346 CenterZ=0 NormalX=0 NormalY=0 NormalZ=1 AngleXU=0 Radius=1.6 StartAngle=4.88447 EndAngle=6.45527
    g16: GeomPoint [constr] X=-183.742 Y=12.1322 Z=0
  constraints (43):
    c: Tangent(g1,g0) = -1.5708
    c: Distance(g0) = 2.7
    c: Equal(g1,g0)
    c: Tangent(g1,g-5)
    c: Coincident(g2,g0)
    c: Coincident(g3,g0)
    c: Distance(g2) = 1.1
    c: Equal(g3,g2)
    c: PointOnObject(g3,g2)
    c: Coincident(g4,g2)
    c: Coincident(g5,g3)
    c: Distance(g4) = 2.2
    c: Equal(g4,g5)
    c: Perpendicular(g1,g4)
    c: Perpendicular(g0,g5)
    c: Coincident(g6,g5)
    c: Coincident(g6,g4)
    c: Coincident(g7,g1)
    c: Coincident(g8,g0)
    c: Distance(g7) = 1.6
    c: Equal(g7,g8)
    c: Perpendicular(g1,g7)
    c: Perpendicular(g8,g0)
    c: Coincident(g9,g8)
    c: Coincident(g9,g7)
    c: Coincident(g10,g1)
    c: Coincident(g11,g0)
    c: Distance(g10,g16) = 3.8
    c: Perpendicular(g1,g10)
    c: Perpendicular(g1,g11)
    c: DistanceY(g0,g-4) = 3.8
    c: PointOnObject(g14,g12)
    c: PointOnObject(g14,g11)
    c: Tangent(g12,g13) = 1.5708
    c: Tangent(g11,g13) = 1.5708
    c: PointOnObject(g16,g12)
    c: PointOnObject(g16,g10)
    c: Tangent(g12,g15) = 1.5708
    c: Tangent(g10,g15) = -1.5708
    c: Equal(g13,g15)
    c: Coincident(g13,g5)
    c: Parallel(g2,g0)
    c: PointOnObject(g0,g-5)
FEATURE [Part::Extrusion] Extrude079  label="Extrude079 - fermi_nuovo_driver_alto"
  Base = -> Sketch139
  Dir = (0,-1,2e-16)
  DirMode = 2
  FaceMakerClass = Part::FaceMakerBullseye
  FaceMakerMode = 3
  InnerWireTaper = 1
  LengthFwd = 25.2
  LengthRev = 0
  Solid = true
  Symmetric = true
FEATURE [Sketcher::SketchObject] Sketch140  label="scavo_diodo_nuovo_driver_alto"
  ArcFitTolerance = 1e-06
  AttachmentSupport = -> [XZ_Plane]
  ExternalGeometry = -> [Sketch138]
  ExternalTypes = [0]
  FullyConstrained = true
  MakeInternals = false
  MapMode = 5
  Placement = pos=(0,0,0) rot=(1,0,0;1.5708rad)
  _ExternalGeoVersion = 0
  sketch-geometry (4):
    g0: LineSegment StartX=-190.909 StartY=17.9416 StartZ=0 EndX=-189.742 EndY=4.79337 EndZ=0
    g1: LineSegment StartX=-193.898 StartY=17.6763 StartZ=0 EndX=-192.73 EndY=4.52805 EndZ=0
    g2: LineSegment StartX=-190.909 StartY=17.9416 StartZ=0 EndX=-193.898 EndY=17.6763 EndZ=0
    g3: LineSegment StartX=-192.73 StartY=4.52805 StartZ=0 EndX=-189.742 EndY=4.79337 EndZ=0
  constraints (11):
    c: Equal(g0,g-3)
    c: Parallel(g0,g-3)
    c: Equal(g1,g-3)
    c: Parallel(g1,g-3)
    c: Coincident(g2,g0)
    c: Distance(g2) = 3
    c: Perpendicular(g0,g2)
    c: Coincident(g1,g2)
    c: Coincident(g3,g1)
    c: Coincident(g3,g0)
    c: Coincident(g0,g-3)
FEATURE [Part::Extrusion] Extrude080  label="Extrude080 - scavo_diodo_nuovo_driver_alto"
  Base = -> Sketch140
  Dir = (0,-1,2e-16)
  DirMode = 2
  FaceMakerClass = Part::FaceMakerBullseye
  FaceMakerMode = 3
  InnerWireTaper = 1
  LengthFwd = 4
  LengthRev = 0
  Placement = pos=(0,7.8,0) rot=(0,0,1;0rad)
  Solid = true
  Symmetric = false
FEATURE [Part::MultiFuse] Fusion001
  Refine = true
  Shapes = -> [Cut043,Extrude079]
FEATURE [Part::Cut] Cut044
  Base = -> Fusion001
  Refine = true
  Tool = -> Extrude078
FEATURE [Part::Cut] Cut045
  Base = -> Cut044
  Refine = true
  Tool = -> Extrude080
FEATURE [Sketcher::SketchObject] Sketch141  label="fermi_nuovo_driver"
  ArcFitTolerance = 1e-06
  AttachmentSupport = -> [XZ_Plane]
  ExternalGeometry = -> [Sketch,Sketch137]
  ExternalTypes = [0]
  FullyConstrained = true
  MakeInternals = false
  MapMode = 5
  Placement = pos=(0,0,0) rot=(1,0,0;1.5708rad)
  _ExternalGeoVersion = 0
  sketch-geometry (17):
    g0: LineSegment [constr] StartX=-156.99 StartY=-23.6885 StartZ=0 EndX=-160.034 EndY=-22.6997 EndZ=0
    g1: LineSegment [constr] StartX=-160.034 StartY=-22.6997 StartZ=0 EndX=-162.815 EndY=-31.2592 EndZ=0
    g2: LineSegment [constr] StartX=-162.815 StartY=-31.2592 StartZ=0 EndX=-164.484 EndY=-36.3949 EndZ=0
    g3: LineSegment StartX=-164.484 StartY=-36.3949 StartZ=0 EndX=-166.576 EndY=-35.715 EndZ=0
    g4: LineSegment StartX=-167.603 StartY=-33.6989 StartZ=0 EndX=-166.923 EndY=-31.6066 EndZ=0
    g5: LineSegment StartX=-164.907 StartY=-30.5793 StartZ=0 EndX=-161.293 EndY=-31.7536 EndZ=0
    g6: LineSegment StartX=-161.293 StartY=-31.7536 StartZ=0 EndX=-162.962 EndY=-36.8893 EndZ=0
    g7: LineSegment StartX=-164.484 StartY=-36.3949 StartZ=0 EndX=-162.962 EndY=-36.8893 EndZ=0
    g8: LineSegment StartX=-165.402 StartY=-32.101 StartZ=0 EndX=-166.082 EndY=-34.1933 EndZ=0
    g9: LineSegment StartX=-166.082 StartY=-34.1933 StartZ=0 EndX=-163.989 EndY=-34.8732 EndZ=0
    g10: LineSegment StartX=-163.989 StartY=-34.8732 StartZ=0 EndX=-163.309 EndY=-32.7809 EndZ=0
    g11: LineSegment StartX=-163.309 StartY=-32.7809 StartZ=0 EndX=-165.402 EndY=-32.101 EndZ=0
    g12: ArcOfCircle CenterX=-165.402 CenterY=-32.101 CenterZ=0 NormalX=0 NormalY=0 NormalZ=1 AngleXU=0 Radius=1.6 StartAngle=1.25664 EndAngle=2.82743
    g13: GeomPoint [constr] X=-166.429 Y=-30.0849 Z=0
    g14: ArcOfCircle CenterX=-166.082 CenterY=-34.1933 CenterZ=0 NormalX=0 NormalY=0 NormalZ=1 AngleXU=0 Radius=1.6 StartAngle=2.82743 EndAngle=4.39823
    g15: GeomPoint [constr] X=-168.098 Y=-35.2206 Z=0
    g16: LineSegment [constr] StartX=-160.034 StartY=-22.6997 StartZ=0 EndX=-164.854 EndY=-37.5361 EndZ=0
  constraints (44):
    c: Coincident(g0,g-4)
    c: PointOnObject(g0,g-3)
    c: Parallel(g0,g-4)
    c: Coincident(g1,g0)
    c: Parallel(g1,g-3)
    c: Coincident(g2,g1)
    c: Distance(g2) = 5.4
    c: Coincident(g3,g2)
    c: Parallel(g2,g-3)
    c: Distance(g15,g13) = 5.4
    c: Perpendicular(g3,g2)
    c: Parallel(g4,g2)
    c: Distance(g5,g13) = 5.4
    c: Distance(g3,g15) = 3.8
    c: Perpendicular(g4,g5)
    c: Coincident(g6,g5)
    c: Distance(g6) = 5.4
    c: Parallel(g6,g4)
    c: Coincident(g7,g2)
    c: Coincident(g7,g6)
    c: Coincident(g8,g9)
    c: Coincident(g9,g10)
    c: Coincident(g10,g11)
    c: Coincident(g11,g8)
    c: Distance(g8,g10) = 2.2
    c: Distance(g9,g11) = 2.2
    c: Perpendicular(g11,g8)
    c: Equal(g8,g10)
    c: Equal(g11,g9)
    c: Tangent(g10,g2)
    c: Distance(g10,g1) = 1.6
    c: PointOnObject(g13,g4)
    c: PointOnObject(g13,g5)
    c: Tangent(g4,g12) = 1.5708
    c: Tangent(g5,g12) = 1.5708
    c: PointOnObject(g15,g4)
    c: Tangent(g4,g14) = 1.5708
    c: Tangent(g3,g14) = 1.5708
    c: Equal(g14,g12)
    c: Coincident(g12,g8)
    c: Coincident(g16,g0)
    c: PointOnObject(g16,g-5)
    c: Parallel(g16,g-3)
    c: Distance(g16,g2) = 1.2
FEATURE [Part::Extrusion] Extrude081  label="Extrude081 - fermi_nuovo_driver"
  Base = -> Sketch141
  Dir = (0,-1,2e-16)
  DirMode = 2
  FaceMakerClass = Part::FaceMakerBullseye
  FaceMakerMode = 3
  InnerWireTaper = 1
  LengthFwd = 25.2
  LengthRev = 0
  Solid = true
  Symmetric = true
FEATURE [Part::MultiFuse] Fusion002
  Refine = true
  Shapes = -> [Cut045,Extrude081]
FEATURE [Part::Cut] Cut046
  Base = -> Fusion002
  Refine = true
  Tool = -> Extrude077
FEATURE [Sketcher::SketchObject] Sketch142  label="fermi_rele"
  ArcFitTolerance = 1e-06
  AttachmentSupport = -> [XZ_Plane]
  ExternalGeometry = -> [Sketch,Sketch136]
  ExternalTypes = [0]
  FullyConstrained = true
  MakeInternals = false
  MapMode = 5
  Placement = pos=(0,0,0) rot=(1,0,0;1.5708rad)
  _ExternalGeoVersion = 0
  sketch-geometry (15):
    g0: LineSegment StartX=-176.936 StartY=-62.4208 StartZ=0 EndX=-177.615 EndY=-64.5131 EndZ=0
    g1: LineSegment StartX=-174.919 StartY=-61.3936 StartZ=0 EndX=-171.305 EndY=-62.5678 EndZ=0
    g2: LineSegment StartX=-171.305 StartY=-62.5678 StartZ=0 EndX=-172.974 EndY=-67.7035 EndZ=0
    g3: LineSegment StartX=-176.588 StartY=-66.5293 StartZ=0 EndX=-172.974 EndY=-67.7035 EndZ=0
    g4: LineSegment StartX=-175.414 StartY=-62.9152 StartZ=0 EndX=-173.322 EndY=-63.5951 EndZ=0
    g5: LineSegment StartX=-175.414 StartY=-62.9152 StartZ=0 EndX=-176.094 EndY=-65.0076 EndZ=0
    g6: LineSegment StartX=-173.322 StartY=-63.5951 StartZ=0 EndX=-174.001 EndY=-65.6874 EndZ=0
    g7: LineSegment StartX=-176.094 StartY=-65.0076 StartZ=0 EndX=-174.001 EndY=-65.6874 EndZ=0
    g8: LineSegment [constr] StartX=-173.322 StartY=-63.5951 StartZ=0 EndX=-172.827 EndY=-62.0734 EndZ=0
    g9: LineSegment [constr] StartX=-173.322 StartY=-63.5951 StartZ=0 EndX=-171.8 EndY=-64.0895 EndZ=0
    g10: LineSegment [constr] StartX=-170.364 StartY=-61.612 StartZ=0 EndX=-172.456 EndY=-60.9321 EndZ=0
    g11: ArcOfCircle CenterX=-175.414 CenterY=-62.9152 CenterZ=0 NormalX=0 NormalY=0 NormalZ=1 AngleXU=0 Radius=1.6 StartAngle=1.25664 EndAngle=2.82743
    g12: GeomPoint [constr] X=-176.441 Y=-60.8991 Z=0
    g13: ArcOfCircle CenterX=-176.094 CenterY=-65.0076 CenterZ=0 NormalX=0 NormalY=0 NormalZ=1 AngleXU=0 Radius=1.6 StartAngle=2.82743 EndAngle=4.39823
    g14: GeomPoint [constr] X=-178.11 Y=-66.0348 Z=0
  constraints (39):
    c: Distance(g14,g12) = 5.4
    c: Distance(g1,g12) = 5.4
    c: Perpendicular(g1,g0)
    c: Coincident(g2,g1)
    c: Parallel(g2,g0)
    c: Coincident(g3,g2)
    c: Parallel(g2,g-3)
    c: Coincident(g5,g4)
    c: Distance(g5) = 2.2
    c: Distance(g4) = 2.2
    c: Perpendicular(g4,g5)
    c: Coincident(g6,g4)
    c: Equal(g6,g5)
    c: Parallel(g6,g5)
    c: Coincident(g7,g5)
    c: Coincident(g7,g6)
    c: Coincident(g8,g4)
    c: Coincident(g9,g4)
    c: Distance(g8) = 1.6
    c: Distance(g9) = 1.6
    c: Parallel(g8,g6)
    c: Parallel(g9,g4)
    c: PointOnObject(g8,g1)
    c: PointOnObject(g9,g2)
    c: Coincident(g10,g-4)
    c: Parallel(g10,g-4)
    c: PointOnObject(g10,g-3)
    c: Tangent(g6,g-3) = 1.5708
    c: Distance(g4,g10) = 2.8
    c: PointOnObject(g12,g1)
    c: Tangent(g1,g11) = 1.5708
    c: Tangent(g0,g11) = -1.5708
    c: PointOnObject(g14,g3)
    c: PointOnObject(g14,g0)
    c: Tangent(g3,g13) = -1.5708
    c: Tangent(g0,g13) = -1.5708
    c: Equal(g11,g13)
    c: Coincident(g11,g4)
    c: Parallel(g3,g1)
FEATURE [Part::Extrusion] Extrude082  label="Extrude082 - fermi_rele"
  Base = -> Sketch142
  Dir = (0,-1,2e-16)
  DirMode = 2
  FaceMakerClass = Part::FaceMakerBullseye
  FaceMakerMode = 3
  InnerWireTaper = 1
  LengthFwd = 25.2
  LengthRev = 0
  Solid = true
  Symmetric = true
FEATURE [Part::MultiFuse] Fusion003
  Refine = true
  Shapes = -> [Cut046,Extrude082]
FEATURE [Part::Cut] Cut047
  Base = -> Fusion003
  Refine = true
  Tool = -> Extrude076
FEATURE [Sketcher::SketchObject] Sketch143  label="foro_passaggio_cavi_led_batteria"
  ArcFitTolerance = 1e-06
  AttachmentSupport = -> [XZ_Plane]
  ExternalGeometry = -> [Sketch,Sketch042,Sketch036]
  ExternalTypes = [0]
  FullyConstrained = true
  MakeInternals = false
  MapMode = 5
  Placement = pos=(0,0,0) rot=(1,0,0;1.5708rad)
  _ExternalGeoVersion = 0
  sketch-geometry (4):
    g0: LineSegment StartX=-207.775 StartY=-41.3701 StartZ=0 EndX=-213.607 EndY=-53.8767 EndZ=0
    g1: LineSegment StartX=-213.607 StartY=-53.8767 StartZ=0 EndX=-211.843 EndY=-59.5559 EndZ=0
    g2: LineSegment StartX=-207.775 StartY=-41.3701 StartZ=0 EndX=-207.775 EndY=-50.8316 EndZ=0
    g3: LineSegment StartX=-207.775 StartY=-50.8316 StartZ=0 EndX=-211.843 EndY=-59.5559 EndZ=0
  constraints (9):
    c: Coincident(g0,g-3)
    c: PointOnObject(g1,g-6)
    c: Coincident(g1,g0)
    c: Coincident(g2,g0)
    c: Coincident(g2,g-7)
    c: Coincident(g3,g2)
    c: Parallel(g3,g0)
    c: Coincident(g3,g1)
    c: Coincident(g0,g-5)
FEATURE [Part::Extrusion] Extrude083  label="Extrude083 - foro_passaggio_cavi_led_batteria"
  Base = -> Sketch143
  Dir = (0,-1,2e-16)
  DirMode = 2
  FaceMakerClass = Part::FaceMakerBullseye
  FaceMakerMode = 3
  InnerWireTaper = 1
  LengthFwd = 6
  LengthRev = 0
  Placement = pos=(0,1.2,0) rot=(0,0,1;0rad)
  Solid = true
  Symmetric = true
FEATURE [Part::Cut] Cut048
  Base = -> Cut047
  Refine = true
  Tool = -> Extrude083
FEATURE [Sketcher::SketchObject] Sketch144  label="foro_areazione_alimentatore"
  ArcFitTolerance = 1e-06
  AttachmentSupport = -> [XZ_Plane]
  ExternalGeometry = -> [Sketch036]
  ExternalTypes = [0]
  FullyConstrained = true
  MakeInternals = false
  MapMode = 5
  Placement = pos=(0,0,0) rot=(1,0,0;1.5708rad)
  _ExternalGeoVersion = 0
  sketch-geometry (4):
    g0: LineSegment StartX=-211.843 StartY=-60.3701 StartZ=0 EndX=-207.775 EndY=-60.3701 EndZ=0
    g1: LineSegment StartX=-207.775 StartY=-60.3701 StartZ=0 EndX=-207.775 EndY=-70.3701 EndZ=0
    g2: LineSegment StartX=-211.843 StartY=-60.3701 StartZ=0 EndX=-211.843 EndY=-70.3701 EndZ=0
    g3: LineSegment StartX=-207.775 StartY=-70.3701 StartZ=0 EndX=-211.843 EndY=-70.3701 EndZ=0
  constraints (11):
    c: Horizontal(g0)
    c: Distance(g1) = 10
    c: Coincident(g1,g0)
    c: Tangent(g1,g-3)
    c: PointOnObject(g0,g-4)
    c: Coincident(g2,g0)
    c: PointOnObject(g2,g-4)
    c: Coincident(g3,g1)
    c: Horizontal(g3)
    c: Coincident(g3,g2)
    c: DistanceY(g0,g-3) = 19
FEATURE [Part::Extrusion] Extrude084  label="Extrude084 - foro_areazione_alimentatore"
  Base = -> Sketch144
  Dir = (0,-1,2e-16)
  DirMode = 2
  FaceMakerClass = Part::FaceMakerBullseye
  FaceMakerMode = 3
  InnerWireTaper = 1
  LengthFwd = 10
  LengthRev = 0
  Solid = true
  Symmetric = true
FEATURE [Part::Cut] Cut049
  Base = -> Cut048
  Refine = true
  Tool = -> Extrude084
FEATURE [Sketcher::SketchObject] Sketch145  label="foro_per_condesatore"
  ArcFitTolerance = 1e-06
  AttachmentSupport = -> [XZ_Plane]
  ExternalGeometry = -> [Sketch138]
  ExternalTypes = [0]
  FullyConstrained = true
  MakeInternals = false
  MapMode = 5
  Placement = pos=(0,0,0) rot=(1,0,0;1.5708rad)
  _ExternalGeoVersion = 0
  sketch-geometry (1):
    g0: Circle CenterX=-179.742 CenterY=9.59337 CenterZ=0 NormalX=0 NormalY=0 NormalZ=1 AngleXU=0 Radius=5.4
  constraints (3):
    c: Diameter(g0) = 10.8
    c: DistanceX(g-3,g0) = 10
    c: DistanceY(g-3,g0) = 4.8
FEATURE [Part::Extrusion] Extrude085  label="Extrude085 - foro_per_condesatore"
  Base = -> Sketch145
  Dir = (0,-1,2e-16)
  DirMode = 2
  FaceMakerClass = Part::FaceMakerBullseye
  FaceMakerMode = 3
  InnerWireTaper = 1
  LengthFwd = 25.2
  LengthRev = 0
  Solid = true
  Symmetric = true
FEATURE [Part::Cut] Cut050
  Base = -> Cut049
  Refine = true
  Tool = -> Extrude085
FEATURE [Sketcher::SketchObject] Sketch146  label="scavo_pulsante_6x6_per_led_batteria"
  ArcFitTolerance = 1e-06
  AttachmentSupport = -> [XZ_Plane]
  ExternalGeometry = -> [Sketch016]
  ExternalTypes = [0]
  FullyConstrained = true
  MakeInternals = false
  MapMode = 5
  Placement = pos=(0,0,0) rot=(1,0,0;1.5708rad)
  _ExternalGeoVersion = 0
  sketch-geometry (5):
    g0: LineSegment StartX=-216.643 StartY=-65.8316 StartZ=0 EndX=-216.643 EndY=-72.8316 EndZ=0
    g1: LineSegment StartX=-216.643 StartY=-72.8316 StartZ=0 EndX=-210.243 EndY=-72.8316 EndZ=0
    g2: LineSegment StartX=-210.243 StartY=-72.8316 StartZ=0 EndX=-210.243 EndY=-65.8316 EndZ=0
    g3: LineSegment StartX=-210.243 StartY=-65.8316 StartZ=0 EndX=-216.643 EndY=-65.8316 EndZ=0
    g4: GeomPoint [constr] X=-213.443 Y=-69.3316 Z=0
  constraints (13):
    c: Coincident(g0,g1)
    c: Coincident(g1,g2)
    c: Coincident(g2,g3)
    c: Coincident(g3,g0)
    c: Vertical(g0)
    c: Vertical(g2)
    c: Horizontal(g1)
    c: Horizontal(g3)
    c: Distance(g0,g2) = 6.4
    c: Distance(g1,g3) = 7
    c: Tangent(g1,g-3)
    c: Symmetric(g0,g2,g4)
    c: Vertical(g-3,g4)
FEATURE [Part::Extrusion] Extrude086  label="Extrude086 - scavo_pulsante_6x6_per_led_batteria"
  Base = -> Sketch146
  Dir = (0,-1,2e-16)
  DirMode = 2
  FaceMakerClass = Part::FaceMakerBullseye
  FaceMakerMode = 3
  InnerWireTaper = 1
  LengthFwd = 4
  LengthRev = 0
  Placement = pos=(0,12.6,0) rot=(0,0,1;0rad)
  Solid = true
  Symmetric = false
FEATURE [Sketcher::SketchObject] Sketch147  label="scavo_led_stato_batteria"
  ArcFitTolerance = 1e-06
  AttachmentSupport = -> [XZ_Plane]
  ExternalGeometry = -> [Sketch016]
  ExternalTypes = [0]
  FullyConstrained = true
  MakeInternals = false
  MapMode = 5
  Placement = pos=(0,0,0) rot=(1,0,0;1.5708rad)
  _ExternalGeoVersion = 0
  sketch-geometry (5):
    g0: LineSegment StartX=-215.843 StartY=-56.2316 StartZ=0 EndX=-215.843 EndY=-65.4316 EndZ=0
    g1: LineSegment StartX=-215.843 StartY=-65.4316 StartZ=0 EndX=-211.043 EndY=-65.4316 EndZ=0
    g2: LineSegment StartX=-211.043 StartY=-65.4316 StartZ=0 EndX=-211.043 EndY=-56.2316 EndZ=0
    g3: LineSegment StartX=-211.043 StartY=-56.2316 StartZ=0 EndX=-215.843 EndY=-56.2316 EndZ=0
    g4: GeomPoint [constr] X=-213.443 Y=-60.8316 Z=0
  constraints (13):
    c: Coincident(g0,g1)
    c: Coincident(g1,g2)
    c: Coincident(g2,g3)
    c: Coincident(g3,g0)
    c: Distance(g0,g2) = 4.8
    c: Distance(g1,g3) = 9.2
    c: Equal(g0,g2)
    c: Equal(g1,g3)
    c: Perpendicular(g3,g0)
    c: DistanceY(g-3,g0) = 11.4
    c: Vertical(g2)
    c: Symmetric(g0,g2,g4)
    c: Vertical(g4,g-3)
FEATURE [Part::Extrusion] Extrude087  label="Extrude087 - scavo_led_stato_batteria"
  Base = -> Sketch147
  Dir = (0,-1,2e-16)
  DirMode = 2
  FaceMakerClass = Part::FaceMakerBullseye
  FaceMakerMode = 3
  InnerWireTaper = 1
  LengthFwd = 2.2
  LengthRev = 0
  Placement = pos=(0,12.6,0) rot=(0,0,1;0rad)
  Solid = true
  Symmetric = false
FEATURE [Sketcher::SketchObject] Sketch148
  ArcFitTolerance = 1e-06
  AttachmentSupport = -> [Pad016]
  ExternalGeometry = -> [Pad016]
  ExternalTypes = [0]
  FullyConstrained = true
  MakeInternals = false
  MapMode = 5
  Placement = pos=(0,-1.77e-14,-80.4316) rot=(1,0,0;3.14159rad)
  _ExternalGeoVersion = 0
  sketch-geometry (8):
    g0: LineSegment StartX=-176.685 StartY=3.6 StartZ=0 EndX=-186.685 EndY=3.6 EndZ=0
    g1: LineSegment StartX=-176.685 StartY=3.6 StartZ=0 EndX=-176.685 EndY=3.162e-13 EndZ=0
    g2: LineSegment [constr] StartX=-186.685 StartY=3.6 StartZ=0 EndX=-186.685 EndY=3.162e-13 EndZ=0
    g3: ArcOfEllipse CenterX=-186.685 CenterY=3.162e-13 CenterZ=0 NormalX=0 NormalY=0 NormalZ=1 MajorRadius=10 MinorRadius=3.6 AngleXU=0 StartAngle=0 EndAngle=1.5708
    g4: LineSegment [constr] StartX=-176.685 StartY=3.162e-13 StartZ=0 EndX=-196.685 EndY=3.162e-13 EndZ=0
    g5: LineSegment [constr] StartX=-186.685 StartY=3.6 StartZ=0 EndX=-186.685 EndY=-3.6 EndZ=0
    g6: GeomPoint [constr] X=-177.356 Y=3.162e-13 Z=0
    g7: GeomPoint [constr] X=-196.015 Y=3.161e-13 Z=0
  constraints (13):
    c: Distance(g0) = 10
    c: Coincident(g0,g-5)
    c: PointOnObject(g0,g-3)
    c: Coincident(g1,g0)
    c: Coincident(g1,g-5)
    c: Coincident(g2,g0)
    c: Vertical(g2)
    c: PointOnObject(g2,g-4)
    c: InternalAlignment(g4-g7 -> g3) x4
    c: Coincident(g3,g2)
    c: Coincident(g3,g0)
    c: Coincident(g3,g1)
    c: Horizontal(g4)
FEATURE [PartDesign::SubtractivePipe] SubtractivePipe004
  AuxiliaryCurvilinear = true
  AuxiliarySpineTangent = false
  BaseFeature = -> Pad016
  Binormal = (0,0,0)
  Mode = 0
  Profile = -> Sketch148
  Refine = true
  Spine = -> Pad016 [Edge161]
  SpineTangent = false
  Suppressed = false
  Transformation = 0
  Transition = 0
FEATURE [Sketcher::SketchObject] Sketch149
  ArcFitTolerance = 1e-06
  AttachmentSupport = -> [Pad016]
  ExternalGeometry = -> [Pad016]
  ExternalTypes = [0]
  FullyConstrained = true
  MakeInternals = false
  MapMode = 5
  Placement = pos=(0,-1.77e-14,-80.4316) rot=(1,0,0;3.14159rad)
  _ExternalGeoVersion = 0
  sketch-geometry (8):
    g0: LineSegment StartX=-215.932 StartY=3.6 StartZ=0 EndX=-205.932 EndY=3.6 EndZ=0
    g1: LineSegment StartX=-215.932 StartY=3.6 StartZ=0 EndX=-215.932 EndY=3.157e-13 EndZ=0
    g2: LineSegment [constr] StartX=-205.932 StartY=3.6 StartZ=0 EndX=-205.932 EndY=3.162e-13 EndZ=0
    g3: ArcOfEllipse CenterX=-205.932 CenterY=3.162e-13 CenterZ=0 NormalX=0 NormalY=0 NormalZ=1 MajorRadius=10 MinorRadius=3.6 AngleXU=-3.14159 StartAngle=4.71239 EndAngle=6.28319
    g4: LineSegment [constr] StartX=-215.932 StartY=3.162e-13 StartZ=0 EndX=-195.932 EndY=3.162e-13 EndZ=0
    g5: LineSegment [constr] StartX=-205.932 StartY=-3.6 StartZ=0 EndX=-205.932 EndY=3.6 EndZ=0
    g6: GeomPoint [constr] X=-215.262 Y=3.151e-13 Z=0
    g7: GeomPoint [constr] X=-196.602 Y=3.163e-13 Z=0
  constraints (13):
    c: Distance(g0) = 10
    c: Coincident(g0,g-5)
    c: PointOnObject(g0,g-5)
    c: Coincident(g1,g0)
    c: Coincident(g1,g-4)
    c: Coincident(g2,g0)
    c: Vertical(g2)
    c: PointOnObject(g2,g-3)
    c: InternalAlignment(g4-g7 -> g3) x4
    c: Coincident(g3,g2)
    c: Coincident(g3,g0)
    c: Coincident(g3,g1)
    c: Horizontal(g4)
FEATURE [PartDesign::SubtractivePipe] SubtractivePipe005
  AuxiliaryCurvilinear = true
  AuxiliarySpineTangent = false
  BaseFeature = -> SubtractivePipe004
  Binormal = (0,0,0)
  Mode = 0
  Profile = -> Sketch149
  Refine = true
  Spine = -> Pad016 [Edge203,Edge210,Edge256]
  SpineTangent = false
  Suppressed = false
  Transformation = 0
  Transition = 0
FEATURE [PartDesign::SubtractiveLoft] SubtractiveLoft002
  BaseFeature = -> SubtractivePipe005
  Closed = false
  Profile = -> Sketch129
  Refine = true
  Ruled = false
  Sections = -> [Sketch130]
  Suppressed = false
FEATURE [PartDesign::SubtractiveLoft] SubtractiveLoft003
  BaseFeature = -> SubtractiveLoft002
  Closed = false
  Profile = -> Clone2D001
  Refine = true
  Ruled = false
  Sections = -> [Sketch131]
  Suppressed = false
FEATURE [PartDesign::Chamfer] Chamfer010
  Angle = 45
  Base = -> SubtractiveLoft003 [Edge205,Edge206,Edge204,Edge203,Edge197]
  BaseFeature = -> SubtractiveLoft003
  ChamferType = 0
  FlipDirection = false
  Refine = true
  Size = 1.5
  Size2 = 1
  SupportTransform = false
  Suppressed = false
  UseAllEdges = false
FEATURE [PartDesign::Chamfer] Chamfer011
  Angle = 45
  Base = -> Chamfer010 [Edge15]
  BaseFeature = -> Chamfer010
  ChamferType = 0
  FlipDirection = false
  Refine = true
  Size = 1.6
  Size2 = 1
  SupportTransform = false
  Suppressed = false
  UseAllEdges = false
FEATURE [PartDesign::Chamfer] Chamfer012
  Angle = 45
  Base = -> Chamfer011 [Edge10]
  BaseFeature = -> Chamfer011
  ChamferType = 0
  FlipDirection = false
  Refine = true
  Size = 3.5
  Size2 = 1
  SupportTransform = false
  Suppressed = false
  UseAllEdges = false
FEATURE [PartDesign::Chamfer] Chamfer013
  Angle = 45
  Base = -> Chamfer012 [Edge94]
  BaseFeature = -> Chamfer012
  ChamferType = 0
  FlipDirection = false
  Refine = true
  Size = 1.9
  Size2 = 1
  SupportTransform = false
  Suppressed = false
  UseAllEdges = false
FEATURE [PartDesign::Fillet] Fillet007
  Base = -> Chamfer013 [Edge83]
  BaseFeature = -> Chamfer013
  Radius = 1.1
  Refine = true
  SupportTransform = false
  Suppressed = false
  UseAllEdges = false
FEATURE [PartDesign::Fillet] Fillet008
  Base = -> Fillet007 [Edge75]
  BaseFeature = -> Fillet007
  Radius = 1.9
  Refine = true
  SupportTransform = false
  Suppressed = false
  UseAllEdges = false
FEATURE [PartDesign::Pocket] Pocket011
  BaseFeature = -> Fillet008
  Direction = (0,1,-2e-16)
  Length = 0.8
  Length2 = 5
  Profile = -> Sketch132
  ReferenceAxis = -> Sketch132 [N_Axis]
  Refine = true
  SideType = 0
  Suppressed = false
  Type = 0
  Type2 = 0
FEATURE [PartDesign::Pocket] Pocket012
  BaseFeature = -> Pocket011
  Direction = (0,1,0)
  Length = 1
  Length2 = 5
  Profile = -> ShapeString
  ReferenceAxis = -> ShapeString [N_Axis]
  Refine = true
  SideType = 0
  Suppressed = false
  Type = 0
  Type2 = 0
FEATURE [Sketcher::SketchObject] Sketch150
  ArcFitTolerance = 1e-06
  AttachmentSupport = -> [Pad008]
  ExternalGeometry = -> [Pad008]
  ExternalTypes = [0]
  FullyConstrained = true
  MakeInternals = false
  MapMode = 5
  Placement = pos=(0,3.6,0) rot=(0,0.707107,0.707107;3.14159rad)
  _ExternalGeoVersion = 0
  sketch-geometry (7):
    g0: LineSegment [constr] StartX=210.343 StartY=-66.0316 StartZ=0 EndX=210.343 EndY=-72.8316 EndZ=0
    g1: LineSegment [constr] StartX=210.343 StartY=-72.8316 StartZ=0 EndX=216.543 EndY=-72.8316 EndZ=0
    g2: LineSegment [constr] StartX=216.543 StartY=-72.8316 StartZ=0 EndX=216.543 EndY=-66.0316 EndZ=0
    g3: LineSegment [constr] StartX=216.543 StartY=-66.0316 StartZ=0 EndX=210.343 EndY=-66.0316 EndZ=0
    g4: LineSegment [constr] StartX=210.343 StartY=-72.8316 StartZ=0 EndX=216.543 EndY=-66.0316 EndZ=0
    g5: LineSegment [constr] StartX=210.343 StartY=-66.0316 StartZ=0 EndX=213.443 EndY=-69.4316 EndZ=0
    g6: Circle CenterX=213.443 CenterY=-69.4316 CenterZ=0 NormalX=0 NormalY=0 NormalZ=1 AngleXU=0 Radius=2
  constraints (18):
    c: Coincident(g0,g1)
    c: Coincident(g1,g2)
    c: Coincident(g2,g3)
    c: Coincident(g3,g0)
    c: Vertical(g0)
    c: Vertical(g2)
    c: Horizontal(g1)
    c: Horizontal(g3)
    c: Distance(g0,g2) = 6.2
    c: Distance(g1,g3) = 6.8
    c: DistanceY(g-3,g1) = 4
    c: Coincident(g4,g0)
    c: Coincident(g4,g2)
    c: Coincident(g5,g0)
    c: Symmetric(g0,g2,g5)
    c: Diameter(g6) = 4
    c: Coincident(g6,g5)
    c: Vertical(g5,g-3)
FEATURE [Sketcher::SketchObject] Sketch151
  ArcFitTolerance = 1e-06
  AttachmentSupport = -> [Pad008]
  ExternalGeometry = -> [Pad008]
  ExternalTypes = [0]
  FullyConstrained = true
  MakeInternals = false
  MapMode = 5
  Placement = pos=(0,3.6,0) rot=(0,0.707107,0.707107;3.14159rad)
  _ExternalGeoVersion = 0
  sketch-geometry (10):
    g0: LineSegment [constr] StartX=211.143 StartY=-56.2316 StartZ=0 EndX=211.143 EndY=-65.4316 EndZ=0
    g1: LineSegment [constr] StartX=211.143 StartY=-65.4316 StartZ=0 EndX=215.743 EndY=-65.4316 EndZ=0
    g2: LineSegment [constr] StartX=215.743 StartY=-65.4316 StartZ=0 EndX=215.743 EndY=-56.2316 EndZ=0
    g3: LineSegment [constr] StartX=215.743 StartY=-56.2316 StartZ=0 EndX=211.143 EndY=-56.2316 EndZ=0
    g4: LineSegment StartX=212.243 StartY=-63.8316 StartZ=0 EndX=214.643 EndY=-63.8316 EndZ=0
    g5: LineSegment StartX=214.643 StartY=-63.8316 StartZ=0 EndX=214.643 EndY=-57.0316 EndZ=0
    g6: LineSegment StartX=214.643 StartY=-57.0316 StartZ=0 EndX=212.243 EndY=-57.0316 EndZ=0
    g7: LineSegment StartX=212.243 StartY=-57.0316 StartZ=0 EndX=212.243 EndY=-63.8316 EndZ=0
    g8: GeomPoint [constr] X=213.443 Y=-60.4316 Z=0
    g9: GeomPoint [constr] X=213.443 Y=-60.8316 Z=0
  constraints (26):
    c: Coincident(g0,g1)
    c: Coincident(g1,g2)
    c: Coincident(g2,g3)
    c: Coincident(g3,g0)
    c: Vertical(g0)
    c: Vertical(g2)
    c: Horizontal(g1)
    c: Horizontal(g3)
    c: Distance(g0,g2) = 4.6
    c: Distance(g1,g3) = 9.2
    c: DistanceY(g-3,g1) = 11.4
    c: Coincident(g4,g5)
    c: Coincident(g5,g6)
    c: Coincident(g6,g7)
    c: Coincident(g7,g4)
    c: Horizontal(g4)
    c: Horizontal(g6)
    c: Vertical(g5)
    c: Vertical(g7)
    c: Symmetric(g6,g4,g8)
    c: Distance(g5,g7) = 2.4
    c: Distance(g4,g6) = 6.8
    c: Symmetric(g2,g0,g9)
    c: Vertical(g8,g9)
    c: DistanceY(g1,g4) = 1.6
    c: Vertical(g9,g-3)
FEATURE [PartDesign::Pocket] Pocket019
  BaseFeature = -> Pocket013
  Direction = (0,-1,2e-16)
  Length = 3.6
  Length2 = 5
  Profile = -> Sketch151
  ReferenceAxis = -> Sketch151 [N_Axis]
  Refine = true
  SideType = 0
  Suppressed = false
  Type = 0
  Type2 = 0
FEATURE [PartDesign::Pocket] Pocket018
  BaseFeature = -> Pocket019
  Direction = (0,-1,2e-16)
  Length = 3.6
  Length2 = 5
  Profile = -> Sketch150
  ReferenceAxis = -> Sketch150 [N_Axis]
  Refine = true
  SideType = 0
  Suppressed = false
  Type = 0
  Type2 = 0
FEATURE [PartDesign::Point] DatumPoint
  AttacherType = Attacher::AttachEnginePoint
  AttachmentSupport = -> [Sketch150]
  MapMode = 36
  Placement = pos=(-213.443,3.6,-69.4316) rot=(0,1,0;3.14159rad)
FEATURE [PartDesign::Plane] DatumPlane002
  AttachmentSupport = -> [DatumPoint]
  Length = 265.655
  MapMode = 1
  Placement = pos=(-213.443,3.6,-69.4316) rot=(0,0,1;0rad)
  ResizeMode = 0
  Width = 72.0719
FEATURE [Sketcher::SketchObject] Sketch152
  ArcFitTolerance = 1e-06
  AttachmentSupport = -> [DatumPlane002]
  ExternalGeometry = -> [Sketch150]
  ExternalTypes = [0]
  FullyConstrained = true
  MakeInternals = false
  MapMode = 5
  Placement = pos=(-213.443,3.6,-69.4316) rot=(0,0,1;0rad)
  _ExternalGeoVersion = 0
  sketch-geometry (7):
    g0: LineSegment StartX=0 StartY=0 StartZ=0 EndX=-4 EndY=5.1e-15 EndZ=0
    g1: ArcOfEllipse CenterX=0 CenterY=0 CenterZ=0 NormalX=0 NormalY=0 NormalZ=1 MajorRadius=4 MinorRadius=3.6 AngleXU=3.14159 StartAngle=2e-16 EndAngle=1.5708
    g2: LineSegment [constr] StartX=-4 StartY=9e-16 StartZ=0 EndX=4 EndY=-9e-16 EndZ=0
    g3: LineSegment [constr] StartX=0 StartY=-3.6 StartZ=0 EndX=0 EndY=3.6 EndZ=0
    g4: GeomPoint [constr] X=-1.74356 Y=2.5e-15 Z=0
    g5: GeomPoint [constr] X=1.74356 Y=-2e-15 Z=0
    g6: LineSegment StartX=0 StartY=0 StartZ=0 EndX=-5.5e-15 EndY=-3.6 EndZ=0
  constraints (11):
    c: PointOnObject(g1,g-2)
    c: Distance(g0) = 4
    c: PointOnObject(g0,g-1)
    c: InternalAlignment(g2-g5 -> g1) x4
    c: Coincident(g1,g0)
    c: Vertical(g3)
    c: Coincident(g1,g-1)
    c: Distance(g6) = 3.6
    c: Coincident(g6,g1)
    c: Coincident(g1,g6)
    c: Coincident(g0,g1)
FEATURE [PartDesign::Groove] Groove
  Angle = 360
  Angle2 = 60
  Axis = (0,1,0)
  Base = (-213.443,3.6,-69.4316)
  BaseFeature = -> Pocket018
  Profile = -> Sketch152
  ReferenceAxis = -> Sketch152 [V_Axis]
  Refine = true
  Reversed = true
  Suppressed = false
  Type = 0
FEATURE [PartDesign::Body] Body006  label="lato SX"
  AllowCompound = false
  Group = -> [Binder,Pad019,Chamfer015,Pocket002,Sketch133,Sketch091,Pad005,Sketch092,Pocket001,Sketch093,Sketch094,Pad006,Sketch095,Pad007,Sketch096,Pad008,Sketch097,Pad009,Chamfer005,Pocket004,Sketch098,Pad010,Chamfer006,Pocket003,SubtractivePipe,SubtractivePipe001,Sketch099,Sketch106,Sketch107,Sketch108,Clone2D,Sketch109,SubtractiveLoft,SubtractiveLoft001,Sketch110,Sketch111,Sketch112,Chamfer016,Chamfer017,+15 more]
  Origin = -> Origin006
  Tip = -> Groove
FEATURE [Sketcher::SketchObject] Sketch153  label="ripieno_per_sostegno_led_batteria"
  ArcFitTolerance = 1e-06
  AttachmentSupport = -> [XZ_Plane]
  ExternalGeometry = -> [Sketch036]
  ExternalTypes = [0]
  FullyConstrained = true
  MakeInternals = false
  MapMode = 5
  Placement = pos=(0,0,0) rot=(1,0,0;1.5708rad)
  _ExternalGeoVersion = 0
  sketch-geometry (4):
    g0: LineSegment StartX=-217.343 StartY=-54.5944 StartZ=0 EndX=-217.343 EndY=-63.1944 EndZ=0
    g1: LineSegment StartX=-217.343 StartY=-63.1944 StartZ=0 EndX=-211.843 EndY=-63.1944 EndZ=0
    g2: LineSegment StartX=-211.843 StartY=-63.1944 StartZ=0 EndX=-211.843 EndY=-54.5944 EndZ=0
    g3: LineSegment StartX=-211.843 StartY=-54.5944 StartZ=0 EndX=-217.343 EndY=-54.5944 EndZ=0
  constraints (11):
    c: Coincident(g0,g1)
    c: Coincident(g1,g2)
    c: Coincident(g2,g3)
    c: Coincident(g3,g0)
    c: Vertical(g0)
    c: Horizontal(g1)
    c: Horizontal(g3)
    c: Tangent(g2,g-3)
    c: DistanceY(g2,g-3) = 4.5
    c: DistanceX(g3,g3) = 5.5
    c: DistanceY(g0,g0) = 8.6
FEATURE [Part::Extrusion] Extrude088  label="Extrude088 - ripieno_per_sostegno_led_batteria"
  Base = -> Sketch153
  Dir = (0,-1,2e-16)
  DirMode = 2
  FaceMakerClass = Part::FaceMakerBullseye
  FaceMakerMode = 3
  InnerWireTaper = 1
  LengthFwd = 4
  LengthRev = 0
  Placement = pos=(0,12.6,0) rot=(0,0,1;0rad)
  Solid = true
  Symmetric = false
FEATURE [Part::MultiFuse] Fusion004
  Refine = true
  Shapes = -> [Cut050,Extrude088]
FEATURE [Part::Cut] Cut051
  Base = -> Fusion004
  Refine = true
  Tool = -> Extrude087
FEATURE [Part::Cut] Cut052
  Base = -> Cut051
  Refine = true
  Tool = -> Extrude086
FEATURE [Sketcher::SketchObject] Sketch154
  ArcFitTolerance = 1e-06
  AttachmentSupport = -> [Pad016]
  ExternalGeometry = -> [Binder001]
  ExternalTypes = [0]
  FullyConstrained = true
  MakeInternals = false
  MapMode = 5
  Placement = pos=(0,-3.6,0) rot=(1,0,0;1.5708rad)
  _ExternalGeoVersion = 0
  sketch-geometry (25):
    g0: LineSegment StartX=-214.643 StartY=-72.4316 StartZ=0 EndX=-212.243 EndY=-72.4316 EndZ=0
    g1: LineSegment StartX=-212.243 StartY=-72.4316 StartZ=0 EndX=-212.243 EndY=-71.2316 EndZ=0
    g2: LineSegment StartX=-212.243 StartY=-71.2316 StartZ=0 EndX=-214.643 EndY=-71.2316 EndZ=0
    g3: LineSegment StartX=-214.643 StartY=-71.2316 StartZ=0 EndX=-214.643 EndY=-72.4316 EndZ=0
    g4: GeomPoint [constr] X=-213.443 Y=-71.8316 Z=0
    g5: LineSegment StartX=-214.643 StartY=-69.6316 StartZ=0 EndX=-212.243 EndY=-69.6316 EndZ=0
    g6: LineSegment StartX=-212.243 StartY=-69.6316 StartZ=0 EndX=-212.243 EndY=-68.4316 EndZ=0
    g7: LineSegment StartX=-212.243 StartY=-68.4316 StartZ=0 EndX=-214.643 EndY=-68.4316 EndZ=0
    g8: LineSegment StartX=-214.643 StartY=-68.4316 StartZ=0 EndX=-214.643 EndY=-69.6316 EndZ=0
    g9: GeomPoint [constr] X=-213.443 Y=-69.0316 Z=0
    g10: LineSegment StartX=-214.643 StartY=-66.8316 StartZ=0 EndX=-212.243 EndY=-66.8316 EndZ=0
    g11: LineSegment StartX=-212.243 StartY=-66.8316 StartZ=0 EndX=-212.243 EndY=-65.6316 EndZ=0
    g12: LineSegment StartX=-212.243 StartY=-65.6316 StartZ=0 EndX=-214.643 EndY=-65.6316 EndZ=0
    g13: LineSegment StartX=-214.643 StartY=-65.6316 StartZ=0 EndX=-214.643 EndY=-66.8316 EndZ=0
    g14: GeomPoint [constr] X=-213.443 Y=-66.2316 Z=0
    g15: LineSegment StartX=-214.643 StartY=-64.0316 StartZ=0 EndX=-212.243 EndY=-64.0316 EndZ=0
    g16: LineSegment StartX=-212.243 StartY=-64.0316 StartZ=0 EndX=-212.243 EndY=-62.8316 EndZ=0
    g17: LineSegment StartX=-212.243 StartY=-62.8316 StartZ=0 EndX=-214.643 EndY=-62.8316 EndZ=0
    g18: LineSegment StartX=-214.643 StartY=-62.8316 StartZ=0 EndX=-214.643 EndY=-64.0316 EndZ=0
    g19: GeomPoint [constr] X=-213.443 Y=-63.4316 Z=0
    g20: LineSegment StartX=-214.643 StartY=-61.2316 StartZ=0 EndX=-212.243 EndY=-61.2316 EndZ=0
    g21: LineSegment StartX=-212.243 StartY=-61.2316 StartZ=0 EndX=-212.243 EndY=-60.0316 EndZ=0
    g22: LineSegment StartX=-212.243 StartY=-60.0316 StartZ=0 EndX=-214.643 EndY=-60.0316 EndZ=0
    g23: LineSegment StartX=-214.643 StartY=-60.0316 StartZ=0 EndX=-214.643 EndY=-61.2316 EndZ=0
    g24: GeomPoint [constr] X=-213.443 Y=-60.6316 Z=0
  constraints (65):
    c: Coincident(g0,g1)
    c: Coincident(g1,g2)
    c: Coincident(g2,g3)
    c: Coincident(g3,g0)
    c: Horizontal(g0)
    c: Horizontal(g2)
    c: Vertical(g1)
    c: Vertical(g3)
    c: Symmetric(g2,g0,g4)
    c: Distance(g1,g3) = 2.4
    c: Distance(g0,g2) = 1.2
    c: Coincident(g5,g6)
    c: Coincident(g6,g7)
    c: Coincident(g7,g8)
    c: Coincident(g8,g5)
    c: Horizontal(g5)
    c: Horizontal(g7)
    c: Vertical(g6)
    c: Vertical(g8)
    c: Symmetric(g7,g5,g9)
    c: Distance(g6,g8) = 2.4
    c: Distance(g5,g7) = 1.2
    c: Coincident(g10,g11)
    c: Coincident(g11,g12)
    c: Coincident(g12,g13)
    c: Coincident(g13,g10)
    c: Horizontal(g10)
    c: Horizontal(g12)
    c: Vertical(g11)
    c: Vertical(g13)
    c: Symmetric(g12,g10,g14)
    c: Distance(g11,g13) = 2.4
    c: Distance(g10,g12) = 1.2
    c: Coincident(g15,g16)
    c: Coincident(g16,g17)
    c: Coincident(g17,g18)
    c: Coincident(g18,g15)
    c: Horizontal(g15)
    c: Horizontal(g17)
    c: Vertical(g16)
    c: Vertical(g18)
    c: Symmetric(g17,g15,g19)
    c: Distance(g16,g18) = 2.4
    c: Distance(g15,g17) = 1.2
    c: Vertical(g4,g-3)
    c: Vertical(g9,g-3)
    c: Vertical(g14,g-3)
    c: Vertical(g19,g-3)
    c: DistanceY(g-3,g4) = 5
    c: DistanceY(g4,g9) = 2.8
    c: DistanceY(g9,g14) = 2.8
    c: DistanceY(g14,g19) = 2.8
    c: Coincident(g20,g21)
    c: Coincident(g21,g22)
    c: Coincident(g22,g23)
    c: Coincident(g23,g20)
    c: Horizontal(g20)
    c: Horizontal(g22)
    c: Vertical(g21)
    c: Vertical(g23)
    c: Symmetric(g22,g20,g24)
    c: Distance(g21,g23) = 2.4
    c: Distance(g20,g22) = 1.2
    c: DistanceY(g19,g24) = 2.8
    c: Vertical(g-3,g24)
FEATURE [PartDesign::Pocket] Pocket020
  BaseFeature = -> Pocket012
  Direction = (0,1,-2e-16)
  Length = 3.6
  Length2 = 5
  Profile = -> Sketch154
  ReferenceAxis = -> Sketch154 [N_Axis]
  Refine = true
  SideType = 0
  Suppressed = false
  Type = 0
  Type2 = 0
FEATURE [PartDesign::Body] Body007  label="lato DX"
  AllowCompound = false
  Group = -> [Binder001,Sketch114,Pad011,Chamfer014,Sketch115,Pocket006,Sketch116,Pad012,Sketch117,Pocket007,Sketch118,Pad013,Sketch119,Pocket008,Pad017,Chamfer009,Pocket009,Sketch123,Sketch120,Pad014,Pad018,Chamfer008,Pocket010,Sketch121,Pad015,Sketch122,Pad016,SubtractivePipe004,SubtractivePipe005,Sketch149,Sketch148,Sketch124,Sketch125,Sketch126,Sketch129,Sketch130,Clone2D001,Sketch131,SubtractiveLoft002,+13 more]
  Origin = -> Origin007
  Tip = -> Pocket020
FEATURE [Sketcher::SketchObject] Sketch155  label="fermo per protezione batteria"
  ArcFitTolerance = 1e-06
  AttachmentSupport = -> [XZ_Plane]
  ExternalGeometry = -> [Sketch016,Sketch]
  ExternalTypes = [0]
  FullyConstrained = true
  MakeInternals = false
  MapMode = 5
  Placement = pos=(0,0,0) rot=(1,0,0;1.5708rad)
  _ExternalGeoVersion = 0
  sketch-geometry (5):
    g0: LineSegment StartX=-183.305 StartY=-76.0316 StartZ=0 EndX=-179.305 EndY=-76.0316 EndZ=0
    g1: LineSegment StartX=-179.305 StartY=-76.0316 StartZ=0 EndX=-179.305 EndY=-74.4316 EndZ=0
    g2: LineSegment StartX=-179.305 StartY=-74.4316 StartZ=0 EndX=-183.305 EndY=-74.4316 EndZ=0
    g3: LineSegment [constr] StartX=-183.305 StartY=-76.0316 StartZ=0 EndX=-183.305 EndY=-78.4316 EndZ=0
    g4: LineSegment StartX=-183.305 StartY=-74.4316 StartZ=0 EndX=-183.305 EndY=-76.0316 EndZ=0
  constraints (16):
    c: Horizontal(g0)
    c: Distance(g1) = 1.6
    c: Coincident(g1,g0)
    c: Vertical(g1)
    c: Coincident(g2,g1)
    c: Horizontal(g2)
    c: Vertical(g3)
    c: PointOnObject(g3,g-4)
    c: Horizontal(g3,g0)
    c: Tangent(g3,g-3)
    c: Vertical(g0,g-3)
    c: Coincident(g4,g2)
    c: Coincident(g4,g0)
    c: Vertical(g4)
    c: Vertical(g0,g3)
    c: DistanceY(g3,g3) = 2.4
FEATURE [Part::Extrusion] Extrude089  label="Extrude089 - fermo per protezione batteria"
  Base = -> Sketch155
  Dir = (0,-1,2e-16)
  DirMode = 2
  FaceMakerClass = Part::FaceMakerBullseye
  FaceMakerMode = 3
  InnerWireTaper = 1
  LengthFwd = 8
  LengthRev = 0
  Solid = true
  Symmetric = true
FEATURE [Sketcher::SketchObject] Sketch156  label="buco per protezione batteria"
  ArcFitTolerance = 1e-06
  AttachmentSupport = -> [XZ_Plane]
  ExternalGeometry = -> [Sketch,Sketch016]
  ExternalTypes = [0]
  FullyConstrained = true
  MakeInternals = false
  MapMode = 5
  Placement = pos=(0,0,0) rot=(1,0,0;1.5708rad)
  _ExternalGeoVersion = 0
  sketch-geometry (5):
    g0: LineSegment [constr] StartX=-183.305 StartY=-76.8316 StartZ=0 EndX=-183.305 EndY=-78.4316 EndZ=0
    g1: LineSegment StartX=-200.305 StartY=-78.4316 StartZ=0 EndX=-200.305 EndY=-80.4316 EndZ=0
    g2: LineSegment StartX=-200.305 StartY=-80.4316 StartZ=0 EndX=-198.505 EndY=-80.4316 EndZ=0
    g3: LineSegment StartX=-198.505 StartY=-80.4316 StartZ=0 EndX=-198.505 EndY=-78.4316 EndZ=0
    g4: LineSegment StartX=-198.505 StartY=-78.4316 StartZ=0 EndX=-200.305 EndY=-78.4316 EndZ=0
  constraints (15):
    c: Vertical(g0)
    c: Tangent(g0,g-4)
    c: PointOnObject(g0,g-3)
    c: Horizontal(g0,g-4)
    c: Coincident(g1,g2)
    c: Coincident(g2,g3)
    c: Coincident(g3,g4)
    c: Coincident(g4,g1)
    c: Vertical(g1)
    c: Vertical(g3)
    c: Horizontal(g2)
    c: Distance(g1,g3) = 1.8
    c: Distance(g2,g4) = 2
    c: Tangent(g4,g-3)
    c: Distance(g3,g0) = 15.2
FEATURE [Part::Extrusion] Extrude090  label="Extrude090 - buco per protezione batteria"
  Base = -> Sketch156
  Dir = (0,-1,2e-16)
  DirMode = 2
  FaceMakerClass = Part::FaceMakerBullseye
  FaceMakerMode = 3
  InnerWireTaper = 1
  LengthFwd = 4.8
  LengthRev = 0
  Solid = true
  Symmetric = true
FEATURE [Sketcher::SketchObject] Sketch157
  ArcFitTolerance = 1e-06
  AttachmentSupport = -> [XY_Plane010]
  ExternalTypes = [0]
  FullyConstrained = true
  MakeInternals = false
  MapMode = 5
  _ExternalGeoVersion = 0
  sketch-geometry (9):
    g0: LineSegment [constr] StartX=1.8 StartY=8 StartZ=0 EndX=1.8 EndY=-8 EndZ=0
    g1: LineSegment StartX=1.8 StartY=8 StartZ=0 EndX=17 EndY=8 EndZ=0
    g2: LineSegment StartX=1.8 StartY=-8 StartZ=0 EndX=17 EndY=-8 EndZ=0
    g3: LineSegment StartX=0 StartY=8 StartZ=0 EndX=0 EndY=-8 EndZ=0
    g4: LineSegment StartX=1.8 StartY=8 StartZ=0 EndX=0 EndY=8 EndZ=0
    g5: LineSegment StartX=1.8 StartY=-8 StartZ=0 EndX=0 EndY=-8 EndZ=0
    g6: LineSegment StartX=17 StartY=8 StartZ=0 EndX=17 EndY=-8 EndZ=0
    g7: Circle CenterX=8.5 CenterY=0 CenterZ=0 NormalX=0 NormalY=0 NormalZ=1 AngleXU=0 Radius=5
    g8: LineSegment [constr] StartX=17 StartY=8 StartZ=0 EndX=17 EndY=0 EndZ=0
  constraints (23):
    c: DistanceY(g0,g0) = 16
    c: Distance(g1) = 15.2
    c: Coincident(g1,g0)
    c: Horizontal(g1)
    c: Coincident(g2,g0)
    c: Horizontal(g2)
    c: Equal(g1,g2)
    c: Symmetric(g0,g0,g-1)
    c: Equal(g3,g0)
    c: Coincident(g4,g0)
    c: Horizontal(g4)
    c: DistanceX(g4,g4) = 1.8
    c: Coincident(g5,g0)
    c: Horizontal(g5)
    c: Equal(g4,g5)
    c: Coincident(g3,g4)
    c: Tangent(g3,g-2)
    c: Coincident(g6,g1)
    c: Coincident(g6,g2)
    c: Coincident(g8,g1)
    c: Symmetric(g6,g6,g8)
    c: Symmetric(g8,g-1,g7)
    c: Diameter(g7) = 10
FEATURE [PartDesign::Pad] Pad031
  Direction = (0,0,1)
  Length = 1.4
  Length2 = 10
  Profile = -> Sketch157
  ReferenceAxis = -> Sketch157 [N_Axis]
  Refine = true
  SideType = 0
  Suppressed = false
  Type = 0
  Type2 = 0
FEATURE [Sketcher::SketchObject] Sketch158
  ArcFitTolerance = 1e-06
  AttachmentSupport = -> [Pad031]
  ExternalGeometry = -> [Pad031]
  ExternalTypes = [0]
  FullyConstrained = true
  MakeInternals = false
  MapMode = 5
  Placement = pos=(0,0,1.4) rot=(0,0,1;0rad)
  _ExternalGeoVersion = 0
  sketch-geometry (4):
    g0: LineSegment StartX=0 StartY=8 StartZ=0 EndX=0 EndY=-8 EndZ=0
    g1: LineSegment StartX=0 StartY=8 StartZ=0 EndX=1.8 EndY=8 EndZ=0
    g2: LineSegment StartX=1.8 StartY=8 StartZ=0 EndX=1.8 EndY=-8 EndZ=0
    g3: LineSegment StartX=0 StartY=-8 StartZ=0 EndX=1.8 EndY=-8 EndZ=0
  constraints (10):
    c: Coincident(g0,g-3)
    c: Coincident(g0,g-4)
    c: Distance(g1) = 1.8
    c: Coincident(g1,g0)
    c: PointOnObject(g1,g-3)
    c: Coincident(g2,g1)
    c: Vertical(g2)
    c: Coincident(g3,g0)
    c: PointOnObject(g3,g-4)
    c: Coincident(g3,g2)
FEATURE [PartDesign::Pad] Pad032
  BaseFeature = -> Pad031
  Direction = (0,0,1)
  Length = 6.4
  Length2 = 10
  Profile = -> Sketch158
  ReferenceAxis = -> Sketch158 [N_Axis]
  Refine = true
  SideType = 0
  Suppressed = false
  Type = 0
  Type2 = 0
FEATURE [Sketcher::SketchObject] Sketch159
  ArcFitTolerance = 1e-06
  AttachmentSupport = -> [Pad032]
  ExternalGeometry = -> [Pad032,Pad031]
  ExternalTypes = [0]
  FullyConstrained = true
  MakeInternals = false
  MapMode = 5
  Placement = pos=(0,0,7.8) rot=(0,0,1;0rad)
  _ExternalGeoVersion = 0
  sketch-geometry (7):
    g0: LineSegment StartX=0.1 StartY=2.2 StartZ=0 EndX=0.1 EndY=-2.2 EndZ=0
    g1: LineSegment StartX=0.1 StartY=-2.2 StartZ=0 EndX=1.7 EndY=-2.2 EndZ=0
    g2: LineSegment StartX=1.7 StartY=-2.2 StartZ=0 EndX=1.7 EndY=2.2 EndZ=0
    g3: LineSegment StartX=1.7 StartY=2.2 StartZ=0 EndX=0.1 EndY=2.2 EndZ=0
    g4: GeomPoint [constr] X=0.9 Y=8 Z=0
    g5: GeomPoint [constr] X=0.9 Y=-8 Z=0
    g6: LineSegment [constr] StartX=0.9 StartY=8 StartZ=0 EndX=0.9 EndY=-8 EndZ=0
  constraints (14):
    c: Coincident(g0,g1)
    c: Coincident(g1,g2)
    c: Coincident(g2,g3)
    c: Coincident(g3,g0)
    c: Vertical(g2)
    c: Horizontal(g1)
    c: Distance(g0,g2) = 1.6
    c: Distance(g1,g3) = 4.4
    c: Symmetric(g0,g0,g-1)
    c: Symmetric(g-4,g-4,g4)
    c: Symmetric(g-3,g-5,g5)
    c: Coincident(g6,g4)
    c: Coincident(g6,g5)
    c: Symmetric(g0,g2,g6)
FEATURE [PartDesign::Pad] Pad033
  BaseFeature = -> Pad032
  Direction = (0,0,1)
  Length = 1.4
  Length2 = 10
  Profile = -> Sketch159
  ReferenceAxis = -> Sketch159 [N_Axis]
  Refine = true
  SideType = 0
  Suppressed = false
  Type = 0
  Type2 = 0
FEATURE [Part::Cut] Cut053
  Base = -> Cut052
  Refine = true
  Tool = -> Extrude089
FEATURE [Part::Cut] Cut054
  Base = -> Cut053
  Refine = true
  Tool = -> Extrude090
FEATURE [Sketcher::SketchObject] Sketch160
  ArcFitTolerance = 1e-06
  AttachmentSupport = -> [Pad033]
  ExternalGeometry = -> [Pad033]
  ExternalTypes = [0]
  FullyConstrained = true
  MakeInternals = false
  MapMode = 5
  Placement = pos=(0,0,1.4) rot=(0,0,1;0rad)
  _ExternalGeoVersion = 0
  sketch-geometry (4):
    g0: LineSegment StartX=15.6 StartY=3.7 StartZ=0 EndX=15.6 EndY=-3.7 EndZ=0
    g1: LineSegment StartX=15.6 StartY=-3.7 StartZ=0 EndX=17 EndY=-3.7 EndZ=0
    g2: LineSegment StartX=17 StartY=-3.7 StartZ=0 EndX=17 EndY=3.7 EndZ=0
    g3: LineSegment StartX=17 StartY=3.7 StartZ=0 EndX=15.6 EndY=3.7 EndZ=0
  constraints (10):
    c: Coincident(g0,g1)
    c: Coincident(g1,g2)
    c: Coincident(g2,g3)
    c: Coincident(g3,g0)
    c: Horizontal(g1)
    c: Horizontal(g3)
    c: Distance(g0,g2) = 1.4
    c: Distance(g1,g3) = 7.4
    c: Symmetric(g0,g0,g-1)
    c: Tangent(g2,g-3)
FEATURE [PartDesign::Pad] Pad034
  BaseFeature = -> Pad033
  Direction = (0,0,1)
  Length = 2.4
  Length2 = 10
  Profile = -> Sketch160
  ReferenceAxis = -> Sketch160 [N_Axis]
  Refine = true
  SideType = 0
  Suppressed = false
  Type = 0
  Type2 = 0
FEATURE [Sketcher::SketchObject] Sketch161
  ArcFitTolerance = 1e-06
  AttachmentSupport = -> [Pad034]
  ExternalGeometry = -> [Pad034]
  ExternalTypes = [0]
  FullyConstrained = true
  MakeInternals = false
  MapMode = 5
  Placement = pos=(0,0,3.8) rot=(0,0,1;0rad)
  _ExternalGeoVersion = 0
  sketch-geometry (6):
    g0: LineSegment StartX=17 StartY=3.7 StartZ=0 EndX=21 EndY=3.7 EndZ=0
    g1: LineSegment StartX=17 StartY=3.7 StartZ=0 EndX=15.6 EndY=3.7 EndZ=0
    g2: LineSegment StartX=15.6 StartY=3.7 StartZ=0 EndX=15.6 EndY=-3.7 EndZ=0
    g3: LineSegment StartX=15.6 StartY=-3.7 StartZ=0 EndX=17 EndY=-3.7 EndZ=0
    g4: LineSegment StartX=17 StartY=-3.7 StartZ=0 EndX=21 EndY=-3.7 EndZ=0
    g5: LineSegment StartX=21 StartY=3.7 StartZ=0 EndX=21 EndY=-3.7 EndZ=0
  constraints (14):
    c: Distance(g0) = 4
    c: Coincident(g0,g-4)
    c: Horizontal(g0)
    c: Coincident(g1,g0)
    c: Coincident(g1,g-3)
    c: Coincident(g2,g1)
    c: Coincident(g2,g-5)
    c: Coincident(g3,g2)
    c: Coincident(g3,g-5)
    c: Coincident(g4,g3)
    c: Horizontal(g4)
    c: Equal(g4,g0)
    c: Coincident(g5,g0)
    c: Coincident(g5,g4)
FEATURE [PartDesign::Pad] Pad035
  BaseFeature = -> Pad034
  Direction = (0,0,1)
  Length = 1.4
  Length2 = 10
  Profile = -> Sketch161
  ReferenceAxis = -> Sketch161 [N_Axis]
  Refine = true
  SideType = 0
  Suppressed = false
  Type = 0
  Type2 = 0
FEATURE [PartDesign::Body] Body010  label="Protezione_inferiore_batteria"
  AllowCompound = false
  Group = -> [Sketch157,Pad031,Sketch158,Pad032,Sketch159,Pad033,Sketch160,Pad034,Sketch161,Pad035]
  Origin = -> Origin010
  Tip = -> Pad035
FEATURE [Sketcher::SketchObject] Sketch162  label="scavo_saldature_nuovo_driver_alto"
  ArcFitTolerance = 1e-06
  AttachmentSupport = -> [XZ_Plane]
  ExternalGeometry = -> [Sketch138]
  ExternalTypes = [0]
  FullyConstrained = true
  MakeInternals = false
  MapMode = 5
  Placement = pos=(0,0,0) rot=(1,0,0;1.5708rad)
  _ExternalGeoVersion = 0
  sketch-geometry (4):
    g0: LineSegment StartX=-192.503 StartY=17.8001 StartZ=0 EndX=-191.336 EndY=4.65187 EndZ=0
    g1: LineSegment StartX=-192.503 StartY=17.8001 StartZ=0 EndX=-190.909 EndY=17.9416 EndZ=0
    g2: LineSegment StartX=-190.909 StartY=17.9416 StartZ=0 EndX=-189.742 EndY=4.79337 EndZ=0
    g3: LineSegment StartX=-189.742 StartY=4.79337 StartZ=0 EndX=-191.336 EndY=4.65187 EndZ=0
  constraints (10):
    c: Parallel(g0,g-3)
    c: Equal(g0,g-3)
    c: Coincident(g1,g0)
    c: Perpendicular(g0,g1)
    c: Coincident(g1,g-3)
    c: Coincident(g2,g1)
    c: Coincident(g2,g-3)
    c: Coincident(g3,g2)
    c: Coincident(g3,g0)
    c: Distance(g1) = 1.6
FEATURE [PartDesign::Body] Body  label="Struttura pistola"
  AllowCompound = false
  Group = -> [Sketch,Sketch002,Sketch004,DatumPlane,Sketch005,DatumPlane001,CopyCut,Sketch008,Sketch009,Sketch010,Sketch011,Sketch012,Sketch013,Sketch014,Sketch015,Sketch016,Sketch017,Sketch018,Sketch019,Sketch020,Sketch022,Sketch023,Sketch024,Sketch025,Sketch026,Sketch027,Sketch029,Sketch030,Sketch031,Sketch032,Sketch033,Sketch034,Sketch035,Sketch036,Sketch037,Sketch038,Sketch039,Sketch040,Sketch041,Sketch042,+31 more]
  Origin = -> Origin
FEATURE [Part::Extrusion] Extrude091  label="Extrude091 - scavo_saldature_nuovo_driver_alto"
  Base = -> Sketch162
  Dir = (0,-1,2e-16)
  DirMode = 2
  FaceMakerClass = Part::FaceMakerBullseye
  FaceMakerMode = 3
  InnerWireTaper = 1
  LengthFwd = 4
  LengthRev = 0
  Placement = pos=(0,-3.8,0) rot=(0,0,1;0rad)
  Solid = true
  Symmetric = false
FEATURE [Part::Cut] Cut055
  Base = -> Cut054
  Refine = true
  Tool = -> Extrude091
FEATURE [App::Point] Origin011  label="O"
  Role = Origin
FEATURE [App::Point] Origin012  label="O"
  Role = Origin
FEATURE [App::Point] Origin013  label="O"
  Role = Origin
FEATURE [App::Point] Origin014  label="O"
  Role = Origin
FEATURE [App::Point] Origin015  label="O"
  Role = Origin
FEATURE [App::Point] Origin016  label="O"
  Role = Origin
FEATURE [App::Point] Origin017  label="O"
  Role = Origin
FEATURE [App::Point] Origin018  label="O"
  Role = Origin
FEATURE [App::Point] Origin019  label="O"
  Role = Origin
FEATURE [App::Point] Origin020  label="O"
  Role = Origin
FEATURE [App::Point] Origin021  label="O"
  Role = Origin
note: 2 file-system paths scrubbed to <path> (originals preserved in the JSON sidecar)
